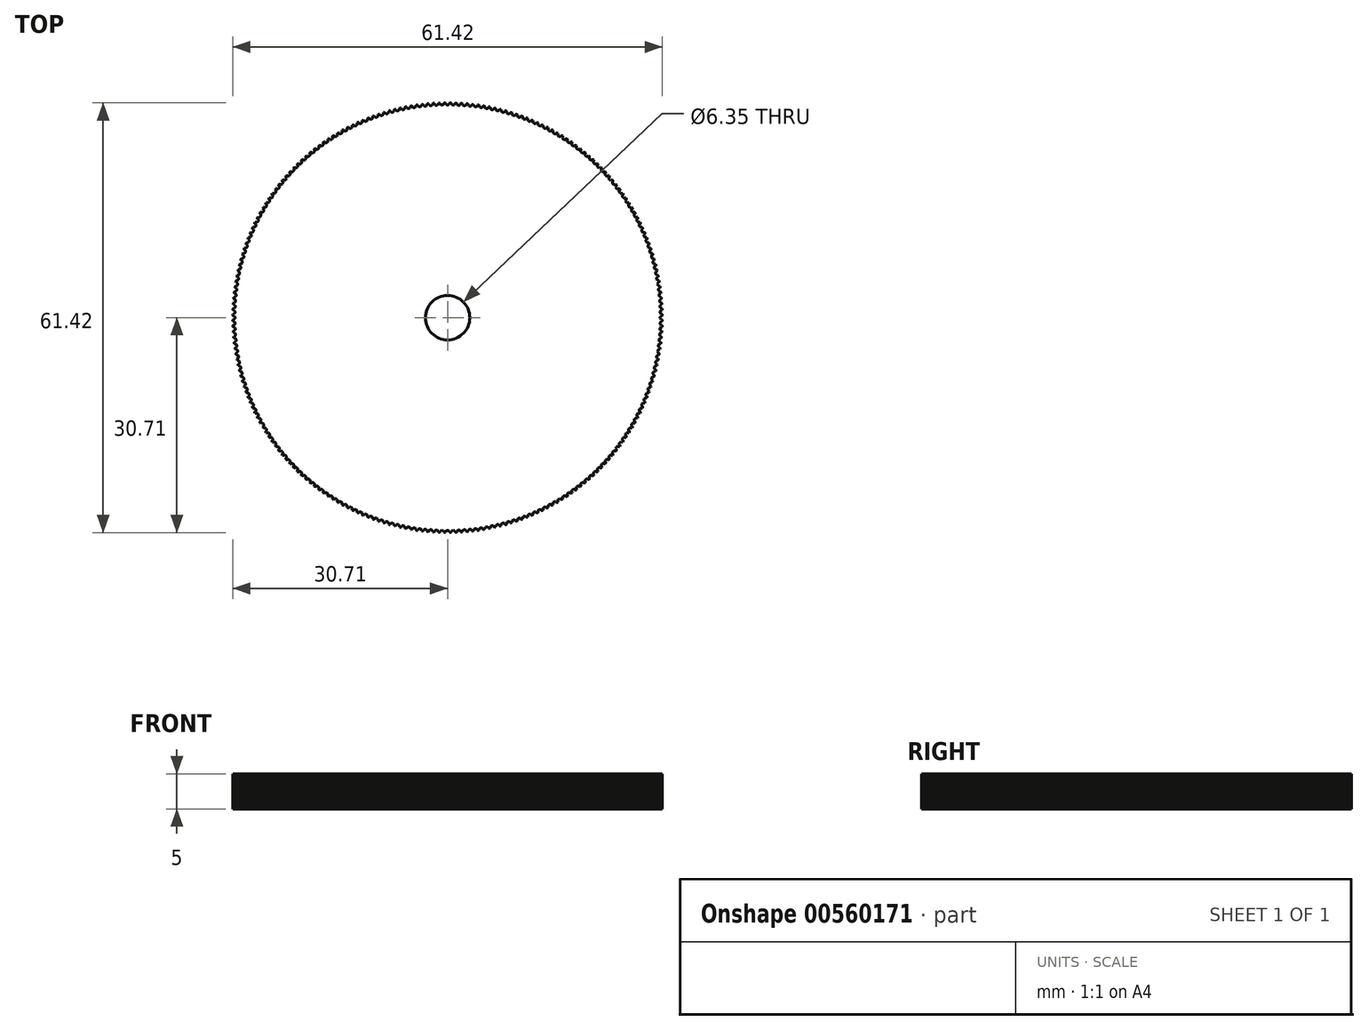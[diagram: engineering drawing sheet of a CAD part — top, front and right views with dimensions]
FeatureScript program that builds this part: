
annotation { "Feature Type Name" : "Feature", "Feature Type Description" : "" }
export const myFeature = defineFeature(function(context is Context, id is Id, definition is map)
    precondition{}
    {
        {
            var Q0;
            Q0=qCreatedBy(makeId("Top.planeOp"),FACE);
            var sketch = newSketch(context, id + "F0", { "sketchPlane" : qUnion([Q0])});
            skLineSegment(sketch, "E0", {"start": v(0.34, -30.7) * mm, "end": v(0.46, -30.7) * mm});
            skLineSegment(sketch, "E1", {"start": v(0.46, -30.7) * mm, "end": v(0.5, -30.7) * mm});
            skLineSegment(sketch, "E2", {"start": v(0.5, -30.7) * mm, "end": v(0.53, -30.65) * mm});
            skLineSegment(sketch, "E3", {"start": v(0.53, -30.65) * mm, "end": v(0.54, -30.6) * mm});
            skLineSegment(sketch, "E4", {"start": v(0.54, -30.6) * mm, "end": v(0.55, -30.57) * mm});
            skLineSegment(sketch, "E5", {"start": v(0.55, -30.57) * mm, "end": v(0.57, -30.53) * mm});
            skLineSegment(sketch, "E6", {"start": v(0.57, -30.53) * mm, "end": v(0.6, -30.49) * mm});
            skLineSegment(sketch, "E7", {"start": v(0.6, -30.49) * mm, "end": v(0.63, -30.45) * mm});
            skLineSegment(sketch, "E8", {"start": v(0.63, -30.45) * mm, "end": v(0.68, -30.42) * mm});
            skLineSegment(sketch, "E9", {"start": v(0.68, -30.42) * mm, "end": v(0.74, -30.4) * mm});
            skLineSegment(sketch, "E10", {"start": v(0.74, -30.4) * mm, "end": v(0.8, -30.39) * mm});
            skLineSegment(sketch, "E11", {"start": v(0.8, -30.39) * mm, "end": v(0.85, -30.4) * mm});
            skLineSegment(sketch, "E12", {"start": v(0.85, -30.4) * mm, "end": v(0.9, -30.4) * mm});
            skLineSegment(sketch, "E13", {"start": v(0.9, -30.4) * mm, "end": v(0.96, -30.44) * mm});
            skLineSegment(sketch, "E14", {"start": v(0.96, -30.44) * mm, "end": v(1, -30.48) * mm});
            skLineSegment(sketch, "E15", {"start": v(1, -30.48) * mm, "end": v(1.03, -30.51) * mm});
            skLineSegment(sketch, "E16", {"start": v(1.03, -30.51) * mm, "end": v(1.05, -30.55) * mm});
            skLineSegment(sketch, "E17", {"start": v(1.05, -30.55) * mm, "end": v(1.07, -30.6) * mm});
            skLineSegment(sketch, "E18", {"start": v(1.07, -30.6) * mm, "end": v(1.08, -30.64) * mm});
            skLineSegment(sketch, "E19", {"start": v(1.08, -30.64) * mm, "end": v(1.1, -30.68) * mm});
            skLineSegment(sketch, "E20", {"start": v(1.1, -30.68) * mm, "end": v(1.15, -30.69) * mm});
            skLineSegment(sketch, "E21", {"start": v(1.15, -30.69) * mm, "end": v(1.27, -30.68) * mm});
            skLineSegment(sketch, "E22", {"start": v(1.27, -30.68) * mm, "end": v(1.31, -30.67) * mm});
            skLineSegment(sketch, "E23", {"start": v(1.31, -30.67) * mm, "end": v(1.33, -30.63) * mm});
            skLineSegment(sketch, "E24", {"start": v(1.33, -30.63) * mm, "end": v(1.34, -30.58) * mm});
            skLineSegment(sketch, "E25", {"start": v(1.34, -30.58) * mm, "end": v(1.35, -30.54) * mm});
            skLineSegment(sketch, "E26", {"start": v(1.35, -30.54) * mm, "end": v(1.37, -30.5) * mm});
            skLineSegment(sketch, "E27", {"start": v(1.37, -30.5) * mm, "end": v(1.39, -30.46) * mm});
            skLineSegment(sketch, "E28", {"start": v(1.39, -30.46) * mm, "end": v(1.43, -30.42) * mm});
            skLineSegment(sketch, "E29", {"start": v(1.43, -30.42) * mm, "end": v(1.48, -30.39) * mm});
            skLineSegment(sketch, "E30", {"start": v(1.48, -30.39) * mm, "end": v(1.53, -30.37) * mm});
            skLineSegment(sketch, "E31", {"start": v(1.53, -30.37) * mm, "end": v(1.6, -30.36) * mm});
            skLineSegment(sketch, "E32", {"start": v(1.6, -30.36) * mm, "end": v(1.65, -30.36) * mm});
            skLineSegment(sketch, "E33", {"start": v(1.65, -30.36) * mm, "end": v(1.7, -30.38) * mm});
            skLineSegment(sketch, "E34", {"start": v(1.7, -30.38) * mm, "end": v(1.76, -30.4) * mm});
            skLineSegment(sketch, "E35", {"start": v(1.76, -30.4) * mm, "end": v(1.8, -30.44) * mm});
            skLineSegment(sketch, "E36", {"start": v(1.8, -30.44) * mm, "end": v(1.83, -30.48) * mm});
            skLineSegment(sketch, "E37", {"start": v(1.83, -30.48) * mm, "end": v(1.85, -30.52) * mm});
            skLineSegment(sketch, "E38", {"start": v(1.85, -30.52) * mm, "end": v(1.87, -30.56) * mm});
            skLineSegment(sketch, "E39", {"start": v(1.87, -30.56) * mm, "end": v(1.88, -30.6) * mm});
            skLineSegment(sketch, "E40", {"start": v(1.88, -30.6) * mm, "end": v(1.9, -30.64) * mm});
            skLineSegment(sketch, "E41", {"start": v(1.9, -30.64) * mm, "end": v(1.95, -30.65) * mm});
            skLineSegment(sketch, "E42", {"start": v(1.95, -30.65) * mm, "end": v(2.07, -30.64) * mm});
            skLineSegment(sketch, "E43", {"start": v(2.07, -30.64) * mm, "end": v(2.11, -30.62) * mm});
            skLineSegment(sketch, "E44", {"start": v(2.11, -30.62) * mm, "end": v(2.13, -30.58) * mm});
            skLineSegment(sketch, "E45", {"start": v(2.13, -30.58) * mm, "end": v(2.14, -30.54) * mm});
            skLineSegment(sketch, "E46", {"start": v(2.14, -30.54) * mm, "end": v(2.15, -30.5) * mm});
            skLineSegment(sketch, "E47", {"start": v(2.15, -30.5) * mm, "end": v(2.17, -30.45) * mm});
            skLineSegment(sketch, "E48", {"start": v(2.17, -30.45) * mm, "end": v(2.19, -30.41) * mm});
            skLineSegment(sketch, "E49", {"start": v(2.19, -30.41) * mm, "end": v(2.23, -30.37) * mm});
            skLineSegment(sketch, "E50", {"start": v(2.23, -30.37) * mm, "end": v(2.27, -30.34) * mm});
            skLineSegment(sketch, "E51", {"start": v(2.27, -30.34) * mm, "end": v(2.33, -30.32) * mm});
            skLineSegment(sketch, "E52", {"start": v(2.33, -30.32) * mm, "end": v(2.39, -30.3) * mm});
            skLineSegment(sketch, "E53", {"start": v(2.39, -30.3) * mm, "end": v(2.44, -30.3) * mm});
            skLineSegment(sketch, "E54", {"start": v(2.44, -30.3) * mm, "end": v(2.5, -30.32) * mm});
            skLineSegment(sketch, "E55", {"start": v(2.5, -30.32) * mm, "end": v(2.55, -30.34) * mm});
            skLineSegment(sketch, "E56", {"start": v(2.55, -30.34) * mm, "end": v(2.6, -30.38) * mm});
            skLineSegment(sketch, "E57", {"start": v(2.6, -30.38) * mm, "end": v(2.63, -30.42) * mm});
            skLineSegment(sketch, "E58", {"start": v(2.63, -30.42) * mm, "end": v(2.65, -30.46) * mm});
            skLineSegment(sketch, "E59", {"start": v(2.65, -30.46) * mm, "end": v(2.67, -30.5) * mm});
            skLineSegment(sketch, "E60", {"start": v(2.67, -30.5) * mm, "end": v(2.68, -30.54) * mm});
            skLineSegment(sketch, "E61", {"start": v(2.68, -30.54) * mm, "end": v(2.7, -30.58) * mm});
            skLineSegment(sketch, "E62", {"start": v(2.7, -30.58) * mm, "end": v(2.75, -30.59) * mm});
            skLineSegment(sketch, "E63", {"start": v(2.75, -30.59) * mm, "end": v(2.87, -30.58) * mm});
            skLineSegment(sketch, "E64", {"start": v(2.87, -30.58) * mm, "end": v(2.91, -30.56) * mm});
            skLineSegment(sketch, "E65", {"start": v(2.91, -30.56) * mm, "end": v(2.93, -30.52) * mm});
            skLineSegment(sketch, "E66", {"start": v(2.93, -30.52) * mm, "end": v(2.94, -30.47) * mm});
            skLineSegment(sketch, "E67", {"start": v(2.94, -30.47) * mm, "end": v(2.95, -30.43) * mm});
            skLineSegment(sketch, "E68", {"start": v(2.95, -30.43) * mm, "end": v(2.96, -30.39) * mm});
            skLineSegment(sketch, "E69", {"start": v(2.96, -30.39) * mm, "end": v(2.98, -30.35) * mm});
            skLineSegment(sketch, "E70", {"start": v(2.98, -30.35) * mm, "end": v(3.02, -30.3) * mm});
            skLineSegment(sketch, "E71", {"start": v(3.02, -30.3) * mm, "end": v(3.07, -30.27) * mm});
            skLineSegment(sketch, "E72", {"start": v(3.07, -30.27) * mm, "end": v(3.12, -30.25) * mm});
            skLineSegment(sketch, "E73", {"start": v(3.12, -30.25) * mm, "end": v(3.18, -30.23) * mm});
            skLineSegment(sketch, "E74", {"start": v(3.18, -30.23) * mm, "end": v(3.24, -30.23) * mm});
            skLineSegment(sketch, "E75", {"start": v(3.24, -30.23) * mm, "end": v(3.3, -30.24) * mm});
            skLineSegment(sketch, "E76", {"start": v(3.3, -30.24) * mm, "end": v(3.35, -30.27) * mm});
            skLineSegment(sketch, "E77", {"start": v(3.35, -30.27) * mm, "end": v(3.4, -30.3) * mm});
            skLineSegment(sketch, "E78", {"start": v(3.4, -30.3) * mm, "end": v(3.42, -30.34) * mm});
            skLineSegment(sketch, "E79", {"start": v(3.42, -30.34) * mm, "end": v(3.44, -30.38) * mm});
            skLineSegment(sketch, "E80", {"start": v(3.44, -30.38) * mm, "end": v(3.46, -30.42) * mm});
            skLineSegment(sketch, "E81", {"start": v(3.46, -30.42) * mm, "end": v(3.48, -30.46) * mm});
            skLineSegment(sketch, "E82", {"start": v(3.48, -30.46) * mm, "end": v(3.5, -30.5) * mm});
            skLineSegment(sketch, "E83", {"start": v(3.5, -30.5) * mm, "end": v(3.55, -30.5) * mm});
            skLineSegment(sketch, "E84", {"start": v(3.55, -30.5) * mm, "end": v(3.67, -30.5) * mm});
            skLineSegment(sketch, "E85", {"start": v(3.67, -30.5) * mm, "end": v(3.71, -30.47) * mm});
            skLineSegment(sketch, "E86", {"start": v(3.71, -30.47) * mm, "end": v(3.73, -30.43) * mm});
            skLineSegment(sketch, "E87", {"start": v(3.73, -30.43) * mm, "end": v(3.73, -30.39) * mm});
            skLineSegment(sketch, "E88", {"start": v(3.73, -30.39) * mm, "end": v(3.74, -30.34) * mm});
            skLineSegment(sketch, "E89", {"start": v(3.74, -30.34) * mm, "end": v(3.76, -30.3) * mm});
            skLineSegment(sketch, "E90", {"start": v(3.76, -30.3) * mm, "end": v(3.78, -30.26) * mm});
            skLineSegment(sketch, "E91", {"start": v(3.78, -30.26) * mm, "end": v(3.81, -30.21) * mm});
            skLineSegment(sketch, "E92", {"start": v(3.81, -30.21) * mm, "end": v(3.86, -30.18) * mm});
            skLineSegment(sketch, "E93", {"start": v(3.86, -30.18) * mm, "end": v(3.91, -30.15) * mm});
            skLineSegment(sketch, "E94", {"start": v(3.91, -30.15) * mm, "end": v(3.97, -30.14) * mm});
            skLineSegment(sketch, "E95", {"start": v(3.97, -30.14) * mm, "end": v(4.03, -30.14) * mm});
            skLineSegment(sketch, "E96", {"start": v(4.03, -30.14) * mm, "end": v(4.08, -30.15) * mm});
            skLineSegment(sketch, "E97", {"start": v(4.08, -30.15) * mm, "end": v(4.14, -30.17) * mm});
            skLineSegment(sketch, "E98", {"start": v(4.14, -30.17) * mm, "end": v(4.18, -30.2) * mm});
            skLineSegment(sketch, "E99", {"start": v(4.18, -30.2) * mm, "end": v(4.21, -30.24) * mm});
            skLineSegment(sketch, "E100", {"start": v(4.21, -30.24) * mm, "end": v(4.24, -30.28) * mm});
            skLineSegment(sketch, "E101", {"start": v(4.24, -30.28) * mm, "end": v(4.26, -30.32) * mm});
            skLineSegment(sketch, "E102", {"start": v(4.26, -30.32) * mm, "end": v(4.27, -30.36) * mm});
            skLineSegment(sketch, "E103", {"start": v(4.27, -30.36) * mm, "end": v(4.3, -30.4) * mm});
            skLineSegment(sketch, "E104", {"start": v(4.3, -30.4) * mm, "end": v(4.35, -30.4) * mm});
            skLineSegment(sketch, "E105", {"start": v(4.35, -30.4) * mm, "end": v(4.47, -30.38) * mm});
            skLineSegment(sketch, "E106", {"start": v(4.47, -30.38) * mm, "end": v(4.5, -30.36) * mm});
            skLineSegment(sketch, "E107", {"start": v(4.5, -30.36) * mm, "end": v(4.53, -30.32) * mm});
            skLineSegment(sketch, "E108", {"start": v(4.53, -30.32) * mm, "end": v(4.53, -30.28) * mm});
            skLineSegment(sketch, "E109", {"start": v(4.53, -30.28) * mm, "end": v(4.54, -30.23) * mm});
            skLineSegment(sketch, "E110", {"start": v(4.54, -30.23) * mm, "end": v(4.55, -30.19) * mm});
            skLineSegment(sketch, "E111", {"start": v(4.55, -30.19) * mm, "end": v(4.57, -30.15) * mm});
            skLineSegment(sketch, "E112", {"start": v(4.57, -30.15) * mm, "end": v(4.6, -30.1) * mm});
            skLineSegment(sketch, "E113", {"start": v(4.6, -30.1) * mm, "end": v(4.65, -30.07) * mm});
            skLineSegment(sketch, "E114", {"start": v(4.65, -30.07) * mm, "end": v(4.7, -30.04) * mm});
            skLineSegment(sketch, "E115", {"start": v(4.7, -30.04) * mm, "end": v(4.76, -30.03) * mm});
            skLineSegment(sketch, "E116", {"start": v(4.76, -30.03) * mm, "end": v(4.81, -30.02) * mm});
            skLineSegment(sketch, "E117", {"start": v(4.81, -30.02) * mm, "end": v(4.87, -30.03) * mm});
            skLineSegment(sketch, "E118", {"start": v(4.87, -30.03) * mm, "end": v(4.93, -30.05) * mm});
            skLineSegment(sketch, "E119", {"start": v(4.93, -30.05) * mm, "end": v(4.97, -30.08) * mm});
            skLineSegment(sketch, "E120", {"start": v(4.97, -30.08) * mm, "end": v(5, -30.12) * mm});
            skLineSegment(sketch, "E121", {"start": v(5, -30.12) * mm, "end": v(5.03, -30.15) * mm});
            skLineSegment(sketch, "E122", {"start": v(5.03, -30.15) * mm, "end": v(5.05, -30.2) * mm});
            skLineSegment(sketch, "E123", {"start": v(5.05, -30.2) * mm, "end": v(5.07, -30.24) * mm});
            skLineSegment(sketch, "E124", {"start": v(5.07, -30.24) * mm, "end": v(5.1, -30.27) * mm});
            skLineSegment(sketch, "E125", {"start": v(5.1, -30.27) * mm, "end": v(5.14, -30.28) * mm});
            skLineSegment(sketch, "E126", {"start": v(5.14, -30.28) * mm, "end": v(5.26, -30.26) * mm});
            skLineSegment(sketch, "E127", {"start": v(5.26, -30.26) * mm, "end": v(5.3, -30.23) * mm});
            skLineSegment(sketch, "E128", {"start": v(5.3, -30.23) * mm, "end": v(5.32, -30.2) * mm});
            skLineSegment(sketch, "E129", {"start": v(5.32, -30.2) * mm, "end": v(5.32, -30.15) * mm});
            skLineSegment(sketch, "E130", {"start": v(5.32, -30.15) * mm, "end": v(5.32, -30.1) * mm});
            skLineSegment(sketch, "E131", {"start": v(5.32, -30.1) * mm, "end": v(5.34, -30.06) * mm});
            skLineSegment(sketch, "E132", {"start": v(5.34, -30.06) * mm, "end": v(5.35, -30.02) * mm});
            skLineSegment(sketch, "E133", {"start": v(5.35, -30.02) * mm, "end": v(5.39, -29.97) * mm});
            skLineSegment(sketch, "E134", {"start": v(5.39, -29.97) * mm, "end": v(5.43, -29.93) * mm});
            skLineSegment(sketch, "E135", {"start": v(5.43, -29.93) * mm, "end": v(5.48, -29.9) * mm});
            skLineSegment(sketch, "E136", {"start": v(5.48, -29.9) * mm, "end": v(5.54, -29.9) * mm});
            skLineSegment(sketch, "E137", {"start": v(5.54, -29.9) * mm, "end": v(5.6, -29.89) * mm});
            skLineSegment(sketch, "E138", {"start": v(5.6, -29.89) * mm, "end": v(5.66, -29.9) * mm});
            skLineSegment(sketch, "E139", {"start": v(5.66, -29.9) * mm, "end": v(5.71, -29.91) * mm});
            skLineSegment(sketch, "E140", {"start": v(5.71, -29.91) * mm, "end": v(5.76, -29.94) * mm});
            skLineSegment(sketch, "E141", {"start": v(5.76, -29.94) * mm, "end": v(5.8, -29.98) * mm});
            skLineSegment(sketch, "E142", {"start": v(5.8, -29.98) * mm, "end": v(5.82, -30.01) * mm});
            skLineSegment(sketch, "E143", {"start": v(5.82, -30.01) * mm, "end": v(5.84, -30.05) * mm});
            skLineSegment(sketch, "E144", {"start": v(5.84, -30.05) * mm, "end": v(5.86, -30.1) * mm});
            skLineSegment(sketch, "E145", {"start": v(5.86, -30.1) * mm, "end": v(5.88, -30.13) * mm});
            skLineSegment(sketch, "E146", {"start": v(5.88, -30.13) * mm, "end": v(5.93, -30.13) * mm});
            skLineSegment(sketch, "E147", {"start": v(5.93, -30.13) * mm, "end": v(6.05, -30.1) * mm});
            skLineSegment(sketch, "E148", {"start": v(6.05, -30.1) * mm, "end": v(6.1, -30.08) * mm});
            skLineSegment(sketch, "E149", {"start": v(6.1, -30.08) * mm, "end": v(6.1, -30.04) * mm});
            skLineSegment(sketch, "E150", {"start": v(6.1, -30.04) * mm, "end": v(6.1, -30) * mm});
            skLineSegment(sketch, "E151", {"start": v(6.1, -30) * mm, "end": v(6.11, -29.95) * mm});
            skLineSegment(sketch, "E152", {"start": v(6.11, -29.95) * mm, "end": v(6.12, -29.91) * mm});
            skLineSegment(sketch, "E153", {"start": v(6.12, -29.91) * mm, "end": v(6.14, -29.87) * mm});
            skLineSegment(sketch, "E154", {"start": v(6.14, -29.87) * mm, "end": v(6.17, -29.82) * mm});
            skLineSegment(sketch, "E155", {"start": v(6.17, -29.82) * mm, "end": v(6.21, -29.78) * mm});
            skLineSegment(sketch, "E156", {"start": v(6.21, -29.78) * mm, "end": v(6.26, -29.75) * mm});
            skLineSegment(sketch, "E157", {"start": v(6.26, -29.75) * mm, "end": v(6.32, -29.74) * mm});
            skLineSegment(sketch, "E158", {"start": v(6.32, -29.74) * mm, "end": v(6.38, -29.73) * mm});
            skLineSegment(sketch, "E159", {"start": v(6.38, -29.73) * mm, "end": v(6.44, -29.73) * mm});
            skLineSegment(sketch, "E160", {"start": v(6.44, -29.73) * mm, "end": v(6.5, -29.75) * mm});
            skLineSegment(sketch, "E161", {"start": v(6.5, -29.75) * mm, "end": v(6.54, -29.78) * mm});
            skLineSegment(sketch, "E162", {"start": v(6.54, -29.78) * mm, "end": v(6.57, -29.81) * mm});
            skLineSegment(sketch, "E163", {"start": v(6.57, -29.81) * mm, "end": v(6.6, -29.85) * mm});
            skLineSegment(sketch, "E164", {"start": v(6.6, -29.85) * mm, "end": v(6.62, -29.89) * mm});
            skLineSegment(sketch, "E165", {"start": v(6.62, -29.89) * mm, "end": v(6.64, -29.93) * mm});
            skLineSegment(sketch, "E166", {"start": v(6.64, -29.93) * mm, "end": v(6.67, -29.96) * mm});
            skLineSegment(sketch, "E167", {"start": v(6.67, -29.96) * mm, "end": v(6.72, -29.97) * mm});
            skLineSegment(sketch, "E168", {"start": v(6.72, -29.97) * mm, "end": v(6.84, -29.94) * mm});
            skLineSegment(sketch, "E169", {"start": v(6.84, -29.94) * mm, "end": v(6.88, -29.91) * mm});
            skLineSegment(sketch, "E170", {"start": v(6.88, -29.91) * mm, "end": v(6.9, -29.87) * mm});
            skLineSegment(sketch, "E171", {"start": v(6.9, -29.87) * mm, "end": v(6.89, -29.83) * mm});
            skLineSegment(sketch, "E172", {"start": v(6.89, -29.83) * mm, "end": v(6.9, -29.78) * mm});
            skLineSegment(sketch, "E173", {"start": v(6.9, -29.78) * mm, "end": v(6.9, -29.74) * mm});
            skLineSegment(sketch, "E174", {"start": v(6.9, -29.74) * mm, "end": v(6.92, -29.7) * mm});
            skLineSegment(sketch, "E175", {"start": v(6.92, -29.7) * mm, "end": v(6.95, -29.65) * mm});
            skLineSegment(sketch, "E176", {"start": v(6.95, -29.65) * mm, "end": v(7, -29.6) * mm});
            skLineSegment(sketch, "E177", {"start": v(7, -29.6) * mm, "end": v(7.04, -29.58) * mm});
            skLineSegment(sketch, "E178", {"start": v(7.04, -29.58) * mm, "end": v(7.1, -29.56) * mm});
            skLineSegment(sketch, "E179", {"start": v(7.1, -29.56) * mm, "end": v(7.15, -29.55) * mm});
            skLineSegment(sketch, "E180", {"start": v(7.15, -29.55) * mm, "end": v(7.21, -29.56) * mm});
            skLineSegment(sketch, "E181", {"start": v(7.21, -29.56) * mm, "end": v(7.27, -29.57) * mm});
            skLineSegment(sketch, "E182", {"start": v(7.27, -29.57) * mm, "end": v(7.32, -29.6) * mm});
            skLineSegment(sketch, "E183", {"start": v(7.32, -29.6) * mm, "end": v(7.35, -29.63) * mm});
            skLineSegment(sketch, "E184", {"start": v(7.35, -29.63) * mm, "end": v(7.38, -29.67) * mm});
            skLineSegment(sketch, "E185", {"start": v(7.38, -29.67) * mm, "end": v(7.4, -29.7) * mm});
            skLineSegment(sketch, "E186", {"start": v(7.4, -29.7) * mm, "end": v(7.42, -29.75) * mm});
            skLineSegment(sketch, "E187", {"start": v(7.42, -29.75) * mm, "end": v(7.45, -29.78) * mm});
            skLineSegment(sketch, "E188", {"start": v(7.45, -29.78) * mm, "end": v(7.5, -29.78) * mm});
            skLineSegment(sketch, "E189", {"start": v(7.5, -29.78) * mm, "end": v(7.62, -29.75) * mm});
            skLineSegment(sketch, "E190", {"start": v(7.62, -29.75) * mm, "end": v(7.66, -29.72) * mm});
            skLineSegment(sketch, "E191", {"start": v(7.66, -29.72) * mm, "end": v(7.67, -29.68) * mm});
            skLineSegment(sketch, "E192", {"start": v(7.67, -29.68) * mm, "end": v(7.67, -29.64) * mm});
            skLineSegment(sketch, "E193", {"start": v(7.67, -29.64) * mm, "end": v(7.67, -29.6) * mm});
            skLineSegment(sketch, "E194", {"start": v(7.67, -29.6) * mm, "end": v(7.68, -29.55) * mm});
            skLineSegment(sketch, "E195", {"start": v(7.68, -29.55) * mm, "end": v(7.7, -29.5) * mm});
            skLineSegment(sketch, "E196", {"start": v(7.7, -29.5) * mm, "end": v(7.72, -29.46) * mm});
            skLineSegment(sketch, "E197", {"start": v(7.72, -29.46) * mm, "end": v(7.76, -29.42) * mm});
            skLineSegment(sketch, "E198", {"start": v(7.76, -29.42) * mm, "end": v(7.81, -29.39) * mm});
            skLineSegment(sketch, "E199", {"start": v(7.81, -29.39) * mm, "end": v(7.87, -29.36) * mm});
            skLineSegment(sketch, "E200", {"start": v(7.87, -29.36) * mm, "end": v(7.93, -29.35) * mm});
            skLineSegment(sketch, "E201", {"start": v(7.93, -29.35) * mm, "end": v(7.98, -29.36) * mm});
            skLineSegment(sketch, "E202", {"start": v(7.98, -29.36) * mm, "end": v(8.04, -29.37) * mm});
            skLineSegment(sketch, "E203", {"start": v(8.04, -29.37) * mm, "end": v(8.1, -29.4) * mm});
            skLineSegment(sketch, "E204", {"start": v(8.1, -29.4) * mm, "end": v(8.12, -29.43) * mm});
            skLineSegment(sketch, "E205", {"start": v(8.12, -29.43) * mm, "end": v(8.15, -29.46) * mm});
            skLineSegment(sketch, "E206", {"start": v(8.15, -29.46) * mm, "end": v(8.18, -29.5) * mm});
            skLineSegment(sketch, "E207", {"start": v(8.18, -29.5) * mm, "end": v(8.2, -29.54) * mm});
            skLineSegment(sketch, "E208", {"start": v(8.2, -29.54) * mm, "end": v(8.23, -29.57) * mm});
            skLineSegment(sketch, "E209", {"start": v(8.23, -29.57) * mm, "end": v(8.28, -29.57) * mm});
            skLineSegment(sketch, "E210", {"start": v(8.28, -29.57) * mm, "end": v(8.4, -29.54) * mm});
            skLineSegment(sketch, "E211", {"start": v(8.4, -29.54) * mm, "end": v(8.43, -29.51) * mm});
            skLineSegment(sketch, "E212", {"start": v(8.43, -29.51) * mm, "end": v(8.44, -29.47) * mm});
            skLineSegment(sketch, "E213", {"start": v(8.44, -29.47) * mm, "end": v(8.44, -29.43) * mm});
            skLineSegment(sketch, "E214", {"start": v(8.44, -29.43) * mm, "end": v(8.44, -29.38) * mm});
            skLineSegment(sketch, "E215", {"start": v(8.44, -29.38) * mm, "end": v(8.45, -29.34) * mm});
            skLineSegment(sketch, "E216", {"start": v(8.45, -29.34) * mm, "end": v(8.46, -29.3) * mm});
            skLineSegment(sketch, "E217", {"start": v(8.46, -29.3) * mm, "end": v(8.5, -29.24) * mm});
            skLineSegment(sketch, "E218", {"start": v(8.5, -29.24) * mm, "end": v(8.53, -29.2) * mm});
            skLineSegment(sketch, "E219", {"start": v(8.53, -29.2) * mm, "end": v(8.58, -29.17) * mm});
            skLineSegment(sketch, "E220", {"start": v(8.58, -29.17) * mm, "end": v(8.63, -29.15) * mm});
            skLineSegment(sketch, "E221", {"start": v(8.63, -29.15) * mm, "end": v(8.7, -29.14) * mm});
            skLineSegment(sketch, "E222", {"start": v(8.7, -29.14) * mm, "end": v(8.75, -29.14) * mm});
            skLineSegment(sketch, "E223", {"start": v(8.75, -29.14) * mm, "end": v(8.8, -29.15) * mm});
            skLineSegment(sketch, "E224", {"start": v(8.8, -29.15) * mm, "end": v(8.86, -29.18) * mm});
            skLineSegment(sketch, "E225", {"start": v(8.86, -29.18) * mm, "end": v(8.9, -29.2) * mm});
            skLineSegment(sketch, "E226", {"start": v(8.9, -29.2) * mm, "end": v(8.92, -29.24) * mm});
            skLineSegment(sketch, "E227", {"start": v(8.92, -29.24) * mm, "end": v(8.95, -29.28) * mm});
            skLineSegment(sketch, "E228", {"start": v(8.95, -29.28) * mm, "end": v(8.97, -29.32) * mm});
            skLineSegment(sketch, "E229", {"start": v(8.97, -29.32) * mm, "end": v(9, -29.35) * mm});
            skLineSegment(sketch, "E230", {"start": v(9, -29.35) * mm, "end": v(9.05, -29.35) * mm});
            skLineSegment(sketch, "E231", {"start": v(9.05, -29.35) * mm, "end": v(9.16, -29.31) * mm});
            skLineSegment(sketch, "E232", {"start": v(9.16, -29.31) * mm, "end": v(9.2, -29.28) * mm});
            skLineSegment(sketch, "E233", {"start": v(9.2, -29.28) * mm, "end": v(9.21, -29.24) * mm});
            skLineSegment(sketch, "E234", {"start": v(9.21, -29.24) * mm, "end": v(9.2, -29.2) * mm});
            skLineSegment(sketch, "E235", {"start": v(9.2, -29.2) * mm, "end": v(9.2, -29.15) * mm});
            skLineSegment(sketch, "E236", {"start": v(9.2, -29.15) * mm, "end": v(9.21, -29.1) * mm});
            skLineSegment(sketch, "E237", {"start": v(9.21, -29.1) * mm, "end": v(9.23, -29.06) * mm});
            skLineSegment(sketch, "E238", {"start": v(9.23, -29.06) * mm, "end": v(9.25, -29.01) * mm});
            skLineSegment(sketch, "E239", {"start": v(9.25, -29.01) * mm, "end": v(9.3, -28.97) * mm});
            skLineSegment(sketch, "E240", {"start": v(9.3, -28.97) * mm, "end": v(9.34, -28.94) * mm});
            skLineSegment(sketch, "E241", {"start": v(9.34, -28.94) * mm, "end": v(9.4, -28.91) * mm});
            skLineSegment(sketch, "E242", {"start": v(9.4, -28.91) * mm, "end": v(9.45, -28.9) * mm});
            skLineSegment(sketch, "E243", {"start": v(9.45, -28.9) * mm, "end": v(9.5, -28.9) * mm});
            skLineSegment(sketch, "E244", {"start": v(9.5, -28.9) * mm, "end": v(9.57, -28.91) * mm});
            skLineSegment(sketch, "E245", {"start": v(9.57, -28.91) * mm, "end": v(9.62, -28.93) * mm});
            skLineSegment(sketch, "E246", {"start": v(9.62, -28.93) * mm, "end": v(9.65, -28.96) * mm});
            skLineSegment(sketch, "E247", {"start": v(9.65, -28.96) * mm, "end": v(9.68, -29) * mm});
            skLineSegment(sketch, "E248", {"start": v(9.68, -29) * mm, "end": v(9.71, -29.03) * mm});
            skLineSegment(sketch, "E249", {"start": v(9.71, -29.03) * mm, "end": v(9.73, -29.07) * mm});
            skLineSegment(sketch, "E250", {"start": v(9.73, -29.07) * mm, "end": v(9.77, -29.1) * mm});
            skLineSegment(sketch, "E251", {"start": v(9.77, -29.1) * mm, "end": v(9.81, -29.1) * mm});
            skLineSegment(sketch, "E252", {"start": v(9.81, -29.1) * mm, "end": v(9.93, -29.06) * mm});
            skLineSegment(sketch, "E253", {"start": v(9.93, -29.06) * mm, "end": v(9.97, -29.03) * mm});
            skLineSegment(sketch, "E254", {"start": v(9.97, -29.03) * mm, "end": v(9.98, -28.99) * mm});
            skLineSegment(sketch, "E255", {"start": v(9.98, -28.99) * mm, "end": v(9.97, -28.94) * mm});
            skLineSegment(sketch, "E256", {"start": v(9.97, -28.94) * mm, "end": v(9.97, -28.9) * mm});
            skLineSegment(sketch, "E257", {"start": v(9.97, -28.9) * mm, "end": v(9.97, -28.86) * mm});
            skLineSegment(sketch, "E258", {"start": v(9.97, -28.86) * mm, "end": v(9.98, -28.81) * mm});
            skLineSegment(sketch, "E259", {"start": v(9.98, -28.81) * mm, "end": v(10.01, -28.76) * mm});
            skLineSegment(sketch, "E260", {"start": v(10.01, -28.76) * mm, "end": v(10.05, -28.72) * mm});
            skLineSegment(sketch, "E261", {"start": v(10.05, -28.72) * mm, "end": v(10.1, -28.68) * mm});
            skLineSegment(sketch, "E262", {"start": v(10.1, -28.68) * mm, "end": v(10.15, -28.66) * mm});
            skLineSegment(sketch, "E263", {"start": v(10.15, -28.66) * mm, "end": v(10.2, -28.64) * mm});
            skLineSegment(sketch, "E264", {"start": v(10.2, -28.64) * mm, "end": v(10.26, -28.64) * mm});
            skLineSegment(sketch, "E265", {"start": v(10.26, -28.64) * mm, "end": v(10.32, -28.65) * mm});
            skLineSegment(sketch, "E266", {"start": v(10.32, -28.65) * mm, "end": v(10.37, -28.67) * mm});
            skLineSegment(sketch, "E267", {"start": v(10.37, -28.67) * mm, "end": v(10.4, -28.7) * mm});
            skLineSegment(sketch, "E268", {"start": v(10.4, -28.7) * mm, "end": v(10.44, -28.73) * mm});
            skLineSegment(sketch, "E269", {"start": v(10.44, -28.73) * mm, "end": v(10.47, -28.77) * mm});
            skLineSegment(sketch, "E270", {"start": v(10.47, -28.77) * mm, "end": v(10.5, -28.8) * mm});
            skLineSegment(sketch, "E271", {"start": v(10.5, -28.8) * mm, "end": v(10.53, -28.83) * mm});
            skLineSegment(sketch, "E272", {"start": v(10.53, -28.83) * mm, "end": v(10.57, -28.83) * mm});
            skLineSegment(sketch, "E273", {"start": v(10.57, -28.83) * mm, "end": v(10.69, -28.8) * mm});
            skLineSegment(sketch, "E274", {"start": v(10.69, -28.8) * mm, "end": v(10.72, -28.76) * mm});
            skLineSegment(sketch, "E275", {"start": v(10.72, -28.76) * mm, "end": v(10.73, -28.72) * mm});
            skLineSegment(sketch, "E276", {"start": v(10.73, -28.72) * mm, "end": v(10.72, -28.67) * mm});
            skLineSegment(sketch, "E277", {"start": v(10.72, -28.67) * mm, "end": v(10.72, -28.63) * mm});
            skLineSegment(sketch, "E278", {"start": v(10.72, -28.63) * mm, "end": v(10.73, -28.58) * mm});
            skLineSegment(sketch, "E279", {"start": v(10.73, -28.58) * mm, "end": v(10.73, -28.54) * mm});
            skLineSegment(sketch, "E280", {"start": v(10.73, -28.54) * mm, "end": v(10.76, -28.49) * mm});
            skLineSegment(sketch, "E281", {"start": v(10.76, -28.49) * mm, "end": v(10.8, -28.44) * mm});
            skLineSegment(sketch, "E282", {"start": v(10.8, -28.44) * mm, "end": v(10.84, -28.4) * mm});
            skLineSegment(sketch, "E283", {"start": v(10.84, -28.4) * mm, "end": v(10.9, -28.38) * mm});
            skLineSegment(sketch, "E284", {"start": v(10.9, -28.38) * mm, "end": v(10.95, -28.37) * mm});
            skLineSegment(sketch, "E285", {"start": v(10.95, -28.37) * mm, "end": v(11, -28.36) * mm});
            skLineSegment(sketch, "E286", {"start": v(11, -28.36) * mm, "end": v(11.07, -28.37) * mm});
            skLineSegment(sketch, "E287", {"start": v(11.07, -28.37) * mm, "end": v(11.12, -28.4) * mm});
            skLineSegment(sketch, "E288", {"start": v(11.12, -28.4) * mm, "end": v(11.16, -28.42) * mm});
            skLineSegment(sketch, "E289", {"start": v(11.16, -28.42) * mm, "end": v(11.19, -28.45) * mm});
            skLineSegment(sketch, "E290", {"start": v(11.19, -28.45) * mm, "end": v(11.22, -28.48) * mm});
            skLineSegment(sketch, "E291", {"start": v(11.22, -28.48) * mm, "end": v(11.24, -28.52) * mm});
            skLineSegment(sketch, "E292", {"start": v(11.24, -28.52) * mm, "end": v(11.28, -28.55) * mm});
            skLineSegment(sketch, "E293", {"start": v(11.28, -28.55) * mm, "end": v(11.32, -28.55) * mm});
            skLineSegment(sketch, "E294", {"start": v(11.32, -28.55) * mm, "end": v(11.44, -28.5) * mm});
            skLineSegment(sketch, "E295", {"start": v(11.44, -28.5) * mm, "end": v(11.47, -28.47) * mm});
            skLineSegment(sketch, "E296", {"start": v(11.47, -28.47) * mm, "end": v(11.48, -28.43) * mm});
            skLineSegment(sketch, "E297", {"start": v(11.48, -28.43) * mm, "end": v(11.47, -28.38) * mm});
            skLineSegment(sketch, "E298", {"start": v(11.47, -28.38) * mm, "end": v(11.47, -28.34) * mm});
            skLineSegment(sketch, "E299", {"start": v(11.47, -28.34) * mm, "end": v(11.47, -28.3) * mm});
            skLineSegment(sketch, "E300", {"start": v(11.47, -28.3) * mm, "end": v(11.48, -28.25) * mm});
            skLineSegment(sketch, "E301", {"start": v(11.48, -28.25) * mm, "end": v(11.5, -28.2) * mm});
            skLineSegment(sketch, "E302", {"start": v(11.5, -28.2) * mm, "end": v(11.54, -28.15) * mm});
            skLineSegment(sketch, "E303", {"start": v(11.54, -28.15) * mm, "end": v(11.58, -28.11) * mm});
            skLineSegment(sketch, "E304", {"start": v(11.58, -28.11) * mm, "end": v(11.63, -28.09) * mm});
            skLineSegment(sketch, "E305", {"start": v(11.63, -28.09) * mm, "end": v(11.69, -28.07) * mm});
            skLineSegment(sketch, "E306", {"start": v(11.69, -28.07) * mm, "end": v(11.75, -28.06) * mm});
            skLineSegment(sketch, "E307", {"start": v(11.75, -28.06) * mm, "end": v(11.8, -28.07) * mm});
            skLineSegment(sketch, "E308", {"start": v(11.8, -28.07) * mm, "end": v(11.86, -28.1) * mm});
            skLineSegment(sketch, "E309", {"start": v(11.86, -28.1) * mm, "end": v(11.9, -28.12) * mm});
            skLineSegment(sketch, "E310", {"start": v(11.9, -28.12) * mm, "end": v(11.93, -28.15) * mm});
            skLineSegment(sketch, "E311", {"start": v(11.93, -28.15) * mm, "end": v(11.96, -28.18) * mm});
            skLineSegment(sketch, "E312", {"start": v(11.96, -28.18) * mm, "end": v(11.98, -28.22) * mm});
            skLineSegment(sketch, "E313", {"start": v(11.98, -28.22) * mm, "end": v(12.02, -28.24) * mm});
            skLineSegment(sketch, "E314", {"start": v(12.02, -28.24) * mm, "end": v(12.07, -28.24) * mm});
            skLineSegment(sketch, "E315", {"start": v(12.07, -28.24) * mm, "end": v(12.18, -28.2) * mm});
            skLineSegment(sketch, "E316", {"start": v(12.18, -28.2) * mm, "end": v(12.21, -28.16) * mm});
            skLineSegment(sketch, "E317", {"start": v(12.21, -28.16) * mm, "end": v(12.22, -28.12) * mm});
            skLineSegment(sketch, "E318", {"start": v(12.22, -28.12) * mm, "end": v(12.2, -28.07) * mm});
            skLineSegment(sketch, "E319", {"start": v(12.2, -28.07) * mm, "end": v(12.2, -28.03) * mm});
            skLineSegment(sketch, "E320", {"start": v(12.2, -28.03) * mm, "end": v(12.2, -27.98) * mm});
            skLineSegment(sketch, "E321", {"start": v(12.2, -27.98) * mm, "end": v(12.21, -27.94) * mm});
            skLineSegment(sketch, "E322", {"start": v(12.21, -27.94) * mm, "end": v(12.24, -27.89) * mm});
            skLineSegment(sketch, "E323", {"start": v(12.24, -27.89) * mm, "end": v(12.27, -27.84) * mm});
            skLineSegment(sketch, "E324", {"start": v(12.27, -27.84) * mm, "end": v(12.31, -27.8) * mm});
            skLineSegment(sketch, "E325", {"start": v(12.31, -27.8) * mm, "end": v(12.36, -27.77) * mm});
            skLineSegment(sketch, "E326", {"start": v(12.36, -27.77) * mm, "end": v(12.42, -27.75) * mm});
            skLineSegment(sketch, "E327", {"start": v(12.42, -27.75) * mm, "end": v(12.48, -27.75) * mm});
            skLineSegment(sketch, "E328", {"start": v(12.48, -27.75) * mm, "end": v(12.54, -27.75) * mm});
            skLineSegment(sketch, "E329", {"start": v(12.54, -27.75) * mm, "end": v(12.6, -27.77) * mm});
            skLineSegment(sketch, "E330", {"start": v(12.6, -27.77) * mm, "end": v(12.63, -27.8) * mm});
            skLineSegment(sketch, "E331", {"start": v(12.63, -27.8) * mm, "end": v(12.66, -27.83) * mm});
            skLineSegment(sketch, "E332", {"start": v(12.66, -27.83) * mm, "end": v(12.7, -27.86) * mm});
            skLineSegment(sketch, "E333", {"start": v(12.7, -27.86) * mm, "end": v(12.72, -27.9) * mm});
            skLineSegment(sketch, "E334", {"start": v(12.72, -27.9) * mm, "end": v(12.75, -27.92) * mm});
            skLineSegment(sketch, "E335", {"start": v(12.75, -27.92) * mm, "end": v(12.8, -27.91) * mm});
            skLineSegment(sketch, "E336", {"start": v(12.8, -27.91) * mm, "end": v(12.91, -27.86) * mm});
            skLineSegment(sketch, "E337", {"start": v(12.91, -27.86) * mm, "end": v(12.95, -27.83) * mm});
            skLineSegment(sketch, "E338", {"start": v(12.95, -27.83) * mm, "end": v(12.95, -27.79) * mm});
            skLineSegment(sketch, "E339", {"start": v(12.95, -27.79) * mm, "end": v(12.94, -27.74) * mm});
            skLineSegment(sketch, "E340", {"start": v(12.94, -27.74) * mm, "end": v(12.93, -27.7) * mm});
            skLineSegment(sketch, "E341", {"start": v(12.93, -27.7) * mm, "end": v(12.93, -27.65) * mm});
            skLineSegment(sketch, "E342", {"start": v(12.93, -27.65) * mm, "end": v(12.94, -27.6) * mm});
            skLineSegment(sketch, "E343", {"start": v(12.94, -27.6) * mm, "end": v(12.96, -27.56) * mm});
            skLineSegment(sketch, "E344", {"start": v(12.96, -27.56) * mm, "end": v(13, -27.5) * mm});
            skLineSegment(sketch, "E345", {"start": v(13, -27.5) * mm, "end": v(13.04, -27.47) * mm});
            skLineSegment(sketch, "E346", {"start": v(13.04, -27.47) * mm, "end": v(13.09, -27.44) * mm});
            skLineSegment(sketch, "E347", {"start": v(13.09, -27.44) * mm, "end": v(13.14, -27.42) * mm});
            skLineSegment(sketch, "E348", {"start": v(13.14, -27.42) * mm, "end": v(13.2, -27.41) * mm});
            skLineSegment(sketch, "E349", {"start": v(13.2, -27.41) * mm, "end": v(13.26, -27.41) * mm});
            skLineSegment(sketch, "E350", {"start": v(13.26, -27.41) * mm, "end": v(13.31, -27.43) * mm});
            skLineSegment(sketch, "E351", {"start": v(13.31, -27.43) * mm, "end": v(13.35, -27.46) * mm});
            skLineSegment(sketch, "E352", {"start": v(13.35, -27.46) * mm, "end": v(13.39, -27.48) * mm});
            skLineSegment(sketch, "E353", {"start": v(13.39, -27.48) * mm, "end": v(13.42, -27.52) * mm});
            skLineSegment(sketch, "E354", {"start": v(13.42, -27.52) * mm, "end": v(13.44, -27.55) * mm});
            skLineSegment(sketch, "E355", {"start": v(13.44, -27.55) * mm, "end": v(13.48, -27.58) * mm});
            skLineSegment(sketch, "E356", {"start": v(13.48, -27.58) * mm, "end": v(13.53, -27.57) * mm});
            skLineSegment(sketch, "E357", {"start": v(13.53, -27.57) * mm, "end": v(13.64, -27.52) * mm});
            skLineSegment(sketch, "E358", {"start": v(13.64, -27.52) * mm, "end": v(13.67, -27.48) * mm});
            skLineSegment(sketch, "E359", {"start": v(13.67, -27.48) * mm, "end": v(13.67, -27.44) * mm});
            skLineSegment(sketch, "E360", {"start": v(13.67, -27.44) * mm, "end": v(13.66, -27.4) * mm});
            skLineSegment(sketch, "E361", {"start": v(13.66, -27.4) * mm, "end": v(13.66, -27.35) * mm});
            skLineSegment(sketch, "E362", {"start": v(13.66, -27.35) * mm, "end": v(13.65, -27.3) * mm});
            skLineSegment(sketch, "E363", {"start": v(13.65, -27.3) * mm, "end": v(13.66, -27.26) * mm});
            skLineSegment(sketch, "E364", {"start": v(13.66, -27.26) * mm, "end": v(13.68, -27.2) * mm});
            skLineSegment(sketch, "E365", {"start": v(13.68, -27.2) * mm, "end": v(13.71, -27.16) * mm});
            skLineSegment(sketch, "E366", {"start": v(13.71, -27.16) * mm, "end": v(13.75, -27.12) * mm});
            skLineSegment(sketch, "E367", {"start": v(13.75, -27.12) * mm, "end": v(13.8, -27.09) * mm});
            skLineSegment(sketch, "E368", {"start": v(13.8, -27.09) * mm, "end": v(13.86, -27.07) * mm});
            skLineSegment(sketch, "E369", {"start": v(13.86, -27.07) * mm, "end": v(13.91, -27.06) * mm});
            skLineSegment(sketch, "E370", {"start": v(13.91, -27.06) * mm, "end": v(13.97, -27.06) * mm});
            skLineSegment(sketch, "E371", {"start": v(13.97, -27.06) * mm, "end": v(14.03, -27.07) * mm});
            skLineSegment(sketch, "E372", {"start": v(14.03, -27.07) * mm, "end": v(14.07, -27.1) * mm});
            skLineSegment(sketch, "E373", {"start": v(14.07, -27.1) * mm, "end": v(14.1, -27.12) * mm});
            skLineSegment(sketch, "E374", {"start": v(14.1, -27.12) * mm, "end": v(14.13, -27.16) * mm});
            skLineSegment(sketch, "E375", {"start": v(14.13, -27.16) * mm, "end": v(14.16, -27.2) * mm});
            skLineSegment(sketch, "E376", {"start": v(14.16, -27.2) * mm, "end": v(14.2, -27.21) * mm});
            skLineSegment(sketch, "E377", {"start": v(14.2, -27.21) * mm, "end": v(14.25, -27.2) * mm});
            skLineSegment(sketch, "E378", {"start": v(14.25, -27.2) * mm, "end": v(14.35, -27.15) * mm});
            skLineSegment(sketch, "E379", {"start": v(14.35, -27.15) * mm, "end": v(14.39, -27.12) * mm});
            skLineSegment(sketch, "E380", {"start": v(14.39, -27.12) * mm, "end": v(14.39, -27.07) * mm});
            skLineSegment(sketch, "E381", {"start": v(14.39, -27.07) * mm, "end": v(14.37, -27.03) * mm});
            skLineSegment(sketch, "E382", {"start": v(14.37, -27.03) * mm, "end": v(14.37, -26.99) * mm});
            skLineSegment(sketch, "E383", {"start": v(14.37, -26.99) * mm, "end": v(14.36, -26.94) * mm});
            skLineSegment(sketch, "E384", {"start": v(14.36, -26.94) * mm, "end": v(14.37, -26.9) * mm});
            skLineSegment(sketch, "E385", {"start": v(14.37, -26.9) * mm, "end": v(14.39, -26.84) * mm});
            skLineSegment(sketch, "E386", {"start": v(14.39, -26.84) * mm, "end": v(14.42, -26.8) * mm});
            skLineSegment(sketch, "E387", {"start": v(14.42, -26.8) * mm, "end": v(14.46, -26.75) * mm});
            skLineSegment(sketch, "E388", {"start": v(14.46, -26.75) * mm, "end": v(14.5, -26.72) * mm});
            skLineSegment(sketch, "E389", {"start": v(14.5, -26.72) * mm, "end": v(14.56, -26.7) * mm});
            skLineSegment(sketch, "E390", {"start": v(14.56, -26.7) * mm, "end": v(14.62, -26.68) * mm});
            skLineSegment(sketch, "E391", {"start": v(14.62, -26.68) * mm, "end": v(14.67, -26.68) * mm});
            skLineSegment(sketch, "E392", {"start": v(14.67, -26.68) * mm, "end": v(14.73, -26.7) * mm});
            skLineSegment(sketch, "E393", {"start": v(14.73, -26.7) * mm, "end": v(14.77, -26.72) * mm});
            skLineSegment(sketch, "E394", {"start": v(14.77, -26.72) * mm, "end": v(14.8, -26.75) * mm});
            skLineSegment(sketch, "E395", {"start": v(14.8, -26.75) * mm, "end": v(14.84, -26.78) * mm});
            skLineSegment(sketch, "E396", {"start": v(14.84, -26.78) * mm, "end": v(14.87, -26.81) * mm});
            skLineSegment(sketch, "E397", {"start": v(14.87, -26.81) * mm, "end": v(14.9, -26.83) * mm});
            skLineSegment(sketch, "E398", {"start": v(14.9, -26.83) * mm, "end": v(14.95, -26.82) * mm});
            skLineSegment(sketch, "E399", {"start": v(14.95, -26.82) * mm, "end": v(15.06, -26.76) * mm});
            skLineSegment(sketch, "E400", {"start": v(15.06, -26.76) * mm, "end": v(15.1, -26.73) * mm});
            skLineSegment(sketch, "E401", {"start": v(15.1, -26.73) * mm, "end": v(15.1, -26.69) * mm});
            skLineSegment(sketch, "E402", {"start": v(15.1, -26.69) * mm, "end": v(15.08, -26.64) * mm});
            skLineSegment(sketch, "E403", {"start": v(15.08, -26.64) * mm, "end": v(15.07, -26.6) * mm});
            skLineSegment(sketch, "E404", {"start": v(15.07, -26.6) * mm, "end": v(15.06, -26.55) * mm});
            skLineSegment(sketch, "E405", {"start": v(15.06, -26.55) * mm, "end": v(15.07, -26.5) * mm});
            skLineSegment(sketch, "E406", {"start": v(15.07, -26.5) * mm, "end": v(15.08, -26.45) * mm});
            skLineSegment(sketch, "E407", {"start": v(15.08, -26.45) * mm, "end": v(15.11, -26.4) * mm});
            skLineSegment(sketch, "E408", {"start": v(15.11, -26.4) * mm, "end": v(15.15, -26.36) * mm});
            skLineSegment(sketch, "E409", {"start": v(15.15, -26.36) * mm, "end": v(15.2, -26.33) * mm});
            skLineSegment(sketch, "E410", {"start": v(15.2, -26.33) * mm, "end": v(15.25, -26.3) * mm});
            skLineSegment(sketch, "E411", {"start": v(15.25, -26.3) * mm, "end": v(15.31, -26.3) * mm});
            skLineSegment(sketch, "E412", {"start": v(15.31, -26.3) * mm, "end": v(15.37, -26.3) * mm});
            skLineSegment(sketch, "E413", {"start": v(15.37, -26.3) * mm, "end": v(15.42, -26.3) * mm});
            skLineSegment(sketch, "E414", {"start": v(15.42, -26.3) * mm, "end": v(15.46, -26.32) * mm});
            skLineSegment(sketch, "E415", {"start": v(15.46, -26.32) * mm, "end": v(15.5, -26.35) * mm});
            skLineSegment(sketch, "E416", {"start": v(15.5, -26.35) * mm, "end": v(15.54, -26.38) * mm});
            skLineSegment(sketch, "E417", {"start": v(15.54, -26.38) * mm, "end": v(15.56, -26.41) * mm});
            skLineSegment(sketch, "E418", {"start": v(15.56, -26.41) * mm, "end": v(15.6, -26.43) * mm});
            skLineSegment(sketch, "E419", {"start": v(15.6, -26.43) * mm, "end": v(15.65, -26.42) * mm});
            skLineSegment(sketch, "E420", {"start": v(15.65, -26.42) * mm, "end": v(15.75, -26.36) * mm});
            skLineSegment(sketch, "E421", {"start": v(15.75, -26.36) * mm, "end": v(15.78, -26.33) * mm});
            skLineSegment(sketch, "E422", {"start": v(15.78, -26.33) * mm, "end": v(15.78, -26.28) * mm});
            skLineSegment(sketch, "E423", {"start": v(15.78, -26.28) * mm, "end": v(15.77, -26.24) * mm});
            skLineSegment(sketch, "E424", {"start": v(15.77, -26.24) * mm, "end": v(15.76, -26.2) * mm});
            skLineSegment(sketch, "E425", {"start": v(15.76, -26.2) * mm, "end": v(15.75, -26.15) * mm});
            skLineSegment(sketch, "E426", {"start": v(15.75, -26.15) * mm, "end": v(15.76, -26.1) * mm});
            skLineSegment(sketch, "E427", {"start": v(15.76, -26.1) * mm, "end": v(15.77, -26.05) * mm});
            skLineSegment(sketch, "E428", {"start": v(15.77, -26.05) * mm, "end": v(15.8, -26) * mm});
            skLineSegment(sketch, "E429", {"start": v(15.8, -26) * mm, "end": v(15.84, -25.96) * mm});
            skLineSegment(sketch, "E430", {"start": v(15.84, -25.96) * mm, "end": v(15.88, -25.92) * mm});
            skLineSegment(sketch, "E431", {"start": v(15.88, -25.92) * mm, "end": v(15.94, -25.9) * mm});
            skLineSegment(sketch, "E432", {"start": v(15.94, -25.9) * mm, "end": v(16, -25.88) * mm});
            skLineSegment(sketch, "E433", {"start": v(16, -25.88) * mm, "end": v(16.05, -25.88) * mm});
            skLineSegment(sketch, "E434", {"start": v(16.05, -25.88) * mm, "end": v(16.1, -25.89) * mm});
            skLineSegment(sketch, "E435", {"start": v(16.1, -25.89) * mm, "end": v(16.15, -25.91) * mm});
            skLineSegment(sketch, "E436", {"start": v(16.15, -25.91) * mm, "end": v(16.19, -25.93) * mm});
            skLineSegment(sketch, "E437", {"start": v(16.19, -25.93) * mm, "end": v(16.22, -25.96) * mm});
            skLineSegment(sketch, "E438", {"start": v(16.22, -25.96) * mm, "end": v(16.25, -26) * mm});
            skLineSegment(sketch, "E439", {"start": v(16.25, -26) * mm, "end": v(16.3, -26.02) * mm});
            skLineSegment(sketch, "E440", {"start": v(16.3, -26.02) * mm, "end": v(16.34, -26) * mm});
            skLineSegment(sketch, "E441", {"start": v(16.34, -26) * mm, "end": v(16.44, -25.94) * mm});
            skLineSegment(sketch, "E442", {"start": v(16.44, -25.94) * mm, "end": v(16.47, -25.9) * mm});
            skLineSegment(sketch, "E443", {"start": v(16.47, -25.9) * mm, "end": v(16.47, -25.86) * mm});
            skLineSegment(sketch, "E444", {"start": v(16.47, -25.86) * mm, "end": v(16.45, -25.82) * mm});
            skLineSegment(sketch, "E445", {"start": v(16.45, -25.82) * mm, "end": v(16.44, -25.77) * mm});
            skLineSegment(sketch, "E446", {"start": v(16.44, -25.77) * mm, "end": v(16.43, -25.73) * mm});
            skLineSegment(sketch, "E447", {"start": v(16.43, -25.73) * mm, "end": v(16.43, -25.68) * mm});
            skLineSegment(sketch, "E448", {"start": v(16.43, -25.68) * mm, "end": v(16.45, -25.63) * mm});
            skLineSegment(sketch, "E449", {"start": v(16.45, -25.63) * mm, "end": v(16.47, -25.58) * mm});
            skLineSegment(sketch, "E450", {"start": v(16.47, -25.58) * mm, "end": v(16.51, -25.53) * mm});
            skLineSegment(sketch, "E451", {"start": v(16.51, -25.53) * mm, "end": v(16.56, -25.5) * mm});
            skLineSegment(sketch, "E452", {"start": v(16.56, -25.5) * mm, "end": v(16.6, -25.47) * mm});
            skLineSegment(sketch, "E453", {"start": v(16.6, -25.47) * mm, "end": v(16.67, -25.45) * mm});
            skLineSegment(sketch, "E454", {"start": v(16.67, -25.45) * mm, "end": v(16.72, -25.45) * mm});
            skLineSegment(sketch, "E455", {"start": v(16.72, -25.45) * mm, "end": v(16.78, -25.46) * mm});
            skLineSegment(sketch, "E456", {"start": v(16.78, -25.46) * mm, "end": v(16.82, -25.48) * mm});
            skLineSegment(sketch, "E457", {"start": v(16.82, -25.48) * mm, "end": v(16.86, -25.5) * mm});
            skLineSegment(sketch, "E458", {"start": v(16.86, -25.5) * mm, "end": v(16.9, -25.53) * mm});
            skLineSegment(sketch, "E459", {"start": v(16.9, -25.53) * mm, "end": v(16.93, -25.56) * mm});
            skLineSegment(sketch, "E460", {"start": v(16.93, -25.56) * mm, "end": v(16.97, -25.58) * mm});
            skLineSegment(sketch, "E461", {"start": v(16.97, -25.58) * mm, "end": v(17.01, -25.57) * mm});
            skLineSegment(sketch, "E462", {"start": v(17.01, -25.57) * mm, "end": v(17.11, -25.5) * mm});
            skLineSegment(sketch, "E463", {"start": v(17.11, -25.5) * mm, "end": v(17.14, -25.46) * mm});
            skLineSegment(sketch, "E464", {"start": v(17.14, -25.46) * mm, "end": v(17.14, -25.42) * mm});
            skLineSegment(sketch, "E465", {"start": v(17.14, -25.42) * mm, "end": v(17.12, -25.38) * mm});
            skLineSegment(sketch, "E466", {"start": v(17.12, -25.38) * mm, "end": v(17.1, -25.34) * mm});
            skLineSegment(sketch, "E467", {"start": v(17.1, -25.34) * mm, "end": v(17.1, -25.3) * mm});
            skLineSegment(sketch, "E468", {"start": v(17.1, -25.3) * mm, "end": v(17.1, -25.25) * mm});
            skLineSegment(sketch, "E469", {"start": v(17.1, -25.25) * mm, "end": v(17.11, -25.19) * mm});
            skLineSegment(sketch, "E470", {"start": v(17.11, -25.19) * mm, "end": v(17.14, -25.14) * mm});
            skLineSegment(sketch, "E471", {"start": v(17.14, -25.14) * mm, "end": v(17.17, -25.1) * mm});
            skLineSegment(sketch, "E472", {"start": v(17.17, -25.1) * mm, "end": v(17.22, -25.05) * mm});
            skLineSegment(sketch, "E473", {"start": v(17.22, -25.05) * mm, "end": v(17.27, -25.03) * mm});
            skLineSegment(sketch, "E474", {"start": v(17.27, -25.03) * mm, "end": v(17.33, -25) * mm});
            skLineSegment(sketch, "E475", {"start": v(17.33, -25) * mm, "end": v(17.38, -25) * mm});
            skLineSegment(sketch, "E476", {"start": v(17.38, -25) * mm, "end": v(17.44, -25.01) * mm});
            skLineSegment(sketch, "E477", {"start": v(17.44, -25.01) * mm, "end": v(17.48, -25.03) * mm});
            skLineSegment(sketch, "E478", {"start": v(17.48, -25.03) * mm, "end": v(17.52, -25.05) * mm});
            skLineSegment(sketch, "E479", {"start": v(17.52, -25.05) * mm, "end": v(17.56, -25.08) * mm});
            skLineSegment(sketch, "E480", {"start": v(17.56, -25.08) * mm, "end": v(17.59, -25.1) * mm});
            skLineSegment(sketch, "E481", {"start": v(17.59, -25.1) * mm, "end": v(17.63, -25.13) * mm});
            skLineSegment(sketch, "E482", {"start": v(17.63, -25.13) * mm, "end": v(17.67, -25.11) * mm});
            skLineSegment(sketch, "E483", {"start": v(17.67, -25.11) * mm, "end": v(17.77, -25.04) * mm});
            skLineSegment(sketch, "E484", {"start": v(17.77, -25.04) * mm, "end": v(17.8, -25) * mm});
            skLineSegment(sketch, "E485", {"start": v(17.8, -25) * mm, "end": v(17.8, -24.96) * mm});
            skLineSegment(sketch, "E486", {"start": v(17.8, -24.96) * mm, "end": v(17.78, -24.92) * mm});
            skLineSegment(sketch, "E487", {"start": v(17.78, -24.92) * mm, "end": v(17.77, -24.88) * mm});
            skLineSegment(sketch, "E488", {"start": v(17.77, -24.88) * mm, "end": v(17.76, -24.83) * mm});
            skLineSegment(sketch, "E489", {"start": v(17.76, -24.83) * mm, "end": v(17.76, -24.79) * mm});
            skLineSegment(sketch, "E490", {"start": v(17.76, -24.79) * mm, "end": v(17.77, -24.73) * mm});
            skLineSegment(sketch, "E491", {"start": v(17.77, -24.73) * mm, "end": v(17.8, -24.68) * mm});
            skLineSegment(sketch, "E492", {"start": v(17.8, -24.68) * mm, "end": v(17.83, -24.63) * mm});
            skLineSegment(sketch, "E493", {"start": v(17.83, -24.63) * mm, "end": v(17.87, -24.6) * mm});
            skLineSegment(sketch, "E494", {"start": v(17.87, -24.6) * mm, "end": v(17.92, -24.56) * mm});
            skLineSegment(sketch, "E495", {"start": v(17.92, -24.56) * mm, "end": v(17.97, -24.55) * mm});
            skLineSegment(sketch, "E496", {"start": v(17.97, -24.55) * mm, "end": v(18.03, -24.54) * mm});
            skLineSegment(sketch, "E497", {"start": v(18.03, -24.54) * mm, "end": v(18.09, -24.55) * mm});
            skLineSegment(sketch, "E498", {"start": v(18.09, -24.55) * mm, "end": v(18.13, -24.56) * mm});
            skLineSegment(sketch, "E499", {"start": v(18.13, -24.56) * mm, "end": v(18.17, -24.58) * mm});
            skLineSegment(sketch, "E500", {"start": v(18.17, -24.58) * mm, "end": v(18.2, -24.61) * mm});
            skLineSegment(sketch, "E501", {"start": v(18.2, -24.61) * mm, "end": v(18.24, -24.64) * mm});
            skLineSegment(sketch, "E502", {"start": v(18.24, -24.64) * mm, "end": v(18.28, -24.66) * mm});
            skLineSegment(sketch, "E503", {"start": v(18.28, -24.66) * mm, "end": v(18.33, -24.64) * mm});
            skLineSegment(sketch, "E504", {"start": v(18.33, -24.64) * mm, "end": v(18.42, -24.57) * mm});
            skLineSegment(sketch, "E505", {"start": v(18.42, -24.57) * mm, "end": v(18.45, -24.53) * mm});
            skLineSegment(sketch, "E506", {"start": v(18.45, -24.53) * mm, "end": v(18.45, -24.49) * mm});
            skLineSegment(sketch, "E507", {"start": v(18.45, -24.49) * mm, "end": v(18.43, -24.45) * mm});
            skLineSegment(sketch, "E508", {"start": v(18.43, -24.45) * mm, "end": v(18.41, -24.4) * mm});
            skLineSegment(sketch, "E509", {"start": v(18.41, -24.4) * mm, "end": v(18.4, -24.36) * mm});
            skLineSegment(sketch, "E510", {"start": v(18.4, -24.36) * mm, "end": v(18.4, -24.32) * mm});
            skLineSegment(sketch, "E511", {"start": v(18.4, -24.32) * mm, "end": v(18.4, -24.26) * mm});
            skLineSegment(sketch, "E512", {"start": v(18.4, -24.26) * mm, "end": v(18.43, -24.2) * mm});
            skLineSegment(sketch, "E513", {"start": v(18.43, -24.2) * mm, "end": v(18.46, -24.16) * mm});
            skLineSegment(sketch, "E514", {"start": v(18.46, -24.16) * mm, "end": v(18.5, -24.12) * mm});
            skLineSegment(sketch, "E515", {"start": v(18.5, -24.12) * mm, "end": v(18.56, -24.09) * mm});
            skLineSegment(sketch, "E516", {"start": v(18.56, -24.09) * mm, "end": v(18.61, -24.07) * mm});
            skLineSegment(sketch, "E517", {"start": v(18.61, -24.07) * mm, "end": v(18.67, -24.06) * mm});
            skLineSegment(sketch, "E518", {"start": v(18.67, -24.06) * mm, "end": v(18.73, -24.06) * mm});
            skLineSegment(sketch, "E519", {"start": v(18.73, -24.06) * mm, "end": v(18.77, -24.08) * mm});
            skLineSegment(sketch, "E520", {"start": v(18.77, -24.08) * mm, "end": v(18.8, -24.1) * mm});
            skLineSegment(sketch, "E521", {"start": v(18.8, -24.1) * mm, "end": v(18.85, -24.13) * mm});
            skLineSegment(sketch, "E522", {"start": v(18.85, -24.13) * mm, "end": v(18.88, -24.15) * mm});
            skLineSegment(sketch, "E523", {"start": v(18.88, -24.15) * mm, "end": v(18.92, -24.17) * mm});
            skLineSegment(sketch, "E524", {"start": v(18.92, -24.17) * mm, "end": v(18.96, -24.15) * mm});
            skLineSegment(sketch, "E525", {"start": v(18.96, -24.15) * mm, "end": v(19.06, -24.08) * mm});
            skLineSegment(sketch, "E526", {"start": v(19.06, -24.08) * mm, "end": v(19.09, -24.04) * mm});
            skLineSegment(sketch, "E527", {"start": v(19.09, -24.04) * mm, "end": v(19.08, -24) * mm});
            skLineSegment(sketch, "E528", {"start": v(19.08, -24) * mm, "end": v(19.06, -23.96) * mm});
            skLineSegment(sketch, "E529", {"start": v(19.06, -23.96) * mm, "end": v(19.04, -23.92) * mm});
            skLineSegment(sketch, "E530", {"start": v(19.04, -23.92) * mm, "end": v(19.03, -23.87) * mm});
            skLineSegment(sketch, "E531", {"start": v(19.03, -23.87) * mm, "end": v(19.03, -23.83) * mm});
            skLineSegment(sketch, "E532", {"start": v(19.03, -23.83) * mm, "end": v(19.04, -23.77) * mm});
            skLineSegment(sketch, "E533", {"start": v(19.04, -23.77) * mm, "end": v(19.06, -23.71) * mm});
            skLineSegment(sketch, "E534", {"start": v(19.06, -23.71) * mm, "end": v(19.09, -23.67) * mm});
            skLineSegment(sketch, "E535", {"start": v(19.09, -23.67) * mm, "end": v(19.13, -23.63) * mm});
            skLineSegment(sketch, "E536", {"start": v(19.13, -23.63) * mm, "end": v(19.18, -23.6) * mm});
            skLineSegment(sketch, "E537", {"start": v(19.18, -23.6) * mm, "end": v(19.23, -23.57) * mm});
            skLineSegment(sketch, "E538", {"start": v(19.23, -23.57) * mm, "end": v(19.3, -23.56) * mm});
            skLineSegment(sketch, "E539", {"start": v(19.3, -23.56) * mm, "end": v(19.35, -23.57) * mm});
            skLineSegment(sketch, "E540", {"start": v(19.35, -23.57) * mm, "end": v(19.4, -23.58) * mm});
            skLineSegment(sketch, "E541", {"start": v(19.4, -23.58) * mm, "end": v(19.43, -23.6) * mm});
            skLineSegment(sketch, "E542", {"start": v(19.43, -23.6) * mm, "end": v(19.47, -23.62) * mm});
            skLineSegment(sketch, "E543", {"start": v(19.47, -23.62) * mm, "end": v(19.5, -23.65) * mm});
            skLineSegment(sketch, "E544", {"start": v(19.5, -23.65) * mm, "end": v(19.55, -23.67) * mm});
            skLineSegment(sketch, "E545", {"start": v(19.55, -23.67) * mm, "end": v(19.6, -23.65) * mm});
            skLineSegment(sketch, "E546", {"start": v(19.6, -23.65) * mm, "end": v(19.68, -23.57) * mm});
            skLineSegment(sketch, "E547", {"start": v(19.68, -23.57) * mm, "end": v(19.7, -23.53) * mm});
            skLineSegment(sketch, "E548", {"start": v(19.7, -23.53) * mm, "end": v(19.7, -23.49) * mm});
            skLineSegment(sketch, "E549", {"start": v(19.7, -23.49) * mm, "end": v(19.68, -23.45) * mm});
            skLineSegment(sketch, "E550", {"start": v(19.68, -23.45) * mm, "end": v(19.66, -23.4) * mm});
            skLineSegment(sketch, "E551", {"start": v(19.66, -23.4) * mm, "end": v(19.65, -23.36) * mm});
            skLineSegment(sketch, "E552", {"start": v(19.65, -23.36) * mm, "end": v(19.65, -23.32) * mm});
            skLineSegment(sketch, "E553", {"start": v(19.65, -23.32) * mm, "end": v(19.65, -23.26) * mm});
            skLineSegment(sketch, "E554", {"start": v(19.65, -23.26) * mm, "end": v(19.67, -23.2) * mm});
            skLineSegment(sketch, "E555", {"start": v(19.67, -23.2) * mm, "end": v(19.7, -23.16) * mm});
            skLineSegment(sketch, "E556", {"start": v(19.7, -23.16) * mm, "end": v(19.74, -23.12) * mm});
            skLineSegment(sketch, "E557", {"start": v(19.74, -23.12) * mm, "end": v(19.8, -23.08) * mm});
            skLineSegment(sketch, "E558", {"start": v(19.8, -23.08) * mm, "end": v(19.84, -23.06) * mm});
            skLineSegment(sketch, "E559", {"start": v(19.84, -23.06) * mm, "end": v(19.9, -23.05) * mm});
            skLineSegment(sketch, "E560", {"start": v(19.9, -23.05) * mm, "end": v(19.96, -23.05) * mm});
            skLineSegment(sketch, "E561", {"start": v(19.96, -23.05) * mm, "end": v(20, -23.07) * mm});
            skLineSegment(sketch, "E562", {"start": v(20, -23.07) * mm, "end": v(20.04, -23.08) * mm});
            skLineSegment(sketch, "E563", {"start": v(20.04, -23.08) * mm, "end": v(20.08, -23.1) * mm});
            skLineSegment(sketch, "E564", {"start": v(20.08, -23.1) * mm, "end": v(20.12, -23.13) * mm});
            skLineSegment(sketch, "E565", {"start": v(20.12, -23.13) * mm, "end": v(20.16, -23.15) * mm});
            skLineSegment(sketch, "E566", {"start": v(20.16, -23.15) * mm, "end": v(20.2, -23.13) * mm});
            skLineSegment(sketch, "E567", {"start": v(20.2, -23.13) * mm, "end": v(20.3, -23.05) * mm});
            skLineSegment(sketch, "E568", {"start": v(20.3, -23.05) * mm, "end": v(20.32, -23) * mm});
            skLineSegment(sketch, "E569", {"start": v(20.32, -23) * mm, "end": v(20.3, -22.96) * mm});
            skLineSegment(sketch, "E570", {"start": v(20.3, -22.96) * mm, "end": v(20.29, -22.93) * mm});
            skLineSegment(sketch, "E571", {"start": v(20.29, -22.93) * mm, "end": v(20.27, -22.89) * mm});
            skLineSegment(sketch, "E572", {"start": v(20.27, -22.89) * mm, "end": v(20.26, -22.84) * mm});
            skLineSegment(sketch, "E573", {"start": v(20.26, -22.84) * mm, "end": v(20.25, -22.8) * mm});
            skLineSegment(sketch, "E574", {"start": v(20.25, -22.8) * mm, "end": v(20.25, -22.74) * mm});
            skLineSegment(sketch, "E575", {"start": v(20.25, -22.74) * mm, "end": v(20.27, -22.68) * mm});
            skLineSegment(sketch, "E576", {"start": v(20.27, -22.68) * mm, "end": v(20.3, -22.64) * mm});
            skLineSegment(sketch, "E577", {"start": v(20.3, -22.64) * mm, "end": v(20.34, -22.6) * mm});
            skLineSegment(sketch, "E578", {"start": v(20.34, -22.6) * mm, "end": v(20.39, -22.56) * mm});
            skLineSegment(sketch, "E579", {"start": v(20.39, -22.56) * mm, "end": v(20.44, -22.53) * mm});
            skLineSegment(sketch, "E580", {"start": v(20.44, -22.53) * mm, "end": v(20.5, -22.52) * mm});
            skLineSegment(sketch, "E581", {"start": v(20.5, -22.52) * mm, "end": v(20.56, -22.52) * mm});
            skLineSegment(sketch, "E582", {"start": v(20.56, -22.52) * mm, "end": v(20.6, -22.53) * mm});
            skLineSegment(sketch, "E583", {"start": v(20.6, -22.53) * mm, "end": v(20.64, -22.55) * mm});
            skLineSegment(sketch, "E584", {"start": v(20.64, -22.55) * mm, "end": v(20.68, -22.57) * mm});
            skLineSegment(sketch, "E585", {"start": v(20.68, -22.57) * mm, "end": v(20.72, -22.6) * mm});
            skLineSegment(sketch, "E586", {"start": v(20.72, -22.6) * mm, "end": v(20.76, -22.61) * mm});
            skLineSegment(sketch, "E587", {"start": v(20.76, -22.61) * mm, "end": v(20.8, -22.6) * mm});
            skLineSegment(sketch, "E588", {"start": v(20.8, -22.6) * mm, "end": v(20.9, -22.51) * mm});
            skLineSegment(sketch, "E589", {"start": v(20.9, -22.51) * mm, "end": v(20.91, -22.47) * mm});
            skLineSegment(sketch, "E590", {"start": v(20.91, -22.47) * mm, "end": v(20.9, -22.43) * mm});
            skLineSegment(sketch, "E591", {"start": v(20.9, -22.43) * mm, "end": v(20.88, -22.39) * mm});
            skLineSegment(sketch, "E592", {"start": v(20.88, -22.39) * mm, "end": v(20.86, -22.35) * mm});
            skLineSegment(sketch, "E593", {"start": v(20.86, -22.35) * mm, "end": v(20.85, -22.3) * mm});
            skLineSegment(sketch, "E594", {"start": v(20.85, -22.3) * mm, "end": v(20.84, -22.26) * mm});
            skLineSegment(sketch, "E595", {"start": v(20.84, -22.26) * mm, "end": v(20.84, -22.2) * mm});
            skLineSegment(sketch, "E596", {"start": v(20.84, -22.2) * mm, "end": v(20.86, -22.15) * mm});
            skLineSegment(sketch, "E597", {"start": v(20.86, -22.15) * mm, "end": v(20.89, -22.1) * mm});
            skLineSegment(sketch, "E598", {"start": v(20.89, -22.1) * mm, "end": v(20.93, -22.05) * mm});
            skLineSegment(sketch, "E599", {"start": v(20.93, -22.05) * mm, "end": v(20.97, -22.02) * mm});
            skLineSegment(sketch, "E600", {"start": v(20.97, -22.02) * mm, "end": v(21.02, -22) * mm});
            skLineSegment(sketch, "E601", {"start": v(21.02, -22) * mm, "end": v(21.08, -21.98) * mm});
            skLineSegment(sketch, "E602", {"start": v(21.08, -21.98) * mm, "end": v(21.14, -21.98) * mm});
            skLineSegment(sketch, "E603", {"start": v(21.14, -21.98) * mm, "end": v(21.18, -21.99) * mm});
            skLineSegment(sketch, "E604", {"start": v(21.18, -21.99) * mm, "end": v(21.22, -22) * mm});
            skLineSegment(sketch, "E605", {"start": v(21.22, -22) * mm, "end": v(21.26, -22.02) * mm});
            skLineSegment(sketch, "E606", {"start": v(21.26, -22.02) * mm, "end": v(21.3, -22.05) * mm});
            skLineSegment(sketch, "E607", {"start": v(21.3, -22.05) * mm, "end": v(21.34, -22.06) * mm});
            skLineSegment(sketch, "E608", {"start": v(21.34, -22.06) * mm, "end": v(21.39, -22.04) * mm});
            skLineSegment(sketch, "E609", {"start": v(21.39, -22.04) * mm, "end": v(21.47, -21.96) * mm});
            skLineSegment(sketch, "E610", {"start": v(21.47, -21.96) * mm, "end": v(21.5, -21.91) * mm});
            skLineSegment(sketch, "E611", {"start": v(21.5, -21.91) * mm, "end": v(21.48, -21.87) * mm});
            skLineSegment(sketch, "E612", {"start": v(21.48, -21.87) * mm, "end": v(21.46, -21.83) * mm});
            skLineSegment(sketch, "E613", {"start": v(21.46, -21.83) * mm, "end": v(21.44, -21.8) * mm});
            skLineSegment(sketch, "E614", {"start": v(21.44, -21.8) * mm, "end": v(21.42, -21.75) * mm});
            skLineSegment(sketch, "E615", {"start": v(21.42, -21.75) * mm, "end": v(21.41, -21.7) * mm});
            skLineSegment(sketch, "E616", {"start": v(21.41, -21.7) * mm, "end": v(21.42, -21.65) * mm});
            skLineSegment(sketch, "E617", {"start": v(21.42, -21.65) * mm, "end": v(21.43, -21.6) * mm});
            skLineSegment(sketch, "E618", {"start": v(21.43, -21.6) * mm, "end": v(21.46, -21.54) * mm});
            skLineSegment(sketch, "E619", {"start": v(21.46, -21.54) * mm, "end": v(21.5, -21.5) * mm});
            skLineSegment(sketch, "E620", {"start": v(21.5, -21.5) * mm, "end": v(21.54, -21.46) * mm});
            skLineSegment(sketch, "E621", {"start": v(21.54, -21.46) * mm, "end": v(21.6, -21.43) * mm});
            skLineSegment(sketch, "E622", {"start": v(21.6, -21.43) * mm, "end": v(21.65, -21.42) * mm});
            skLineSegment(sketch, "E623", {"start": v(21.65, -21.42) * mm, "end": v(21.7, -21.41) * mm});
            skLineSegment(sketch, "E624", {"start": v(21.7, -21.41) * mm, "end": v(21.75, -21.42) * mm});
            skLineSegment(sketch, "E625", {"start": v(21.75, -21.42) * mm, "end": v(21.8, -21.44) * mm});
            skLineSegment(sketch, "E626", {"start": v(21.8, -21.44) * mm, "end": v(21.83, -21.46) * mm});
            skLineSegment(sketch, "E627", {"start": v(21.83, -21.46) * mm, "end": v(21.87, -21.48) * mm});
            skLineSegment(sketch, "E628", {"start": v(21.87, -21.48) * mm, "end": v(21.91, -21.5) * mm});
            skLineSegment(sketch, "E629", {"start": v(21.91, -21.5) * mm, "end": v(21.96, -21.47) * mm});
            skLineSegment(sketch, "E630", {"start": v(21.96, -21.47) * mm, "end": v(22.04, -21.39) * mm});
            skLineSegment(sketch, "E631", {"start": v(22.04, -21.39) * mm, "end": v(22.06, -21.34) * mm});
            skLineSegment(sketch, "E632", {"start": v(22.06, -21.34) * mm, "end": v(22.05, -21.3) * mm});
            skLineSegment(sketch, "E633", {"start": v(22.05, -21.3) * mm, "end": v(22.02, -21.26) * mm});
            skLineSegment(sketch, "E634", {"start": v(22.02, -21.26) * mm, "end": v(22, -21.22) * mm});
            skLineSegment(sketch, "E635", {"start": v(22, -21.22) * mm, "end": v(21.99, -21.18) * mm});
            skLineSegment(sketch, "E636", {"start": v(21.99, -21.18) * mm, "end": v(21.98, -21.14) * mm});
            skLineSegment(sketch, "E637", {"start": v(21.98, -21.14) * mm, "end": v(21.98, -21.08) * mm});
            skLineSegment(sketch, "E638", {"start": v(21.98, -21.08) * mm, "end": v(22, -21.02) * mm});
            skLineSegment(sketch, "E639", {"start": v(22, -21.02) * mm, "end": v(22.02, -20.97) * mm});
            skLineSegment(sketch, "E640", {"start": v(22.02, -20.97) * mm, "end": v(22.05, -20.93) * mm});
            skLineSegment(sketch, "E641", {"start": v(22.05, -20.93) * mm, "end": v(22.1, -20.89) * mm});
            skLineSegment(sketch, "E642", {"start": v(22.1, -20.89) * mm, "end": v(22.15, -20.86) * mm});
            skLineSegment(sketch, "E643", {"start": v(22.15, -20.86) * mm, "end": v(22.2, -20.84) * mm});
            skLineSegment(sketch, "E644", {"start": v(22.2, -20.84) * mm, "end": v(22.26, -20.84) * mm});
            skLineSegment(sketch, "E645", {"start": v(22.26, -20.84) * mm, "end": v(22.3, -20.85) * mm});
            skLineSegment(sketch, "E646", {"start": v(22.3, -20.85) * mm, "end": v(22.35, -20.86) * mm});
            skLineSegment(sketch, "E647", {"start": v(22.35, -20.86) * mm, "end": v(22.39, -20.88) * mm});
            skLineSegment(sketch, "E648", {"start": v(22.39, -20.88) * mm, "end": v(22.43, -20.9) * mm});
            skLineSegment(sketch, "E649", {"start": v(22.43, -20.9) * mm, "end": v(22.47, -20.91) * mm});
            skLineSegment(sketch, "E650", {"start": v(22.47, -20.91) * mm, "end": v(22.51, -20.9) * mm});
            skLineSegment(sketch, "E651", {"start": v(22.51, -20.9) * mm, "end": v(22.6, -20.8) * mm});
            skLineSegment(sketch, "E652", {"start": v(22.6, -20.8) * mm, "end": v(22.61, -20.76) * mm});
            skLineSegment(sketch, "E653", {"start": v(22.61, -20.76) * mm, "end": v(22.6, -20.72) * mm});
            skLineSegment(sketch, "E654", {"start": v(22.6, -20.72) * mm, "end": v(22.57, -20.68) * mm});
            skLineSegment(sketch, "E655", {"start": v(22.57, -20.68) * mm, "end": v(22.55, -20.64) * mm});
            skLineSegment(sketch, "E656", {"start": v(22.55, -20.64) * mm, "end": v(22.53, -20.6) * mm});
            skLineSegment(sketch, "E657", {"start": v(22.53, -20.6) * mm, "end": v(22.52, -20.56) * mm});
            skLineSegment(sketch, "E658", {"start": v(22.52, -20.56) * mm, "end": v(22.52, -20.5) * mm});
            skLineSegment(sketch, "E659", {"start": v(22.52, -20.5) * mm, "end": v(22.53, -20.44) * mm});
            skLineSegment(sketch, "E660", {"start": v(22.53, -20.44) * mm, "end": v(22.56, -20.39) * mm});
            skLineSegment(sketch, "E661", {"start": v(22.56, -20.39) * mm, "end": v(22.6, -20.34) * mm});
            skLineSegment(sketch, "E662", {"start": v(22.6, -20.34) * mm, "end": v(22.64, -20.3) * mm});
            skLineSegment(sketch, "E663", {"start": v(22.64, -20.3) * mm, "end": v(22.68, -20.27) * mm});
            skLineSegment(sketch, "E664", {"start": v(22.68, -20.27) * mm, "end": v(22.74, -20.25) * mm});
            skLineSegment(sketch, "E665", {"start": v(22.74, -20.25) * mm, "end": v(22.8, -20.25) * mm});
            skLineSegment(sketch, "E666", {"start": v(22.8, -20.25) * mm, "end": v(22.84, -20.26) * mm});
            skLineSegment(sketch, "E667", {"start": v(22.84, -20.26) * mm, "end": v(22.89, -20.27) * mm});
            skLineSegment(sketch, "E668", {"start": v(22.89, -20.27) * mm, "end": v(22.93, -20.29) * mm});
            skLineSegment(sketch, "E669", {"start": v(22.93, -20.29) * mm, "end": v(22.96, -20.3) * mm});
            skLineSegment(sketch, "E670", {"start": v(22.96, -20.3) * mm, "end": v(23, -20.32) * mm});
            skLineSegment(sketch, "E671", {"start": v(23, -20.32) * mm, "end": v(23.05, -20.3) * mm});
            skLineSegment(sketch, "E672", {"start": v(23.05, -20.3) * mm, "end": v(23.13, -20.2) * mm});
            skLineSegment(sketch, "E673", {"start": v(23.13, -20.2) * mm, "end": v(23.15, -20.16) * mm});
            skLineSegment(sketch, "E674", {"start": v(23.15, -20.16) * mm, "end": v(23.13, -20.12) * mm});
            skLineSegment(sketch, "E675", {"start": v(23.13, -20.12) * mm, "end": v(23.1, -20.08) * mm});
            skLineSegment(sketch, "E676", {"start": v(23.1, -20.08) * mm, "end": v(23.08, -20.04) * mm});
            skLineSegment(sketch, "E677", {"start": v(23.08, -20.04) * mm, "end": v(23.07, -20) * mm});
            skLineSegment(sketch, "E678", {"start": v(23.07, -20) * mm, "end": v(23.05, -19.96) * mm});
            skLineSegment(sketch, "E679", {"start": v(23.05, -19.96) * mm, "end": v(23.05, -19.9) * mm});
            skLineSegment(sketch, "E680", {"start": v(23.05, -19.9) * mm, "end": v(23.06, -19.84) * mm});
            skLineSegment(sketch, "E681", {"start": v(23.06, -19.84) * mm, "end": v(23.08, -19.8) * mm});
            skLineSegment(sketch, "E682", {"start": v(23.08, -19.8) * mm, "end": v(23.12, -19.74) * mm});
            skLineSegment(sketch, "E683", {"start": v(23.12, -19.74) * mm, "end": v(23.16, -19.7) * mm});
            skLineSegment(sketch, "E684", {"start": v(23.16, -19.7) * mm, "end": v(23.2, -19.67) * mm});
            skLineSegment(sketch, "E685", {"start": v(23.2, -19.67) * mm, "end": v(23.26, -19.65) * mm});
            skLineSegment(sketch, "E686", {"start": v(23.26, -19.65) * mm, "end": v(23.32, -19.65) * mm});
            skLineSegment(sketch, "E687", {"start": v(23.32, -19.65) * mm, "end": v(23.36, -19.65) * mm});
            skLineSegment(sketch, "E688", {"start": v(23.36, -19.65) * mm, "end": v(23.4, -19.66) * mm});
            skLineSegment(sketch, "E689", {"start": v(23.4, -19.66) * mm, "end": v(23.45, -19.68) * mm});
            skLineSegment(sketch, "E690", {"start": v(23.45, -19.68) * mm, "end": v(23.49, -19.7) * mm});
            skLineSegment(sketch, "E691", {"start": v(23.49, -19.7) * mm, "end": v(23.53, -19.7) * mm});
            skLineSegment(sketch, "E692", {"start": v(23.53, -19.7) * mm, "end": v(23.57, -19.68) * mm});
            skLineSegment(sketch, "E693", {"start": v(23.57, -19.68) * mm, "end": v(23.65, -19.6) * mm});
            skLineSegment(sketch, "E694", {"start": v(23.65, -19.6) * mm, "end": v(23.67, -19.55) * mm});
            skLineSegment(sketch, "E695", {"start": v(23.67, -19.55) * mm, "end": v(23.65, -19.5) * mm});
            skLineSegment(sketch, "E696", {"start": v(23.65, -19.5) * mm, "end": v(23.62, -19.47) * mm});
            skLineSegment(sketch, "E697", {"start": v(23.62, -19.47) * mm, "end": v(23.6, -19.43) * mm});
            skLineSegment(sketch, "E698", {"start": v(23.6, -19.43) * mm, "end": v(23.58, -19.4) * mm});
            skLineSegment(sketch, "E699", {"start": v(23.58, -19.4) * mm, "end": v(23.57, -19.35) * mm});
            skLineSegment(sketch, "E700", {"start": v(23.57, -19.35) * mm, "end": v(23.56, -19.3) * mm});
            skLineSegment(sketch, "E701", {"start": v(23.56, -19.3) * mm, "end": v(23.57, -19.23) * mm});
            skLineSegment(sketch, "E702", {"start": v(23.57, -19.23) * mm, "end": v(23.6, -19.18) * mm});
            skLineSegment(sketch, "E703", {"start": v(23.6, -19.18) * mm, "end": v(23.63, -19.13) * mm});
            skLineSegment(sketch, "E704", {"start": v(23.63, -19.13) * mm, "end": v(23.67, -19.09) * mm});
            skLineSegment(sketch, "E705", {"start": v(23.67, -19.09) * mm, "end": v(23.71, -19.06) * mm});
            skLineSegment(sketch, "E706", {"start": v(23.71, -19.06) * mm, "end": v(23.77, -19.04) * mm});
            skLineSegment(sketch, "E707", {"start": v(23.77, -19.04) * mm, "end": v(23.83, -19.03) * mm});
            skLineSegment(sketch, "E708", {"start": v(23.83, -19.03) * mm, "end": v(23.87, -19.03) * mm});
            skLineSegment(sketch, "E709", {"start": v(23.87, -19.03) * mm, "end": v(23.92, -19.04) * mm});
            skLineSegment(sketch, "E710", {"start": v(23.92, -19.04) * mm, "end": v(23.96, -19.06) * mm});
            skLineSegment(sketch, "E711", {"start": v(23.96, -19.06) * mm, "end": v(24, -19.08) * mm});
            skLineSegment(sketch, "E712", {"start": v(24, -19.08) * mm, "end": v(24.04, -19.09) * mm});
            skLineSegment(sketch, "E713", {"start": v(24.04, -19.09) * mm, "end": v(24.08, -19.06) * mm});
            skLineSegment(sketch, "E714", {"start": v(24.08, -19.06) * mm, "end": v(24.15, -18.96) * mm});
            skLineSegment(sketch, "E715", {"start": v(24.15, -18.96) * mm, "end": v(24.17, -18.92) * mm});
            skLineSegment(sketch, "E716", {"start": v(24.17, -18.92) * mm, "end": v(24.15, -18.88) * mm});
            skLineSegment(sketch, "E717", {"start": v(24.15, -18.88) * mm, "end": v(24.13, -18.85) * mm});
            skLineSegment(sketch, "E718", {"start": v(24.13, -18.85) * mm, "end": v(24.1, -18.8) * mm});
            skLineSegment(sketch, "E719", {"start": v(24.1, -18.8) * mm, "end": v(24.08, -18.77) * mm});
            skLineSegment(sketch, "E720", {"start": v(24.08, -18.77) * mm, "end": v(24.06, -18.73) * mm});
            skLineSegment(sketch, "E721", {"start": v(24.06, -18.73) * mm, "end": v(24.06, -18.67) * mm});
            skLineSegment(sketch, "E722", {"start": v(24.06, -18.67) * mm, "end": v(24.07, -18.61) * mm});
            skLineSegment(sketch, "E723", {"start": v(24.07, -18.61) * mm, "end": v(24.09, -18.56) * mm});
            skLineSegment(sketch, "E724", {"start": v(24.09, -18.56) * mm, "end": v(24.12, -18.5) * mm});
            skLineSegment(sketch, "E725", {"start": v(24.12, -18.5) * mm, "end": v(24.16, -18.46) * mm});
            skLineSegment(sketch, "E726", {"start": v(24.16, -18.46) * mm, "end": v(24.2, -18.43) * mm});
            skLineSegment(sketch, "E727", {"start": v(24.2, -18.43) * mm, "end": v(24.26, -18.4) * mm});
            skLineSegment(sketch, "E728", {"start": v(24.26, -18.4) * mm, "end": v(24.32, -18.4) * mm});
            skLineSegment(sketch, "E729", {"start": v(24.32, -18.4) * mm, "end": v(24.36, -18.4) * mm});
            skLineSegment(sketch, "E730", {"start": v(24.36, -18.4) * mm, "end": v(24.4, -18.41) * mm});
            skLineSegment(sketch, "E731", {"start": v(24.4, -18.41) * mm, "end": v(24.45, -18.43) * mm});
            skLineSegment(sketch, "E732", {"start": v(24.45, -18.43) * mm, "end": v(24.49, -18.45) * mm});
            skLineSegment(sketch, "E733", {"start": v(24.49, -18.45) * mm, "end": v(24.53, -18.45) * mm});
            skLineSegment(sketch, "E734", {"start": v(24.53, -18.45) * mm, "end": v(24.57, -18.42) * mm});
            skLineSegment(sketch, "E735", {"start": v(24.57, -18.42) * mm, "end": v(24.64, -18.33) * mm});
            skLineSegment(sketch, "E736", {"start": v(24.64, -18.33) * mm, "end": v(24.66, -18.28) * mm});
            skLineSegment(sketch, "E737", {"start": v(24.66, -18.28) * mm, "end": v(24.64, -18.24) * mm});
            skLineSegment(sketch, "E738", {"start": v(24.64, -18.24) * mm, "end": v(24.61, -18.2) * mm});
            skLineSegment(sketch, "E739", {"start": v(24.61, -18.2) * mm, "end": v(24.58, -18.17) * mm});
            skLineSegment(sketch, "E740", {"start": v(24.58, -18.17) * mm, "end": v(24.56, -18.13) * mm});
            skLineSegment(sketch, "E741", {"start": v(24.56, -18.13) * mm, "end": v(24.55, -18.09) * mm});
            skLineSegment(sketch, "E742", {"start": v(24.55, -18.09) * mm, "end": v(24.54, -18.03) * mm});
            skLineSegment(sketch, "E743", {"start": v(24.54, -18.03) * mm, "end": v(24.55, -17.97) * mm});
            skLineSegment(sketch, "E744", {"start": v(24.55, -17.97) * mm, "end": v(24.56, -17.92) * mm});
            skLineSegment(sketch, "E745", {"start": v(24.56, -17.92) * mm, "end": v(24.6, -17.87) * mm});
            skLineSegment(sketch, "E746", {"start": v(24.6, -17.87) * mm, "end": v(24.63, -17.83) * mm});
            skLineSegment(sketch, "E747", {"start": v(24.63, -17.83) * mm, "end": v(24.68, -17.8) * mm});
            skLineSegment(sketch, "E748", {"start": v(24.68, -17.8) * mm, "end": v(24.73, -17.77) * mm});
            skLineSegment(sketch, "E749", {"start": v(24.73, -17.77) * mm, "end": v(24.79, -17.76) * mm});
            skLineSegment(sketch, "E750", {"start": v(24.79, -17.76) * mm, "end": v(24.83, -17.76) * mm});
            skLineSegment(sketch, "E751", {"start": v(24.83, -17.76) * mm, "end": v(24.88, -17.77) * mm});
            skLineSegment(sketch, "E752", {"start": v(24.88, -17.77) * mm, "end": v(24.92, -17.78) * mm});
            skLineSegment(sketch, "E753", {"start": v(24.92, -17.78) * mm, "end": v(24.96, -17.8) * mm});
            skLineSegment(sketch, "E754", {"start": v(24.96, -17.8) * mm, "end": v(25, -17.8) * mm});
            skLineSegment(sketch, "E755", {"start": v(25, -17.8) * mm, "end": v(25.04, -17.77) * mm});
            skLineSegment(sketch, "E756", {"start": v(25.04, -17.77) * mm, "end": v(25.11, -17.67) * mm});
            skLineSegment(sketch, "E757", {"start": v(25.11, -17.67) * mm, "end": v(25.13, -17.63) * mm});
            skLineSegment(sketch, "E758", {"start": v(25.13, -17.63) * mm, "end": v(25.1, -17.59) * mm});
            skLineSegment(sketch, "E759", {"start": v(25.1, -17.59) * mm, "end": v(25.08, -17.56) * mm});
            skLineSegment(sketch, "E760", {"start": v(25.08, -17.56) * mm, "end": v(25.05, -17.52) * mm});
            skLineSegment(sketch, "E761", {"start": v(25.05, -17.52) * mm, "end": v(25.03, -17.48) * mm});
            skLineSegment(sketch, "E762", {"start": v(25.03, -17.48) * mm, "end": v(25.01, -17.44) * mm});
            skLineSegment(sketch, "E763", {"start": v(25.01, -17.44) * mm, "end": v(25, -17.38) * mm});
            skLineSegment(sketch, "E764", {"start": v(25, -17.38) * mm, "end": v(25, -17.33) * mm});
            skLineSegment(sketch, "E765", {"start": v(25, -17.33) * mm, "end": v(25.03, -17.27) * mm});
            skLineSegment(sketch, "E766", {"start": v(25.03, -17.27) * mm, "end": v(25.05, -17.22) * mm});
            skLineSegment(sketch, "E767", {"start": v(25.05, -17.22) * mm, "end": v(25.1, -17.17) * mm});
            skLineSegment(sketch, "E768", {"start": v(25.1, -17.17) * mm, "end": v(25.14, -17.14) * mm});
            skLineSegment(sketch, "E769", {"start": v(25.14, -17.14) * mm, "end": v(25.19, -17.11) * mm});
            skLineSegment(sketch, "E770", {"start": v(25.19, -17.11) * mm, "end": v(25.25, -17.1) * mm});
            skLineSegment(sketch, "E771", {"start": v(25.25, -17.1) * mm, "end": v(25.3, -17.1) * mm});
            skLineSegment(sketch, "E772", {"start": v(25.3, -17.1) * mm, "end": v(25.34, -17.1) * mm});
            skLineSegment(sketch, "E773", {"start": v(25.34, -17.1) * mm, "end": v(25.38, -17.12) * mm});
            skLineSegment(sketch, "E774", {"start": v(25.38, -17.12) * mm, "end": v(25.42, -17.14) * mm});
            skLineSegment(sketch, "E775", {"start": v(25.42, -17.14) * mm, "end": v(25.46, -17.14) * mm});
            skLineSegment(sketch, "E776", {"start": v(25.46, -17.14) * mm, "end": v(25.5, -17.11) * mm});
            skLineSegment(sketch, "E777", {"start": v(25.5, -17.11) * mm, "end": v(25.57, -17.01) * mm});
            skLineSegment(sketch, "E778", {"start": v(25.57, -17.01) * mm, "end": v(25.58, -16.97) * mm});
            skLineSegment(sketch, "E779", {"start": v(25.58, -16.97) * mm, "end": v(25.56, -16.93) * mm});
            skLineSegment(sketch, "E780", {"start": v(25.56, -16.93) * mm, "end": v(25.53, -16.9) * mm});
            skLineSegment(sketch, "E781", {"start": v(25.53, -16.9) * mm, "end": v(25.5, -16.86) * mm});
            skLineSegment(sketch, "E782", {"start": v(25.5, -16.86) * mm, "end": v(25.48, -16.82) * mm});
            skLineSegment(sketch, "E783", {"start": v(25.48, -16.82) * mm, "end": v(25.46, -16.78) * mm});
            skLineSegment(sketch, "E784", {"start": v(25.46, -16.78) * mm, "end": v(25.45, -16.72) * mm});
            skLineSegment(sketch, "E785", {"start": v(25.45, -16.72) * mm, "end": v(25.45, -16.67) * mm});
            skLineSegment(sketch, "E786", {"start": v(25.45, -16.67) * mm, "end": v(25.47, -16.6) * mm});
            skLineSegment(sketch, "E787", {"start": v(25.47, -16.6) * mm, "end": v(25.5, -16.56) * mm});
            skLineSegment(sketch, "E788", {"start": v(25.5, -16.56) * mm, "end": v(25.53, -16.51) * mm});
            skLineSegment(sketch, "E789", {"start": v(25.53, -16.51) * mm, "end": v(25.58, -16.47) * mm});
            skLineSegment(sketch, "E790", {"start": v(25.58, -16.47) * mm, "end": v(25.63, -16.45) * mm});
            skLineSegment(sketch, "E791", {"start": v(25.63, -16.45) * mm, "end": v(25.68, -16.43) * mm});
            skLineSegment(sketch, "E792", {"start": v(25.68, -16.43) * mm, "end": v(25.73, -16.43) * mm});
            skLineSegment(sketch, "E793", {"start": v(25.73, -16.43) * mm, "end": v(25.77, -16.44) * mm});
            skLineSegment(sketch, "E794", {"start": v(25.77, -16.44) * mm, "end": v(25.82, -16.45) * mm});
            skLineSegment(sketch, "E795", {"start": v(25.82, -16.45) * mm, "end": v(25.86, -16.47) * mm});
            skLineSegment(sketch, "E796", {"start": v(25.86, -16.47) * mm, "end": v(25.9, -16.47) * mm});
            skLineSegment(sketch, "E797", {"start": v(25.9, -16.47) * mm, "end": v(25.94, -16.44) * mm});
            skLineSegment(sketch, "E798", {"start": v(25.94, -16.44) * mm, "end": v(26, -16.34) * mm});
            skLineSegment(sketch, "E799", {"start": v(26, -16.34) * mm, "end": v(26.02, -16.3) * mm});
            skLineSegment(sketch, "E800", {"start": v(26.02, -16.3) * mm, "end": v(26, -16.25) * mm});
            skLineSegment(sketch, "E801", {"start": v(26, -16.25) * mm, "end": v(25.96, -16.22) * mm});
            skLineSegment(sketch, "E802", {"start": v(25.96, -16.22) * mm, "end": v(25.93, -16.19) * mm});
            skLineSegment(sketch, "E803", {"start": v(25.93, -16.19) * mm, "end": v(25.91, -16.15) * mm});
            skLineSegment(sketch, "E804", {"start": v(25.91, -16.15) * mm, "end": v(25.89, -16.1) * mm});
            skLineSegment(sketch, "E805", {"start": v(25.89, -16.1) * mm, "end": v(25.88, -16.05) * mm});
            skLineSegment(sketch, "E806", {"start": v(25.88, -16.05) * mm, "end": v(25.88, -16) * mm});
            skLineSegment(sketch, "E807", {"start": v(25.88, -16) * mm, "end": v(25.9, -15.94) * mm});
            skLineSegment(sketch, "E808", {"start": v(25.9, -15.94) * mm, "end": v(25.92, -15.88) * mm});
            skLineSegment(sketch, "E809", {"start": v(25.92, -15.88) * mm, "end": v(25.96, -15.84) * mm});
            skLineSegment(sketch, "E810", {"start": v(25.96, -15.84) * mm, "end": v(26, -15.8) * mm});
            skLineSegment(sketch, "E811", {"start": v(26, -15.8) * mm, "end": v(26.05, -15.77) * mm});
            skLineSegment(sketch, "E812", {"start": v(26.05, -15.77) * mm, "end": v(26.1, -15.76) * mm});
            skLineSegment(sketch, "E813", {"start": v(26.1, -15.76) * mm, "end": v(26.15, -15.75) * mm});
            skLineSegment(sketch, "E814", {"start": v(26.15, -15.75) * mm, "end": v(26.2, -15.76) * mm});
            skLineSegment(sketch, "E815", {"start": v(26.2, -15.76) * mm, "end": v(26.24, -15.77) * mm});
            skLineSegment(sketch, "E816", {"start": v(26.24, -15.77) * mm, "end": v(26.28, -15.78) * mm});
            skLineSegment(sketch, "E817", {"start": v(26.28, -15.78) * mm, "end": v(26.33, -15.78) * mm});
            skLineSegment(sketch, "E818", {"start": v(26.33, -15.78) * mm, "end": v(26.36, -15.75) * mm});
            skLineSegment(sketch, "E819", {"start": v(26.36, -15.75) * mm, "end": v(26.42, -15.65) * mm});
            skLineSegment(sketch, "E820", {"start": v(26.42, -15.65) * mm, "end": v(26.43, -15.6) * mm});
            skLineSegment(sketch, "E821", {"start": v(26.43, -15.6) * mm, "end": v(26.41, -15.56) * mm});
            skLineSegment(sketch, "E822", {"start": v(26.41, -15.56) * mm, "end": v(26.38, -15.54) * mm});
            skLineSegment(sketch, "E823", {"start": v(26.38, -15.54) * mm, "end": v(26.35, -15.5) * mm});
            skLineSegment(sketch, "E824", {"start": v(26.35, -15.5) * mm, "end": v(26.32, -15.46) * mm});
            skLineSegment(sketch, "E825", {"start": v(26.32, -15.46) * mm, "end": v(26.3, -15.42) * mm});
            skLineSegment(sketch, "E826", {"start": v(26.3, -15.42) * mm, "end": v(26.3, -15.37) * mm});
            skLineSegment(sketch, "E827", {"start": v(26.3, -15.37) * mm, "end": v(26.3, -15.31) * mm});
            skLineSegment(sketch, "E828", {"start": v(26.3, -15.31) * mm, "end": v(26.3, -15.25) * mm});
            skLineSegment(sketch, "E829", {"start": v(26.3, -15.25) * mm, "end": v(26.33, -15.2) * mm});
            skLineSegment(sketch, "E830", {"start": v(26.33, -15.2) * mm, "end": v(26.36, -15.15) * mm});
            skLineSegment(sketch, "E831", {"start": v(26.36, -15.15) * mm, "end": v(26.4, -15.11) * mm});
            skLineSegment(sketch, "E832", {"start": v(26.4, -15.11) * mm, "end": v(26.45, -15.08) * mm});
            skLineSegment(sketch, "E833", {"start": v(26.45, -15.08) * mm, "end": v(26.5, -15.07) * mm});
            skLineSegment(sketch, "E834", {"start": v(26.5, -15.07) * mm, "end": v(26.55, -15.06) * mm});
            skLineSegment(sketch, "E835", {"start": v(26.55, -15.06) * mm, "end": v(26.6, -15.07) * mm});
            skLineSegment(sketch, "E836", {"start": v(26.6, -15.07) * mm, "end": v(26.64, -15.08) * mm});
            skLineSegment(sketch, "E837", {"start": v(26.64, -15.08) * mm, "end": v(26.69, -15.1) * mm});
            skLineSegment(sketch, "E838", {"start": v(26.69, -15.1) * mm, "end": v(26.73, -15.1) * mm});
            skLineSegment(sketch, "E839", {"start": v(26.73, -15.1) * mm, "end": v(26.76, -15.06) * mm});
            skLineSegment(sketch, "E840", {"start": v(26.76, -15.06) * mm, "end": v(26.82, -14.95) * mm});
            skLineSegment(sketch, "E841", {"start": v(26.82, -14.95) * mm, "end": v(26.83, -14.9) * mm});
            skLineSegment(sketch, "E842", {"start": v(26.83, -14.9) * mm, "end": v(26.81, -14.87) * mm});
            skLineSegment(sketch, "E843", {"start": v(26.81, -14.87) * mm, "end": v(26.78, -14.84) * mm});
            skLineSegment(sketch, "E844", {"start": v(26.78, -14.84) * mm, "end": v(26.75, -14.8) * mm});
            skLineSegment(sketch, "E845", {"start": v(26.75, -14.8) * mm, "end": v(26.72, -14.77) * mm});
            skLineSegment(sketch, "E846", {"start": v(26.72, -14.77) * mm, "end": v(26.7, -14.73) * mm});
            skLineSegment(sketch, "E847", {"start": v(26.7, -14.73) * mm, "end": v(26.68, -14.67) * mm});
            skLineSegment(sketch, "E848", {"start": v(26.68, -14.67) * mm, "end": v(26.68, -14.62) * mm});
            skLineSegment(sketch, "E849", {"start": v(26.68, -14.62) * mm, "end": v(26.7, -14.56) * mm});
            skLineSegment(sketch, "E850", {"start": v(26.7, -14.56) * mm, "end": v(26.72, -14.5) * mm});
            skLineSegment(sketch, "E851", {"start": v(26.72, -14.5) * mm, "end": v(26.75, -14.46) * mm});
            skLineSegment(sketch, "E852", {"start": v(26.75, -14.46) * mm, "end": v(26.8, -14.42) * mm});
            skLineSegment(sketch, "E853", {"start": v(26.8, -14.42) * mm, "end": v(26.84, -14.39) * mm});
            skLineSegment(sketch, "E854", {"start": v(26.84, -14.39) * mm, "end": v(26.9, -14.37) * mm});
            skLineSegment(sketch, "E855", {"start": v(26.9, -14.37) * mm, "end": v(26.94, -14.36) * mm});
            skLineSegment(sketch, "E856", {"start": v(26.94, -14.36) * mm, "end": v(26.99, -14.37) * mm});
            skLineSegment(sketch, "E857", {"start": v(26.99, -14.37) * mm, "end": v(27.03, -14.37) * mm});
            skLineSegment(sketch, "E858", {"start": v(27.03, -14.37) * mm, "end": v(27.07, -14.39) * mm});
            skLineSegment(sketch, "E859", {"start": v(27.07, -14.39) * mm, "end": v(27.12, -14.39) * mm});
            skLineSegment(sketch, "E860", {"start": v(27.12, -14.39) * mm, "end": v(27.15, -14.35) * mm});
            skLineSegment(sketch, "E861", {"start": v(27.15, -14.35) * mm, "end": v(27.2, -14.25) * mm});
            skLineSegment(sketch, "E862", {"start": v(27.2, -14.25) * mm, "end": v(27.21, -14.2) * mm});
            skLineSegment(sketch, "E863", {"start": v(27.21, -14.2) * mm, "end": v(27.2, -14.16) * mm});
            skLineSegment(sketch, "E864", {"start": v(27.2, -14.16) * mm, "end": v(27.16, -14.13) * mm});
            skLineSegment(sketch, "E865", {"start": v(27.16, -14.13) * mm, "end": v(27.12, -14.1) * mm});
            skLineSegment(sketch, "E866", {"start": v(27.12, -14.1) * mm, "end": v(27.1, -14.07) * mm});
            skLineSegment(sketch, "E867", {"start": v(27.1, -14.07) * mm, "end": v(27.07, -14.03) * mm});
            skLineSegment(sketch, "E868", {"start": v(27.07, -14.03) * mm, "end": v(27.06, -13.97) * mm});
            skLineSegment(sketch, "E869", {"start": v(27.06, -13.97) * mm, "end": v(27.06, -13.91) * mm});
            skLineSegment(sketch, "E870", {"start": v(27.06, -13.91) * mm, "end": v(27.07, -13.86) * mm});
            skLineSegment(sketch, "E871", {"start": v(27.07, -13.86) * mm, "end": v(27.09, -13.8) * mm});
            skLineSegment(sketch, "E872", {"start": v(27.09, -13.8) * mm, "end": v(27.12, -13.75) * mm});
            skLineSegment(sketch, "E873", {"start": v(27.12, -13.75) * mm, "end": v(27.16, -13.71) * mm});
            skLineSegment(sketch, "E874", {"start": v(27.16, -13.71) * mm, "end": v(27.2, -13.68) * mm});
            skLineSegment(sketch, "E875", {"start": v(27.2, -13.68) * mm, "end": v(27.26, -13.66) * mm});
            skLineSegment(sketch, "E876", {"start": v(27.26, -13.66) * mm, "end": v(27.3, -13.65) * mm});
            skLineSegment(sketch, "E877", {"start": v(27.3, -13.65) * mm, "end": v(27.35, -13.66) * mm});
            skLineSegment(sketch, "E878", {"start": v(27.35, -13.66) * mm, "end": v(27.4, -13.66) * mm});
            skLineSegment(sketch, "E879", {"start": v(27.4, -13.66) * mm, "end": v(27.44, -13.67) * mm});
            skLineSegment(sketch, "E880", {"start": v(27.44, -13.67) * mm, "end": v(27.48, -13.67) * mm});
            skLineSegment(sketch, "E881", {"start": v(27.48, -13.67) * mm, "end": v(27.52, -13.64) * mm});
            skLineSegment(sketch, "E882", {"start": v(27.52, -13.64) * mm, "end": v(27.57, -13.53) * mm});
            skLineSegment(sketch, "E883", {"start": v(27.57, -13.53) * mm, "end": v(27.58, -13.48) * mm});
            skLineSegment(sketch, "E884", {"start": v(27.58, -13.48) * mm, "end": v(27.55, -13.44) * mm});
            skLineSegment(sketch, "E885", {"start": v(27.55, -13.44) * mm, "end": v(27.52, -13.42) * mm});
            skLineSegment(sketch, "E886", {"start": v(27.52, -13.42) * mm, "end": v(27.48, -13.39) * mm});
            skLineSegment(sketch, "E887", {"start": v(27.48, -13.39) * mm, "end": v(27.46, -13.35) * mm});
            skLineSegment(sketch, "E888", {"start": v(27.46, -13.35) * mm, "end": v(27.43, -13.31) * mm});
            skLineSegment(sketch, "E889", {"start": v(27.43, -13.31) * mm, "end": v(27.41, -13.26) * mm});
            skLineSegment(sketch, "E890", {"start": v(27.41, -13.26) * mm, "end": v(27.41, -13.2) * mm});
            skLineSegment(sketch, "E891", {"start": v(27.41, -13.2) * mm, "end": v(27.42, -13.14) * mm});
            skLineSegment(sketch, "E892", {"start": v(27.42, -13.14) * mm, "end": v(27.44, -13.09) * mm});
            skLineSegment(sketch, "E893", {"start": v(27.44, -13.09) * mm, "end": v(27.47, -13.04) * mm});
            skLineSegment(sketch, "E894", {"start": v(27.47, -13.04) * mm, "end": v(27.5, -13) * mm});
            skLineSegment(sketch, "E895", {"start": v(27.5, -13) * mm, "end": v(27.56, -12.96) * mm});
            skLineSegment(sketch, "E896", {"start": v(27.56, -12.96) * mm, "end": v(27.6, -12.94) * mm});
            skLineSegment(sketch, "E897", {"start": v(27.6, -12.94) * mm, "end": v(27.65, -12.94) * mm});
            skLineSegment(sketch, "E898", {"start": v(27.65, -12.94) * mm, "end": v(27.7, -12.93) * mm});
            skLineSegment(sketch, "E899", {"start": v(27.7, -12.93) * mm, "end": v(27.74, -12.94) * mm});
            skLineSegment(sketch, "E900", {"start": v(27.74, -12.94) * mm, "end": v(27.79, -12.95) * mm});
            skLineSegment(sketch, "E901", {"start": v(27.79, -12.95) * mm, "end": v(27.83, -12.95) * mm});
            skLineSegment(sketch, "E902", {"start": v(27.83, -12.95) * mm, "end": v(27.86, -12.91) * mm});
            skLineSegment(sketch, "E903", {"start": v(27.86, -12.91) * mm, "end": v(27.91, -12.8) * mm});
            skLineSegment(sketch, "E904", {"start": v(27.91, -12.8) * mm, "end": v(27.92, -12.75) * mm});
            skLineSegment(sketch, "E905", {"start": v(27.92, -12.75) * mm, "end": v(27.9, -12.72) * mm});
            skLineSegment(sketch, "E906", {"start": v(27.9, -12.72) * mm, "end": v(27.86, -12.7) * mm});
            skLineSegment(sketch, "E907", {"start": v(27.86, -12.7) * mm, "end": v(27.83, -12.66) * mm});
            skLineSegment(sketch, "E908", {"start": v(27.83, -12.66) * mm, "end": v(27.8, -12.63) * mm});
            skLineSegment(sketch, "E909", {"start": v(27.8, -12.63) * mm, "end": v(27.77, -12.6) * mm});
            skLineSegment(sketch, "E910", {"start": v(27.77, -12.6) * mm, "end": v(27.75, -12.54) * mm});
            skLineSegment(sketch, "E911", {"start": v(27.75, -12.54) * mm, "end": v(27.75, -12.48) * mm});
            skLineSegment(sketch, "E912", {"start": v(27.75, -12.48) * mm, "end": v(27.75, -12.42) * mm});
            skLineSegment(sketch, "E913", {"start": v(27.75, -12.42) * mm, "end": v(27.77, -12.36) * mm});
            skLineSegment(sketch, "E914", {"start": v(27.77, -12.36) * mm, "end": v(27.8, -12.31) * mm});
            skLineSegment(sketch, "E915", {"start": v(27.8, -12.31) * mm, "end": v(27.84, -12.27) * mm});
            skLineSegment(sketch, "E916", {"start": v(27.84, -12.27) * mm, "end": v(27.89, -12.24) * mm});
            skLineSegment(sketch, "E917", {"start": v(27.89, -12.24) * mm, "end": v(27.94, -12.21) * mm});
            skLineSegment(sketch, "E918", {"start": v(27.94, -12.21) * mm, "end": v(27.98, -12.2) * mm});
            skLineSegment(sketch, "E919", {"start": v(27.98, -12.2) * mm, "end": v(28.03, -12.2) * mm});
            skLineSegment(sketch, "E920", {"start": v(28.03, -12.2) * mm, "end": v(28.07, -12.2) * mm});
            skLineSegment(sketch, "E921", {"start": v(28.07, -12.2) * mm, "end": v(28.12, -12.22) * mm});
            skLineSegment(sketch, "E922", {"start": v(28.12, -12.22) * mm, "end": v(28.16, -12.21) * mm});
            skLineSegment(sketch, "E923", {"start": v(28.16, -12.21) * mm, "end": v(28.2, -12.18) * mm});
            skLineSegment(sketch, "E924", {"start": v(28.2, -12.18) * mm, "end": v(28.24, -12.07) * mm});
            skLineSegment(sketch, "E925", {"start": v(28.24, -12.07) * mm, "end": v(28.24, -12.02) * mm});
            skLineSegment(sketch, "E926", {"start": v(28.24, -12.02) * mm, "end": v(28.22, -11.98) * mm});
            skLineSegment(sketch, "E927", {"start": v(28.22, -11.98) * mm, "end": v(28.18, -11.96) * mm});
            skLineSegment(sketch, "E928", {"start": v(28.18, -11.96) * mm, "end": v(28.15, -11.93) * mm});
            skLineSegment(sketch, "E929", {"start": v(28.15, -11.93) * mm, "end": v(28.12, -11.9) * mm});
            skLineSegment(sketch, "E930", {"start": v(28.12, -11.9) * mm, "end": v(28.1, -11.86) * mm});
            skLineSegment(sketch, "E931", {"start": v(28.1, -11.86) * mm, "end": v(28.07, -11.8) * mm});
            skLineSegment(sketch, "E932", {"start": v(28.07, -11.8) * mm, "end": v(28.06, -11.75) * mm});
            skLineSegment(sketch, "E933", {"start": v(28.06, -11.75) * mm, "end": v(28.07, -11.69) * mm});
            skLineSegment(sketch, "E934", {"start": v(28.07, -11.69) * mm, "end": v(28.09, -11.63) * mm});
            skLineSegment(sketch, "E935", {"start": v(28.09, -11.63) * mm, "end": v(28.11, -11.58) * mm});
            skLineSegment(sketch, "E936", {"start": v(28.11, -11.58) * mm, "end": v(28.15, -11.54) * mm});
            skLineSegment(sketch, "E937", {"start": v(28.15, -11.54) * mm, "end": v(28.2, -11.5) * mm});
            skLineSegment(sketch, "E938", {"start": v(28.2, -11.5) * mm, "end": v(28.25, -11.48) * mm});
            skLineSegment(sketch, "E939", {"start": v(28.25, -11.48) * mm, "end": v(28.3, -11.47) * mm});
            skLineSegment(sketch, "E940", {"start": v(28.3, -11.47) * mm, "end": v(28.34, -11.47) * mm});
            skLineSegment(sketch, "E941", {"start": v(28.34, -11.47) * mm, "end": v(28.38, -11.47) * mm});
            skLineSegment(sketch, "E942", {"start": v(28.38, -11.47) * mm, "end": v(28.43, -11.48) * mm});
            skLineSegment(sketch, "E943", {"start": v(28.43, -11.48) * mm, "end": v(28.47, -11.47) * mm});
            skLineSegment(sketch, "E944", {"start": v(28.47, -11.47) * mm, "end": v(28.5, -11.44) * mm});
            skLineSegment(sketch, "E945", {"start": v(28.5, -11.44) * mm, "end": v(28.55, -11.32) * mm});
            skLineSegment(sketch, "E946", {"start": v(28.55, -11.32) * mm, "end": v(28.55, -11.28) * mm});
            skLineSegment(sketch, "E947", {"start": v(28.55, -11.28) * mm, "end": v(28.52, -11.24) * mm});
            skLineSegment(sketch, "E948", {"start": v(28.52, -11.24) * mm, "end": v(28.48, -11.22) * mm});
            skLineSegment(sketch, "E949", {"start": v(28.48, -11.22) * mm, "end": v(28.45, -11.19) * mm});
            skLineSegment(sketch, "E950", {"start": v(28.45, -11.19) * mm, "end": v(28.42, -11.16) * mm});
            skLineSegment(sketch, "E951", {"start": v(28.42, -11.16) * mm, "end": v(28.4, -11.12) * mm});
            skLineSegment(sketch, "E952", {"start": v(28.4, -11.12) * mm, "end": v(28.37, -11.07) * mm});
            skLineSegment(sketch, "E953", {"start": v(28.37, -11.07) * mm, "end": v(28.36, -11) * mm});
            skLineSegment(sketch, "E954", {"start": v(28.36, -11) * mm, "end": v(28.37, -10.95) * mm});
            skLineSegment(sketch, "E955", {"start": v(28.37, -10.95) * mm, "end": v(28.38, -10.9) * mm});
            skLineSegment(sketch, "E956", {"start": v(28.38, -10.9) * mm, "end": v(28.4, -10.84) * mm});
            skLineSegment(sketch, "E957", {"start": v(28.4, -10.84) * mm, "end": v(28.44, -10.8) * mm});
            skLineSegment(sketch, "E958", {"start": v(28.44, -10.8) * mm, "end": v(28.49, -10.76) * mm});
            skLineSegment(sketch, "E959", {"start": v(28.49, -10.76) * mm, "end": v(28.54, -10.73) * mm});
            skLineSegment(sketch, "E960", {"start": v(28.54, -10.73) * mm, "end": v(28.58, -10.73) * mm});
            skLineSegment(sketch, "E961", {"start": v(28.58, -10.73) * mm, "end": v(28.63, -10.72) * mm});
            skLineSegment(sketch, "E962", {"start": v(28.63, -10.72) * mm, "end": v(28.67, -10.72) * mm});
            skLineSegment(sketch, "E963", {"start": v(28.67, -10.72) * mm, "end": v(28.72, -10.73) * mm});
            skLineSegment(sketch, "E964", {"start": v(28.72, -10.73) * mm, "end": v(28.76, -10.72) * mm});
            skLineSegment(sketch, "E965", {"start": v(28.76, -10.72) * mm, "end": v(28.8, -10.69) * mm});
            skLineSegment(sketch, "E966", {"start": v(28.8, -10.69) * mm, "end": v(28.83, -10.57) * mm});
            skLineSegment(sketch, "E967", {"start": v(28.83, -10.57) * mm, "end": v(28.83, -10.53) * mm});
            skLineSegment(sketch, "E968", {"start": v(28.83, -10.53) * mm, "end": v(28.8, -10.5) * mm});
            skLineSegment(sketch, "E969", {"start": v(28.8, -10.5) * mm, "end": v(28.77, -10.47) * mm});
            skLineSegment(sketch, "E970", {"start": v(28.77, -10.47) * mm, "end": v(28.73, -10.44) * mm});
            skLineSegment(sketch, "E971", {"start": v(28.73, -10.44) * mm, "end": v(28.7, -10.4) * mm});
            skLineSegment(sketch, "E972", {"start": v(28.7, -10.4) * mm, "end": v(28.67, -10.37) * mm});
            skLineSegment(sketch, "E973", {"start": v(28.67, -10.37) * mm, "end": v(28.65, -10.32) * mm});
            skLineSegment(sketch, "E974", {"start": v(28.65, -10.32) * mm, "end": v(28.64, -10.26) * mm});
            skLineSegment(sketch, "E975", {"start": v(28.64, -10.26) * mm, "end": v(28.64, -10.2) * mm});
            skLineSegment(sketch, "E976", {"start": v(28.64, -10.2) * mm, "end": v(28.66, -10.15) * mm});
            skLineSegment(sketch, "E977", {"start": v(28.66, -10.15) * mm, "end": v(28.68, -10.1) * mm});
            skLineSegment(sketch, "E978", {"start": v(28.68, -10.1) * mm, "end": v(28.72, -10.05) * mm});
            skLineSegment(sketch, "E979", {"start": v(28.72, -10.05) * mm, "end": v(28.76, -10.01) * mm});
            skLineSegment(sketch, "E980", {"start": v(28.76, -10.01) * mm, "end": v(28.81, -9.98) * mm});
            skLineSegment(sketch, "E981", {"start": v(28.81, -9.98) * mm, "end": v(28.86, -9.97) * mm});
            skLineSegment(sketch, "E982", {"start": v(28.86, -9.97) * mm, "end": v(28.9, -9.97) * mm});
            skLineSegment(sketch, "E983", {"start": v(28.9, -9.97) * mm, "end": v(28.94, -9.97) * mm});
            skLineSegment(sketch, "E984", {"start": v(28.94, -9.97) * mm, "end": v(28.99, -9.98) * mm});
            skLineSegment(sketch, "E985", {"start": v(28.99, -9.98) * mm, "end": v(29.03, -9.97) * mm});
            skLineSegment(sketch, "E986", {"start": v(29.03, -9.97) * mm, "end": v(29.06, -9.93) * mm});
            skLineSegment(sketch, "E987", {"start": v(29.06, -9.93) * mm, "end": v(29.1, -9.81) * mm});
            skLineSegment(sketch, "E988", {"start": v(29.1, -9.81) * mm, "end": v(29.1, -9.77) * mm});
            skLineSegment(sketch, "E989", {"start": v(29.1, -9.77) * mm, "end": v(29.07, -9.73) * mm});
            skLineSegment(sketch, "E990", {"start": v(29.07, -9.73) * mm, "end": v(29.03, -9.71) * mm});
            skLineSegment(sketch, "E991", {"start": v(29.03, -9.71) * mm, "end": v(29, -9.68) * mm});
            skLineSegment(sketch, "E992", {"start": v(29, -9.68) * mm, "end": v(28.96, -9.65) * mm});
            skLineSegment(sketch, "E993", {"start": v(28.96, -9.65) * mm, "end": v(28.93, -9.62) * mm});
            skLineSegment(sketch, "E994", {"start": v(28.93, -9.62) * mm, "end": v(28.91, -9.57) * mm});
            skLineSegment(sketch, "E995", {"start": v(28.91, -9.57) * mm, "end": v(28.9, -9.5) * mm});
            skLineSegment(sketch, "E996", {"start": v(28.9, -9.5) * mm, "end": v(28.9, -9.45) * mm});
            skLineSegment(sketch, "E997", {"start": v(28.9, -9.45) * mm, "end": v(28.91, -9.4) * mm});
            skLineSegment(sketch, "E998", {"start": v(28.91, -9.4) * mm, "end": v(28.94, -9.34) * mm});
            skLineSegment(sketch, "E999", {"start": v(28.94, -9.34) * mm, "end": v(28.97, -9.3) * mm});
            skLineSegment(sketch, "E1000", {"start": v(28.97, -9.3) * mm, "end": v(29.01, -9.25) * mm});
            skLineSegment(sketch, "E1001", {"start": v(29.01, -9.25) * mm, "end": v(29.06, -9.23) * mm});
            skLineSegment(sketch, "E1002", {"start": v(29.06, -9.23) * mm, "end": v(29.1, -9.21) * mm});
            skLineSegment(sketch, "E1003", {"start": v(29.1, -9.21) * mm, "end": v(29.15, -9.2) * mm});
            skLineSegment(sketch, "E1004", {"start": v(29.15, -9.2) * mm, "end": v(29.2, -9.2) * mm});
            skLineSegment(sketch, "E1005", {"start": v(29.2, -9.2) * mm, "end": v(29.24, -9.21) * mm});
            skLineSegment(sketch, "E1006", {"start": v(29.24, -9.21) * mm, "end": v(29.28, -9.2) * mm});
            skLineSegment(sketch, "E1007", {"start": v(29.28, -9.2) * mm, "end": v(29.31, -9.16) * mm});
            skLineSegment(sketch, "E1008", {"start": v(29.31, -9.16) * mm, "end": v(29.35, -9.05) * mm});
            skLineSegment(sketch, "E1009", {"start": v(29.35, -9.05) * mm, "end": v(29.35, -9) * mm});
            skLineSegment(sketch, "E1010", {"start": v(29.35, -9) * mm, "end": v(29.32, -8.97) * mm});
            skLineSegment(sketch, "E1011", {"start": v(29.32, -8.97) * mm, "end": v(29.28, -8.95) * mm});
            skLineSegment(sketch, "E1012", {"start": v(29.28, -8.95) * mm, "end": v(29.24, -8.92) * mm});
            skLineSegment(sketch, "E1013", {"start": v(29.24, -8.92) * mm, "end": v(29.2, -8.9) * mm});
            skLineSegment(sketch, "E1014", {"start": v(29.2, -8.9) * mm, "end": v(29.18, -8.86) * mm});
            skLineSegment(sketch, "E1015", {"start": v(29.18, -8.86) * mm, "end": v(29.15, -8.8) * mm});
            skLineSegment(sketch, "E1016", {"start": v(29.15, -8.8) * mm, "end": v(29.14, -8.75) * mm});
            skLineSegment(sketch, "E1017", {"start": v(29.14, -8.75) * mm, "end": v(29.14, -8.7) * mm});
            skLineSegment(sketch, "E1018", {"start": v(29.14, -8.7) * mm, "end": v(29.15, -8.63) * mm});
            skLineSegment(sketch, "E1019", {"start": v(29.15, -8.63) * mm, "end": v(29.17, -8.58) * mm});
            skLineSegment(sketch, "E1020", {"start": v(29.17, -8.58) * mm, "end": v(29.2, -8.53) * mm});
            skLineSegment(sketch, "E1021", {"start": v(29.2, -8.53) * mm, "end": v(29.24, -8.5) * mm});
            skLineSegment(sketch, "E1022", {"start": v(29.24, -8.5) * mm, "end": v(29.3, -8.46) * mm});
            skLineSegment(sketch, "E1023", {"start": v(29.3, -8.46) * mm, "end": v(29.34, -8.45) * mm});
            skLineSegment(sketch, "E1024", {"start": v(29.34, -8.45) * mm, "end": v(29.38, -8.44) * mm});
            skLineSegment(sketch, "E1025", {"start": v(29.38, -8.44) * mm, "end": v(29.43, -8.44) * mm});
            skLineSegment(sketch, "E1026", {"start": v(29.43, -8.44) * mm, "end": v(29.47, -8.44) * mm});
            skLineSegment(sketch, "E1027", {"start": v(29.47, -8.44) * mm, "end": v(29.51, -8.43) * mm});
            skLineSegment(sketch, "E1028", {"start": v(29.51, -8.43) * mm, "end": v(29.54, -8.4) * mm});
            skLineSegment(sketch, "E1029", {"start": v(29.54, -8.4) * mm, "end": v(29.57, -8.28) * mm});
            skLineSegment(sketch, "E1030", {"start": v(29.57, -8.28) * mm, "end": v(29.57, -8.23) * mm});
            skLineSegment(sketch, "E1031", {"start": v(29.57, -8.23) * mm, "end": v(29.54, -8.2) * mm});
            skLineSegment(sketch, "E1032", {"start": v(29.54, -8.2) * mm, "end": v(29.5, -8.18) * mm});
            skLineSegment(sketch, "E1033", {"start": v(29.5, -8.18) * mm, "end": v(29.46, -8.15) * mm});
            skLineSegment(sketch, "E1034", {"start": v(29.46, -8.15) * mm, "end": v(29.43, -8.12) * mm});
            skLineSegment(sketch, "E1035", {"start": v(29.43, -8.12) * mm, "end": v(29.4, -8.1) * mm});
            skLineSegment(sketch, "E1036", {"start": v(29.4, -8.1) * mm, "end": v(29.37, -8.04) * mm});
            skLineSegment(sketch, "E1037", {"start": v(29.37, -8.04) * mm, "end": v(29.36, -7.98) * mm});
            skLineSegment(sketch, "E1038", {"start": v(29.36, -7.98) * mm, "end": v(29.35, -7.93) * mm});
            skLineSegment(sketch, "E1039", {"start": v(29.35, -7.93) * mm, "end": v(29.36, -7.87) * mm});
            skLineSegment(sketch, "E1040", {"start": v(29.36, -7.87) * mm, "end": v(29.39, -7.81) * mm});
            skLineSegment(sketch, "E1041", {"start": v(29.39, -7.81) * mm, "end": v(29.42, -7.76) * mm});
            skLineSegment(sketch, "E1042", {"start": v(29.42, -7.76) * mm, "end": v(29.46, -7.72) * mm});
            skLineSegment(sketch, "E1043", {"start": v(29.46, -7.72) * mm, "end": v(29.5, -7.7) * mm});
            skLineSegment(sketch, "E1044", {"start": v(29.5, -7.7) * mm, "end": v(29.55, -7.68) * mm});
            skLineSegment(sketch, "E1045", {"start": v(29.55, -7.68) * mm, "end": v(29.6, -7.67) * mm});
            skLineSegment(sketch, "E1046", {"start": v(29.6, -7.67) * mm, "end": v(29.64, -7.67) * mm});
            skLineSegment(sketch, "E1047", {"start": v(29.64, -7.67) * mm, "end": v(29.68, -7.67) * mm});
            skLineSegment(sketch, "E1048", {"start": v(29.68, -7.67) * mm, "end": v(29.72, -7.66) * mm});
            skLineSegment(sketch, "E1049", {"start": v(29.72, -7.66) * mm, "end": v(29.75, -7.62) * mm});
            skLineSegment(sketch, "E1050", {"start": v(29.75, -7.62) * mm, "end": v(29.78, -7.5) * mm});
            skLineSegment(sketch, "E1051", {"start": v(29.78, -7.5) * mm, "end": v(29.78, -7.45) * mm});
            skLineSegment(sketch, "E1052", {"start": v(29.78, -7.45) * mm, "end": v(29.75, -7.42) * mm});
            skLineSegment(sketch, "E1053", {"start": v(29.75, -7.42) * mm, "end": v(29.7, -7.4) * mm});
            skLineSegment(sketch, "E1054", {"start": v(29.7, -7.4) * mm, "end": v(29.67, -7.38) * mm});
            skLineSegment(sketch, "E1055", {"start": v(29.67, -7.38) * mm, "end": v(29.63, -7.35) * mm});
            skLineSegment(sketch, "E1056", {"start": v(29.63, -7.35) * mm, "end": v(29.6, -7.32) * mm});
            skLineSegment(sketch, "E1057", {"start": v(29.6, -7.32) * mm, "end": v(29.57, -7.27) * mm});
            skLineSegment(sketch, "E1058", {"start": v(29.57, -7.27) * mm, "end": v(29.56, -7.21) * mm});
            skLineSegment(sketch, "E1059", {"start": v(29.56, -7.21) * mm, "end": v(29.55, -7.15) * mm});
            skLineSegment(sketch, "E1060", {"start": v(29.55, -7.15) * mm, "end": v(29.56, -7.1) * mm});
            skLineSegment(sketch, "E1061", {"start": v(29.56, -7.1) * mm, "end": v(29.58, -7.04) * mm});
            skLineSegment(sketch, "E1062", {"start": v(29.58, -7.04) * mm, "end": v(29.6, -7) * mm});
            skLineSegment(sketch, "E1063", {"start": v(29.6, -7) * mm, "end": v(29.65, -6.95) * mm});
            skLineSegment(sketch, "E1064", {"start": v(29.65, -6.95) * mm, "end": v(29.7, -6.92) * mm});
            skLineSegment(sketch, "E1065", {"start": v(29.7, -6.92) * mm, "end": v(29.74, -6.9) * mm});
            skLineSegment(sketch, "E1066", {"start": v(29.74, -6.9) * mm, "end": v(29.78, -6.9) * mm});
            skLineSegment(sketch, "E1067", {"start": v(29.78, -6.9) * mm, "end": v(29.83, -6.89) * mm});
            skLineSegment(sketch, "E1068", {"start": v(29.83, -6.89) * mm, "end": v(29.87, -6.9) * mm});
            skLineSegment(sketch, "E1069", {"start": v(29.87, -6.9) * mm, "end": v(29.91, -6.88) * mm});
            skLineSegment(sketch, "E1070", {"start": v(29.91, -6.88) * mm, "end": v(29.94, -6.84) * mm});
            skLineSegment(sketch, "E1071", {"start": v(29.94, -6.84) * mm, "end": v(29.97, -6.72) * mm});
            skLineSegment(sketch, "E1072", {"start": v(29.97, -6.72) * mm, "end": v(29.96, -6.67) * mm});
            skLineSegment(sketch, "E1073", {"start": v(29.96, -6.67) * mm, "end": v(29.93, -6.64) * mm});
            skLineSegment(sketch, "E1074", {"start": v(29.93, -6.64) * mm, "end": v(29.89, -6.62) * mm});
            skLineSegment(sketch, "E1075", {"start": v(29.89, -6.62) * mm, "end": v(29.85, -6.6) * mm});
            skLineSegment(sketch, "E1076", {"start": v(29.85, -6.6) * mm, "end": v(29.81, -6.57) * mm});
            skLineSegment(sketch, "E1077", {"start": v(29.81, -6.57) * mm, "end": v(29.78, -6.54) * mm});
            skLineSegment(sketch, "E1078", {"start": v(29.78, -6.54) * mm, "end": v(29.75, -6.5) * mm});
            skLineSegment(sketch, "E1079", {"start": v(29.75, -6.5) * mm, "end": v(29.73, -6.44) * mm});
            skLineSegment(sketch, "E1080", {"start": v(29.73, -6.44) * mm, "end": v(29.73, -6.38) * mm});
            skLineSegment(sketch, "E1081", {"start": v(29.73, -6.38) * mm, "end": v(29.74, -6.32) * mm});
            skLineSegment(sketch, "E1082", {"start": v(29.74, -6.32) * mm, "end": v(29.75, -6.26) * mm});
            skLineSegment(sketch, "E1083", {"start": v(29.75, -6.26) * mm, "end": v(29.78, -6.21) * mm});
            skLineSegment(sketch, "E1084", {"start": v(29.78, -6.21) * mm, "end": v(29.82, -6.17) * mm});
            skLineSegment(sketch, "E1085", {"start": v(29.82, -6.17) * mm, "end": v(29.87, -6.14) * mm});
            skLineSegment(sketch, "E1086", {"start": v(29.87, -6.14) * mm, "end": v(29.91, -6.12) * mm});
            skLineSegment(sketch, "E1087", {"start": v(29.91, -6.12) * mm, "end": v(29.95, -6.11) * mm});
            skLineSegment(sketch, "E1088", {"start": v(29.95, -6.11) * mm, "end": v(30, -6.1) * mm});
            skLineSegment(sketch, "E1089", {"start": v(30, -6.1) * mm, "end": v(30.04, -6.1) * mm});
            skLineSegment(sketch, "E1090", {"start": v(30.04, -6.1) * mm, "end": v(30.08, -6.1) * mm});
            skLineSegment(sketch, "E1091", {"start": v(30.08, -6.1) * mm, "end": v(30.1, -6.05) * mm});
            skLineSegment(sketch, "E1092", {"start": v(30.1, -6.05) * mm, "end": v(30.13, -5.93) * mm});
            skLineSegment(sketch, "E1093", {"start": v(30.13, -5.93) * mm, "end": v(30.13, -5.88) * mm});
            skLineSegment(sketch, "E1094", {"start": v(30.13, -5.88) * mm, "end": v(30.1, -5.86) * mm});
            skLineSegment(sketch, "E1095", {"start": v(30.1, -5.86) * mm, "end": v(30.05, -5.84) * mm});
            skLineSegment(sketch, "E1096", {"start": v(30.05, -5.84) * mm, "end": v(30.01, -5.82) * mm});
            skLineSegment(sketch, "E1097", {"start": v(30.01, -5.82) * mm, "end": v(29.98, -5.8) * mm});
            skLineSegment(sketch, "E1098", {"start": v(29.98, -5.8) * mm, "end": v(29.94, -5.76) * mm});
            skLineSegment(sketch, "E1099", {"start": v(29.94, -5.76) * mm, "end": v(29.91, -5.71) * mm});
            skLineSegment(sketch, "E1100", {"start": v(29.91, -5.71) * mm, "end": v(29.9, -5.66) * mm});
            skLineSegment(sketch, "E1101", {"start": v(29.9, -5.66) * mm, "end": v(29.89, -5.6) * mm});
            skLineSegment(sketch, "E1102", {"start": v(29.89, -5.6) * mm, "end": v(29.9, -5.54) * mm});
            skLineSegment(sketch, "E1103", {"start": v(29.9, -5.54) * mm, "end": v(29.9, -5.48) * mm});
            skLineSegment(sketch, "E1104", {"start": v(29.9, -5.48) * mm, "end": v(29.93, -5.43) * mm});
            skLineSegment(sketch, "E1105", {"start": v(29.93, -5.43) * mm, "end": v(29.97, -5.39) * mm});
            skLineSegment(sketch, "E1106", {"start": v(29.97, -5.39) * mm, "end": v(30.02, -5.35) * mm});
            skLineSegment(sketch, "E1107", {"start": v(30.02, -5.35) * mm, "end": v(30.06, -5.34) * mm});
            skLineSegment(sketch, "E1108", {"start": v(30.06, -5.34) * mm, "end": v(30.1, -5.32) * mm});
            skLineSegment(sketch, "E1109", {"start": v(30.1, -5.32) * mm, "end": v(30.15, -5.32) * mm});
            skLineSegment(sketch, "E1110", {"start": v(30.15, -5.32) * mm, "end": v(30.2, -5.32) * mm});
            skLineSegment(sketch, "E1111", {"start": v(30.2, -5.32) * mm, "end": v(30.23, -5.3) * mm});
            skLineSegment(sketch, "E1112", {"start": v(30.23, -5.3) * mm, "end": v(30.26, -5.26) * mm});
            skLineSegment(sketch, "E1113", {"start": v(30.26, -5.26) * mm, "end": v(30.28, -5.14) * mm});
            skLineSegment(sketch, "E1114", {"start": v(30.28, -5.14) * mm, "end": v(30.27, -5.1) * mm});
            skLineSegment(sketch, "E1115", {"start": v(30.27, -5.1) * mm, "end": v(30.24, -5.07) * mm});
            skLineSegment(sketch, "E1116", {"start": v(30.24, -5.07) * mm, "end": v(30.2, -5.05) * mm});
            skLineSegment(sketch, "E1117", {"start": v(30.2, -5.05) * mm, "end": v(30.15, -5.03) * mm});
            skLineSegment(sketch, "E1118", {"start": v(30.15, -5.03) * mm, "end": v(30.12, -5) * mm});
            skLineSegment(sketch, "E1119", {"start": v(30.12, -5) * mm, "end": v(30.08, -4.97) * mm});
            skLineSegment(sketch, "E1120", {"start": v(30.08, -4.97) * mm, "end": v(30.05, -4.93) * mm});
            skLineSegment(sketch, "E1121", {"start": v(30.05, -4.93) * mm, "end": v(30.03, -4.87) * mm});
            skLineSegment(sketch, "E1122", {"start": v(30.03, -4.87) * mm, "end": v(30.02, -4.81) * mm});
            skLineSegment(sketch, "E1123", {"start": v(30.02, -4.81) * mm, "end": v(30.03, -4.76) * mm});
            skLineSegment(sketch, "E1124", {"start": v(30.03, -4.76) * mm, "end": v(30.04, -4.7) * mm});
            skLineSegment(sketch, "E1125", {"start": v(30.04, -4.7) * mm, "end": v(30.07, -4.65) * mm});
            skLineSegment(sketch, "E1126", {"start": v(30.07, -4.65) * mm, "end": v(30.1, -4.6) * mm});
            skLineSegment(sketch, "E1127", {"start": v(30.1, -4.6) * mm, "end": v(30.15, -4.57) * mm});
            skLineSegment(sketch, "E1128", {"start": v(30.15, -4.57) * mm, "end": v(30.19, -4.55) * mm});
            skLineSegment(sketch, "E1129", {"start": v(30.19, -4.55) * mm, "end": v(30.23, -4.54) * mm});
            skLineSegment(sketch, "E1130", {"start": v(30.23, -4.54) * mm, "end": v(30.28, -4.53) * mm});
            skLineSegment(sketch, "E1131", {"start": v(30.28, -4.53) * mm, "end": v(30.32, -4.53) * mm});
            skLineSegment(sketch, "E1132", {"start": v(30.32, -4.53) * mm, "end": v(30.36, -4.5) * mm});
            skLineSegment(sketch, "E1133", {"start": v(30.36, -4.5) * mm, "end": v(30.38, -4.47) * mm});
            skLineSegment(sketch, "E1134", {"start": v(30.38, -4.47) * mm, "end": v(30.4, -4.35) * mm});
            skLineSegment(sketch, "E1135", {"start": v(30.4, -4.35) * mm, "end": v(30.4, -4.3) * mm});
            skLineSegment(sketch, "E1136", {"start": v(30.4, -4.3) * mm, "end": v(30.36, -4.27) * mm});
            skLineSegment(sketch, "E1137", {"start": v(30.36, -4.27) * mm, "end": v(30.32, -4.26) * mm});
            skLineSegment(sketch, "E1138", {"start": v(30.32, -4.26) * mm, "end": v(30.28, -4.24) * mm});
            skLineSegment(sketch, "E1139", {"start": v(30.28, -4.24) * mm, "end": v(30.24, -4.21) * mm});
            skLineSegment(sketch, "E1140", {"start": v(30.24, -4.21) * mm, "end": v(30.2, -4.18) * mm});
            skLineSegment(sketch, "E1141", {"start": v(30.2, -4.18) * mm, "end": v(30.17, -4.14) * mm});
            skLineSegment(sketch, "E1142", {"start": v(30.17, -4.14) * mm, "end": v(30.15, -4.08) * mm});
            skLineSegment(sketch, "E1143", {"start": v(30.15, -4.08) * mm, "end": v(30.14, -4.03) * mm});
            skLineSegment(sketch, "E1144", {"start": v(30.14, -4.03) * mm, "end": v(30.14, -3.97) * mm});
            skLineSegment(sketch, "E1145", {"start": v(30.14, -3.97) * mm, "end": v(30.15, -3.91) * mm});
            skLineSegment(sketch, "E1146", {"start": v(30.15, -3.91) * mm, "end": v(30.18, -3.86) * mm});
            skLineSegment(sketch, "E1147", {"start": v(30.18, -3.86) * mm, "end": v(30.21, -3.81) * mm});
            skLineSegment(sketch, "E1148", {"start": v(30.21, -3.81) * mm, "end": v(30.26, -3.78) * mm});
            skLineSegment(sketch, "E1149", {"start": v(30.26, -3.78) * mm, "end": v(30.3, -3.76) * mm});
            skLineSegment(sketch, "E1150", {"start": v(30.3, -3.76) * mm, "end": v(30.34, -3.74) * mm});
            skLineSegment(sketch, "E1151", {"start": v(30.34, -3.74) * mm, "end": v(30.39, -3.73) * mm});
            skLineSegment(sketch, "E1152", {"start": v(30.39, -3.73) * mm, "end": v(30.43, -3.73) * mm});
            skLineSegment(sketch, "E1153", {"start": v(30.43, -3.73) * mm, "end": v(30.47, -3.71) * mm});
            skLineSegment(sketch, "E1154", {"start": v(30.47, -3.71) * mm, "end": v(30.5, -3.67) * mm});
            skLineSegment(sketch, "E1155", {"start": v(30.5, -3.67) * mm, "end": v(30.5, -3.55) * mm});
            skLineSegment(sketch, "E1156", {"start": v(30.5, -3.55) * mm, "end": v(30.5, -3.5) * mm});
            skLineSegment(sketch, "E1157", {"start": v(30.5, -3.5) * mm, "end": v(30.46, -3.48) * mm});
            skLineSegment(sketch, "E1158", {"start": v(30.46, -3.48) * mm, "end": v(30.42, -3.46) * mm});
            skLineSegment(sketch, "E1159", {"start": v(30.42, -3.46) * mm, "end": v(30.38, -3.44) * mm});
            skLineSegment(sketch, "E1160", {"start": v(30.38, -3.44) * mm, "end": v(30.34, -3.42) * mm});
            skLineSegment(sketch, "E1161", {"start": v(30.34, -3.42) * mm, "end": v(30.3, -3.4) * mm});
            skLineSegment(sketch, "E1162", {"start": v(30.3, -3.4) * mm, "end": v(30.27, -3.35) * mm});
            skLineSegment(sketch, "E1163", {"start": v(30.27, -3.35) * mm, "end": v(30.24, -3.3) * mm});
            skLineSegment(sketch, "E1164", {"start": v(30.24, -3.3) * mm, "end": v(30.23, -3.24) * mm});
            skLineSegment(sketch, "E1165", {"start": v(30.23, -3.24) * mm, "end": v(30.23, -3.18) * mm});
            skLineSegment(sketch, "E1166", {"start": v(30.23, -3.18) * mm, "end": v(30.25, -3.12) * mm});
            skLineSegment(sketch, "E1167", {"start": v(30.25, -3.12) * mm, "end": v(30.27, -3.07) * mm});
            skLineSegment(sketch, "E1168", {"start": v(30.27, -3.07) * mm, "end": v(30.3, -3.02) * mm});
            skLineSegment(sketch, "E1169", {"start": v(30.3, -3.02) * mm, "end": v(30.35, -2.98) * mm});
            skLineSegment(sketch, "E1170", {"start": v(30.35, -2.98) * mm, "end": v(30.39, -2.96) * mm});
            skLineSegment(sketch, "E1171", {"start": v(30.39, -2.96) * mm, "end": v(30.43, -2.95) * mm});
            skLineSegment(sketch, "E1172", {"start": v(30.43, -2.95) * mm, "end": v(30.47, -2.94) * mm});
            skLineSegment(sketch, "E1173", {"start": v(30.47, -2.94) * mm, "end": v(30.52, -2.93) * mm});
            skLineSegment(sketch, "E1174", {"start": v(30.52, -2.93) * mm, "end": v(30.56, -2.91) * mm});
            skLineSegment(sketch, "E1175", {"start": v(30.56, -2.91) * mm, "end": v(30.58, -2.87) * mm});
            skLineSegment(sketch, "E1176", {"start": v(30.58, -2.87) * mm, "end": v(30.59, -2.75) * mm});
            skLineSegment(sketch, "E1177", {"start": v(30.59, -2.75) * mm, "end": v(30.58, -2.7) * mm});
            skLineSegment(sketch, "E1178", {"start": v(30.58, -2.7) * mm, "end": v(30.54, -2.68) * mm});
            skLineSegment(sketch, "E1179", {"start": v(30.54, -2.68) * mm, "end": v(30.5, -2.67) * mm});
            skLineSegment(sketch, "E1180", {"start": v(30.5, -2.67) * mm, "end": v(30.46, -2.65) * mm});
            skLineSegment(sketch, "E1181", {"start": v(30.46, -2.65) * mm, "end": v(30.42, -2.63) * mm});
            skLineSegment(sketch, "E1182", {"start": v(30.42, -2.63) * mm, "end": v(30.38, -2.6) * mm});
            skLineSegment(sketch, "E1183", {"start": v(30.38, -2.6) * mm, "end": v(30.34, -2.55) * mm});
            skLineSegment(sketch, "E1184", {"start": v(30.34, -2.55) * mm, "end": v(30.32, -2.5) * mm});
            skLineSegment(sketch, "E1185", {"start": v(30.32, -2.5) * mm, "end": v(30.3, -2.44) * mm});
            skLineSegment(sketch, "E1186", {"start": v(30.3, -2.44) * mm, "end": v(30.3, -2.39) * mm});
            skLineSegment(sketch, "E1187", {"start": v(30.3, -2.39) * mm, "end": v(30.32, -2.33) * mm});
            skLineSegment(sketch, "E1188", {"start": v(30.32, -2.33) * mm, "end": v(30.34, -2.27) * mm});
            skLineSegment(sketch, "E1189", {"start": v(30.34, -2.27) * mm, "end": v(30.37, -2.23) * mm});
            skLineSegment(sketch, "E1190", {"start": v(30.37, -2.23) * mm, "end": v(30.41, -2.19) * mm});
            skLineSegment(sketch, "E1191", {"start": v(30.41, -2.19) * mm, "end": v(30.45, -2.17) * mm});
            skLineSegment(sketch, "E1192", {"start": v(30.45, -2.17) * mm, "end": v(30.5, -2.15) * mm});
            skLineSegment(sketch, "E1193", {"start": v(30.5, -2.15) * mm, "end": v(30.54, -2.14) * mm});
            skLineSegment(sketch, "E1194", {"start": v(30.54, -2.14) * mm, "end": v(30.58, -2.13) * mm});
            skLineSegment(sketch, "E1195", {"start": v(30.58, -2.13) * mm, "end": v(30.62, -2.11) * mm});
            skLineSegment(sketch, "E1196", {"start": v(30.62, -2.11) * mm, "end": v(30.64, -2.07) * mm});
            skLineSegment(sketch, "E1197", {"start": v(30.64, -2.07) * mm, "end": v(30.65, -1.95) * mm});
            skLineSegment(sketch, "E1198", {"start": v(30.65, -1.95) * mm, "end": v(30.64, -1.9) * mm});
            skLineSegment(sketch, "E1199", {"start": v(30.64, -1.9) * mm, "end": v(30.6, -1.88) * mm});
            skLineSegment(sketch, "E1200", {"start": v(30.6, -1.88) * mm, "end": v(30.56, -1.87) * mm});
            skLineSegment(sketch, "E1201", {"start": v(30.56, -1.87) * mm, "end": v(30.52, -1.85) * mm});
            skLineSegment(sketch, "E1202", {"start": v(30.52, -1.85) * mm, "end": v(30.48, -1.83) * mm});
            skLineSegment(sketch, "E1203", {"start": v(30.48, -1.83) * mm, "end": v(30.44, -1.8) * mm});
            skLineSegment(sketch, "E1204", {"start": v(30.44, -1.8) * mm, "end": v(30.4, -1.76) * mm});
            skLineSegment(sketch, "E1205", {"start": v(30.4, -1.76) * mm, "end": v(30.38, -1.7) * mm});
            skLineSegment(sketch, "E1206", {"start": v(30.38, -1.7) * mm, "end": v(30.36, -1.65) * mm});
            skLineSegment(sketch, "E1207", {"start": v(30.36, -1.65) * mm, "end": v(30.36, -1.6) * mm});
            skLineSegment(sketch, "E1208", {"start": v(30.36, -1.6) * mm, "end": v(30.37, -1.53) * mm});
            skLineSegment(sketch, "E1209", {"start": v(30.37, -1.53) * mm, "end": v(30.39, -1.48) * mm});
            skLineSegment(sketch, "E1210", {"start": v(30.39, -1.48) * mm, "end": v(30.42, -1.43) * mm});
            skLineSegment(sketch, "E1211", {"start": v(30.42, -1.43) * mm, "end": v(30.46, -1.39) * mm});
            skLineSegment(sketch, "E1212", {"start": v(30.46, -1.39) * mm, "end": v(30.5, -1.37) * mm});
            skLineSegment(sketch, "E1213", {"start": v(30.5, -1.37) * mm, "end": v(30.54, -1.35) * mm});
            skLineSegment(sketch, "E1214", {"start": v(30.54, -1.35) * mm, "end": v(30.58, -1.34) * mm});
            skLineSegment(sketch, "E1215", {"start": v(30.58, -1.34) * mm, "end": v(30.63, -1.33) * mm});
            skLineSegment(sketch, "E1216", {"start": v(30.63, -1.33) * mm, "end": v(30.67, -1.31) * mm});
            skLineSegment(sketch, "E1217", {"start": v(30.67, -1.31) * mm, "end": v(30.68, -1.27) * mm});
            skLineSegment(sketch, "E1218", {"start": v(30.68, -1.27) * mm, "end": v(30.69, -1.15) * mm});
            skLineSegment(sketch, "E1219", {"start": v(30.69, -1.15) * mm, "end": v(30.68, -1.1) * mm});
            skLineSegment(sketch, "E1220", {"start": v(30.68, -1.1) * mm, "end": v(30.64, -1.08) * mm});
            skLineSegment(sketch, "E1221", {"start": v(30.64, -1.08) * mm, "end": v(30.6, -1.07) * mm});
            skLineSegment(sketch, "E1222", {"start": v(30.6, -1.07) * mm, "end": v(30.55, -1.05) * mm});
            skLineSegment(sketch, "E1223", {"start": v(30.55, -1.05) * mm, "end": v(30.51, -1.03) * mm});
            skLineSegment(sketch, "E1224", {"start": v(30.51, -1.03) * mm, "end": v(30.48, -1) * mm});
            skLineSegment(sketch, "E1225", {"start": v(30.48, -1) * mm, "end": v(30.44, -0.96) * mm});
            skLineSegment(sketch, "E1226", {"start": v(30.44, -0.96) * mm, "end": v(30.4, -0.9) * mm});
            skLineSegment(sketch, "E1227", {"start": v(30.4, -0.9) * mm, "end": v(30.4, -0.85) * mm});
            skLineSegment(sketch, "E1228", {"start": v(30.4, -0.85) * mm, "end": v(30.39, -0.8) * mm});
            skLineSegment(sketch, "E1229", {"start": v(30.39, -0.8) * mm, "end": v(30.4, -0.74) * mm});
            skLineSegment(sketch, "E1230", {"start": v(30.4, -0.74) * mm, "end": v(30.42, -0.68) * mm});
            skLineSegment(sketch, "E1231", {"start": v(30.42, -0.68) * mm, "end": v(30.45, -0.63) * mm});
            skLineSegment(sketch, "E1232", {"start": v(30.45, -0.63) * mm, "end": v(30.49, -0.6) * mm});
            skLineSegment(sketch, "E1233", {"start": v(30.49, -0.6) * mm, "end": v(30.53, -0.57) * mm});
            skLineSegment(sketch, "E1234", {"start": v(30.53, -0.57) * mm, "end": v(30.57, -0.55) * mm});
            skLineSegment(sketch, "E1235", {"start": v(30.57, -0.55) * mm, "end": v(30.6, -0.54) * mm});
            skLineSegment(sketch, "E1236", {"start": v(30.6, -0.54) * mm, "end": v(30.65, -0.53) * mm});
            skLineSegment(sketch, "E1237", {"start": v(30.65, -0.53) * mm, "end": v(30.7, -0.5) * mm});
            skLineSegment(sketch, "E1238", {"start": v(30.7, -0.5) * mm, "end": v(30.7, -0.46) * mm});
            skLineSegment(sketch, "E1239", {"start": v(30.7, -0.46) * mm, "end": v(30.7, -0.34) * mm});
            skLineSegment(sketch, "E1240", {"start": v(30.7, -0.34) * mm, "end": v(30.7, -0.3) * mm});
            skLineSegment(sketch, "E1241", {"start": v(30.7, -0.3) * mm, "end": v(30.66, -0.27) * mm});
            skLineSegment(sketch, "E1242", {"start": v(30.66, -0.27) * mm, "end": v(30.61, -0.26) * mm});
            skLineSegment(sketch, "E1243", {"start": v(30.61, -0.26) * mm, "end": v(30.57, -0.25) * mm});
            skLineSegment(sketch, "E1244", {"start": v(30.57, -0.25) * mm, "end": v(30.53, -0.23) * mm});
            skLineSegment(sketch, "E1245", {"start": v(30.53, -0.23) * mm, "end": v(30.5, -0.2) * mm});
            skLineSegment(sketch, "E1246", {"start": v(30.5, -0.2) * mm, "end": v(30.45, -0.16) * mm});
            skLineSegment(sketch, "E1247", {"start": v(30.45, -0.16) * mm, "end": v(30.42, -0.11) * mm});
            skLineSegment(sketch, "E1248", {"start": v(30.42, -0.11) * mm, "end": v(30.4, -0.06) * mm});
            skLineSegment(sketch, "E1249", {"start": v(30.4, -0.06) * mm, "end": v(30.4, 0) * mm});
            skLineSegment(sketch, "E1250", {"start": v(30.4, 0) * mm, "end": v(30.4, 0.06) * mm});
            skLineSegment(sketch, "E1251", {"start": v(30.4, 0.06) * mm, "end": v(30.42, 0.11) * mm});
            skLineSegment(sketch, "E1252", {"start": v(30.42, 0.11) * mm, "end": v(30.45, 0.16) * mm});
            skLineSegment(sketch, "E1253", {"start": v(30.45, 0.16) * mm, "end": v(30.5, 0.2) * mm});
            skLineSegment(sketch, "E1254", {"start": v(30.5, 0.2) * mm, "end": v(30.53, 0.23) * mm});
            skLineSegment(sketch, "E1255", {"start": v(30.53, 0.23) * mm, "end": v(30.57, 0.25) * mm});
            skLineSegment(sketch, "E1256", {"start": v(30.57, 0.25) * mm, "end": v(30.61, 0.26) * mm});
            skLineSegment(sketch, "E1257", {"start": v(30.61, 0.26) * mm, "end": v(30.66, 0.27) * mm});
            skLineSegment(sketch, "E1258", {"start": v(30.66, 0.27) * mm, "end": v(30.7, 0.3) * mm});
            skLineSegment(sketch, "E1259", {"start": v(30.7, 0.3) * mm, "end": v(30.7, 0.34) * mm});
            skLineSegment(sketch, "E1260", {"start": v(30.7, 0.34) * mm, "end": v(30.7, 0.46) * mm});
            skLineSegment(sketch, "E1261", {"start": v(30.7, 0.46) * mm, "end": v(30.7, 0.5) * mm});
            skLineSegment(sketch, "E1262", {"start": v(30.7, 0.5) * mm, "end": v(30.65, 0.53) * mm});
            skLineSegment(sketch, "E1263", {"start": v(30.65, 0.53) * mm, "end": v(30.6, 0.54) * mm});
            skLineSegment(sketch, "E1264", {"start": v(30.6, 0.54) * mm, "end": v(30.57, 0.55) * mm});
            skLineSegment(sketch, "E1265", {"start": v(30.57, 0.55) * mm, "end": v(30.53, 0.57) * mm});
            skLineSegment(sketch, "E1266", {"start": v(30.53, 0.57) * mm, "end": v(30.49, 0.6) * mm});
            skLineSegment(sketch, "E1267", {"start": v(30.49, 0.6) * mm, "end": v(30.45, 0.63) * mm});
            skLineSegment(sketch, "E1268", {"start": v(30.45, 0.63) * mm, "end": v(30.42, 0.68) * mm});
            skLineSegment(sketch, "E1269", {"start": v(30.42, 0.68) * mm, "end": v(30.4, 0.74) * mm});
            skLineSegment(sketch, "E1270", {"start": v(30.4, 0.74) * mm, "end": v(30.39, 0.8) * mm});
            skLineSegment(sketch, "E1271", {"start": v(30.39, 0.8) * mm, "end": v(30.4, 0.85) * mm});
            skLineSegment(sketch, "E1272", {"start": v(30.4, 0.85) * mm, "end": v(30.4, 0.9) * mm});
            skLineSegment(sketch, "E1273", {"start": v(30.4, 0.9) * mm, "end": v(30.44, 0.96) * mm});
            skLineSegment(sketch, "E1274", {"start": v(30.44, 0.96) * mm, "end": v(30.48, 1) * mm});
            skLineSegment(sketch, "E1275", {"start": v(30.48, 1) * mm, "end": v(30.51, 1.03) * mm});
            skLineSegment(sketch, "E1276", {"start": v(30.51, 1.03) * mm, "end": v(30.55, 1.05) * mm});
            skLineSegment(sketch, "E1277", {"start": v(30.55, 1.05) * mm, "end": v(30.6, 1.07) * mm});
            skLineSegment(sketch, "E1278", {"start": v(30.6, 1.07) * mm, "end": v(30.64, 1.08) * mm});
            skLineSegment(sketch, "E1279", {"start": v(30.64, 1.08) * mm, "end": v(30.68, 1.1) * mm});
            skLineSegment(sketch, "E1280", {"start": v(30.68, 1.1) * mm, "end": v(30.69, 1.15) * mm});
            skLineSegment(sketch, "E1281", {"start": v(30.69, 1.15) * mm, "end": v(30.68, 1.27) * mm});
            skLineSegment(sketch, "E1282", {"start": v(30.68, 1.27) * mm, "end": v(30.67, 1.31) * mm});
            skLineSegment(sketch, "E1283", {"start": v(30.67, 1.31) * mm, "end": v(30.63, 1.33) * mm});
            skLineSegment(sketch, "E1284", {"start": v(30.63, 1.33) * mm, "end": v(30.58, 1.34) * mm});
            skLineSegment(sketch, "E1285", {"start": v(30.58, 1.34) * mm, "end": v(30.54, 1.35) * mm});
            skLineSegment(sketch, "E1286", {"start": v(30.54, 1.35) * mm, "end": v(30.5, 1.37) * mm});
            skLineSegment(sketch, "E1287", {"start": v(30.5, 1.37) * mm, "end": v(30.46, 1.39) * mm});
            skLineSegment(sketch, "E1288", {"start": v(30.46, 1.39) * mm, "end": v(30.42, 1.43) * mm});
            skLineSegment(sketch, "E1289", {"start": v(30.42, 1.43) * mm, "end": v(30.39, 1.48) * mm});
            skLineSegment(sketch, "E1290", {"start": v(30.39, 1.48) * mm, "end": v(30.37, 1.53) * mm});
            skLineSegment(sketch, "E1291", {"start": v(30.37, 1.53) * mm, "end": v(30.36, 1.6) * mm});
            skLineSegment(sketch, "E1292", {"start": v(30.36, 1.6) * mm, "end": v(30.36, 1.65) * mm});
            skLineSegment(sketch, "E1293", {"start": v(30.36, 1.65) * mm, "end": v(30.38, 1.7) * mm});
            skLineSegment(sketch, "E1294", {"start": v(30.38, 1.7) * mm, "end": v(30.4, 1.76) * mm});
            skLineSegment(sketch, "E1295", {"start": v(30.4, 1.76) * mm, "end": v(30.44, 1.8) * mm});
            skLineSegment(sketch, "E1296", {"start": v(30.44, 1.8) * mm, "end": v(30.48, 1.83) * mm});
            skLineSegment(sketch, "E1297", {"start": v(30.48, 1.83) * mm, "end": v(30.52, 1.85) * mm});
            skLineSegment(sketch, "E1298", {"start": v(30.52, 1.85) * mm, "end": v(30.56, 1.87) * mm});
            skLineSegment(sketch, "E1299", {"start": v(30.56, 1.87) * mm, "end": v(30.6, 1.88) * mm});
            skLineSegment(sketch, "E1300", {"start": v(30.6, 1.88) * mm, "end": v(30.64, 1.9) * mm});
            skLineSegment(sketch, "E1301", {"start": v(30.64, 1.9) * mm, "end": v(30.65, 1.95) * mm});
            skLineSegment(sketch, "E1302", {"start": v(30.65, 1.95) * mm, "end": v(30.64, 2.07) * mm});
            skLineSegment(sketch, "E1303", {"start": v(30.64, 2.07) * mm, "end": v(30.62, 2.11) * mm});
            skLineSegment(sketch, "E1304", {"start": v(30.62, 2.11) * mm, "end": v(30.58, 2.13) * mm});
            skLineSegment(sketch, "E1305", {"start": v(30.58, 2.13) * mm, "end": v(30.54, 2.14) * mm});
            skLineSegment(sketch, "E1306", {"start": v(30.54, 2.14) * mm, "end": v(30.5, 2.15) * mm});
            skLineSegment(sketch, "E1307", {"start": v(30.5, 2.15) * mm, "end": v(30.45, 2.17) * mm});
            skLineSegment(sketch, "E1308", {"start": v(30.45, 2.17) * mm, "end": v(30.41, 2.19) * mm});
            skLineSegment(sketch, "E1309", {"start": v(30.41, 2.19) * mm, "end": v(30.37, 2.23) * mm});
            skLineSegment(sketch, "E1310", {"start": v(30.37, 2.23) * mm, "end": v(30.34, 2.27) * mm});
            skLineSegment(sketch, "E1311", {"start": v(30.34, 2.27) * mm, "end": v(30.32, 2.33) * mm});
            skLineSegment(sketch, "E1312", {"start": v(30.32, 2.33) * mm, "end": v(30.3, 2.39) * mm});
            skLineSegment(sketch, "E1313", {"start": v(30.3, 2.39) * mm, "end": v(30.3, 2.44) * mm});
            skLineSegment(sketch, "E1314", {"start": v(30.3, 2.44) * mm, "end": v(30.32, 2.5) * mm});
            skLineSegment(sketch, "E1315", {"start": v(30.32, 2.5) * mm, "end": v(30.34, 2.55) * mm});
            skLineSegment(sketch, "E1316", {"start": v(30.34, 2.55) * mm, "end": v(30.38, 2.6) * mm});
            skLineSegment(sketch, "E1317", {"start": v(30.38, 2.6) * mm, "end": v(30.42, 2.63) * mm});
            skLineSegment(sketch, "E1318", {"start": v(30.42, 2.63) * mm, "end": v(30.46, 2.65) * mm});
            skLineSegment(sketch, "E1319", {"start": v(30.46, 2.65) * mm, "end": v(30.5, 2.67) * mm});
            skLineSegment(sketch, "E1320", {"start": v(30.5, 2.67) * mm, "end": v(30.54, 2.68) * mm});
            skLineSegment(sketch, "E1321", {"start": v(30.54, 2.68) * mm, "end": v(30.58, 2.7) * mm});
            skLineSegment(sketch, "E1322", {"start": v(30.58, 2.7) * mm, "end": v(30.59, 2.75) * mm});
            skLineSegment(sketch, "E1323", {"start": v(30.59, 2.75) * mm, "end": v(30.58, 2.87) * mm});
            skLineSegment(sketch, "E1324", {"start": v(30.58, 2.87) * mm, "end": v(30.56, 2.91) * mm});
            skLineSegment(sketch, "E1325", {"start": v(30.56, 2.91) * mm, "end": v(30.52, 2.93) * mm});
            skLineSegment(sketch, "E1326", {"start": v(30.52, 2.93) * mm, "end": v(30.47, 2.94) * mm});
            skLineSegment(sketch, "E1327", {"start": v(30.47, 2.94) * mm, "end": v(30.43, 2.95) * mm});
            skLineSegment(sketch, "E1328", {"start": v(30.43, 2.95) * mm, "end": v(30.39, 2.96) * mm});
            skLineSegment(sketch, "E1329", {"start": v(30.39, 2.96) * mm, "end": v(30.35, 2.98) * mm});
            skLineSegment(sketch, "E1330", {"start": v(30.35, 2.98) * mm, "end": v(30.3, 3.02) * mm});
            skLineSegment(sketch, "E1331", {"start": v(30.3, 3.02) * mm, "end": v(30.27, 3.07) * mm});
            skLineSegment(sketch, "E1332", {"start": v(30.27, 3.07) * mm, "end": v(30.25, 3.12) * mm});
            skLineSegment(sketch, "E1333", {"start": v(30.25, 3.12) * mm, "end": v(30.23, 3.18) * mm});
            skLineSegment(sketch, "E1334", {"start": v(30.23, 3.18) * mm, "end": v(30.23, 3.24) * mm});
            skLineSegment(sketch, "E1335", {"start": v(30.23, 3.24) * mm, "end": v(30.24, 3.3) * mm});
            skLineSegment(sketch, "E1336", {"start": v(30.24, 3.3) * mm, "end": v(30.27, 3.35) * mm});
            skLineSegment(sketch, "E1337", {"start": v(30.27, 3.35) * mm, "end": v(30.3, 3.4) * mm});
            skLineSegment(sketch, "E1338", {"start": v(30.3, 3.4) * mm, "end": v(30.34, 3.42) * mm});
            skLineSegment(sketch, "E1339", {"start": v(30.34, 3.42) * mm, "end": v(30.38, 3.44) * mm});
            skLineSegment(sketch, "E1340", {"start": v(30.38, 3.44) * mm, "end": v(30.42, 3.46) * mm});
            skLineSegment(sketch, "E1341", {"start": v(30.42, 3.46) * mm, "end": v(30.46, 3.48) * mm});
            skLineSegment(sketch, "E1342", {"start": v(30.46, 3.48) * mm, "end": v(30.5, 3.5) * mm});
            skLineSegment(sketch, "E1343", {"start": v(30.5, 3.5) * mm, "end": v(30.5, 3.55) * mm});
            skLineSegment(sketch, "E1344", {"start": v(30.5, 3.55) * mm, "end": v(30.5, 3.67) * mm});
            skLineSegment(sketch, "E1345", {"start": v(30.5, 3.67) * mm, "end": v(30.47, 3.71) * mm});
            skLineSegment(sketch, "E1346", {"start": v(30.47, 3.71) * mm, "end": v(30.43, 3.73) * mm});
            skLineSegment(sketch, "E1347", {"start": v(30.43, 3.73) * mm, "end": v(30.39, 3.73) * mm});
            skLineSegment(sketch, "E1348", {"start": v(30.39, 3.73) * mm, "end": v(30.34, 3.74) * mm});
            skLineSegment(sketch, "E1349", {"start": v(30.34, 3.74) * mm, "end": v(30.3, 3.76) * mm});
            skLineSegment(sketch, "E1350", {"start": v(30.3, 3.76) * mm, "end": v(30.26, 3.78) * mm});
            skLineSegment(sketch, "E1351", {"start": v(30.26, 3.78) * mm, "end": v(30.21, 3.81) * mm});
            skLineSegment(sketch, "E1352", {"start": v(30.21, 3.81) * mm, "end": v(30.18, 3.86) * mm});
            skLineSegment(sketch, "E1353", {"start": v(30.18, 3.86) * mm, "end": v(30.15, 3.91) * mm});
            skLineSegment(sketch, "E1354", {"start": v(30.15, 3.91) * mm, "end": v(30.14, 3.97) * mm});
            skLineSegment(sketch, "E1355", {"start": v(30.14, 3.97) * mm, "end": v(30.14, 4.03) * mm});
            skLineSegment(sketch, "E1356", {"start": v(30.14, 4.03) * mm, "end": v(30.15, 4.08) * mm});
            skLineSegment(sketch, "E1357", {"start": v(30.15, 4.08) * mm, "end": v(30.17, 4.14) * mm});
            skLineSegment(sketch, "E1358", {"start": v(30.17, 4.14) * mm, "end": v(30.2, 4.18) * mm});
            skLineSegment(sketch, "E1359", {"start": v(30.2, 4.18) * mm, "end": v(30.24, 4.21) * mm});
            skLineSegment(sketch, "E1360", {"start": v(30.24, 4.21) * mm, "end": v(30.28, 4.24) * mm});
            skLineSegment(sketch, "E1361", {"start": v(30.28, 4.24) * mm, "end": v(30.32, 4.26) * mm});
            skLineSegment(sketch, "E1362", {"start": v(30.32, 4.26) * mm, "end": v(30.36, 4.27) * mm});
            skLineSegment(sketch, "E1363", {"start": v(30.36, 4.27) * mm, "end": v(30.4, 4.3) * mm});
            skLineSegment(sketch, "E1364", {"start": v(30.4, 4.3) * mm, "end": v(30.4, 4.35) * mm});
            skLineSegment(sketch, "E1365", {"start": v(30.4, 4.35) * mm, "end": v(30.38, 4.47) * mm});
            skLineSegment(sketch, "E1366", {"start": v(30.38, 4.47) * mm, "end": v(30.36, 4.5) * mm});
            skLineSegment(sketch, "E1367", {"start": v(30.36, 4.5) * mm, "end": v(30.32, 4.53) * mm});
            skLineSegment(sketch, "E1368", {"start": v(30.32, 4.53) * mm, "end": v(30.28, 4.53) * mm});
            skLineSegment(sketch, "E1369", {"start": v(30.28, 4.53) * mm, "end": v(30.23, 4.54) * mm});
            skLineSegment(sketch, "E1370", {"start": v(30.23, 4.54) * mm, "end": v(30.19, 4.55) * mm});
            skLineSegment(sketch, "E1371", {"start": v(30.19, 4.55) * mm, "end": v(30.15, 4.57) * mm});
            skLineSegment(sketch, "E1372", {"start": v(30.15, 4.57) * mm, "end": v(30.1, 4.6) * mm});
            skLineSegment(sketch, "E1373", {"start": v(30.1, 4.6) * mm, "end": v(30.07, 4.65) * mm});
            skLineSegment(sketch, "E1374", {"start": v(30.07, 4.65) * mm, "end": v(30.04, 4.7) * mm});
            skLineSegment(sketch, "E1375", {"start": v(30.04, 4.7) * mm, "end": v(30.03, 4.76) * mm});
            skLineSegment(sketch, "E1376", {"start": v(30.03, 4.76) * mm, "end": v(30.02, 4.81) * mm});
            skLineSegment(sketch, "E1377", {"start": v(30.02, 4.81) * mm, "end": v(30.03, 4.87) * mm});
            skLineSegment(sketch, "E1378", {"start": v(30.03, 4.87) * mm, "end": v(30.05, 4.93) * mm});
            skLineSegment(sketch, "E1379", {"start": v(30.05, 4.93) * mm, "end": v(30.08, 4.97) * mm});
            skLineSegment(sketch, "E1380", {"start": v(30.08, 4.97) * mm, "end": v(30.12, 5) * mm});
            skLineSegment(sketch, "E1381", {"start": v(30.12, 5) * mm, "end": v(30.15, 5.03) * mm});
            skLineSegment(sketch, "E1382", {"start": v(30.15, 5.03) * mm, "end": v(30.2, 5.05) * mm});
            skLineSegment(sketch, "E1383", {"start": v(30.2, 5.05) * mm, "end": v(30.24, 5.07) * mm});
            skLineSegment(sketch, "E1384", {"start": v(30.24, 5.07) * mm, "end": v(30.27, 5.1) * mm});
            skLineSegment(sketch, "E1385", {"start": v(30.27, 5.1) * mm, "end": v(30.28, 5.14) * mm});
            skLineSegment(sketch, "E1386", {"start": v(30.28, 5.14) * mm, "end": v(30.26, 5.26) * mm});
            skLineSegment(sketch, "E1387", {"start": v(30.26, 5.26) * mm, "end": v(30.23, 5.3) * mm});
            skLineSegment(sketch, "E1388", {"start": v(30.23, 5.3) * mm, "end": v(30.2, 5.32) * mm});
            skLineSegment(sketch, "E1389", {"start": v(30.2, 5.32) * mm, "end": v(30.15, 5.32) * mm});
            skLineSegment(sketch, "E1390", {"start": v(30.15, 5.32) * mm, "end": v(30.1, 5.32) * mm});
            skLineSegment(sketch, "E1391", {"start": v(30.1, 5.32) * mm, "end": v(30.06, 5.34) * mm});
            skLineSegment(sketch, "E1392", {"start": v(30.06, 5.34) * mm, "end": v(30.02, 5.35) * mm});
            skLineSegment(sketch, "E1393", {"start": v(30.02, 5.35) * mm, "end": v(29.97, 5.39) * mm});
            skLineSegment(sketch, "E1394", {"start": v(29.97, 5.39) * mm, "end": v(29.93, 5.43) * mm});
            skLineSegment(sketch, "E1395", {"start": v(29.93, 5.43) * mm, "end": v(29.9, 5.48) * mm});
            skLineSegment(sketch, "E1396", {"start": v(29.9, 5.48) * mm, "end": v(29.9, 5.54) * mm});
            skLineSegment(sketch, "E1397", {"start": v(29.9, 5.54) * mm, "end": v(29.89, 5.6) * mm});
            skLineSegment(sketch, "E1398", {"start": v(29.89, 5.6) * mm, "end": v(29.9, 5.66) * mm});
            skLineSegment(sketch, "E1399", {"start": v(29.9, 5.66) * mm, "end": v(29.91, 5.71) * mm});
            skLineSegment(sketch, "E1400", {"start": v(29.91, 5.71) * mm, "end": v(29.94, 5.76) * mm});
            skLineSegment(sketch, "E1401", {"start": v(29.94, 5.76) * mm, "end": v(29.98, 5.8) * mm});
            skLineSegment(sketch, "E1402", {"start": v(29.98, 5.8) * mm, "end": v(30.01, 5.82) * mm});
            skLineSegment(sketch, "E1403", {"start": v(30.01, 5.82) * mm, "end": v(30.05, 5.84) * mm});
            skLineSegment(sketch, "E1404", {"start": v(30.05, 5.84) * mm, "end": v(30.1, 5.86) * mm});
            skLineSegment(sketch, "E1405", {"start": v(30.1, 5.86) * mm, "end": v(30.13, 5.88) * mm});
            skLineSegment(sketch, "E1406", {"start": v(30.13, 5.88) * mm, "end": v(30.13, 5.93) * mm});
            skLineSegment(sketch, "E1407", {"start": v(30.13, 5.93) * mm, "end": v(30.1, 6.05) * mm});
            skLineSegment(sketch, "E1408", {"start": v(30.1, 6.05) * mm, "end": v(30.08, 6.1) * mm});
            skLineSegment(sketch, "E1409", {"start": v(30.08, 6.1) * mm, "end": v(30.04, 6.1) * mm});
            skLineSegment(sketch, "E1410", {"start": v(30.04, 6.1) * mm, "end": v(30, 6.1) * mm});
            skLineSegment(sketch, "E1411", {"start": v(30, 6.1) * mm, "end": v(29.95, 6.11) * mm});
            skLineSegment(sketch, "E1412", {"start": v(29.95, 6.11) * mm, "end": v(29.91, 6.12) * mm});
            skLineSegment(sketch, "E1413", {"start": v(29.91, 6.12) * mm, "end": v(29.87, 6.14) * mm});
            skLineSegment(sketch, "E1414", {"start": v(29.87, 6.14) * mm, "end": v(29.82, 6.17) * mm});
            skLineSegment(sketch, "E1415", {"start": v(29.82, 6.17) * mm, "end": v(29.78, 6.21) * mm});
            skLineSegment(sketch, "E1416", {"start": v(29.78, 6.21) * mm, "end": v(29.75, 6.26) * mm});
            skLineSegment(sketch, "E1417", {"start": v(29.75, 6.26) * mm, "end": v(29.74, 6.32) * mm});
            skLineSegment(sketch, "E1418", {"start": v(29.74, 6.32) * mm, "end": v(29.73, 6.38) * mm});
            skLineSegment(sketch, "E1419", {"start": v(29.73, 6.38) * mm, "end": v(29.73, 6.44) * mm});
            skLineSegment(sketch, "E1420", {"start": v(29.73, 6.44) * mm, "end": v(29.75, 6.5) * mm});
            skLineSegment(sketch, "E1421", {"start": v(29.75, 6.5) * mm, "end": v(29.78, 6.54) * mm});
            skLineSegment(sketch, "E1422", {"start": v(29.78, 6.54) * mm, "end": v(29.81, 6.57) * mm});
            skLineSegment(sketch, "E1423", {"start": v(29.81, 6.57) * mm, "end": v(29.85, 6.6) * mm});
            skLineSegment(sketch, "E1424", {"start": v(29.85, 6.6) * mm, "end": v(29.89, 6.62) * mm});
            skLineSegment(sketch, "E1425", {"start": v(29.89, 6.62) * mm, "end": v(29.93, 6.64) * mm});
            skLineSegment(sketch, "E1426", {"start": v(29.93, 6.64) * mm, "end": v(29.96, 6.67) * mm});
            skLineSegment(sketch, "E1427", {"start": v(29.96, 6.67) * mm, "end": v(29.97, 6.72) * mm});
            skLineSegment(sketch, "E1428", {"start": v(29.97, 6.72) * mm, "end": v(29.94, 6.84) * mm});
            skLineSegment(sketch, "E1429", {"start": v(29.94, 6.84) * mm, "end": v(29.91, 6.88) * mm});
            skLineSegment(sketch, "E1430", {"start": v(29.91, 6.88) * mm, "end": v(29.87, 6.9) * mm});
            skLineSegment(sketch, "E1431", {"start": v(29.87, 6.9) * mm, "end": v(29.83, 6.89) * mm});
            skLineSegment(sketch, "E1432", {"start": v(29.83, 6.89) * mm, "end": v(29.78, 6.9) * mm});
            skLineSegment(sketch, "E1433", {"start": v(29.78, 6.9) * mm, "end": v(29.74, 6.9) * mm});
            skLineSegment(sketch, "E1434", {"start": v(29.74, 6.9) * mm, "end": v(29.7, 6.92) * mm});
            skLineSegment(sketch, "E1435", {"start": v(29.7, 6.92) * mm, "end": v(29.65, 6.95) * mm});
            skLineSegment(sketch, "E1436", {"start": v(29.65, 6.95) * mm, "end": v(29.6, 7) * mm});
            skLineSegment(sketch, "E1437", {"start": v(29.6, 7) * mm, "end": v(29.58, 7.04) * mm});
            skLineSegment(sketch, "E1438", {"start": v(29.58, 7.04) * mm, "end": v(29.56, 7.1) * mm});
            skLineSegment(sketch, "E1439", {"start": v(29.56, 7.1) * mm, "end": v(29.55, 7.15) * mm});
            skLineSegment(sketch, "E1440", {"start": v(29.55, 7.15) * mm, "end": v(29.56, 7.21) * mm});
            skLineSegment(sketch, "E1441", {"start": v(29.56, 7.21) * mm, "end": v(29.57, 7.27) * mm});
            skLineSegment(sketch, "E1442", {"start": v(29.57, 7.27) * mm, "end": v(29.6, 7.32) * mm});
            skLineSegment(sketch, "E1443", {"start": v(29.6, 7.32) * mm, "end": v(29.63, 7.35) * mm});
            skLineSegment(sketch, "E1444", {"start": v(29.63, 7.35) * mm, "end": v(29.67, 7.38) * mm});
            skLineSegment(sketch, "E1445", {"start": v(29.67, 7.38) * mm, "end": v(29.7, 7.4) * mm});
            skLineSegment(sketch, "E1446", {"start": v(29.7, 7.4) * mm, "end": v(29.75, 7.42) * mm});
            skLineSegment(sketch, "E1447", {"start": v(29.75, 7.42) * mm, "end": v(29.78, 7.45) * mm});
            skLineSegment(sketch, "E1448", {"start": v(29.78, 7.45) * mm, "end": v(29.78, 7.5) * mm});
            skLineSegment(sketch, "E1449", {"start": v(29.78, 7.5) * mm, "end": v(29.75, 7.62) * mm});
            skLineSegment(sketch, "E1450", {"start": v(29.75, 7.62) * mm, "end": v(29.72, 7.66) * mm});
            skLineSegment(sketch, "E1451", {"start": v(29.72, 7.66) * mm, "end": v(29.68, 7.67) * mm});
            skLineSegment(sketch, "E1452", {"start": v(29.68, 7.67) * mm, "end": v(29.64, 7.67) * mm});
            skLineSegment(sketch, "E1453", {"start": v(29.64, 7.67) * mm, "end": v(29.6, 7.67) * mm});
            skLineSegment(sketch, "E1454", {"start": v(29.6, 7.67) * mm, "end": v(29.55, 7.68) * mm});
            skLineSegment(sketch, "E1455", {"start": v(29.55, 7.68) * mm, "end": v(29.5, 7.7) * mm});
            skLineSegment(sketch, "E1456", {"start": v(29.5, 7.7) * mm, "end": v(29.46, 7.72) * mm});
            skLineSegment(sketch, "E1457", {"start": v(29.46, 7.72) * mm, "end": v(29.42, 7.76) * mm});
            skLineSegment(sketch, "E1458", {"start": v(29.42, 7.76) * mm, "end": v(29.39, 7.81) * mm});
            skLineSegment(sketch, "E1459", {"start": v(29.39, 7.81) * mm, "end": v(29.36, 7.87) * mm});
            skLineSegment(sketch, "E1460", {"start": v(29.36, 7.87) * mm, "end": v(29.35, 7.93) * mm});
            skLineSegment(sketch, "E1461", {"start": v(29.35, 7.93) * mm, "end": v(29.36, 7.98) * mm});
            skLineSegment(sketch, "E1462", {"start": v(29.36, 7.98) * mm, "end": v(29.37, 8.04) * mm});
            skLineSegment(sketch, "E1463", {"start": v(29.37, 8.04) * mm, "end": v(29.4, 8.1) * mm});
            skLineSegment(sketch, "E1464", {"start": v(29.4, 8.1) * mm, "end": v(29.43, 8.12) * mm});
            skLineSegment(sketch, "E1465", {"start": v(29.43, 8.12) * mm, "end": v(29.46, 8.15) * mm});
            skLineSegment(sketch, "E1466", {"start": v(29.46, 8.15) * mm, "end": v(29.5, 8.18) * mm});
            skLineSegment(sketch, "E1467", {"start": v(29.5, 8.18) * mm, "end": v(29.54, 8.2) * mm});
            skLineSegment(sketch, "E1468", {"start": v(29.54, 8.2) * mm, "end": v(29.57, 8.23) * mm});
            skLineSegment(sketch, "E1469", {"start": v(29.57, 8.23) * mm, "end": v(29.57, 8.28) * mm});
            skLineSegment(sketch, "E1470", {"start": v(29.57, 8.28) * mm, "end": v(29.54, 8.4) * mm});
            skLineSegment(sketch, "E1471", {"start": v(29.54, 8.4) * mm, "end": v(29.51, 8.43) * mm});
            skLineSegment(sketch, "E1472", {"start": v(29.51, 8.43) * mm, "end": v(29.47, 8.44) * mm});
            skLineSegment(sketch, "E1473", {"start": v(29.47, 8.44) * mm, "end": v(29.43, 8.44) * mm});
            skLineSegment(sketch, "E1474", {"start": v(29.43, 8.44) * mm, "end": v(29.38, 8.44) * mm});
            skLineSegment(sketch, "E1475", {"start": v(29.38, 8.44) * mm, "end": v(29.34, 8.45) * mm});
            skLineSegment(sketch, "E1476", {"start": v(29.34, 8.45) * mm, "end": v(29.3, 8.46) * mm});
            skLineSegment(sketch, "E1477", {"start": v(29.3, 8.46) * mm, "end": v(29.24, 8.5) * mm});
            skLineSegment(sketch, "E1478", {"start": v(29.24, 8.5) * mm, "end": v(29.2, 8.53) * mm});
            skLineSegment(sketch, "E1479", {"start": v(29.2, 8.53) * mm, "end": v(29.17, 8.58) * mm});
            skLineSegment(sketch, "E1480", {"start": v(29.17, 8.58) * mm, "end": v(29.15, 8.63) * mm});
            skLineSegment(sketch, "E1481", {"start": v(29.15, 8.63) * mm, "end": v(29.14, 8.7) * mm});
            skLineSegment(sketch, "E1482", {"start": v(29.14, 8.7) * mm, "end": v(29.14, 8.75) * mm});
            skLineSegment(sketch, "E1483", {"start": v(29.14, 8.75) * mm, "end": v(29.15, 8.8) * mm});
            skLineSegment(sketch, "E1484", {"start": v(29.15, 8.8) * mm, "end": v(29.18, 8.86) * mm});
            skLineSegment(sketch, "E1485", {"start": v(29.18, 8.86) * mm, "end": v(29.2, 8.9) * mm});
            skLineSegment(sketch, "E1486", {"start": v(29.2, 8.9) * mm, "end": v(29.24, 8.92) * mm});
            skLineSegment(sketch, "E1487", {"start": v(29.24, 8.92) * mm, "end": v(29.28, 8.95) * mm});
            skLineSegment(sketch, "E1488", {"start": v(29.28, 8.95) * mm, "end": v(29.32, 8.97) * mm});
            skLineSegment(sketch, "E1489", {"start": v(29.32, 8.97) * mm, "end": v(29.35, 9) * mm});
            skLineSegment(sketch, "E1490", {"start": v(29.35, 9) * mm, "end": v(29.35, 9.05) * mm});
            skLineSegment(sketch, "E1491", {"start": v(29.35, 9.05) * mm, "end": v(29.31, 9.16) * mm});
            skLineSegment(sketch, "E1492", {"start": v(29.31, 9.16) * mm, "end": v(29.28, 9.2) * mm});
            skLineSegment(sketch, "E1493", {"start": v(29.28, 9.2) * mm, "end": v(29.24, 9.21) * mm});
            skLineSegment(sketch, "E1494", {"start": v(29.24, 9.21) * mm, "end": v(29.2, 9.2) * mm});
            skLineSegment(sketch, "E1495", {"start": v(29.2, 9.2) * mm, "end": v(29.15, 9.2) * mm});
            skLineSegment(sketch, "E1496", {"start": v(29.15, 9.2) * mm, "end": v(29.1, 9.21) * mm});
            skLineSegment(sketch, "E1497", {"start": v(29.1, 9.21) * mm, "end": v(29.06, 9.23) * mm});
            skLineSegment(sketch, "E1498", {"start": v(29.06, 9.23) * mm, "end": v(29.01, 9.25) * mm});
            skLineSegment(sketch, "E1499", {"start": v(29.01, 9.25) * mm, "end": v(28.97, 9.3) * mm});
            skLineSegment(sketch, "E1500", {"start": v(28.97, 9.3) * mm, "end": v(28.94, 9.34) * mm});
            skLineSegment(sketch, "E1501", {"start": v(28.94, 9.34) * mm, "end": v(28.91, 9.4) * mm});
            skLineSegment(sketch, "E1502", {"start": v(28.91, 9.4) * mm, "end": v(28.9, 9.45) * mm});
            skLineSegment(sketch, "E1503", {"start": v(28.9, 9.45) * mm, "end": v(28.9, 9.5) * mm});
            skLineSegment(sketch, "E1504", {"start": v(28.9, 9.5) * mm, "end": v(28.91, 9.57) * mm});
            skLineSegment(sketch, "E1505", {"start": v(28.91, 9.57) * mm, "end": v(28.93, 9.62) * mm});
            skLineSegment(sketch, "E1506", {"start": v(28.93, 9.62) * mm, "end": v(28.96, 9.65) * mm});
            skLineSegment(sketch, "E1507", {"start": v(28.96, 9.65) * mm, "end": v(29, 9.68) * mm});
            skLineSegment(sketch, "E1508", {"start": v(29, 9.68) * mm, "end": v(29.03, 9.71) * mm});
            skLineSegment(sketch, "E1509", {"start": v(29.03, 9.71) * mm, "end": v(29.07, 9.73) * mm});
            skLineSegment(sketch, "E1510", {"start": v(29.07, 9.73) * mm, "end": v(29.1, 9.77) * mm});
            skLineSegment(sketch, "E1511", {"start": v(29.1, 9.77) * mm, "end": v(29.1, 9.81) * mm});
            skLineSegment(sketch, "E1512", {"start": v(29.1, 9.81) * mm, "end": v(29.06, 9.93) * mm});
            skLineSegment(sketch, "E1513", {"start": v(29.06, 9.93) * mm, "end": v(29.03, 9.97) * mm});
            skLineSegment(sketch, "E1514", {"start": v(29.03, 9.97) * mm, "end": v(28.99, 9.98) * mm});
            skLineSegment(sketch, "E1515", {"start": v(28.99, 9.98) * mm, "end": v(28.94, 9.97) * mm});
            skLineSegment(sketch, "E1516", {"start": v(28.94, 9.97) * mm, "end": v(28.9, 9.97) * mm});
            skLineSegment(sketch, "E1517", {"start": v(28.9, 9.97) * mm, "end": v(28.86, 9.97) * mm});
            skLineSegment(sketch, "E1518", {"start": v(28.86, 9.97) * mm, "end": v(28.81, 9.98) * mm});
            skLineSegment(sketch, "E1519", {"start": v(28.81, 9.98) * mm, "end": v(28.76, 10.01) * mm});
            skLineSegment(sketch, "E1520", {"start": v(28.76, 10.01) * mm, "end": v(28.72, 10.05) * mm});
            skLineSegment(sketch, "E1521", {"start": v(28.72, 10.05) * mm, "end": v(28.68, 10.1) * mm});
            skLineSegment(sketch, "E1522", {"start": v(28.68, 10.1) * mm, "end": v(28.66, 10.15) * mm});
            skLineSegment(sketch, "E1523", {"start": v(28.66, 10.15) * mm, "end": v(28.64, 10.2) * mm});
            skLineSegment(sketch, "E1524", {"start": v(28.64, 10.2) * mm, "end": v(28.64, 10.26) * mm});
            skLineSegment(sketch, "E1525", {"start": v(28.64, 10.26) * mm, "end": v(28.65, 10.32) * mm});
            skLineSegment(sketch, "E1526", {"start": v(28.65, 10.32) * mm, "end": v(28.67, 10.37) * mm});
            skLineSegment(sketch, "E1527", {"start": v(28.67, 10.37) * mm, "end": v(28.7, 10.4) * mm});
            skLineSegment(sketch, "E1528", {"start": v(28.7, 10.4) * mm, "end": v(28.73, 10.44) * mm});
            skLineSegment(sketch, "E1529", {"start": v(28.73, 10.44) * mm, "end": v(28.77, 10.47) * mm});
            skLineSegment(sketch, "E1530", {"start": v(28.77, 10.47) * mm, "end": v(28.8, 10.5) * mm});
            skLineSegment(sketch, "E1531", {"start": v(28.8, 10.5) * mm, "end": v(28.83, 10.53) * mm});
            skLineSegment(sketch, "E1532", {"start": v(28.83, 10.53) * mm, "end": v(28.83, 10.57) * mm});
            skLineSegment(sketch, "E1533", {"start": v(28.83, 10.57) * mm, "end": v(28.8, 10.69) * mm});
            skLineSegment(sketch, "E1534", {"start": v(28.8, 10.69) * mm, "end": v(28.76, 10.72) * mm});
            skLineSegment(sketch, "E1535", {"start": v(28.76, 10.72) * mm, "end": v(28.72, 10.73) * mm});
            skLineSegment(sketch, "E1536", {"start": v(28.72, 10.73) * mm, "end": v(28.67, 10.72) * mm});
            skLineSegment(sketch, "E1537", {"start": v(28.67, 10.72) * mm, "end": v(28.63, 10.72) * mm});
            skLineSegment(sketch, "E1538", {"start": v(28.63, 10.72) * mm, "end": v(28.58, 10.73) * mm});
            skLineSegment(sketch, "E1539", {"start": v(28.58, 10.73) * mm, "end": v(28.54, 10.73) * mm});
            skLineSegment(sketch, "E1540", {"start": v(28.54, 10.73) * mm, "end": v(28.49, 10.76) * mm});
            skLineSegment(sketch, "E1541", {"start": v(28.49, 10.76) * mm, "end": v(28.44, 10.8) * mm});
            skLineSegment(sketch, "E1542", {"start": v(28.44, 10.8) * mm, "end": v(28.4, 10.84) * mm});
            skLineSegment(sketch, "E1543", {"start": v(28.4, 10.84) * mm, "end": v(28.38, 10.9) * mm});
            skLineSegment(sketch, "E1544", {"start": v(28.38, 10.9) * mm, "end": v(28.37, 10.95) * mm});
            skLineSegment(sketch, "E1545", {"start": v(28.37, 10.95) * mm, "end": v(28.36, 11) * mm});
            skLineSegment(sketch, "E1546", {"start": v(28.36, 11) * mm, "end": v(28.37, 11.07) * mm});
            skLineSegment(sketch, "E1547", {"start": v(28.37, 11.07) * mm, "end": v(28.4, 11.12) * mm});
            skLineSegment(sketch, "E1548", {"start": v(28.4, 11.12) * mm, "end": v(28.42, 11.16) * mm});
            skLineSegment(sketch, "E1549", {"start": v(28.42, 11.16) * mm, "end": v(28.45, 11.19) * mm});
            skLineSegment(sketch, "E1550", {"start": v(28.45, 11.19) * mm, "end": v(28.48, 11.22) * mm});
            skLineSegment(sketch, "E1551", {"start": v(28.48, 11.22) * mm, "end": v(28.52, 11.24) * mm});
            skLineSegment(sketch, "E1552", {"start": v(28.52, 11.24) * mm, "end": v(28.55, 11.28) * mm});
            skLineSegment(sketch, "E1553", {"start": v(28.55, 11.28) * mm, "end": v(28.55, 11.32) * mm});
            skLineSegment(sketch, "E1554", {"start": v(28.55, 11.32) * mm, "end": v(28.5, 11.44) * mm});
            skLineSegment(sketch, "E1555", {"start": v(28.5, 11.44) * mm, "end": v(28.47, 11.47) * mm});
            skLineSegment(sketch, "E1556", {"start": v(28.47, 11.47) * mm, "end": v(28.43, 11.48) * mm});
            skLineSegment(sketch, "E1557", {"start": v(28.43, 11.48) * mm, "end": v(28.38, 11.47) * mm});
            skLineSegment(sketch, "E1558", {"start": v(28.38, 11.47) * mm, "end": v(28.34, 11.47) * mm});
            skLineSegment(sketch, "E1559", {"start": v(28.34, 11.47) * mm, "end": v(28.3, 11.47) * mm});
            skLineSegment(sketch, "E1560", {"start": v(28.3, 11.47) * mm, "end": v(28.25, 11.48) * mm});
            skLineSegment(sketch, "E1561", {"start": v(28.25, 11.48) * mm, "end": v(28.2, 11.5) * mm});
            skLineSegment(sketch, "E1562", {"start": v(28.2, 11.5) * mm, "end": v(28.15, 11.54) * mm});
            skLineSegment(sketch, "E1563", {"start": v(28.15, 11.54) * mm, "end": v(28.11, 11.58) * mm});
            skLineSegment(sketch, "E1564", {"start": v(28.11, 11.58) * mm, "end": v(28.09, 11.63) * mm});
            skLineSegment(sketch, "E1565", {"start": v(28.09, 11.63) * mm, "end": v(28.07, 11.69) * mm});
            skLineSegment(sketch, "E1566", {"start": v(28.07, 11.69) * mm, "end": v(28.06, 11.75) * mm});
            skLineSegment(sketch, "E1567", {"start": v(28.06, 11.75) * mm, "end": v(28.07, 11.8) * mm});
            skLineSegment(sketch, "E1568", {"start": v(28.07, 11.8) * mm, "end": v(28.1, 11.86) * mm});
            skLineSegment(sketch, "E1569", {"start": v(28.1, 11.86) * mm, "end": v(28.12, 11.9) * mm});
            skLineSegment(sketch, "E1570", {"start": v(28.12, 11.9) * mm, "end": v(28.15, 11.93) * mm});
            skLineSegment(sketch, "E1571", {"start": v(28.15, 11.93) * mm, "end": v(28.18, 11.96) * mm});
            skLineSegment(sketch, "E1572", {"start": v(28.18, 11.96) * mm, "end": v(28.22, 11.98) * mm});
            skLineSegment(sketch, "E1573", {"start": v(28.22, 11.98) * mm, "end": v(28.24, 12.02) * mm});
            skLineSegment(sketch, "E1574", {"start": v(28.24, 12.02) * mm, "end": v(28.24, 12.07) * mm});
            skLineSegment(sketch, "E1575", {"start": v(28.24, 12.07) * mm, "end": v(28.2, 12.18) * mm});
            skLineSegment(sketch, "E1576", {"start": v(28.2, 12.18) * mm, "end": v(28.16, 12.21) * mm});
            skLineSegment(sketch, "E1577", {"start": v(28.16, 12.21) * mm, "end": v(28.12, 12.22) * mm});
            skLineSegment(sketch, "E1578", {"start": v(28.12, 12.22) * mm, "end": v(28.07, 12.2) * mm});
            skLineSegment(sketch, "E1579", {"start": v(28.07, 12.2) * mm, "end": v(28.03, 12.2) * mm});
            skLineSegment(sketch, "E1580", {"start": v(28.03, 12.2) * mm, "end": v(27.98, 12.2) * mm});
            skLineSegment(sketch, "E1581", {"start": v(27.98, 12.2) * mm, "end": v(27.94, 12.21) * mm});
            skLineSegment(sketch, "E1582", {"start": v(27.94, 12.21) * mm, "end": v(27.89, 12.24) * mm});
            skLineSegment(sketch, "E1583", {"start": v(27.89, 12.24) * mm, "end": v(27.84, 12.27) * mm});
            skLineSegment(sketch, "E1584", {"start": v(27.84, 12.27) * mm, "end": v(27.8, 12.31) * mm});
            skLineSegment(sketch, "E1585", {"start": v(27.8, 12.31) * mm, "end": v(27.77, 12.36) * mm});
            skLineSegment(sketch, "E1586", {"start": v(27.77, 12.36) * mm, "end": v(27.75, 12.42) * mm});
            skLineSegment(sketch, "E1587", {"start": v(27.75, 12.42) * mm, "end": v(27.75, 12.48) * mm});
            skLineSegment(sketch, "E1588", {"start": v(27.75, 12.48) * mm, "end": v(27.75, 12.54) * mm});
            skLineSegment(sketch, "E1589", {"start": v(27.75, 12.54) * mm, "end": v(27.77, 12.6) * mm});
            skLineSegment(sketch, "E1590", {"start": v(27.77, 12.6) * mm, "end": v(27.8, 12.63) * mm});
            skLineSegment(sketch, "E1591", {"start": v(27.8, 12.63) * mm, "end": v(27.83, 12.66) * mm});
            skLineSegment(sketch, "E1592", {"start": v(27.83, 12.66) * mm, "end": v(27.86, 12.7) * mm});
            skLineSegment(sketch, "E1593", {"start": v(27.86, 12.7) * mm, "end": v(27.9, 12.72) * mm});
            skLineSegment(sketch, "E1594", {"start": v(27.9, 12.72) * mm, "end": v(27.92, 12.75) * mm});
            skLineSegment(sketch, "E1595", {"start": v(27.92, 12.75) * mm, "end": v(27.91, 12.8) * mm});
            skLineSegment(sketch, "E1596", {"start": v(27.91, 12.8) * mm, "end": v(27.86, 12.91) * mm});
            skLineSegment(sketch, "E1597", {"start": v(27.86, 12.91) * mm, "end": v(27.83, 12.95) * mm});
            skLineSegment(sketch, "E1598", {"start": v(27.83, 12.95) * mm, "end": v(27.79, 12.95) * mm});
            skLineSegment(sketch, "E1599", {"start": v(27.79, 12.95) * mm, "end": v(27.74, 12.94) * mm});
            skLineSegment(sketch, "E1600", {"start": v(27.74, 12.94) * mm, "end": v(27.7, 12.93) * mm});
            skLineSegment(sketch, "E1601", {"start": v(27.7, 12.93) * mm, "end": v(27.65, 12.93) * mm});
            skLineSegment(sketch, "E1602", {"start": v(27.65, 12.93) * mm, "end": v(27.6, 12.94) * mm});
            skLineSegment(sketch, "E1603", {"start": v(27.6, 12.94) * mm, "end": v(27.56, 12.96) * mm});
            skLineSegment(sketch, "E1604", {"start": v(27.56, 12.96) * mm, "end": v(27.5, 13) * mm});
            skLineSegment(sketch, "E1605", {"start": v(27.5, 13) * mm, "end": v(27.47, 13.04) * mm});
            skLineSegment(sketch, "E1606", {"start": v(27.47, 13.04) * mm, "end": v(27.44, 13.09) * mm});
            skLineSegment(sketch, "E1607", {"start": v(27.44, 13.09) * mm, "end": v(27.42, 13.14) * mm});
            skLineSegment(sketch, "E1608", {"start": v(27.42, 13.14) * mm, "end": v(27.41, 13.2) * mm});
            skLineSegment(sketch, "E1609", {"start": v(27.41, 13.2) * mm, "end": v(27.41, 13.26) * mm});
            skLineSegment(sketch, "E1610", {"start": v(27.41, 13.26) * mm, "end": v(27.43, 13.31) * mm});
            skLineSegment(sketch, "E1611", {"start": v(27.43, 13.31) * mm, "end": v(27.46, 13.35) * mm});
            skLineSegment(sketch, "E1612", {"start": v(27.46, 13.35) * mm, "end": v(27.48, 13.39) * mm});
            skLineSegment(sketch, "E1613", {"start": v(27.48, 13.39) * mm, "end": v(27.52, 13.42) * mm});
            skLineSegment(sketch, "E1614", {"start": v(27.52, 13.42) * mm, "end": v(27.55, 13.44) * mm});
            skLineSegment(sketch, "E1615", {"start": v(27.55, 13.44) * mm, "end": v(27.58, 13.48) * mm});
            skLineSegment(sketch, "E1616", {"start": v(27.58, 13.48) * mm, "end": v(27.57, 13.53) * mm});
            skLineSegment(sketch, "E1617", {"start": v(27.57, 13.53) * mm, "end": v(27.52, 13.64) * mm});
            skLineSegment(sketch, "E1618", {"start": v(27.52, 13.64) * mm, "end": v(27.48, 13.67) * mm});
            skLineSegment(sketch, "E1619", {"start": v(27.48, 13.67) * mm, "end": v(27.44, 13.67) * mm});
            skLineSegment(sketch, "E1620", {"start": v(27.44, 13.67) * mm, "end": v(27.4, 13.66) * mm});
            skLineSegment(sketch, "E1621", {"start": v(27.4, 13.66) * mm, "end": v(27.35, 13.66) * mm});
            skLineSegment(sketch, "E1622", {"start": v(27.35, 13.66) * mm, "end": v(27.3, 13.65) * mm});
            skLineSegment(sketch, "E1623", {"start": v(27.3, 13.65) * mm, "end": v(27.26, 13.66) * mm});
            skLineSegment(sketch, "E1624", {"start": v(27.26, 13.66) * mm, "end": v(27.2, 13.68) * mm});
            skLineSegment(sketch, "E1625", {"start": v(27.2, 13.68) * mm, "end": v(27.16, 13.71) * mm});
            skLineSegment(sketch, "E1626", {"start": v(27.16, 13.71) * mm, "end": v(27.12, 13.75) * mm});
            skLineSegment(sketch, "E1627", {"start": v(27.12, 13.75) * mm, "end": v(27.09, 13.8) * mm});
            skLineSegment(sketch, "E1628", {"start": v(27.09, 13.8) * mm, "end": v(27.07, 13.86) * mm});
            skLineSegment(sketch, "E1629", {"start": v(27.07, 13.86) * mm, "end": v(27.06, 13.91) * mm});
            skLineSegment(sketch, "E1630", {"start": v(27.06, 13.91) * mm, "end": v(27.06, 13.97) * mm});
            skLineSegment(sketch, "E1631", {"start": v(27.06, 13.97) * mm, "end": v(27.07, 14.03) * mm});
            skLineSegment(sketch, "E1632", {"start": v(27.07, 14.03) * mm, "end": v(27.1, 14.07) * mm});
            skLineSegment(sketch, "E1633", {"start": v(27.1, 14.07) * mm, "end": v(27.12, 14.1) * mm});
            skLineSegment(sketch, "E1634", {"start": v(27.12, 14.1) * mm, "end": v(27.16, 14.13) * mm});
            skLineSegment(sketch, "E1635", {"start": v(27.16, 14.13) * mm, "end": v(27.2, 14.16) * mm});
            skLineSegment(sketch, "E1636", {"start": v(27.2, 14.16) * mm, "end": v(27.21, 14.2) * mm});
            skLineSegment(sketch, "E1637", {"start": v(27.21, 14.2) * mm, "end": v(27.2, 14.25) * mm});
            skLineSegment(sketch, "E1638", {"start": v(27.2, 14.25) * mm, "end": v(27.15, 14.35) * mm});
            skLineSegment(sketch, "E1639", {"start": v(27.15, 14.35) * mm, "end": v(27.12, 14.39) * mm});
            skLineSegment(sketch, "E1640", {"start": v(27.12, 14.39) * mm, "end": v(27.07, 14.39) * mm});
            skLineSegment(sketch, "E1641", {"start": v(27.07, 14.39) * mm, "end": v(27.03, 14.37) * mm});
            skLineSegment(sketch, "E1642", {"start": v(27.03, 14.37) * mm, "end": v(26.99, 14.37) * mm});
            skLineSegment(sketch, "E1643", {"start": v(26.99, 14.37) * mm, "end": v(26.94, 14.36) * mm});
            skLineSegment(sketch, "E1644", {"start": v(26.94, 14.36) * mm, "end": v(26.9, 14.37) * mm});
            skLineSegment(sketch, "E1645", {"start": v(26.9, 14.37) * mm, "end": v(26.84, 14.39) * mm});
            skLineSegment(sketch, "E1646", {"start": v(26.84, 14.39) * mm, "end": v(26.8, 14.42) * mm});
            skLineSegment(sketch, "E1647", {"start": v(26.8, 14.42) * mm, "end": v(26.75, 14.46) * mm});
            skLineSegment(sketch, "E1648", {"start": v(26.75, 14.46) * mm, "end": v(26.72, 14.5) * mm});
            skLineSegment(sketch, "E1649", {"start": v(26.72, 14.5) * mm, "end": v(26.7, 14.56) * mm});
            skLineSegment(sketch, "E1650", {"start": v(26.7, 14.56) * mm, "end": v(26.68, 14.62) * mm});
            skLineSegment(sketch, "E1651", {"start": v(26.68, 14.62) * mm, "end": v(26.68, 14.67) * mm});
            skLineSegment(sketch, "E1652", {"start": v(26.68, 14.67) * mm, "end": v(26.7, 14.73) * mm});
            skLineSegment(sketch, "E1653", {"start": v(26.7, 14.73) * mm, "end": v(26.72, 14.77) * mm});
            skLineSegment(sketch, "E1654", {"start": v(26.72, 14.77) * mm, "end": v(26.75, 14.8) * mm});
            skLineSegment(sketch, "E1655", {"start": v(26.75, 14.8) * mm, "end": v(26.78, 14.84) * mm});
            skLineSegment(sketch, "E1656", {"start": v(26.78, 14.84) * mm, "end": v(26.81, 14.87) * mm});
            skLineSegment(sketch, "E1657", {"start": v(26.81, 14.87) * mm, "end": v(26.83, 14.9) * mm});
            skLineSegment(sketch, "E1658", {"start": v(26.83, 14.9) * mm, "end": v(26.82, 14.95) * mm});
            skLineSegment(sketch, "E1659", {"start": v(26.82, 14.95) * mm, "end": v(26.76, 15.06) * mm});
            skLineSegment(sketch, "E1660", {"start": v(26.76, 15.06) * mm, "end": v(26.73, 15.1) * mm});
            skLineSegment(sketch, "E1661", {"start": v(26.73, 15.1) * mm, "end": v(26.69, 15.1) * mm});
            skLineSegment(sketch, "E1662", {"start": v(26.69, 15.1) * mm, "end": v(26.64, 15.08) * mm});
            skLineSegment(sketch, "E1663", {"start": v(26.64, 15.08) * mm, "end": v(26.6, 15.07) * mm});
            skLineSegment(sketch, "E1664", {"start": v(26.6, 15.07) * mm, "end": v(26.55, 15.06) * mm});
            skLineSegment(sketch, "E1665", {"start": v(26.55, 15.06) * mm, "end": v(26.5, 15.07) * mm});
            skLineSegment(sketch, "E1666", {"start": v(26.5, 15.07) * mm, "end": v(26.45, 15.08) * mm});
            skLineSegment(sketch, "E1667", {"start": v(26.45, 15.08) * mm, "end": v(26.4, 15.11) * mm});
            skLineSegment(sketch, "E1668", {"start": v(26.4, 15.11) * mm, "end": v(26.36, 15.15) * mm});
            skLineSegment(sketch, "E1669", {"start": v(26.36, 15.15) * mm, "end": v(26.33, 15.2) * mm});
            skLineSegment(sketch, "E1670", {"start": v(26.33, 15.2) * mm, "end": v(26.3, 15.25) * mm});
            skLineSegment(sketch, "E1671", {"start": v(26.3, 15.25) * mm, "end": v(26.3, 15.31) * mm});
            skLineSegment(sketch, "E1672", {"start": v(26.3, 15.31) * mm, "end": v(26.3, 15.37) * mm});
            skLineSegment(sketch, "E1673", {"start": v(26.3, 15.37) * mm, "end": v(26.3, 15.42) * mm});
            skLineSegment(sketch, "E1674", {"start": v(26.3, 15.42) * mm, "end": v(26.32, 15.46) * mm});
            skLineSegment(sketch, "E1675", {"start": v(26.32, 15.46) * mm, "end": v(26.35, 15.5) * mm});
            skLineSegment(sketch, "E1676", {"start": v(26.35, 15.5) * mm, "end": v(26.38, 15.54) * mm});
            skLineSegment(sketch, "E1677", {"start": v(26.38, 15.54) * mm, "end": v(26.41, 15.56) * mm});
            skLineSegment(sketch, "E1678", {"start": v(26.41, 15.56) * mm, "end": v(26.43, 15.6) * mm});
            skLineSegment(sketch, "E1679", {"start": v(26.43, 15.6) * mm, "end": v(26.42, 15.65) * mm});
            skLineSegment(sketch, "E1680", {"start": v(26.42, 15.65) * mm, "end": v(26.36, 15.75) * mm});
            skLineSegment(sketch, "E1681", {"start": v(26.36, 15.75) * mm, "end": v(26.33, 15.78) * mm});
            skLineSegment(sketch, "E1682", {"start": v(26.33, 15.78) * mm, "end": v(26.28, 15.78) * mm});
            skLineSegment(sketch, "E1683", {"start": v(26.28, 15.78) * mm, "end": v(26.24, 15.77) * mm});
            skLineSegment(sketch, "E1684", {"start": v(26.24, 15.77) * mm, "end": v(26.2, 15.76) * mm});
            skLineSegment(sketch, "E1685", {"start": v(26.2, 15.76) * mm, "end": v(26.15, 15.75) * mm});
            skLineSegment(sketch, "E1686", {"start": v(26.15, 15.75) * mm, "end": v(26.1, 15.76) * mm});
            skLineSegment(sketch, "E1687", {"start": v(26.1, 15.76) * mm, "end": v(26.05, 15.77) * mm});
            skLineSegment(sketch, "E1688", {"start": v(26.05, 15.77) * mm, "end": v(26, 15.8) * mm});
            skLineSegment(sketch, "E1689", {"start": v(26, 15.8) * mm, "end": v(25.96, 15.84) * mm});
            skLineSegment(sketch, "E1690", {"start": v(25.96, 15.84) * mm, "end": v(25.92, 15.88) * mm});
            skLineSegment(sketch, "E1691", {"start": v(25.92, 15.88) * mm, "end": v(25.9, 15.94) * mm});
            skLineSegment(sketch, "E1692", {"start": v(25.9, 15.94) * mm, "end": v(25.88, 16) * mm});
            skLineSegment(sketch, "E1693", {"start": v(25.88, 16) * mm, "end": v(25.88, 16.05) * mm});
            skLineSegment(sketch, "E1694", {"start": v(25.88, 16.05) * mm, "end": v(25.89, 16.1) * mm});
            skLineSegment(sketch, "E1695", {"start": v(25.89, 16.1) * mm, "end": v(25.91, 16.15) * mm});
            skLineSegment(sketch, "E1696", {"start": v(25.91, 16.15) * mm, "end": v(25.93, 16.19) * mm});
            skLineSegment(sketch, "E1697", {"start": v(25.93, 16.19) * mm, "end": v(25.96, 16.22) * mm});
            skLineSegment(sketch, "E1698", {"start": v(25.96, 16.22) * mm, "end": v(26, 16.25) * mm});
            skLineSegment(sketch, "E1699", {"start": v(26, 16.25) * mm, "end": v(26.02, 16.3) * mm});
            skLineSegment(sketch, "E1700", {"start": v(26.02, 16.3) * mm, "end": v(26, 16.34) * mm});
            skLineSegment(sketch, "E1701", {"start": v(26, 16.34) * mm, "end": v(25.94, 16.44) * mm});
            skLineSegment(sketch, "E1702", {"start": v(25.94, 16.44) * mm, "end": v(25.9, 16.47) * mm});
            skLineSegment(sketch, "E1703", {"start": v(25.9, 16.47) * mm, "end": v(25.86, 16.47) * mm});
            skLineSegment(sketch, "E1704", {"start": v(25.86, 16.47) * mm, "end": v(25.82, 16.45) * mm});
            skLineSegment(sketch, "E1705", {"start": v(25.82, 16.45) * mm, "end": v(25.77, 16.44) * mm});
            skLineSegment(sketch, "E1706", {"start": v(25.77, 16.44) * mm, "end": v(25.73, 16.43) * mm});
            skLineSegment(sketch, "E1707", {"start": v(25.73, 16.43) * mm, "end": v(25.68, 16.43) * mm});
            skLineSegment(sketch, "E1708", {"start": v(25.68, 16.43) * mm, "end": v(25.63, 16.45) * mm});
            skLineSegment(sketch, "E1709", {"start": v(25.63, 16.45) * mm, "end": v(25.58, 16.47) * mm});
            skLineSegment(sketch, "E1710", {"start": v(25.58, 16.47) * mm, "end": v(25.53, 16.51) * mm});
            skLineSegment(sketch, "E1711", {"start": v(25.53, 16.51) * mm, "end": v(25.5, 16.56) * mm});
            skLineSegment(sketch, "E1712", {"start": v(25.5, 16.56) * mm, "end": v(25.47, 16.6) * mm});
            skLineSegment(sketch, "E1713", {"start": v(25.47, 16.6) * mm, "end": v(25.45, 16.67) * mm});
            skLineSegment(sketch, "E1714", {"start": v(25.45, 16.67) * mm, "end": v(25.45, 16.72) * mm});
            skLineSegment(sketch, "E1715", {"start": v(25.45, 16.72) * mm, "end": v(25.46, 16.78) * mm});
            skLineSegment(sketch, "E1716", {"start": v(25.46, 16.78) * mm, "end": v(25.48, 16.82) * mm});
            skLineSegment(sketch, "E1717", {"start": v(25.48, 16.82) * mm, "end": v(25.5, 16.86) * mm});
            skLineSegment(sketch, "E1718", {"start": v(25.5, 16.86) * mm, "end": v(25.53, 16.9) * mm});
            skLineSegment(sketch, "E1719", {"start": v(25.53, 16.9) * mm, "end": v(25.56, 16.93) * mm});
            skLineSegment(sketch, "E1720", {"start": v(25.56, 16.93) * mm, "end": v(25.58, 16.97) * mm});
            skLineSegment(sketch, "E1721", {"start": v(25.58, 16.97) * mm, "end": v(25.57, 17.01) * mm});
            skLineSegment(sketch, "E1722", {"start": v(25.57, 17.01) * mm, "end": v(25.5, 17.11) * mm});
            skLineSegment(sketch, "E1723", {"start": v(25.5, 17.11) * mm, "end": v(25.46, 17.14) * mm});
            skLineSegment(sketch, "E1724", {"start": v(25.46, 17.14) * mm, "end": v(25.42, 17.14) * mm});
            skLineSegment(sketch, "E1725", {"start": v(25.42, 17.14) * mm, "end": v(25.38, 17.12) * mm});
            skLineSegment(sketch, "E1726", {"start": v(25.38, 17.12) * mm, "end": v(25.34, 17.1) * mm});
            skLineSegment(sketch, "E1727", {"start": v(25.34, 17.1) * mm, "end": v(25.3, 17.1) * mm});
            skLineSegment(sketch, "E1728", {"start": v(25.3, 17.1) * mm, "end": v(25.25, 17.1) * mm});
            skLineSegment(sketch, "E1729", {"start": v(25.25, 17.1) * mm, "end": v(25.19, 17.11) * mm});
            skLineSegment(sketch, "E1730", {"start": v(25.19, 17.11) * mm, "end": v(25.14, 17.14) * mm});
            skLineSegment(sketch, "E1731", {"start": v(25.14, 17.14) * mm, "end": v(25.1, 17.17) * mm});
            skLineSegment(sketch, "E1732", {"start": v(25.1, 17.17) * mm, "end": v(25.05, 17.22) * mm});
            skLineSegment(sketch, "E1733", {"start": v(25.05, 17.22) * mm, "end": v(25.03, 17.27) * mm});
            skLineSegment(sketch, "E1734", {"start": v(25.03, 17.27) * mm, "end": v(25, 17.33) * mm});
            skLineSegment(sketch, "E1735", {"start": v(25, 17.33) * mm, "end": v(25, 17.38) * mm});
            skLineSegment(sketch, "E1736", {"start": v(25, 17.38) * mm, "end": v(25.01, 17.44) * mm});
            skLineSegment(sketch, "E1737", {"start": v(25.01, 17.44) * mm, "end": v(25.03, 17.48) * mm});
            skLineSegment(sketch, "E1738", {"start": v(25.03, 17.48) * mm, "end": v(25.05, 17.52) * mm});
            skLineSegment(sketch, "E1739", {"start": v(25.05, 17.52) * mm, "end": v(25.08, 17.56) * mm});
            skLineSegment(sketch, "E1740", {"start": v(25.08, 17.56) * mm, "end": v(25.1, 17.59) * mm});
            skLineSegment(sketch, "E1741", {"start": v(25.1, 17.59) * mm, "end": v(25.13, 17.63) * mm});
            skLineSegment(sketch, "E1742", {"start": v(25.13, 17.63) * mm, "end": v(25.11, 17.67) * mm});
            skLineSegment(sketch, "E1743", {"start": v(25.11, 17.67) * mm, "end": v(25.04, 17.77) * mm});
            skLineSegment(sketch, "E1744", {"start": v(25.04, 17.77) * mm, "end": v(25, 17.8) * mm});
            skLineSegment(sketch, "E1745", {"start": v(25, 17.8) * mm, "end": v(24.96, 17.8) * mm});
            skLineSegment(sketch, "E1746", {"start": v(24.96, 17.8) * mm, "end": v(24.92, 17.78) * mm});
            skLineSegment(sketch, "E1747", {"start": v(24.92, 17.78) * mm, "end": v(24.88, 17.77) * mm});
            skLineSegment(sketch, "E1748", {"start": v(24.88, 17.77) * mm, "end": v(24.83, 17.76) * mm});
            skLineSegment(sketch, "E1749", {"start": v(24.83, 17.76) * mm, "end": v(24.79, 17.76) * mm});
            skLineSegment(sketch, "E1750", {"start": v(24.79, 17.76) * mm, "end": v(24.73, 17.77) * mm});
            skLineSegment(sketch, "E1751", {"start": v(24.73, 17.77) * mm, "end": v(24.68, 17.8) * mm});
            skLineSegment(sketch, "E1752", {"start": v(24.68, 17.8) * mm, "end": v(24.63, 17.83) * mm});
            skLineSegment(sketch, "E1753", {"start": v(24.63, 17.83) * mm, "end": v(24.6, 17.87) * mm});
            skLineSegment(sketch, "E1754", {"start": v(24.6, 17.87) * mm, "end": v(24.56, 17.92) * mm});
            skLineSegment(sketch, "E1755", {"start": v(24.56, 17.92) * mm, "end": v(24.55, 17.97) * mm});
            skLineSegment(sketch, "E1756", {"start": v(24.55, 17.97) * mm, "end": v(24.54, 18.03) * mm});
            skLineSegment(sketch, "E1757", {"start": v(24.54, 18.03) * mm, "end": v(24.55, 18.09) * mm});
            skLineSegment(sketch, "E1758", {"start": v(24.55, 18.09) * mm, "end": v(24.56, 18.13) * mm});
            skLineSegment(sketch, "E1759", {"start": v(24.56, 18.13) * mm, "end": v(24.58, 18.17) * mm});
            skLineSegment(sketch, "E1760", {"start": v(24.58, 18.17) * mm, "end": v(24.61, 18.2) * mm});
            skLineSegment(sketch, "E1761", {"start": v(24.61, 18.2) * mm, "end": v(24.64, 18.24) * mm});
            skLineSegment(sketch, "E1762", {"start": v(24.64, 18.24) * mm, "end": v(24.66, 18.28) * mm});
            skLineSegment(sketch, "E1763", {"start": v(24.66, 18.28) * mm, "end": v(24.64, 18.33) * mm});
            skLineSegment(sketch, "E1764", {"start": v(24.64, 18.33) * mm, "end": v(24.57, 18.42) * mm});
            skLineSegment(sketch, "E1765", {"start": v(24.57, 18.42) * mm, "end": v(24.53, 18.45) * mm});
            skLineSegment(sketch, "E1766", {"start": v(24.53, 18.45) * mm, "end": v(24.49, 18.45) * mm});
            skLineSegment(sketch, "E1767", {"start": v(24.49, 18.45) * mm, "end": v(24.45, 18.43) * mm});
            skLineSegment(sketch, "E1768", {"start": v(24.45, 18.43) * mm, "end": v(24.4, 18.41) * mm});
            skLineSegment(sketch, "E1769", {"start": v(24.4, 18.41) * mm, "end": v(24.36, 18.4) * mm});
            skLineSegment(sketch, "E1770", {"start": v(24.36, 18.4) * mm, "end": v(24.32, 18.4) * mm});
            skLineSegment(sketch, "E1771", {"start": v(24.32, 18.4) * mm, "end": v(24.26, 18.4) * mm});
            skLineSegment(sketch, "E1772", {"start": v(24.26, 18.4) * mm, "end": v(24.2, 18.43) * mm});
            skLineSegment(sketch, "E1773", {"start": v(24.2, 18.43) * mm, "end": v(24.16, 18.46) * mm});
            skLineSegment(sketch, "E1774", {"start": v(24.16, 18.46) * mm, "end": v(24.12, 18.5) * mm});
            skLineSegment(sketch, "E1775", {"start": v(24.12, 18.5) * mm, "end": v(24.09, 18.56) * mm});
            skLineSegment(sketch, "E1776", {"start": v(24.09, 18.56) * mm, "end": v(24.07, 18.61) * mm});
            skLineSegment(sketch, "E1777", {"start": v(24.07, 18.61) * mm, "end": v(24.06, 18.67) * mm});
            skLineSegment(sketch, "E1778", {"start": v(24.06, 18.67) * mm, "end": v(24.06, 18.73) * mm});
            skLineSegment(sketch, "E1779", {"start": v(24.06, 18.73) * mm, "end": v(24.08, 18.77) * mm});
            skLineSegment(sketch, "E1780", {"start": v(24.08, 18.77) * mm, "end": v(24.1, 18.8) * mm});
            skLineSegment(sketch, "E1781", {"start": v(24.1, 18.8) * mm, "end": v(24.13, 18.85) * mm});
            skLineSegment(sketch, "E1782", {"start": v(24.13, 18.85) * mm, "end": v(24.15, 18.88) * mm});
            skLineSegment(sketch, "E1783", {"start": v(24.15, 18.88) * mm, "end": v(24.17, 18.92) * mm});
            skLineSegment(sketch, "E1784", {"start": v(24.17, 18.92) * mm, "end": v(24.15, 18.96) * mm});
            skLineSegment(sketch, "E1785", {"start": v(24.15, 18.96) * mm, "end": v(24.08, 19.06) * mm});
            skLineSegment(sketch, "E1786", {"start": v(24.08, 19.06) * mm, "end": v(24.04, 19.09) * mm});
            skLineSegment(sketch, "E1787", {"start": v(24.04, 19.09) * mm, "end": v(24, 19.08) * mm});
            skLineSegment(sketch, "E1788", {"start": v(24, 19.08) * mm, "end": v(23.96, 19.06) * mm});
            skLineSegment(sketch, "E1789", {"start": v(23.96, 19.06) * mm, "end": v(23.92, 19.04) * mm});
            skLineSegment(sketch, "E1790", {"start": v(23.92, 19.04) * mm, "end": v(23.87, 19.03) * mm});
            skLineSegment(sketch, "E1791", {"start": v(23.87, 19.03) * mm, "end": v(23.83, 19.03) * mm});
            skLineSegment(sketch, "E1792", {"start": v(23.83, 19.03) * mm, "end": v(23.77, 19.04) * mm});
            skLineSegment(sketch, "E1793", {"start": v(23.77, 19.04) * mm, "end": v(23.71, 19.06) * mm});
            skLineSegment(sketch, "E1794", {"start": v(23.71, 19.06) * mm, "end": v(23.67, 19.09) * mm});
            skLineSegment(sketch, "E1795", {"start": v(23.67, 19.09) * mm, "end": v(23.63, 19.13) * mm});
            skLineSegment(sketch, "E1796", {"start": v(23.63, 19.13) * mm, "end": v(23.6, 19.18) * mm});
            skLineSegment(sketch, "E1797", {"start": v(23.6, 19.18) * mm, "end": v(23.57, 19.23) * mm});
            skLineSegment(sketch, "E1798", {"start": v(23.57, 19.23) * mm, "end": v(23.56, 19.3) * mm});
            skLineSegment(sketch, "E1799", {"start": v(23.56, 19.3) * mm, "end": v(23.57, 19.35) * mm});
            skLineSegment(sketch, "E1800", {"start": v(23.57, 19.35) * mm, "end": v(23.58, 19.4) * mm});
            skLineSegment(sketch, "E1801", {"start": v(23.58, 19.4) * mm, "end": v(23.6, 19.43) * mm});
            skLineSegment(sketch, "E1802", {"start": v(23.6, 19.43) * mm, "end": v(23.62, 19.47) * mm});
            skLineSegment(sketch, "E1803", {"start": v(23.62, 19.47) * mm, "end": v(23.65, 19.5) * mm});
            skLineSegment(sketch, "E1804", {"start": v(23.65, 19.5) * mm, "end": v(23.67, 19.55) * mm});
            skLineSegment(sketch, "E1805", {"start": v(23.67, 19.55) * mm, "end": v(23.65, 19.6) * mm});
            skLineSegment(sketch, "E1806", {"start": v(23.65, 19.6) * mm, "end": v(23.57, 19.68) * mm});
            skLineSegment(sketch, "E1807", {"start": v(23.57, 19.68) * mm, "end": v(23.53, 19.7) * mm});
            skLineSegment(sketch, "E1808", {"start": v(23.53, 19.7) * mm, "end": v(23.49, 19.7) * mm});
            skLineSegment(sketch, "E1809", {"start": v(23.49, 19.7) * mm, "end": v(23.45, 19.68) * mm});
            skLineSegment(sketch, "E1810", {"start": v(23.45, 19.68) * mm, "end": v(23.4, 19.66) * mm});
            skLineSegment(sketch, "E1811", {"start": v(23.4, 19.66) * mm, "end": v(23.36, 19.65) * mm});
            skLineSegment(sketch, "E1812", {"start": v(23.36, 19.65) * mm, "end": v(23.32, 19.65) * mm});
            skLineSegment(sketch, "E1813", {"start": v(23.32, 19.65) * mm, "end": v(23.26, 19.65) * mm});
            skLineSegment(sketch, "E1814", {"start": v(23.26, 19.65) * mm, "end": v(23.2, 19.67) * mm});
            skLineSegment(sketch, "E1815", {"start": v(23.2, 19.67) * mm, "end": v(23.16, 19.7) * mm});
            skLineSegment(sketch, "E1816", {"start": v(23.16, 19.7) * mm, "end": v(23.12, 19.74) * mm});
            skLineSegment(sketch, "E1817", {"start": v(23.12, 19.74) * mm, "end": v(23.08, 19.8) * mm});
            skLineSegment(sketch, "E1818", {"start": v(23.08, 19.8) * mm, "end": v(23.06, 19.84) * mm});
            skLineSegment(sketch, "E1819", {"start": v(23.06, 19.84) * mm, "end": v(23.05, 19.9) * mm});
            skLineSegment(sketch, "E1820", {"start": v(23.05, 19.9) * mm, "end": v(23.05, 19.96) * mm});
            skLineSegment(sketch, "E1821", {"start": v(23.05, 19.96) * mm, "end": v(23.07, 20) * mm});
            skLineSegment(sketch, "E1822", {"start": v(23.07, 20) * mm, "end": v(23.08, 20.04) * mm});
            skLineSegment(sketch, "E1823", {"start": v(23.08, 20.04) * mm, "end": v(23.1, 20.08) * mm});
            skLineSegment(sketch, "E1824", {"start": v(23.1, 20.08) * mm, "end": v(23.13, 20.12) * mm});
            skLineSegment(sketch, "E1825", {"start": v(23.13, 20.12) * mm, "end": v(23.15, 20.16) * mm});
            skLineSegment(sketch, "E1826", {"start": v(23.15, 20.16) * mm, "end": v(23.13, 20.2) * mm});
            skLineSegment(sketch, "E1827", {"start": v(23.13, 20.2) * mm, "end": v(23.05, 20.3) * mm});
            skLineSegment(sketch, "E1828", {"start": v(23.05, 20.3) * mm, "end": v(23, 20.32) * mm});
            skLineSegment(sketch, "E1829", {"start": v(23, 20.32) * mm, "end": v(22.96, 20.3) * mm});
            skLineSegment(sketch, "E1830", {"start": v(22.96, 20.3) * mm, "end": v(22.93, 20.29) * mm});
            skLineSegment(sketch, "E1831", {"start": v(22.93, 20.29) * mm, "end": v(22.89, 20.27) * mm});
            skLineSegment(sketch, "E1832", {"start": v(22.89, 20.27) * mm, "end": v(22.84, 20.26) * mm});
            skLineSegment(sketch, "E1833", {"start": v(22.84, 20.26) * mm, "end": v(22.8, 20.25) * mm});
            skLineSegment(sketch, "E1834", {"start": v(22.8, 20.25) * mm, "end": v(22.74, 20.25) * mm});
            skLineSegment(sketch, "E1835", {"start": v(22.74, 20.25) * mm, "end": v(22.68, 20.27) * mm});
            skLineSegment(sketch, "E1836", {"start": v(22.68, 20.27) * mm, "end": v(22.64, 20.3) * mm});
            skLineSegment(sketch, "E1837", {"start": v(22.64, 20.3) * mm, "end": v(22.6, 20.34) * mm});
            skLineSegment(sketch, "E1838", {"start": v(22.6, 20.34) * mm, "end": v(22.56, 20.39) * mm});
            skLineSegment(sketch, "E1839", {"start": v(22.56, 20.39) * mm, "end": v(22.53, 20.44) * mm});
            skLineSegment(sketch, "E1840", {"start": v(22.53, 20.44) * mm, "end": v(22.52, 20.5) * mm});
            skLineSegment(sketch, "E1841", {"start": v(22.52, 20.5) * mm, "end": v(22.52, 20.56) * mm});
            skLineSegment(sketch, "E1842", {"start": v(22.52, 20.56) * mm, "end": v(22.53, 20.6) * mm});
            skLineSegment(sketch, "E1843", {"start": v(22.53, 20.6) * mm, "end": v(22.55, 20.64) * mm});
            skLineSegment(sketch, "E1844", {"start": v(22.55, 20.64) * mm, "end": v(22.57, 20.68) * mm});
            skLineSegment(sketch, "E1845", {"start": v(22.57, 20.68) * mm, "end": v(22.6, 20.72) * mm});
            skLineSegment(sketch, "E1846", {"start": v(22.6, 20.72) * mm, "end": v(22.61, 20.76) * mm});
            skLineSegment(sketch, "E1847", {"start": v(22.61, 20.76) * mm, "end": v(22.6, 20.8) * mm});
            skLineSegment(sketch, "E1848", {"start": v(22.6, 20.8) * mm, "end": v(22.51, 20.9) * mm});
            skLineSegment(sketch, "E1849", {"start": v(22.51, 20.9) * mm, "end": v(22.47, 20.91) * mm});
            skLineSegment(sketch, "E1850", {"start": v(22.47, 20.91) * mm, "end": v(22.43, 20.9) * mm});
            skLineSegment(sketch, "E1851", {"start": v(22.43, 20.9) * mm, "end": v(22.39, 20.88) * mm});
            skLineSegment(sketch, "E1852", {"start": v(22.39, 20.88) * mm, "end": v(22.35, 20.86) * mm});
            skLineSegment(sketch, "E1853", {"start": v(22.35, 20.86) * mm, "end": v(22.3, 20.85) * mm});
            skLineSegment(sketch, "E1854", {"start": v(22.3, 20.85) * mm, "end": v(22.26, 20.84) * mm});
            skLineSegment(sketch, "E1855", {"start": v(22.26, 20.84) * mm, "end": v(22.2, 20.84) * mm});
            skLineSegment(sketch, "E1856", {"start": v(22.2, 20.84) * mm, "end": v(22.15, 20.86) * mm});
            skLineSegment(sketch, "E1857", {"start": v(22.15, 20.86) * mm, "end": v(22.1, 20.89) * mm});
            skLineSegment(sketch, "E1858", {"start": v(22.1, 20.89) * mm, "end": v(22.05, 20.93) * mm});
            skLineSegment(sketch, "E1859", {"start": v(22.05, 20.93) * mm, "end": v(22.02, 20.97) * mm});
            skLineSegment(sketch, "E1860", {"start": v(22.02, 20.97) * mm, "end": v(22, 21.02) * mm});
            skLineSegment(sketch, "E1861", {"start": v(22, 21.02) * mm, "end": v(21.98, 21.08) * mm});
            skLineSegment(sketch, "E1862", {"start": v(21.98, 21.08) * mm, "end": v(21.98, 21.14) * mm});
            skLineSegment(sketch, "E1863", {"start": v(21.98, 21.14) * mm, "end": v(21.99, 21.18) * mm});
            skLineSegment(sketch, "E1864", {"start": v(21.99, 21.18) * mm, "end": v(22, 21.22) * mm});
            skLineSegment(sketch, "E1865", {"start": v(22, 21.22) * mm, "end": v(22.02, 21.26) * mm});
            skLineSegment(sketch, "E1866", {"start": v(22.02, 21.26) * mm, "end": v(22.05, 21.3) * mm});
            skLineSegment(sketch, "E1867", {"start": v(22.05, 21.3) * mm, "end": v(22.06, 21.34) * mm});
            skLineSegment(sketch, "E1868", {"start": v(22.06, 21.34) * mm, "end": v(22.04, 21.39) * mm});
            skLineSegment(sketch, "E1869", {"start": v(22.04, 21.39) * mm, "end": v(21.96, 21.47) * mm});
            skLineSegment(sketch, "E1870", {"start": v(21.96, 21.47) * mm, "end": v(21.91, 21.5) * mm});
            skLineSegment(sketch, "E1871", {"start": v(21.91, 21.5) * mm, "end": v(21.87, 21.48) * mm});
            skLineSegment(sketch, "E1872", {"start": v(21.87, 21.48) * mm, "end": v(21.83, 21.46) * mm});
            skLineSegment(sketch, "E1873", {"start": v(21.83, 21.46) * mm, "end": v(21.8, 21.44) * mm});
            skLineSegment(sketch, "E1874", {"start": v(21.8, 21.44) * mm, "end": v(21.75, 21.42) * mm});
            skLineSegment(sketch, "E1875", {"start": v(21.75, 21.42) * mm, "end": v(21.7, 21.41) * mm});
            skLineSegment(sketch, "E1876", {"start": v(21.7, 21.41) * mm, "end": v(21.65, 21.42) * mm});
            skLineSegment(sketch, "E1877", {"start": v(21.65, 21.42) * mm, "end": v(21.6, 21.43) * mm});
            skLineSegment(sketch, "E1878", {"start": v(21.6, 21.43) * mm, "end": v(21.54, 21.46) * mm});
            skLineSegment(sketch, "E1879", {"start": v(21.54, 21.46) * mm, "end": v(21.5, 21.5) * mm});
            skLineSegment(sketch, "E1880", {"start": v(21.5, 21.5) * mm, "end": v(21.46, 21.54) * mm});
            skLineSegment(sketch, "E1881", {"start": v(21.46, 21.54) * mm, "end": v(21.43, 21.6) * mm});
            skLineSegment(sketch, "E1882", {"start": v(21.43, 21.6) * mm, "end": v(21.42, 21.65) * mm});
            skLineSegment(sketch, "E1883", {"start": v(21.42, 21.65) * mm, "end": v(21.41, 21.7) * mm});
            skLineSegment(sketch, "E1884", {"start": v(21.41, 21.7) * mm, "end": v(21.42, 21.75) * mm});
            skLineSegment(sketch, "E1885", {"start": v(21.42, 21.75) * mm, "end": v(21.44, 21.8) * mm});
            skLineSegment(sketch, "E1886", {"start": v(21.44, 21.8) * mm, "end": v(21.46, 21.83) * mm});
            skLineSegment(sketch, "E1887", {"start": v(21.46, 21.83) * mm, "end": v(21.48, 21.87) * mm});
            skLineSegment(sketch, "E1888", {"start": v(21.48, 21.87) * mm, "end": v(21.5, 21.91) * mm});
            skLineSegment(sketch, "E1889", {"start": v(21.5, 21.91) * mm, "end": v(21.47, 21.96) * mm});
            skLineSegment(sketch, "E1890", {"start": v(21.47, 21.96) * mm, "end": v(21.39, 22.04) * mm});
            skLineSegment(sketch, "E1891", {"start": v(21.39, 22.04) * mm, "end": v(21.34, 22.06) * mm});
            skLineSegment(sketch, "E1892", {"start": v(21.34, 22.06) * mm, "end": v(21.3, 22.05) * mm});
            skLineSegment(sketch, "E1893", {"start": v(21.3, 22.05) * mm, "end": v(21.26, 22.02) * mm});
            skLineSegment(sketch, "E1894", {"start": v(21.26, 22.02) * mm, "end": v(21.22, 22) * mm});
            skLineSegment(sketch, "E1895", {"start": v(21.22, 22) * mm, "end": v(21.18, 21.99) * mm});
            skLineSegment(sketch, "E1896", {"start": v(21.18, 21.99) * mm, "end": v(21.14, 21.98) * mm});
            skLineSegment(sketch, "E1897", {"start": v(21.14, 21.98) * mm, "end": v(21.08, 21.98) * mm});
            skLineSegment(sketch, "E1898", {"start": v(21.08, 21.98) * mm, "end": v(21.02, 22) * mm});
            skLineSegment(sketch, "E1899", {"start": v(21.02, 22) * mm, "end": v(20.97, 22.02) * mm});
            skLineSegment(sketch, "E1900", {"start": v(20.97, 22.02) * mm, "end": v(20.93, 22.05) * mm});
            skLineSegment(sketch, "E1901", {"start": v(20.93, 22.05) * mm, "end": v(20.89, 22.1) * mm});
            skLineSegment(sketch, "E1902", {"start": v(20.89, 22.1) * mm, "end": v(20.86, 22.15) * mm});
            skLineSegment(sketch, "E1903", {"start": v(20.86, 22.15) * mm, "end": v(20.84, 22.2) * mm});
            skLineSegment(sketch, "E1904", {"start": v(20.84, 22.2) * mm, "end": v(20.84, 22.26) * mm});
            skLineSegment(sketch, "E1905", {"start": v(20.84, 22.26) * mm, "end": v(20.85, 22.3) * mm});
            skLineSegment(sketch, "E1906", {"start": v(20.85, 22.3) * mm, "end": v(20.86, 22.35) * mm});
            skLineSegment(sketch, "E1907", {"start": v(20.86, 22.35) * mm, "end": v(20.88, 22.39) * mm});
            skLineSegment(sketch, "E1908", {"start": v(20.88, 22.39) * mm, "end": v(20.9, 22.43) * mm});
            skLineSegment(sketch, "E1909", {"start": v(20.9, 22.43) * mm, "end": v(20.91, 22.47) * mm});
            skLineSegment(sketch, "E1910", {"start": v(20.91, 22.47) * mm, "end": v(20.9, 22.51) * mm});
            skLineSegment(sketch, "E1911", {"start": v(20.9, 22.51) * mm, "end": v(20.8, 22.6) * mm});
            skLineSegment(sketch, "E1912", {"start": v(20.8, 22.6) * mm, "end": v(20.76, 22.61) * mm});
            skLineSegment(sketch, "E1913", {"start": v(20.76, 22.61) * mm, "end": v(20.72, 22.6) * mm});
            skLineSegment(sketch, "E1914", {"start": v(20.72, 22.6) * mm, "end": v(20.68, 22.57) * mm});
            skLineSegment(sketch, "E1915", {"start": v(20.68, 22.57) * mm, "end": v(20.64, 22.55) * mm});
            skLineSegment(sketch, "E1916", {"start": v(20.64, 22.55) * mm, "end": v(20.6, 22.53) * mm});
            skLineSegment(sketch, "E1917", {"start": v(20.6, 22.53) * mm, "end": v(20.56, 22.52) * mm});
            skLineSegment(sketch, "E1918", {"start": v(20.56, 22.52) * mm, "end": v(20.5, 22.52) * mm});
            skLineSegment(sketch, "E1919", {"start": v(20.5, 22.52) * mm, "end": v(20.44, 22.53) * mm});
            skLineSegment(sketch, "E1920", {"start": v(20.44, 22.53) * mm, "end": v(20.39, 22.56) * mm});
            skLineSegment(sketch, "E1921", {"start": v(20.39, 22.56) * mm, "end": v(20.34, 22.6) * mm});
            skLineSegment(sketch, "E1922", {"start": v(20.34, 22.6) * mm, "end": v(20.3, 22.64) * mm});
            skLineSegment(sketch, "E1923", {"start": v(20.3, 22.64) * mm, "end": v(20.27, 22.68) * mm});
            skLineSegment(sketch, "E1924", {"start": v(20.27, 22.68) * mm, "end": v(20.25, 22.74) * mm});
            skLineSegment(sketch, "E1925", {"start": v(20.25, 22.74) * mm, "end": v(20.25, 22.8) * mm});
            skLineSegment(sketch, "E1926", {"start": v(20.25, 22.8) * mm, "end": v(20.26, 22.84) * mm});
            skLineSegment(sketch, "E1927", {"start": v(20.26, 22.84) * mm, "end": v(20.27, 22.89) * mm});
            skLineSegment(sketch, "E1928", {"start": v(20.27, 22.89) * mm, "end": v(20.29, 22.93) * mm});
            skLineSegment(sketch, "E1929", {"start": v(20.29, 22.93) * mm, "end": v(20.3, 22.96) * mm});
            skLineSegment(sketch, "E1930", {"start": v(20.3, 22.96) * mm, "end": v(20.32, 23) * mm});
            skLineSegment(sketch, "E1931", {"start": v(20.32, 23) * mm, "end": v(20.3, 23.05) * mm});
            skLineSegment(sketch, "E1932", {"start": v(20.3, 23.05) * mm, "end": v(20.2, 23.13) * mm});
            skLineSegment(sketch, "E1933", {"start": v(20.2, 23.13) * mm, "end": v(20.16, 23.15) * mm});
            skLineSegment(sketch, "E1934", {"start": v(20.16, 23.15) * mm, "end": v(20.12, 23.13) * mm});
            skLineSegment(sketch, "E1935", {"start": v(20.12, 23.13) * mm, "end": v(20.08, 23.1) * mm});
            skLineSegment(sketch, "E1936", {"start": v(20.08, 23.1) * mm, "end": v(20.04, 23.08) * mm});
            skLineSegment(sketch, "E1937", {"start": v(20.04, 23.08) * mm, "end": v(20, 23.07) * mm});
            skLineSegment(sketch, "E1938", {"start": v(20, 23.07) * mm, "end": v(19.96, 23.05) * mm});
            skLineSegment(sketch, "E1939", {"start": v(19.96, 23.05) * mm, "end": v(19.9, 23.05) * mm});
            skLineSegment(sketch, "E1940", {"start": v(19.9, 23.05) * mm, "end": v(19.84, 23.06) * mm});
            skLineSegment(sketch, "E1941", {"start": v(19.84, 23.06) * mm, "end": v(19.8, 23.08) * mm});
            skLineSegment(sketch, "E1942", {"start": v(19.8, 23.08) * mm, "end": v(19.74, 23.12) * mm});
            skLineSegment(sketch, "E1943", {"start": v(19.74, 23.12) * mm, "end": v(19.7, 23.16) * mm});
            skLineSegment(sketch, "E1944", {"start": v(19.7, 23.16) * mm, "end": v(19.67, 23.2) * mm});
            skLineSegment(sketch, "E1945", {"start": v(19.67, 23.2) * mm, "end": v(19.65, 23.26) * mm});
            skLineSegment(sketch, "E1946", {"start": v(19.65, 23.26) * mm, "end": v(19.65, 23.32) * mm});
            skLineSegment(sketch, "E1947", {"start": v(19.65, 23.32) * mm, "end": v(19.65, 23.36) * mm});
            skLineSegment(sketch, "E1948", {"start": v(19.65, 23.36) * mm, "end": v(19.66, 23.4) * mm});
            skLineSegment(sketch, "E1949", {"start": v(19.66, 23.4) * mm, "end": v(19.68, 23.45) * mm});
            skLineSegment(sketch, "E1950", {"start": v(19.68, 23.45) * mm, "end": v(19.7, 23.49) * mm});
            skLineSegment(sketch, "E1951", {"start": v(19.7, 23.49) * mm, "end": v(19.7, 23.53) * mm});
            skLineSegment(sketch, "E1952", {"start": v(19.7, 23.53) * mm, "end": v(19.68, 23.57) * mm});
            skLineSegment(sketch, "E1953", {"start": v(19.68, 23.57) * mm, "end": v(19.6, 23.65) * mm});
            skLineSegment(sketch, "E1954", {"start": v(19.6, 23.65) * mm, "end": v(19.55, 23.67) * mm});
            skLineSegment(sketch, "E1955", {"start": v(19.55, 23.67) * mm, "end": v(19.5, 23.65) * mm});
            skLineSegment(sketch, "E1956", {"start": v(19.5, 23.65) * mm, "end": v(19.47, 23.62) * mm});
            skLineSegment(sketch, "E1957", {"start": v(19.47, 23.62) * mm, "end": v(19.43, 23.6) * mm});
            skLineSegment(sketch, "E1958", {"start": v(19.43, 23.6) * mm, "end": v(19.4, 23.58) * mm});
            skLineSegment(sketch, "E1959", {"start": v(19.4, 23.58) * mm, "end": v(19.35, 23.57) * mm});
            skLineSegment(sketch, "E1960", {"start": v(19.35, 23.57) * mm, "end": v(19.3, 23.56) * mm});
            skLineSegment(sketch, "E1961", {"start": v(19.3, 23.56) * mm, "end": v(19.23, 23.57) * mm});
            skLineSegment(sketch, "E1962", {"start": v(19.23, 23.57) * mm, "end": v(19.18, 23.6) * mm});
            skLineSegment(sketch, "E1963", {"start": v(19.18, 23.6) * mm, "end": v(19.13, 23.63) * mm});
            skLineSegment(sketch, "E1964", {"start": v(19.13, 23.63) * mm, "end": v(19.09, 23.67) * mm});
            skLineSegment(sketch, "E1965", {"start": v(19.09, 23.67) * mm, "end": v(19.06, 23.71) * mm});
            skLineSegment(sketch, "E1966", {"start": v(19.06, 23.71) * mm, "end": v(19.04, 23.77) * mm});
            skLineSegment(sketch, "E1967", {"start": v(19.04, 23.77) * mm, "end": v(19.03, 23.83) * mm});
            skLineSegment(sketch, "E1968", {"start": v(19.03, 23.83) * mm, "end": v(19.03, 23.87) * mm});
            skLineSegment(sketch, "E1969", {"start": v(19.03, 23.87) * mm, "end": v(19.04, 23.92) * mm});
            skLineSegment(sketch, "E1970", {"start": v(19.04, 23.92) * mm, "end": v(19.06, 23.96) * mm});
            skLineSegment(sketch, "E1971", {"start": v(19.06, 23.96) * mm, "end": v(19.08, 24) * mm});
            skLineSegment(sketch, "E1972", {"start": v(19.08, 24) * mm, "end": v(19.09, 24.04) * mm});
            skLineSegment(sketch, "E1973", {"start": v(19.09, 24.04) * mm, "end": v(19.06, 24.08) * mm});
            skLineSegment(sketch, "E1974", {"start": v(19.06, 24.08) * mm, "end": v(18.96, 24.15) * mm});
            skLineSegment(sketch, "E1975", {"start": v(18.96, 24.15) * mm, "end": v(18.92, 24.17) * mm});
            skLineSegment(sketch, "E1976", {"start": v(18.92, 24.17) * mm, "end": v(18.88, 24.15) * mm});
            skLineSegment(sketch, "E1977", {"start": v(18.88, 24.15) * mm, "end": v(18.85, 24.13) * mm});
            skLineSegment(sketch, "E1978", {"start": v(18.85, 24.13) * mm, "end": v(18.8, 24.1) * mm});
            skLineSegment(sketch, "E1979", {"start": v(18.8, 24.1) * mm, "end": v(18.77, 24.08) * mm});
            skLineSegment(sketch, "E1980", {"start": v(18.77, 24.08) * mm, "end": v(18.73, 24.06) * mm});
            skLineSegment(sketch, "E1981", {"start": v(18.73, 24.06) * mm, "end": v(18.67, 24.06) * mm});
            skLineSegment(sketch, "E1982", {"start": v(18.67, 24.06) * mm, "end": v(18.61, 24.07) * mm});
            skLineSegment(sketch, "E1983", {"start": v(18.61, 24.07) * mm, "end": v(18.56, 24.09) * mm});
            skLineSegment(sketch, "E1984", {"start": v(18.56, 24.09) * mm, "end": v(18.5, 24.12) * mm});
            skLineSegment(sketch, "E1985", {"start": v(18.5, 24.12) * mm, "end": v(18.46, 24.16) * mm});
            skLineSegment(sketch, "E1986", {"start": v(18.46, 24.16) * mm, "end": v(18.43, 24.2) * mm});
            skLineSegment(sketch, "E1987", {"start": v(18.43, 24.2) * mm, "end": v(18.4, 24.26) * mm});
            skLineSegment(sketch, "E1988", {"start": v(18.4, 24.26) * mm, "end": v(18.4, 24.32) * mm});
            skLineSegment(sketch, "E1989", {"start": v(18.4, 24.32) * mm, "end": v(18.4, 24.36) * mm});
            skLineSegment(sketch, "E1990", {"start": v(18.4, 24.36) * mm, "end": v(18.41, 24.4) * mm});
            skLineSegment(sketch, "E1991", {"start": v(18.41, 24.4) * mm, "end": v(18.43, 24.45) * mm});
            skLineSegment(sketch, "E1992", {"start": v(18.43, 24.45) * mm, "end": v(18.45, 24.49) * mm});
            skLineSegment(sketch, "E1993", {"start": v(18.45, 24.49) * mm, "end": v(18.45, 24.53) * mm});
            skLineSegment(sketch, "E1994", {"start": v(18.45, 24.53) * mm, "end": v(18.42, 24.57) * mm});
            skLineSegment(sketch, "E1995", {"start": v(18.42, 24.57) * mm, "end": v(18.33, 24.64) * mm});
            skLineSegment(sketch, "E1996", {"start": v(18.33, 24.64) * mm, "end": v(18.28, 24.66) * mm});
            skLineSegment(sketch, "E1997", {"start": v(18.28, 24.66) * mm, "end": v(18.24, 24.64) * mm});
            skLineSegment(sketch, "E1998", {"start": v(18.24, 24.64) * mm, "end": v(18.2, 24.61) * mm});
            skLineSegment(sketch, "E1999", {"start": v(18.2, 24.61) * mm, "end": v(18.17, 24.58) * mm});
            skLineSegment(sketch, "E2000", {"start": v(18.17, 24.58) * mm, "end": v(18.13, 24.56) * mm});
            skLineSegment(sketch, "E2001", {"start": v(18.13, 24.56) * mm, "end": v(18.09, 24.55) * mm});
            skLineSegment(sketch, "E2002", {"start": v(18.09, 24.55) * mm, "end": v(18.03, 24.54) * mm});
            skLineSegment(sketch, "E2003", {"start": v(18.03, 24.54) * mm, "end": v(17.97, 24.55) * mm});
            skLineSegment(sketch, "E2004", {"start": v(17.97, 24.55) * mm, "end": v(17.92, 24.56) * mm});
            skLineSegment(sketch, "E2005", {"start": v(17.92, 24.56) * mm, "end": v(17.87, 24.6) * mm});
            skLineSegment(sketch, "E2006", {"start": v(17.87, 24.6) * mm, "end": v(17.83, 24.63) * mm});
            skLineSegment(sketch, "E2007", {"start": v(17.83, 24.63) * mm, "end": v(17.8, 24.68) * mm});
            skLineSegment(sketch, "E2008", {"start": v(17.8, 24.68) * mm, "end": v(17.77, 24.73) * mm});
            skLineSegment(sketch, "E2009", {"start": v(17.77, 24.73) * mm, "end": v(17.76, 24.79) * mm});
            skLineSegment(sketch, "E2010", {"start": v(17.76, 24.79) * mm, "end": v(17.76, 24.83) * mm});
            skLineSegment(sketch, "E2011", {"start": v(17.76, 24.83) * mm, "end": v(17.77, 24.88) * mm});
            skLineSegment(sketch, "E2012", {"start": v(17.77, 24.88) * mm, "end": v(17.78, 24.92) * mm});
            skLineSegment(sketch, "E2013", {"start": v(17.78, 24.92) * mm, "end": v(17.8, 24.96) * mm});
            skLineSegment(sketch, "E2014", {"start": v(17.8, 24.96) * mm, "end": v(17.8, 25) * mm});
            skLineSegment(sketch, "E2015", {"start": v(17.8, 25) * mm, "end": v(17.77, 25.04) * mm});
            skLineSegment(sketch, "E2016", {"start": v(17.77, 25.04) * mm, "end": v(17.67, 25.11) * mm});
            skLineSegment(sketch, "E2017", {"start": v(17.67, 25.11) * mm, "end": v(17.63, 25.13) * mm});
            skLineSegment(sketch, "E2018", {"start": v(17.63, 25.13) * mm, "end": v(17.59, 25.1) * mm});
            skLineSegment(sketch, "E2019", {"start": v(17.59, 25.1) * mm, "end": v(17.56, 25.08) * mm});
            skLineSegment(sketch, "E2020", {"start": v(17.56, 25.08) * mm, "end": v(17.52, 25.05) * mm});
            skLineSegment(sketch, "E2021", {"start": v(17.52, 25.05) * mm, "end": v(17.48, 25.03) * mm});
            skLineSegment(sketch, "E2022", {"start": v(17.48, 25.03) * mm, "end": v(17.44, 25.01) * mm});
            skLineSegment(sketch, "E2023", {"start": v(17.44, 25.01) * mm, "end": v(17.38, 25) * mm});
            skLineSegment(sketch, "E2024", {"start": v(17.38, 25) * mm, "end": v(17.33, 25) * mm});
            skLineSegment(sketch, "E2025", {"start": v(17.33, 25) * mm, "end": v(17.27, 25.03) * mm});
            skLineSegment(sketch, "E2026", {"start": v(17.27, 25.03) * mm, "end": v(17.22, 25.05) * mm});
            skLineSegment(sketch, "E2027", {"start": v(17.22, 25.05) * mm, "end": v(17.17, 25.1) * mm});
            skLineSegment(sketch, "E2028", {"start": v(17.17, 25.1) * mm, "end": v(17.14, 25.14) * mm});
            skLineSegment(sketch, "E2029", {"start": v(17.14, 25.14) * mm, "end": v(17.11, 25.19) * mm});
            skLineSegment(sketch, "E2030", {"start": v(17.11, 25.19) * mm, "end": v(17.1, 25.25) * mm});
            skLineSegment(sketch, "E2031", {"start": v(17.1, 25.25) * mm, "end": v(17.1, 25.3) * mm});
            skLineSegment(sketch, "E2032", {"start": v(17.1, 25.3) * mm, "end": v(17.1, 25.34) * mm});
            skLineSegment(sketch, "E2033", {"start": v(17.1, 25.34) * mm, "end": v(17.12, 25.38) * mm});
            skLineSegment(sketch, "E2034", {"start": v(17.12, 25.38) * mm, "end": v(17.14, 25.42) * mm});
            skLineSegment(sketch, "E2035", {"start": v(17.14, 25.42) * mm, "end": v(17.14, 25.46) * mm});
            skLineSegment(sketch, "E2036", {"start": v(17.14, 25.46) * mm, "end": v(17.11, 25.5) * mm});
            skLineSegment(sketch, "E2037", {"start": v(17.11, 25.5) * mm, "end": v(17.01, 25.57) * mm});
            skLineSegment(sketch, "E2038", {"start": v(17.01, 25.57) * mm, "end": v(16.97, 25.58) * mm});
            skLineSegment(sketch, "E2039", {"start": v(16.97, 25.58) * mm, "end": v(16.93, 25.56) * mm});
            skLineSegment(sketch, "E2040", {"start": v(16.93, 25.56) * mm, "end": v(16.9, 25.53) * mm});
            skLineSegment(sketch, "E2041", {"start": v(16.9, 25.53) * mm, "end": v(16.86, 25.5) * mm});
            skLineSegment(sketch, "E2042", {"start": v(16.86, 25.5) * mm, "end": v(16.82, 25.48) * mm});
            skLineSegment(sketch, "E2043", {"start": v(16.82, 25.48) * mm, "end": v(16.78, 25.46) * mm});
            skLineSegment(sketch, "E2044", {"start": v(16.78, 25.46) * mm, "end": v(16.72, 25.45) * mm});
            skLineSegment(sketch, "E2045", {"start": v(16.72, 25.45) * mm, "end": v(16.67, 25.45) * mm});
            skLineSegment(sketch, "E2046", {"start": v(16.67, 25.45) * mm, "end": v(16.6, 25.47) * mm});
            skLineSegment(sketch, "E2047", {"start": v(16.6, 25.47) * mm, "end": v(16.56, 25.5) * mm});
            skLineSegment(sketch, "E2048", {"start": v(16.56, 25.5) * mm, "end": v(16.51, 25.53) * mm});
            skLineSegment(sketch, "E2049", {"start": v(16.51, 25.53) * mm, "end": v(16.47, 25.58) * mm});
            skLineSegment(sketch, "E2050", {"start": v(16.47, 25.58) * mm, "end": v(16.45, 25.63) * mm});
            skLineSegment(sketch, "E2051", {"start": v(16.45, 25.63) * mm, "end": v(16.43, 25.68) * mm});
            skLineSegment(sketch, "E2052", {"start": v(16.43, 25.68) * mm, "end": v(16.43, 25.73) * mm});
            skLineSegment(sketch, "E2053", {"start": v(16.43, 25.73) * mm, "end": v(16.44, 25.77) * mm});
            skLineSegment(sketch, "E2054", {"start": v(16.44, 25.77) * mm, "end": v(16.45, 25.82) * mm});
            skLineSegment(sketch, "E2055", {"start": v(16.45, 25.82) * mm, "end": v(16.47, 25.86) * mm});
            skLineSegment(sketch, "E2056", {"start": v(16.47, 25.86) * mm, "end": v(16.47, 25.9) * mm});
            skLineSegment(sketch, "E2057", {"start": v(16.47, 25.9) * mm, "end": v(16.44, 25.94) * mm});
            skLineSegment(sketch, "E2058", {"start": v(16.44, 25.94) * mm, "end": v(16.34, 26) * mm});
            skLineSegment(sketch, "E2059", {"start": v(16.34, 26) * mm, "end": v(16.3, 26.02) * mm});
            skLineSegment(sketch, "E2060", {"start": v(16.3, 26.02) * mm, "end": v(16.25, 26) * mm});
            skLineSegment(sketch, "E2061", {"start": v(16.25, 26) * mm, "end": v(16.22, 25.96) * mm});
            skLineSegment(sketch, "E2062", {"start": v(16.22, 25.96) * mm, "end": v(16.19, 25.93) * mm});
            skLineSegment(sketch, "E2063", {"start": v(16.19, 25.93) * mm, "end": v(16.15, 25.91) * mm});
            skLineSegment(sketch, "E2064", {"start": v(16.15, 25.91) * mm, "end": v(16.1, 25.89) * mm});
            skLineSegment(sketch, "E2065", {"start": v(16.1, 25.89) * mm, "end": v(16.05, 25.88) * mm});
            skLineSegment(sketch, "E2066", {"start": v(16.05, 25.88) * mm, "end": v(16, 25.88) * mm});
            skLineSegment(sketch, "E2067", {"start": v(16, 25.88) * mm, "end": v(15.94, 25.9) * mm});
            skLineSegment(sketch, "E2068", {"start": v(15.94, 25.9) * mm, "end": v(15.88, 25.92) * mm});
            skLineSegment(sketch, "E2069", {"start": v(15.88, 25.92) * mm, "end": v(15.84, 25.96) * mm});
            skLineSegment(sketch, "E2070", {"start": v(15.84, 25.96) * mm, "end": v(15.8, 26) * mm});
            skLineSegment(sketch, "E2071", {"start": v(15.8, 26) * mm, "end": v(15.77, 26.05) * mm});
            skLineSegment(sketch, "E2072", {"start": v(15.77, 26.05) * mm, "end": v(15.76, 26.1) * mm});
            skLineSegment(sketch, "E2073", {"start": v(15.76, 26.1) * mm, "end": v(15.75, 26.15) * mm});
            skLineSegment(sketch, "E2074", {"start": v(15.75, 26.15) * mm, "end": v(15.76, 26.2) * mm});
            skLineSegment(sketch, "E2075", {"start": v(15.76, 26.2) * mm, "end": v(15.77, 26.24) * mm});
            skLineSegment(sketch, "E2076", {"start": v(15.77, 26.24) * mm, "end": v(15.78, 26.28) * mm});
            skLineSegment(sketch, "E2077", {"start": v(15.78, 26.28) * mm, "end": v(15.78, 26.33) * mm});
            skLineSegment(sketch, "E2078", {"start": v(15.78, 26.33) * mm, "end": v(15.75, 26.36) * mm});
            skLineSegment(sketch, "E2079", {"start": v(15.75, 26.36) * mm, "end": v(15.65, 26.42) * mm});
            skLineSegment(sketch, "E2080", {"start": v(15.65, 26.42) * mm, "end": v(15.6, 26.43) * mm});
            skLineSegment(sketch, "E2081", {"start": v(15.6, 26.43) * mm, "end": v(15.56, 26.41) * mm});
            skLineSegment(sketch, "E2082", {"start": v(15.56, 26.41) * mm, "end": v(15.54, 26.38) * mm});
            skLineSegment(sketch, "E2083", {"start": v(15.54, 26.38) * mm, "end": v(15.5, 26.35) * mm});
            skLineSegment(sketch, "E2084", {"start": v(15.5, 26.35) * mm, "end": v(15.46, 26.32) * mm});
            skLineSegment(sketch, "E2085", {"start": v(15.46, 26.32) * mm, "end": v(15.42, 26.3) * mm});
            skLineSegment(sketch, "E2086", {"start": v(15.42, 26.3) * mm, "end": v(15.37, 26.3) * mm});
            skLineSegment(sketch, "E2087", {"start": v(15.37, 26.3) * mm, "end": v(15.31, 26.3) * mm});
            skLineSegment(sketch, "E2088", {"start": v(15.31, 26.3) * mm, "end": v(15.25, 26.3) * mm});
            skLineSegment(sketch, "E2089", {"start": v(15.25, 26.3) * mm, "end": v(15.2, 26.33) * mm});
            skLineSegment(sketch, "E2090", {"start": v(15.2, 26.33) * mm, "end": v(15.15, 26.36) * mm});
            skLineSegment(sketch, "E2091", {"start": v(15.15, 26.36) * mm, "end": v(15.11, 26.4) * mm});
            skLineSegment(sketch, "E2092", {"start": v(15.11, 26.4) * mm, "end": v(15.08, 26.45) * mm});
            skLineSegment(sketch, "E2093", {"start": v(15.08, 26.45) * mm, "end": v(15.07, 26.5) * mm});
            skLineSegment(sketch, "E2094", {"start": v(15.07, 26.5) * mm, "end": v(15.06, 26.55) * mm});
            skLineSegment(sketch, "E2095", {"start": v(15.06, 26.55) * mm, "end": v(15.07, 26.6) * mm});
            skLineSegment(sketch, "E2096", {"start": v(15.07, 26.6) * mm, "end": v(15.08, 26.64) * mm});
            skLineSegment(sketch, "E2097", {"start": v(15.08, 26.64) * mm, "end": v(15.1, 26.69) * mm});
            skLineSegment(sketch, "E2098", {"start": v(15.1, 26.69) * mm, "end": v(15.1, 26.73) * mm});
            skLineSegment(sketch, "E2099", {"start": v(15.1, 26.73) * mm, "end": v(15.06, 26.76) * mm});
            skLineSegment(sketch, "E2100", {"start": v(15.06, 26.76) * mm, "end": v(14.95, 26.82) * mm});
            skLineSegment(sketch, "E2101", {"start": v(14.95, 26.82) * mm, "end": v(14.9, 26.83) * mm});
            skLineSegment(sketch, "E2102", {"start": v(14.9, 26.83) * mm, "end": v(14.87, 26.81) * mm});
            skLineSegment(sketch, "E2103", {"start": v(14.87, 26.81) * mm, "end": v(14.84, 26.78) * mm});
            skLineSegment(sketch, "E2104", {"start": v(14.84, 26.78) * mm, "end": v(14.8, 26.75) * mm});
            skLineSegment(sketch, "E2105", {"start": v(14.8, 26.75) * mm, "end": v(14.77, 26.72) * mm});
            skLineSegment(sketch, "E2106", {"start": v(14.77, 26.72) * mm, "end": v(14.73, 26.7) * mm});
            skLineSegment(sketch, "E2107", {"start": v(14.73, 26.7) * mm, "end": v(14.67, 26.68) * mm});
            skLineSegment(sketch, "E2108", {"start": v(14.67, 26.68) * mm, "end": v(14.62, 26.68) * mm});
            skLineSegment(sketch, "E2109", {"start": v(14.62, 26.68) * mm, "end": v(14.56, 26.7) * mm});
            skLineSegment(sketch, "E2110", {"start": v(14.56, 26.7) * mm, "end": v(14.5, 26.72) * mm});
            skLineSegment(sketch, "E2111", {"start": v(14.5, 26.72) * mm, "end": v(14.46, 26.75) * mm});
            skLineSegment(sketch, "E2112", {"start": v(14.46, 26.75) * mm, "end": v(14.42, 26.8) * mm});
            skLineSegment(sketch, "E2113", {"start": v(14.42, 26.8) * mm, "end": v(14.39, 26.84) * mm});
            skLineSegment(sketch, "E2114", {"start": v(14.39, 26.84) * mm, "end": v(14.37, 26.9) * mm});
            skLineSegment(sketch, "E2115", {"start": v(14.37, 26.9) * mm, "end": v(14.36, 26.94) * mm});
            skLineSegment(sketch, "E2116", {"start": v(14.36, 26.94) * mm, "end": v(14.37, 26.99) * mm});
            skLineSegment(sketch, "E2117", {"start": v(14.37, 26.99) * mm, "end": v(14.37, 27.03) * mm});
            skLineSegment(sketch, "E2118", {"start": v(14.37, 27.03) * mm, "end": v(14.39, 27.07) * mm});
            skLineSegment(sketch, "E2119", {"start": v(14.39, 27.07) * mm, "end": v(14.39, 27.12) * mm});
            skLineSegment(sketch, "E2120", {"start": v(14.39, 27.12) * mm, "end": v(14.35, 27.15) * mm});
            skLineSegment(sketch, "E2121", {"start": v(14.35, 27.15) * mm, "end": v(14.25, 27.2) * mm});
            skLineSegment(sketch, "E2122", {"start": v(14.25, 27.2) * mm, "end": v(14.2, 27.21) * mm});
            skLineSegment(sketch, "E2123", {"start": v(14.2, 27.21) * mm, "end": v(14.16, 27.2) * mm});
            skLineSegment(sketch, "E2124", {"start": v(14.16, 27.2) * mm, "end": v(14.13, 27.16) * mm});
            skLineSegment(sketch, "E2125", {"start": v(14.13, 27.16) * mm, "end": v(14.1, 27.12) * mm});
            skLineSegment(sketch, "E2126", {"start": v(14.1, 27.12) * mm, "end": v(14.07, 27.1) * mm});
            skLineSegment(sketch, "E2127", {"start": v(14.07, 27.1) * mm, "end": v(14.03, 27.07) * mm});
            skLineSegment(sketch, "E2128", {"start": v(14.03, 27.07) * mm, "end": v(13.97, 27.06) * mm});
            skLineSegment(sketch, "E2129", {"start": v(13.97, 27.06) * mm, "end": v(13.91, 27.06) * mm});
            skLineSegment(sketch, "E2130", {"start": v(13.91, 27.06) * mm, "end": v(13.86, 27.07) * mm});
            skLineSegment(sketch, "E2131", {"start": v(13.86, 27.07) * mm, "end": v(13.8, 27.09) * mm});
            skLineSegment(sketch, "E2132", {"start": v(13.8, 27.09) * mm, "end": v(13.75, 27.12) * mm});
            skLineSegment(sketch, "E2133", {"start": v(13.75, 27.12) * mm, "end": v(13.71, 27.16) * mm});
            skLineSegment(sketch, "E2134", {"start": v(13.71, 27.16) * mm, "end": v(13.68, 27.2) * mm});
            skLineSegment(sketch, "E2135", {"start": v(13.68, 27.2) * mm, "end": v(13.66, 27.26) * mm});
            skLineSegment(sketch, "E2136", {"start": v(13.66, 27.26) * mm, "end": v(13.65, 27.3) * mm});
            skLineSegment(sketch, "E2137", {"start": v(13.65, 27.3) * mm, "end": v(13.66, 27.35) * mm});
            skLineSegment(sketch, "E2138", {"start": v(13.66, 27.35) * mm, "end": v(13.66, 27.4) * mm});
            skLineSegment(sketch, "E2139", {"start": v(13.66, 27.4) * mm, "end": v(13.67, 27.44) * mm});
            skLineSegment(sketch, "E2140", {"start": v(13.67, 27.44) * mm, "end": v(13.67, 27.48) * mm});
            skLineSegment(sketch, "E2141", {"start": v(13.67, 27.48) * mm, "end": v(13.64, 27.52) * mm});
            skLineSegment(sketch, "E2142", {"start": v(13.64, 27.52) * mm, "end": v(13.53, 27.57) * mm});
            skLineSegment(sketch, "E2143", {"start": v(13.53, 27.57) * mm, "end": v(13.48, 27.58) * mm});
            skLineSegment(sketch, "E2144", {"start": v(13.48, 27.58) * mm, "end": v(13.44, 27.55) * mm});
            skLineSegment(sketch, "E2145", {"start": v(13.44, 27.55) * mm, "end": v(13.42, 27.52) * mm});
            skLineSegment(sketch, "E2146", {"start": v(13.42, 27.52) * mm, "end": v(13.39, 27.48) * mm});
            skLineSegment(sketch, "E2147", {"start": v(13.39, 27.48) * mm, "end": v(13.35, 27.46) * mm});
            skLineSegment(sketch, "E2148", {"start": v(13.35, 27.46) * mm, "end": v(13.31, 27.43) * mm});
            skLineSegment(sketch, "E2149", {"start": v(13.31, 27.43) * mm, "end": v(13.26, 27.41) * mm});
            skLineSegment(sketch, "E2150", {"start": v(13.26, 27.41) * mm, "end": v(13.2, 27.41) * mm});
            skLineSegment(sketch, "E2151", {"start": v(13.2, 27.41) * mm, "end": v(13.14, 27.42) * mm});
            skLineSegment(sketch, "E2152", {"start": v(13.14, 27.42) * mm, "end": v(13.09, 27.44) * mm});
            skLineSegment(sketch, "E2153", {"start": v(13.09, 27.44) * mm, "end": v(13.04, 27.47) * mm});
            skLineSegment(sketch, "E2154", {"start": v(13.04, 27.47) * mm, "end": v(13, 27.5) * mm});
            skLineSegment(sketch, "E2155", {"start": v(13, 27.5) * mm, "end": v(12.96, 27.56) * mm});
            skLineSegment(sketch, "E2156", {"start": v(12.96, 27.56) * mm, "end": v(12.94, 27.6) * mm});
            skLineSegment(sketch, "E2157", {"start": v(12.94, 27.6) * mm, "end": v(12.94, 27.65) * mm});
            skLineSegment(sketch, "E2158", {"start": v(12.94, 27.65) * mm, "end": v(12.93, 27.7) * mm});
            skLineSegment(sketch, "E2159", {"start": v(12.93, 27.7) * mm, "end": v(12.94, 27.74) * mm});
            skLineSegment(sketch, "E2160", {"start": v(12.94, 27.74) * mm, "end": v(12.95, 27.79) * mm});
            skLineSegment(sketch, "E2161", {"start": v(12.95, 27.79) * mm, "end": v(12.95, 27.83) * mm});
            skLineSegment(sketch, "E2162", {"start": v(12.95, 27.83) * mm, "end": v(12.91, 27.86) * mm});
            skLineSegment(sketch, "E2163", {"start": v(12.91, 27.86) * mm, "end": v(12.8, 27.91) * mm});
            skLineSegment(sketch, "E2164", {"start": v(12.8, 27.91) * mm, "end": v(12.75, 27.92) * mm});
            skLineSegment(sketch, "E2165", {"start": v(12.75, 27.92) * mm, "end": v(12.72, 27.9) * mm});
            skLineSegment(sketch, "E2166", {"start": v(12.72, 27.9) * mm, "end": v(12.7, 27.86) * mm});
            skLineSegment(sketch, "E2167", {"start": v(12.7, 27.86) * mm, "end": v(12.66, 27.83) * mm});
            skLineSegment(sketch, "E2168", {"start": v(12.66, 27.83) * mm, "end": v(12.63, 27.8) * mm});
            skLineSegment(sketch, "E2169", {"start": v(12.63, 27.8) * mm, "end": v(12.6, 27.77) * mm});
            skLineSegment(sketch, "E2170", {"start": v(12.6, 27.77) * mm, "end": v(12.54, 27.75) * mm});
            skLineSegment(sketch, "E2171", {"start": v(12.54, 27.75) * mm, "end": v(12.48, 27.75) * mm});
            skLineSegment(sketch, "E2172", {"start": v(12.48, 27.75) * mm, "end": v(12.42, 27.75) * mm});
            skLineSegment(sketch, "E2173", {"start": v(12.42, 27.75) * mm, "end": v(12.36, 27.77) * mm});
            skLineSegment(sketch, "E2174", {"start": v(12.36, 27.77) * mm, "end": v(12.31, 27.8) * mm});
            skLineSegment(sketch, "E2175", {"start": v(12.31, 27.8) * mm, "end": v(12.27, 27.84) * mm});
            skLineSegment(sketch, "E2176", {"start": v(12.27, 27.84) * mm, "end": v(12.24, 27.89) * mm});
            skLineSegment(sketch, "E2177", {"start": v(12.24, 27.89) * mm, "end": v(12.21, 27.94) * mm});
            skLineSegment(sketch, "E2178", {"start": v(12.21, 27.94) * mm, "end": v(12.2, 27.98) * mm});
            skLineSegment(sketch, "E2179", {"start": v(12.2, 27.98) * mm, "end": v(12.2, 28.03) * mm});
            skLineSegment(sketch, "E2180", {"start": v(12.2, 28.03) * mm, "end": v(12.2, 28.07) * mm});
            skLineSegment(sketch, "E2181", {"start": v(12.2, 28.07) * mm, "end": v(12.22, 28.12) * mm});
            skLineSegment(sketch, "E2182", {"start": v(12.22, 28.12) * mm, "end": v(12.21, 28.16) * mm});
            skLineSegment(sketch, "E2183", {"start": v(12.21, 28.16) * mm, "end": v(12.18, 28.2) * mm});
            skLineSegment(sketch, "E2184", {"start": v(12.18, 28.2) * mm, "end": v(12.07, 28.24) * mm});
            skLineSegment(sketch, "E2185", {"start": v(12.07, 28.24) * mm, "end": v(12.02, 28.24) * mm});
            skLineSegment(sketch, "E2186", {"start": v(12.02, 28.24) * mm, "end": v(11.98, 28.22) * mm});
            skLineSegment(sketch, "E2187", {"start": v(11.98, 28.22) * mm, "end": v(11.96, 28.18) * mm});
            skLineSegment(sketch, "E2188", {"start": v(11.96, 28.18) * mm, "end": v(11.93, 28.15) * mm});
            skLineSegment(sketch, "E2189", {"start": v(11.93, 28.15) * mm, "end": v(11.9, 28.12) * mm});
            skLineSegment(sketch, "E2190", {"start": v(11.9, 28.12) * mm, "end": v(11.86, 28.1) * mm});
            skLineSegment(sketch, "E2191", {"start": v(11.86, 28.1) * mm, "end": v(11.8, 28.07) * mm});
            skLineSegment(sketch, "E2192", {"start": v(11.8, 28.07) * mm, "end": v(11.75, 28.06) * mm});
            skLineSegment(sketch, "E2193", {"start": v(11.75, 28.06) * mm, "end": v(11.69, 28.07) * mm});
            skLineSegment(sketch, "E2194", {"start": v(11.69, 28.07) * mm, "end": v(11.63, 28.09) * mm});
            skLineSegment(sketch, "E2195", {"start": v(11.63, 28.09) * mm, "end": v(11.58, 28.11) * mm});
            skLineSegment(sketch, "E2196", {"start": v(11.58, 28.11) * mm, "end": v(11.54, 28.15) * mm});
            skLineSegment(sketch, "E2197", {"start": v(11.54, 28.15) * mm, "end": v(11.5, 28.2) * mm});
            skLineSegment(sketch, "E2198", {"start": v(11.5, 28.2) * mm, "end": v(11.48, 28.25) * mm});
            skLineSegment(sketch, "E2199", {"start": v(11.48, 28.25) * mm, "end": v(11.47, 28.3) * mm});
            skLineSegment(sketch, "E2200", {"start": v(11.47, 28.3) * mm, "end": v(11.47, 28.34) * mm});
            skLineSegment(sketch, "E2201", {"start": v(11.47, 28.34) * mm, "end": v(11.47, 28.38) * mm});
            skLineSegment(sketch, "E2202", {"start": v(11.47, 28.38) * mm, "end": v(11.48, 28.43) * mm});
            skLineSegment(sketch, "E2203", {"start": v(11.48, 28.43) * mm, "end": v(11.47, 28.47) * mm});
            skLineSegment(sketch, "E2204", {"start": v(11.47, 28.47) * mm, "end": v(11.44, 28.5) * mm});
            skLineSegment(sketch, "E2205", {"start": v(11.44, 28.5) * mm, "end": v(11.32, 28.55) * mm});
            skLineSegment(sketch, "E2206", {"start": v(11.32, 28.55) * mm, "end": v(11.28, 28.55) * mm});
            skLineSegment(sketch, "E2207", {"start": v(11.28, 28.55) * mm, "end": v(11.24, 28.52) * mm});
            skLineSegment(sketch, "E2208", {"start": v(11.24, 28.52) * mm, "end": v(11.22, 28.48) * mm});
            skLineSegment(sketch, "E2209", {"start": v(11.22, 28.48) * mm, "end": v(11.19, 28.45) * mm});
            skLineSegment(sketch, "E2210", {"start": v(11.19, 28.45) * mm, "end": v(11.16, 28.42) * mm});
            skLineSegment(sketch, "E2211", {"start": v(11.16, 28.42) * mm, "end": v(11.12, 28.4) * mm});
            skLineSegment(sketch, "E2212", {"start": v(11.12, 28.4) * mm, "end": v(11.07, 28.37) * mm});
            skLineSegment(sketch, "E2213", {"start": v(11.07, 28.37) * mm, "end": v(11, 28.36) * mm});
            skLineSegment(sketch, "E2214", {"start": v(11, 28.36) * mm, "end": v(10.95, 28.37) * mm});
            skLineSegment(sketch, "E2215", {"start": v(10.95, 28.37) * mm, "end": v(10.9, 28.38) * mm});
            skLineSegment(sketch, "E2216", {"start": v(10.9, 28.38) * mm, "end": v(10.84, 28.4) * mm});
            skLineSegment(sketch, "E2217", {"start": v(10.84, 28.4) * mm, "end": v(10.8, 28.44) * mm});
            skLineSegment(sketch, "E2218", {"start": v(10.8, 28.44) * mm, "end": v(10.76, 28.49) * mm});
            skLineSegment(sketch, "E2219", {"start": v(10.76, 28.49) * mm, "end": v(10.73, 28.54) * mm});
            skLineSegment(sketch, "E2220", {"start": v(10.73, 28.54) * mm, "end": v(10.73, 28.58) * mm});
            skLineSegment(sketch, "E2221", {"start": v(10.73, 28.58) * mm, "end": v(10.72, 28.63) * mm});
            skLineSegment(sketch, "E2222", {"start": v(10.72, 28.63) * mm, "end": v(10.72, 28.67) * mm});
            skLineSegment(sketch, "E2223", {"start": v(10.72, 28.67) * mm, "end": v(10.73, 28.72) * mm});
            skLineSegment(sketch, "E2224", {"start": v(10.73, 28.72) * mm, "end": v(10.72, 28.76) * mm});
            skLineSegment(sketch, "E2225", {"start": v(10.72, 28.76) * mm, "end": v(10.69, 28.8) * mm});
            skLineSegment(sketch, "E2226", {"start": v(10.69, 28.8) * mm, "end": v(10.57, 28.83) * mm});
            skLineSegment(sketch, "E2227", {"start": v(10.57, 28.83) * mm, "end": v(10.53, 28.83) * mm});
            skLineSegment(sketch, "E2228", {"start": v(10.53, 28.83) * mm, "end": v(10.5, 28.8) * mm});
            skLineSegment(sketch, "E2229", {"start": v(10.5, 28.8) * mm, "end": v(10.47, 28.77) * mm});
            skLineSegment(sketch, "E2230", {"start": v(10.47, 28.77) * mm, "end": v(10.44, 28.73) * mm});
            skLineSegment(sketch, "E2231", {"start": v(10.44, 28.73) * mm, "end": v(10.4, 28.7) * mm});
            skLineSegment(sketch, "E2232", {"start": v(10.4, 28.7) * mm, "end": v(10.37, 28.67) * mm});
            skLineSegment(sketch, "E2233", {"start": v(10.37, 28.67) * mm, "end": v(10.32, 28.65) * mm});
            skLineSegment(sketch, "E2234", {"start": v(10.32, 28.65) * mm, "end": v(10.26, 28.64) * mm});
            skLineSegment(sketch, "E2235", {"start": v(10.26, 28.64) * mm, "end": v(10.2, 28.64) * mm});
            skLineSegment(sketch, "E2236", {"start": v(10.2, 28.64) * mm, "end": v(10.15, 28.66) * mm});
            skLineSegment(sketch, "E2237", {"start": v(10.15, 28.66) * mm, "end": v(10.1, 28.68) * mm});
            skLineSegment(sketch, "E2238", {"start": v(10.1, 28.68) * mm, "end": v(10.05, 28.72) * mm});
            skLineSegment(sketch, "E2239", {"start": v(10.05, 28.72) * mm, "end": v(10.01, 28.76) * mm});
            skLineSegment(sketch, "E2240", {"start": v(10.01, 28.76) * mm, "end": v(9.98, 28.81) * mm});
            skLineSegment(sketch, "E2241", {"start": v(9.98, 28.81) * mm, "end": v(9.97, 28.86) * mm});
            skLineSegment(sketch, "E2242", {"start": v(9.97, 28.86) * mm, "end": v(9.97, 28.9) * mm});
            skLineSegment(sketch, "E2243", {"start": v(9.97, 28.9) * mm, "end": v(9.97, 28.94) * mm});
            skLineSegment(sketch, "E2244", {"start": v(9.97, 28.94) * mm, "end": v(9.98, 28.99) * mm});
            skLineSegment(sketch, "E2245", {"start": v(9.98, 28.99) * mm, "end": v(9.97, 29.03) * mm});
            skLineSegment(sketch, "E2246", {"start": v(9.97, 29.03) * mm, "end": v(9.93, 29.06) * mm});
            skLineSegment(sketch, "E2247", {"start": v(9.93, 29.06) * mm, "end": v(9.81, 29.1) * mm});
            skLineSegment(sketch, "E2248", {"start": v(9.81, 29.1) * mm, "end": v(9.77, 29.1) * mm});
            skLineSegment(sketch, "E2249", {"start": v(9.77, 29.1) * mm, "end": v(9.73, 29.07) * mm});
            skLineSegment(sketch, "E2250", {"start": v(9.73, 29.07) * mm, "end": v(9.71, 29.03) * mm});
            skLineSegment(sketch, "E2251", {"start": v(9.71, 29.03) * mm, "end": v(9.68, 29) * mm});
            skLineSegment(sketch, "E2252", {"start": v(9.68, 29) * mm, "end": v(9.65, 28.96) * mm});
            skLineSegment(sketch, "E2253", {"start": v(9.65, 28.96) * mm, "end": v(9.62, 28.93) * mm});
            skLineSegment(sketch, "E2254", {"start": v(9.62, 28.93) * mm, "end": v(9.57, 28.91) * mm});
            skLineSegment(sketch, "E2255", {"start": v(9.57, 28.91) * mm, "end": v(9.5, 28.9) * mm});
            skLineSegment(sketch, "E2256", {"start": v(9.5, 28.9) * mm, "end": v(9.45, 28.9) * mm});
            skLineSegment(sketch, "E2257", {"start": v(9.45, 28.9) * mm, "end": v(9.4, 28.91) * mm});
            skLineSegment(sketch, "E2258", {"start": v(9.4, 28.91) * mm, "end": v(9.34, 28.94) * mm});
            skLineSegment(sketch, "E2259", {"start": v(9.34, 28.94) * mm, "end": v(9.3, 28.97) * mm});
            skLineSegment(sketch, "E2260", {"start": v(9.3, 28.97) * mm, "end": v(9.25, 29.01) * mm});
            skLineSegment(sketch, "E2261", {"start": v(9.25, 29.01) * mm, "end": v(9.23, 29.06) * mm});
            skLineSegment(sketch, "E2262", {"start": v(9.23, 29.06) * mm, "end": v(9.21, 29.1) * mm});
            skLineSegment(sketch, "E2263", {"start": v(9.21, 29.1) * mm, "end": v(9.2, 29.15) * mm});
            skLineSegment(sketch, "E2264", {"start": v(9.2, 29.15) * mm, "end": v(9.2, 29.2) * mm});
            skLineSegment(sketch, "E2265", {"start": v(9.2, 29.2) * mm, "end": v(9.21, 29.24) * mm});
            skLineSegment(sketch, "E2266", {"start": v(9.21, 29.24) * mm, "end": v(9.2, 29.28) * mm});
            skLineSegment(sketch, "E2267", {"start": v(9.2, 29.28) * mm, "end": v(9.16, 29.31) * mm});
            skLineSegment(sketch, "E2268", {"start": v(9.16, 29.31) * mm, "end": v(9.05, 29.35) * mm});
            skLineSegment(sketch, "E2269", {"start": v(9.05, 29.35) * mm, "end": v(9, 29.35) * mm});
            skLineSegment(sketch, "E2270", {"start": v(9, 29.35) * mm, "end": v(8.97, 29.32) * mm});
            skLineSegment(sketch, "E2271", {"start": v(8.97, 29.32) * mm, "end": v(8.95, 29.28) * mm});
            skLineSegment(sketch, "E2272", {"start": v(8.95, 29.28) * mm, "end": v(8.92, 29.24) * mm});
            skLineSegment(sketch, "E2273", {"start": v(8.92, 29.24) * mm, "end": v(8.9, 29.2) * mm});
            skLineSegment(sketch, "E2274", {"start": v(8.9, 29.2) * mm, "end": v(8.86, 29.18) * mm});
            skLineSegment(sketch, "E2275", {"start": v(8.86, 29.18) * mm, "end": v(8.8, 29.15) * mm});
            skLineSegment(sketch, "E2276", {"start": v(8.8, 29.15) * mm, "end": v(8.75, 29.14) * mm});
            skLineSegment(sketch, "E2277", {"start": v(8.75, 29.14) * mm, "end": v(8.7, 29.14) * mm});
            skLineSegment(sketch, "E2278", {"start": v(8.7, 29.14) * mm, "end": v(8.63, 29.15) * mm});
            skLineSegment(sketch, "E2279", {"start": v(8.63, 29.15) * mm, "end": v(8.58, 29.17) * mm});
            skLineSegment(sketch, "E2280", {"start": v(8.58, 29.17) * mm, "end": v(8.53, 29.2) * mm});
            skLineSegment(sketch, "E2281", {"start": v(8.53, 29.2) * mm, "end": v(8.5, 29.24) * mm});
            skLineSegment(sketch, "E2282", {"start": v(8.5, 29.24) * mm, "end": v(8.46, 29.3) * mm});
            skLineSegment(sketch, "E2283", {"start": v(8.46, 29.3) * mm, "end": v(8.45, 29.34) * mm});
            skLineSegment(sketch, "E2284", {"start": v(8.45, 29.34) * mm, "end": v(8.44, 29.38) * mm});
            skLineSegment(sketch, "E2285", {"start": v(8.44, 29.38) * mm, "end": v(8.44, 29.43) * mm});
            skLineSegment(sketch, "E2286", {"start": v(8.44, 29.43) * mm, "end": v(8.44, 29.47) * mm});
            skLineSegment(sketch, "E2287", {"start": v(8.44, 29.47) * mm, "end": v(8.43, 29.51) * mm});
            skLineSegment(sketch, "E2288", {"start": v(8.43, 29.51) * mm, "end": v(8.4, 29.54) * mm});
            skLineSegment(sketch, "E2289", {"start": v(8.4, 29.54) * mm, "end": v(8.28, 29.57) * mm});
            skLineSegment(sketch, "E2290", {"start": v(8.28, 29.57) * mm, "end": v(8.23, 29.57) * mm});
            skLineSegment(sketch, "E2291", {"start": v(8.23, 29.57) * mm, "end": v(8.2, 29.54) * mm});
            skLineSegment(sketch, "E2292", {"start": v(8.2, 29.54) * mm, "end": v(8.18, 29.5) * mm});
            skLineSegment(sketch, "E2293", {"start": v(8.18, 29.5) * mm, "end": v(8.15, 29.46) * mm});
            skLineSegment(sketch, "E2294", {"start": v(8.15, 29.46) * mm, "end": v(8.12, 29.43) * mm});
            skLineSegment(sketch, "E2295", {"start": v(8.12, 29.43) * mm, "end": v(8.1, 29.4) * mm});
            skLineSegment(sketch, "E2296", {"start": v(8.1, 29.4) * mm, "end": v(8.04, 29.37) * mm});
            skLineSegment(sketch, "E2297", {"start": v(8.04, 29.37) * mm, "end": v(7.98, 29.36) * mm});
            skLineSegment(sketch, "E2298", {"start": v(7.98, 29.36) * mm, "end": v(7.93, 29.35) * mm});
            skLineSegment(sketch, "E2299", {"start": v(7.93, 29.35) * mm, "end": v(7.87, 29.36) * mm});
            skLineSegment(sketch, "E2300", {"start": v(7.87, 29.36) * mm, "end": v(7.81, 29.39) * mm});
            skLineSegment(sketch, "E2301", {"start": v(7.81, 29.39) * mm, "end": v(7.76, 29.42) * mm});
            skLineSegment(sketch, "E2302", {"start": v(7.76, 29.42) * mm, "end": v(7.72, 29.46) * mm});
            skLineSegment(sketch, "E2303", {"start": v(7.72, 29.46) * mm, "end": v(7.7, 29.5) * mm});
            skLineSegment(sketch, "E2304", {"start": v(7.7, 29.5) * mm, "end": v(7.68, 29.55) * mm});
            skLineSegment(sketch, "E2305", {"start": v(7.68, 29.55) * mm, "end": v(7.67, 29.6) * mm});
            skLineSegment(sketch, "E2306", {"start": v(7.67, 29.6) * mm, "end": v(7.67, 29.64) * mm});
            skLineSegment(sketch, "E2307", {"start": v(7.67, 29.64) * mm, "end": v(7.67, 29.68) * mm});
            skLineSegment(sketch, "E2308", {"start": v(7.67, 29.68) * mm, "end": v(7.66, 29.72) * mm});
            skLineSegment(sketch, "E2309", {"start": v(7.66, 29.72) * mm, "end": v(7.62, 29.75) * mm});
            skLineSegment(sketch, "E2310", {"start": v(7.62, 29.75) * mm, "end": v(7.5, 29.78) * mm});
            skLineSegment(sketch, "E2311", {"start": v(7.5, 29.78) * mm, "end": v(7.45, 29.78) * mm});
            skLineSegment(sketch, "E2312", {"start": v(7.45, 29.78) * mm, "end": v(7.42, 29.75) * mm});
            skLineSegment(sketch, "E2313", {"start": v(7.42, 29.75) * mm, "end": v(7.4, 29.7) * mm});
            skLineSegment(sketch, "E2314", {"start": v(7.4, 29.7) * mm, "end": v(7.38, 29.67) * mm});
            skLineSegment(sketch, "E2315", {"start": v(7.38, 29.67) * mm, "end": v(7.35, 29.63) * mm});
            skLineSegment(sketch, "E2316", {"start": v(7.35, 29.63) * mm, "end": v(7.32, 29.6) * mm});
            skLineSegment(sketch, "E2317", {"start": v(7.32, 29.6) * mm, "end": v(7.27, 29.57) * mm});
            skLineSegment(sketch, "E2318", {"start": v(7.27, 29.57) * mm, "end": v(7.21, 29.56) * mm});
            skLineSegment(sketch, "E2319", {"start": v(7.21, 29.56) * mm, "end": v(7.15, 29.55) * mm});
            skLineSegment(sketch, "E2320", {"start": v(7.15, 29.55) * mm, "end": v(7.1, 29.56) * mm});
            skLineSegment(sketch, "E2321", {"start": v(7.1, 29.56) * mm, "end": v(7.04, 29.58) * mm});
            skLineSegment(sketch, "E2322", {"start": v(7.04, 29.58) * mm, "end": v(7, 29.6) * mm});
            skLineSegment(sketch, "E2323", {"start": v(7, 29.6) * mm, "end": v(6.95, 29.65) * mm});
            skLineSegment(sketch, "E2324", {"start": v(6.95, 29.65) * mm, "end": v(6.92, 29.7) * mm});
            skLineSegment(sketch, "E2325", {"start": v(6.92, 29.7) * mm, "end": v(6.9, 29.74) * mm});
            skLineSegment(sketch, "E2326", {"start": v(6.9, 29.74) * mm, "end": v(6.9, 29.78) * mm});
            skLineSegment(sketch, "E2327", {"start": v(6.9, 29.78) * mm, "end": v(6.89, 29.83) * mm});
            skLineSegment(sketch, "E2328", {"start": v(6.89, 29.83) * mm, "end": v(6.9, 29.87) * mm});
            skLineSegment(sketch, "E2329", {"start": v(6.9, 29.87) * mm, "end": v(6.88, 29.91) * mm});
            skLineSegment(sketch, "E2330", {"start": v(6.88, 29.91) * mm, "end": v(6.84, 29.94) * mm});
            skLineSegment(sketch, "E2331", {"start": v(6.84, 29.94) * mm, "end": v(6.72, 29.97) * mm});
            skLineSegment(sketch, "E2332", {"start": v(6.72, 29.97) * mm, "end": v(6.67, 29.96) * mm});
            skLineSegment(sketch, "E2333", {"start": v(6.67, 29.96) * mm, "end": v(6.64, 29.93) * mm});
            skLineSegment(sketch, "E2334", {"start": v(6.64, 29.93) * mm, "end": v(6.62, 29.89) * mm});
            skLineSegment(sketch, "E2335", {"start": v(6.62, 29.89) * mm, "end": v(6.6, 29.85) * mm});
            skLineSegment(sketch, "E2336", {"start": v(6.6, 29.85) * mm, "end": v(6.57, 29.81) * mm});
            skLineSegment(sketch, "E2337", {"start": v(6.57, 29.81) * mm, "end": v(6.54, 29.78) * mm});
            skLineSegment(sketch, "E2338", {"start": v(6.54, 29.78) * mm, "end": v(6.5, 29.75) * mm});
            skLineSegment(sketch, "E2339", {"start": v(6.5, 29.75) * mm, "end": v(6.44, 29.73) * mm});
            skLineSegment(sketch, "E2340", {"start": v(6.44, 29.73) * mm, "end": v(6.38, 29.73) * mm});
            skLineSegment(sketch, "E2341", {"start": v(6.38, 29.73) * mm, "end": v(6.32, 29.74) * mm});
            skLineSegment(sketch, "E2342", {"start": v(6.32, 29.74) * mm, "end": v(6.26, 29.75) * mm});
            skLineSegment(sketch, "E2343", {"start": v(6.26, 29.75) * mm, "end": v(6.21, 29.78) * mm});
            skLineSegment(sketch, "E2344", {"start": v(6.21, 29.78) * mm, "end": v(6.17, 29.82) * mm});
            skLineSegment(sketch, "E2345", {"start": v(6.17, 29.82) * mm, "end": v(6.14, 29.87) * mm});
            skLineSegment(sketch, "E2346", {"start": v(6.14, 29.87) * mm, "end": v(6.12, 29.91) * mm});
            skLineSegment(sketch, "E2347", {"start": v(6.12, 29.91) * mm, "end": v(6.11, 29.95) * mm});
            skLineSegment(sketch, "E2348", {"start": v(6.11, 29.95) * mm, "end": v(6.1, 30) * mm});
            skLineSegment(sketch, "E2349", {"start": v(6.1, 30) * mm, "end": v(6.1, 30.04) * mm});
            skLineSegment(sketch, "E2350", {"start": v(6.1, 30.04) * mm, "end": v(6.1, 30.08) * mm});
            skLineSegment(sketch, "E2351", {"start": v(6.1, 30.08) * mm, "end": v(6.05, 30.1) * mm});
            skLineSegment(sketch, "E2352", {"start": v(6.05, 30.1) * mm, "end": v(5.93, 30.13) * mm});
            skLineSegment(sketch, "E2353", {"start": v(5.93, 30.13) * mm, "end": v(5.88, 30.13) * mm});
            skLineSegment(sketch, "E2354", {"start": v(5.88, 30.13) * mm, "end": v(5.86, 30.1) * mm});
            skLineSegment(sketch, "E2355", {"start": v(5.86, 30.1) * mm, "end": v(5.84, 30.05) * mm});
            skLineSegment(sketch, "E2356", {"start": v(5.84, 30.05) * mm, "end": v(5.82, 30.01) * mm});
            skLineSegment(sketch, "E2357", {"start": v(5.82, 30.01) * mm, "end": v(5.8, 29.98) * mm});
            skLineSegment(sketch, "E2358", {"start": v(5.8, 29.98) * mm, "end": v(5.76, 29.94) * mm});
            skLineSegment(sketch, "E2359", {"start": v(5.76, 29.94) * mm, "end": v(5.71, 29.91) * mm});
            skLineSegment(sketch, "E2360", {"start": v(5.71, 29.91) * mm, "end": v(5.66, 29.9) * mm});
            skLineSegment(sketch, "E2361", {"start": v(5.66, 29.9) * mm, "end": v(5.6, 29.89) * mm});
            skLineSegment(sketch, "E2362", {"start": v(5.6, 29.89) * mm, "end": v(5.54, 29.9) * mm});
            skLineSegment(sketch, "E2363", {"start": v(5.54, 29.9) * mm, "end": v(5.48, 29.9) * mm});
            skLineSegment(sketch, "E2364", {"start": v(5.48, 29.9) * mm, "end": v(5.43, 29.93) * mm});
            skLineSegment(sketch, "E2365", {"start": v(5.43, 29.93) * mm, "end": v(5.39, 29.97) * mm});
            skLineSegment(sketch, "E2366", {"start": v(5.39, 29.97) * mm, "end": v(5.35, 30.02) * mm});
            skLineSegment(sketch, "E2367", {"start": v(5.35, 30.02) * mm, "end": v(5.34, 30.06) * mm});
            skLineSegment(sketch, "E2368", {"start": v(5.34, 30.06) * mm, "end": v(5.32, 30.1) * mm});
            skLineSegment(sketch, "E2369", {"start": v(5.32, 30.1) * mm, "end": v(5.32, 30.15) * mm});
            skLineSegment(sketch, "E2370", {"start": v(5.32, 30.15) * mm, "end": v(5.32, 30.2) * mm});
            skLineSegment(sketch, "E2371", {"start": v(5.32, 30.2) * mm, "end": v(5.3, 30.23) * mm});
            skLineSegment(sketch, "E2372", {"start": v(5.3, 30.23) * mm, "end": v(5.26, 30.26) * mm});
            skLineSegment(sketch, "E2373", {"start": v(5.26, 30.26) * mm, "end": v(5.14, 30.28) * mm});
            skLineSegment(sketch, "E2374", {"start": v(5.14, 30.28) * mm, "end": v(5.1, 30.27) * mm});
            skLineSegment(sketch, "E2375", {"start": v(5.1, 30.27) * mm, "end": v(5.07, 30.24) * mm});
            skLineSegment(sketch, "E2376", {"start": v(5.07, 30.24) * mm, "end": v(5.05, 30.2) * mm});
            skLineSegment(sketch, "E2377", {"start": v(5.05, 30.2) * mm, "end": v(5.03, 30.15) * mm});
            skLineSegment(sketch, "E2378", {"start": v(5.03, 30.15) * mm, "end": v(5, 30.12) * mm});
            skLineSegment(sketch, "E2379", {"start": v(5, 30.12) * mm, "end": v(4.97, 30.08) * mm});
            skLineSegment(sketch, "E2380", {"start": v(4.97, 30.08) * mm, "end": v(4.93, 30.05) * mm});
            skLineSegment(sketch, "E2381", {"start": v(4.93, 30.05) * mm, "end": v(4.87, 30.03) * mm});
            skLineSegment(sketch, "E2382", {"start": v(4.87, 30.03) * mm, "end": v(4.81, 30.02) * mm});
            skLineSegment(sketch, "E2383", {"start": v(4.81, 30.02) * mm, "end": v(4.76, 30.03) * mm});
            skLineSegment(sketch, "E2384", {"start": v(4.76, 30.03) * mm, "end": v(4.7, 30.04) * mm});
            skLineSegment(sketch, "E2385", {"start": v(4.7, 30.04) * mm, "end": v(4.65, 30.07) * mm});
            skLineSegment(sketch, "E2386", {"start": v(4.65, 30.07) * mm, "end": v(4.6, 30.1) * mm});
            skLineSegment(sketch, "E2387", {"start": v(4.6, 30.1) * mm, "end": v(4.57, 30.15) * mm});
            skLineSegment(sketch, "E2388", {"start": v(4.57, 30.15) * mm, "end": v(4.55, 30.19) * mm});
            skLineSegment(sketch, "E2389", {"start": v(4.55, 30.19) * mm, "end": v(4.54, 30.23) * mm});
            skLineSegment(sketch, "E2390", {"start": v(4.54, 30.23) * mm, "end": v(4.53, 30.28) * mm});
            skLineSegment(sketch, "E2391", {"start": v(4.53, 30.28) * mm, "end": v(4.53, 30.32) * mm});
            skLineSegment(sketch, "E2392", {"start": v(4.53, 30.32) * mm, "end": v(4.5, 30.36) * mm});
            skLineSegment(sketch, "E2393", {"start": v(4.5, 30.36) * mm, "end": v(4.47, 30.38) * mm});
            skLineSegment(sketch, "E2394", {"start": v(4.47, 30.38) * mm, "end": v(4.35, 30.4) * mm});
            skLineSegment(sketch, "E2395", {"start": v(4.35, 30.4) * mm, "end": v(4.3, 30.4) * mm});
            skLineSegment(sketch, "E2396", {"start": v(4.3, 30.4) * mm, "end": v(4.27, 30.36) * mm});
            skLineSegment(sketch, "E2397", {"start": v(4.27, 30.36) * mm, "end": v(4.26, 30.32) * mm});
            skLineSegment(sketch, "E2398", {"start": v(4.26, 30.32) * mm, "end": v(4.24, 30.28) * mm});
            skLineSegment(sketch, "E2399", {"start": v(4.24, 30.28) * mm, "end": v(4.21, 30.24) * mm});
            skLineSegment(sketch, "E2400", {"start": v(4.21, 30.24) * mm, "end": v(4.18, 30.2) * mm});
            skLineSegment(sketch, "E2401", {"start": v(4.18, 30.2) * mm, "end": v(4.14, 30.17) * mm});
            skLineSegment(sketch, "E2402", {"start": v(4.14, 30.17) * mm, "end": v(4.08, 30.15) * mm});
            skLineSegment(sketch, "E2403", {"start": v(4.08, 30.15) * mm, "end": v(4.03, 30.14) * mm});
            skLineSegment(sketch, "E2404", {"start": v(4.03, 30.14) * mm, "end": v(3.97, 30.14) * mm});
            skLineSegment(sketch, "E2405", {"start": v(3.97, 30.14) * mm, "end": v(3.91, 30.15) * mm});
            skLineSegment(sketch, "E2406", {"start": v(3.91, 30.15) * mm, "end": v(3.86, 30.18) * mm});
            skLineSegment(sketch, "E2407", {"start": v(3.86, 30.18) * mm, "end": v(3.81, 30.21) * mm});
            skLineSegment(sketch, "E2408", {"start": v(3.81, 30.21) * mm, "end": v(3.78, 30.26) * mm});
            skLineSegment(sketch, "E2409", {"start": v(3.78, 30.26) * mm, "end": v(3.76, 30.3) * mm});
            skLineSegment(sketch, "E2410", {"start": v(3.76, 30.3) * mm, "end": v(3.74, 30.34) * mm});
            skLineSegment(sketch, "E2411", {"start": v(3.74, 30.34) * mm, "end": v(3.73, 30.39) * mm});
            skLineSegment(sketch, "E2412", {"start": v(3.73, 30.39) * mm, "end": v(3.73, 30.43) * mm});
            skLineSegment(sketch, "E2413", {"start": v(3.73, 30.43) * mm, "end": v(3.71, 30.47) * mm});
            skLineSegment(sketch, "E2414", {"start": v(3.71, 30.47) * mm, "end": v(3.67, 30.5) * mm});
            skLineSegment(sketch, "E2415", {"start": v(3.67, 30.5) * mm, "end": v(3.55, 30.5) * mm});
            skLineSegment(sketch, "E2416", {"start": v(3.55, 30.5) * mm, "end": v(3.5, 30.5) * mm});
            skLineSegment(sketch, "E2417", {"start": v(3.5, 30.5) * mm, "end": v(3.48, 30.46) * mm});
            skLineSegment(sketch, "E2418", {"start": v(3.48, 30.46) * mm, "end": v(3.46, 30.42) * mm});
            skLineSegment(sketch, "E2419", {"start": v(3.46, 30.42) * mm, "end": v(3.44, 30.38) * mm});
            skLineSegment(sketch, "E2420", {"start": v(3.44, 30.38) * mm, "end": v(3.42, 30.34) * mm});
            skLineSegment(sketch, "E2421", {"start": v(3.42, 30.34) * mm, "end": v(3.4, 30.3) * mm});
            skLineSegment(sketch, "E2422", {"start": v(3.4, 30.3) * mm, "end": v(3.35, 30.27) * mm});
            skLineSegment(sketch, "E2423", {"start": v(3.35, 30.27) * mm, "end": v(3.3, 30.24) * mm});
            skLineSegment(sketch, "E2424", {"start": v(3.3, 30.24) * mm, "end": v(3.24, 30.23) * mm});
            skLineSegment(sketch, "E2425", {"start": v(3.24, 30.23) * mm, "end": v(3.18, 30.23) * mm});
            skLineSegment(sketch, "E2426", {"start": v(3.18, 30.23) * mm, "end": v(3.12, 30.25) * mm});
            skLineSegment(sketch, "E2427", {"start": v(3.12, 30.25) * mm, "end": v(3.07, 30.27) * mm});
            skLineSegment(sketch, "E2428", {"start": v(3.07, 30.27) * mm, "end": v(3.02, 30.3) * mm});
            skLineSegment(sketch, "E2429", {"start": v(3.02, 30.3) * mm, "end": v(2.98, 30.35) * mm});
            skLineSegment(sketch, "E2430", {"start": v(2.98, 30.35) * mm, "end": v(2.96, 30.39) * mm});
            skLineSegment(sketch, "E2431", {"start": v(2.96, 30.39) * mm, "end": v(2.95, 30.43) * mm});
            skLineSegment(sketch, "E2432", {"start": v(2.95, 30.43) * mm, "end": v(2.94, 30.47) * mm});
            skLineSegment(sketch, "E2433", {"start": v(2.94, 30.47) * mm, "end": v(2.93, 30.52) * mm});
            skLineSegment(sketch, "E2434", {"start": v(2.93, 30.52) * mm, "end": v(2.91, 30.56) * mm});
            skLineSegment(sketch, "E2435", {"start": v(2.91, 30.56) * mm, "end": v(2.87, 30.58) * mm});
            skLineSegment(sketch, "E2436", {"start": v(2.87, 30.58) * mm, "end": v(2.75, 30.59) * mm});
            skLineSegment(sketch, "E2437", {"start": v(2.75, 30.59) * mm, "end": v(2.7, 30.58) * mm});
            skLineSegment(sketch, "E2438", {"start": v(2.7, 30.58) * mm, "end": v(2.68, 30.54) * mm});
            skLineSegment(sketch, "E2439", {"start": v(2.68, 30.54) * mm, "end": v(2.67, 30.5) * mm});
            skLineSegment(sketch, "E2440", {"start": v(2.67, 30.5) * mm, "end": v(2.65, 30.46) * mm});
            skLineSegment(sketch, "E2441", {"start": v(2.65, 30.46) * mm, "end": v(2.63, 30.42) * mm});
            skLineSegment(sketch, "E2442", {"start": v(2.63, 30.42) * mm, "end": v(2.6, 30.38) * mm});
            skLineSegment(sketch, "E2443", {"start": v(2.6, 30.38) * mm, "end": v(2.55, 30.34) * mm});
            skLineSegment(sketch, "E2444", {"start": v(2.55, 30.34) * mm, "end": v(2.5, 30.32) * mm});
            skLineSegment(sketch, "E2445", {"start": v(2.5, 30.32) * mm, "end": v(2.44, 30.3) * mm});
            skLineSegment(sketch, "E2446", {"start": v(2.44, 30.3) * mm, "end": v(2.39, 30.3) * mm});
            skLineSegment(sketch, "E2447", {"start": v(2.39, 30.3) * mm, "end": v(2.33, 30.32) * mm});
            skLineSegment(sketch, "E2448", {"start": v(2.33, 30.32) * mm, "end": v(2.27, 30.34) * mm});
            skLineSegment(sketch, "E2449", {"start": v(2.27, 30.34) * mm, "end": v(2.23, 30.37) * mm});
            skLineSegment(sketch, "E2450", {"start": v(2.23, 30.37) * mm, "end": v(2.19, 30.41) * mm});
            skLineSegment(sketch, "E2451", {"start": v(2.19, 30.41) * mm, "end": v(2.17, 30.45) * mm});
            skLineSegment(sketch, "E2452", {"start": v(2.17, 30.45) * mm, "end": v(2.15, 30.5) * mm});
            skLineSegment(sketch, "E2453", {"start": v(2.15, 30.5) * mm, "end": v(2.14, 30.54) * mm});
            skLineSegment(sketch, "E2454", {"start": v(2.14, 30.54) * mm, "end": v(2.13, 30.58) * mm});
            skLineSegment(sketch, "E2455", {"start": v(2.13, 30.58) * mm, "end": v(2.11, 30.62) * mm});
            skLineSegment(sketch, "E2456", {"start": v(2.11, 30.62) * mm, "end": v(2.07, 30.64) * mm});
            skLineSegment(sketch, "E2457", {"start": v(2.07, 30.64) * mm, "end": v(1.95, 30.65) * mm});
            skLineSegment(sketch, "E2458", {"start": v(1.95, 30.65) * mm, "end": v(1.9, 30.64) * mm});
            skLineSegment(sketch, "E2459", {"start": v(1.9, 30.64) * mm, "end": v(1.88, 30.6) * mm});
            skLineSegment(sketch, "E2460", {"start": v(1.88, 30.6) * mm, "end": v(1.87, 30.56) * mm});
            skLineSegment(sketch, "E2461", {"start": v(1.87, 30.56) * mm, "end": v(1.85, 30.52) * mm});
            skLineSegment(sketch, "E2462", {"start": v(1.85, 30.52) * mm, "end": v(1.83, 30.48) * mm});
            skLineSegment(sketch, "E2463", {"start": v(1.83, 30.48) * mm, "end": v(1.8, 30.44) * mm});
            skLineSegment(sketch, "E2464", {"start": v(1.8, 30.44) * mm, "end": v(1.76, 30.4) * mm});
            skLineSegment(sketch, "E2465", {"start": v(1.76, 30.4) * mm, "end": v(1.7, 30.38) * mm});
            skLineSegment(sketch, "E2466", {"start": v(1.7, 30.38) * mm, "end": v(1.65, 30.36) * mm});
            skLineSegment(sketch, "E2467", {"start": v(1.65, 30.36) * mm, "end": v(1.6, 30.36) * mm});
            skLineSegment(sketch, "E2468", {"start": v(1.6, 30.36) * mm, "end": v(1.53, 30.37) * mm});
            skLineSegment(sketch, "E2469", {"start": v(1.53, 30.37) * mm, "end": v(1.48, 30.39) * mm});
            skLineSegment(sketch, "E2470", {"start": v(1.48, 30.39) * mm, "end": v(1.43, 30.42) * mm});
            skLineSegment(sketch, "E2471", {"start": v(1.43, 30.42) * mm, "end": v(1.39, 30.46) * mm});
            skLineSegment(sketch, "E2472", {"start": v(1.39, 30.46) * mm, "end": v(1.37, 30.5) * mm});
            skLineSegment(sketch, "E2473", {"start": v(1.37, 30.5) * mm, "end": v(1.35, 30.54) * mm});
            skLineSegment(sketch, "E2474", {"start": v(1.35, 30.54) * mm, "end": v(1.34, 30.58) * mm});
            skLineSegment(sketch, "E2475", {"start": v(1.34, 30.58) * mm, "end": v(1.33, 30.63) * mm});
            skLineSegment(sketch, "E2476", {"start": v(1.33, 30.63) * mm, "end": v(1.31, 30.67) * mm});
            skLineSegment(sketch, "E2477", {"start": v(1.31, 30.67) * mm, "end": v(1.27, 30.68) * mm});
            skLineSegment(sketch, "E2478", {"start": v(1.27, 30.68) * mm, "end": v(1.15, 30.69) * mm});
            skLineSegment(sketch, "E2479", {"start": v(1.15, 30.69) * mm, "end": v(1.1, 30.68) * mm});
            skLineSegment(sketch, "E2480", {"start": v(1.1, 30.68) * mm, "end": v(1.08, 30.64) * mm});
            skLineSegment(sketch, "E2481", {"start": v(1.08, 30.64) * mm, "end": v(1.07, 30.6) * mm});
            skLineSegment(sketch, "E2482", {"start": v(1.07, 30.6) * mm, "end": v(1.05, 30.55) * mm});
            skLineSegment(sketch, "E2483", {"start": v(1.05, 30.55) * mm, "end": v(1.03, 30.51) * mm});
            skLineSegment(sketch, "E2484", {"start": v(1.03, 30.51) * mm, "end": v(1, 30.48) * mm});
            skLineSegment(sketch, "E2485", {"start": v(1, 30.48) * mm, "end": v(0.96, 30.44) * mm});
            skLineSegment(sketch, "E2486", {"start": v(0.96, 30.44) * mm, "end": v(0.9, 30.4) * mm});
            skLineSegment(sketch, "E2487", {"start": v(0.9, 30.4) * mm, "end": v(0.85, 30.4) * mm});
            skLineSegment(sketch, "E2488", {"start": v(0.85, 30.4) * mm, "end": v(0.8, 30.39) * mm});
            skLineSegment(sketch, "E2489", {"start": v(0.8, 30.39) * mm, "end": v(0.74, 30.4) * mm});
            skLineSegment(sketch, "E2490", {"start": v(0.74, 30.4) * mm, "end": v(0.68, 30.42) * mm});
            skLineSegment(sketch, "E2491", {"start": v(0.68, 30.42) * mm, "end": v(0.63, 30.45) * mm});
            skLineSegment(sketch, "E2492", {"start": v(0.63, 30.45) * mm, "end": v(0.6, 30.49) * mm});
            skLineSegment(sketch, "E2493", {"start": v(0.6, 30.49) * mm, "end": v(0.57, 30.53) * mm});
            skLineSegment(sketch, "E2494", {"start": v(0.57, 30.53) * mm, "end": v(0.55, 30.57) * mm});
            skLineSegment(sketch, "E2495", {"start": v(0.55, 30.57) * mm, "end": v(0.54, 30.6) * mm});
            skLineSegment(sketch, "E2496", {"start": v(0.54, 30.6) * mm, "end": v(0.53, 30.65) * mm});
            skLineSegment(sketch, "E2497", {"start": v(0.53, 30.65) * mm, "end": v(0.5, 30.7) * mm});
            skLineSegment(sketch, "E2498", {"start": v(0.5, 30.7) * mm, "end": v(0.46, 30.7) * mm});
            skLineSegment(sketch, "E2499", {"start": v(0.46, 30.7) * mm, "end": v(0.34, 30.7) * mm});
            skLineSegment(sketch, "E2500", {"start": v(0.34, 30.7) * mm, "end": v(0.3, 30.7) * mm});
            skLineSegment(sketch, "E2501", {"start": v(0.3, 30.7) * mm, "end": v(0.27, 30.66) * mm});
            skLineSegment(sketch, "E2502", {"start": v(0.27, 30.66) * mm, "end": v(0.26, 30.61) * mm});
            skLineSegment(sketch, "E2503", {"start": v(0.26, 30.61) * mm, "end": v(0.25, 30.57) * mm});
            skLineSegment(sketch, "E2504", {"start": v(0.25, 30.57) * mm, "end": v(0.23, 30.53) * mm});
            skLineSegment(sketch, "E2505", {"start": v(0.23, 30.53) * mm, "end": v(0.2, 30.5) * mm});
            skLineSegment(sketch, "E2506", {"start": v(0.2, 30.5) * mm, "end": v(0.16, 30.45) * mm});
            skLineSegment(sketch, "E2507", {"start": v(0.16, 30.45) * mm, "end": v(0.11, 30.42) * mm});
            skLineSegment(sketch, "E2508", {"start": v(0.11, 30.42) * mm, "end": v(0.06, 30.4) * mm});
            skLineSegment(sketch, "E2509", {"start": v(0.06, 30.4) * mm, "end": v(0, 30.4) * mm});
            skLineSegment(sketch, "E2510", {"start": v(0, 30.4) * mm, "end": v(-0.06, 30.4) * mm});
            skLineSegment(sketch, "E2511", {"start": v(-0.06, 30.4) * mm, "end": v(-0.11, 30.42) * mm});
            skLineSegment(sketch, "E2512", {"start": v(-0.11, 30.42) * mm, "end": v(-0.16, 30.45) * mm});
            skLineSegment(sketch, "E2513", {"start": v(-0.16, 30.45) * mm, "end": v(-0.2, 30.5) * mm});
            skLineSegment(sketch, "E2514", {"start": v(-0.2, 30.5) * mm, "end": v(-0.23, 30.53) * mm});
            skLineSegment(sketch, "E2515", {"start": v(-0.23, 30.53) * mm, "end": v(-0.25, 30.57) * mm});
            skLineSegment(sketch, "E2516", {"start": v(-0.25, 30.57) * mm, "end": v(-0.26, 30.61) * mm});
            skLineSegment(sketch, "E2517", {"start": v(-0.26, 30.61) * mm, "end": v(-0.27, 30.66) * mm});
            skLineSegment(sketch, "E2518", {"start": v(-0.27, 30.66) * mm, "end": v(-0.3, 30.7) * mm});
            skLineSegment(sketch, "E2519", {"start": v(-0.3, 30.7) * mm, "end": v(-0.34, 30.7) * mm});
            skLineSegment(sketch, "E2520", {"start": v(-0.34, 30.7) * mm, "end": v(-0.46, 30.7) * mm});
            skLineSegment(sketch, "E2521", {"start": v(-0.46, 30.7) * mm, "end": v(-0.5, 30.7) * mm});
            skLineSegment(sketch, "E2522", {"start": v(-0.5, 30.7) * mm, "end": v(-0.53, 30.65) * mm});
            skLineSegment(sketch, "E2523", {"start": v(-0.53, 30.65) * mm, "end": v(-0.54, 30.6) * mm});
            skLineSegment(sketch, "E2524", {"start": v(-0.54, 30.6) * mm, "end": v(-0.55, 30.57) * mm});
            skLineSegment(sketch, "E2525", {"start": v(-0.55, 30.57) * mm, "end": v(-0.57, 30.53) * mm});
            skLineSegment(sketch, "E2526", {"start": v(-0.57, 30.53) * mm, "end": v(-0.6, 30.49) * mm});
            skLineSegment(sketch, "E2527", {"start": v(-0.6, 30.49) * mm, "end": v(-0.63, 30.45) * mm});
            skLineSegment(sketch, "E2528", {"start": v(-0.63, 30.45) * mm, "end": v(-0.68, 30.42) * mm});
            skLineSegment(sketch, "E2529", {"start": v(-0.68, 30.42) * mm, "end": v(-0.74, 30.4) * mm});
            skLineSegment(sketch, "E2530", {"start": v(-0.74, 30.4) * mm, "end": v(-0.8, 30.39) * mm});
            skLineSegment(sketch, "E2531", {"start": v(-0.8, 30.39) * mm, "end": v(-0.85, 30.4) * mm});
            skLineSegment(sketch, "E2532", {"start": v(-0.85, 30.4) * mm, "end": v(-0.9, 30.4) * mm});
            skLineSegment(sketch, "E2533", {"start": v(-0.9, 30.4) * mm, "end": v(-0.96, 30.44) * mm});
            skLineSegment(sketch, "E2534", {"start": v(-0.96, 30.44) * mm, "end": v(-1, 30.48) * mm});
            skLineSegment(sketch, "E2535", {"start": v(-1, 30.48) * mm, "end": v(-1.03, 30.51) * mm});
            skLineSegment(sketch, "E2536", {"start": v(-1.03, 30.51) * mm, "end": v(-1.05, 30.55) * mm});
            skLineSegment(sketch, "E2537", {"start": v(-1.05, 30.55) * mm, "end": v(-1.07, 30.6) * mm});
            skLineSegment(sketch, "E2538", {"start": v(-1.07, 30.6) * mm, "end": v(-1.08, 30.64) * mm});
            skLineSegment(sketch, "E2539", {"start": v(-1.08, 30.64) * mm, "end": v(-1.1, 30.68) * mm});
            skLineSegment(sketch, "E2540", {"start": v(-1.1, 30.68) * mm, "end": v(-1.15, 30.69) * mm});
            skLineSegment(sketch, "E2541", {"start": v(-1.15, 30.69) * mm, "end": v(-1.27, 30.68) * mm});
            skLineSegment(sketch, "E2542", {"start": v(-1.27, 30.68) * mm, "end": v(-1.31, 30.67) * mm});
            skLineSegment(sketch, "E2543", {"start": v(-1.31, 30.67) * mm, "end": v(-1.33, 30.63) * mm});
            skLineSegment(sketch, "E2544", {"start": v(-1.33, 30.63) * mm, "end": v(-1.34, 30.58) * mm});
            skLineSegment(sketch, "E2545", {"start": v(-1.34, 30.58) * mm, "end": v(-1.35, 30.54) * mm});
            skLineSegment(sketch, "E2546", {"start": v(-1.35, 30.54) * mm, "end": v(-1.37, 30.5) * mm});
            skLineSegment(sketch, "E2547", {"start": v(-1.37, 30.5) * mm, "end": v(-1.39, 30.46) * mm});
            skLineSegment(sketch, "E2548", {"start": v(-1.39, 30.46) * mm, "end": v(-1.43, 30.42) * mm});
            skLineSegment(sketch, "E2549", {"start": v(-1.43, 30.42) * mm, "end": v(-1.48, 30.39) * mm});
            skLineSegment(sketch, "E2550", {"start": v(-1.48, 30.39) * mm, "end": v(-1.53, 30.37) * mm});
            skLineSegment(sketch, "E2551", {"start": v(-1.53, 30.37) * mm, "end": v(-1.6, 30.36) * mm});
            skLineSegment(sketch, "E2552", {"start": v(-1.6, 30.36) * mm, "end": v(-1.65, 30.36) * mm});
            skLineSegment(sketch, "E2553", {"start": v(-1.65, 30.36) * mm, "end": v(-1.7, 30.38) * mm});
            skLineSegment(sketch, "E2554", {"start": v(-1.7, 30.38) * mm, "end": v(-1.76, 30.4) * mm});
            skLineSegment(sketch, "E2555", {"start": v(-1.76, 30.4) * mm, "end": v(-1.8, 30.44) * mm});
            skLineSegment(sketch, "E2556", {"start": v(-1.8, 30.44) * mm, "end": v(-1.83, 30.48) * mm});
            skLineSegment(sketch, "E2557", {"start": v(-1.83, 30.48) * mm, "end": v(-1.85, 30.52) * mm});
            skLineSegment(sketch, "E2558", {"start": v(-1.85, 30.52) * mm, "end": v(-1.87, 30.56) * mm});
            skLineSegment(sketch, "E2559", {"start": v(-1.87, 30.56) * mm, "end": v(-1.88, 30.6) * mm});
            skLineSegment(sketch, "E2560", {"start": v(-1.88, 30.6) * mm, "end": v(-1.9, 30.64) * mm});
            skLineSegment(sketch, "E2561", {"start": v(-1.9, 30.64) * mm, "end": v(-1.95, 30.65) * mm});
            skLineSegment(sketch, "E2562", {"start": v(-1.95, 30.65) * mm, "end": v(-2.07, 30.64) * mm});
            skLineSegment(sketch, "E2563", {"start": v(-2.07, 30.64) * mm, "end": v(-2.11, 30.62) * mm});
            skLineSegment(sketch, "E2564", {"start": v(-2.11, 30.62) * mm, "end": v(-2.13, 30.58) * mm});
            skLineSegment(sketch, "E2565", {"start": v(-2.13, 30.58) * mm, "end": v(-2.14, 30.54) * mm});
            skLineSegment(sketch, "E2566", {"start": v(-2.14, 30.54) * mm, "end": v(-2.15, 30.5) * mm});
            skLineSegment(sketch, "E2567", {"start": v(-2.15, 30.5) * mm, "end": v(-2.17, 30.45) * mm});
            skLineSegment(sketch, "E2568", {"start": v(-2.17, 30.45) * mm, "end": v(-2.19, 30.41) * mm});
            skLineSegment(sketch, "E2569", {"start": v(-2.19, 30.41) * mm, "end": v(-2.23, 30.37) * mm});
            skLineSegment(sketch, "E2570", {"start": v(-2.23, 30.37) * mm, "end": v(-2.27, 30.34) * mm});
            skLineSegment(sketch, "E2571", {"start": v(-2.27, 30.34) * mm, "end": v(-2.33, 30.32) * mm});
            skLineSegment(sketch, "E2572", {"start": v(-2.33, 30.32) * mm, "end": v(-2.39, 30.3) * mm});
            skLineSegment(sketch, "E2573", {"start": v(-2.39, 30.3) * mm, "end": v(-2.44, 30.3) * mm});
            skLineSegment(sketch, "E2574", {"start": v(-2.44, 30.3) * mm, "end": v(-2.5, 30.32) * mm});
            skLineSegment(sketch, "E2575", {"start": v(-2.5, 30.32) * mm, "end": v(-2.55, 30.34) * mm});
            skLineSegment(sketch, "E2576", {"start": v(-2.55, 30.34) * mm, "end": v(-2.6, 30.38) * mm});
            skLineSegment(sketch, "E2577", {"start": v(-2.6, 30.38) * mm, "end": v(-2.63, 30.42) * mm});
            skLineSegment(sketch, "E2578", {"start": v(-2.63, 30.42) * mm, "end": v(-2.65, 30.46) * mm});
            skLineSegment(sketch, "E2579", {"start": v(-2.65, 30.46) * mm, "end": v(-2.67, 30.5) * mm});
            skLineSegment(sketch, "E2580", {"start": v(-2.67, 30.5) * mm, "end": v(-2.68, 30.54) * mm});
            skLineSegment(sketch, "E2581", {"start": v(-2.68, 30.54) * mm, "end": v(-2.7, 30.58) * mm});
            skLineSegment(sketch, "E2582", {"start": v(-2.7, 30.58) * mm, "end": v(-2.75, 30.59) * mm});
            skLineSegment(sketch, "E2583", {"start": v(-2.75, 30.59) * mm, "end": v(-2.87, 30.58) * mm});
            skLineSegment(sketch, "E2584", {"start": v(-2.87, 30.58) * mm, "end": v(-2.91, 30.56) * mm});
            skLineSegment(sketch, "E2585", {"start": v(-2.91, 30.56) * mm, "end": v(-2.93, 30.52) * mm});
            skLineSegment(sketch, "E2586", {"start": v(-2.93, 30.52) * mm, "end": v(-2.94, 30.47) * mm});
            skLineSegment(sketch, "E2587", {"start": v(-2.94, 30.47) * mm, "end": v(-2.95, 30.43) * mm});
            skLineSegment(sketch, "E2588", {"start": v(-2.95, 30.43) * mm, "end": v(-2.96, 30.39) * mm});
            skLineSegment(sketch, "E2589", {"start": v(-2.96, 30.39) * mm, "end": v(-2.98, 30.35) * mm});
            skLineSegment(sketch, "E2590", {"start": v(-2.98, 30.35) * mm, "end": v(-3.02, 30.3) * mm});
            skLineSegment(sketch, "E2591", {"start": v(-3.02, 30.3) * mm, "end": v(-3.07, 30.27) * mm});
            skLineSegment(sketch, "E2592", {"start": v(-3.07, 30.27) * mm, "end": v(-3.12, 30.25) * mm});
            skLineSegment(sketch, "E2593", {"start": v(-3.12, 30.25) * mm, "end": v(-3.18, 30.23) * mm});
            skLineSegment(sketch, "E2594", {"start": v(-3.18, 30.23) * mm, "end": v(-3.24, 30.23) * mm});
            skLineSegment(sketch, "E2595", {"start": v(-3.24, 30.23) * mm, "end": v(-3.3, 30.24) * mm});
            skLineSegment(sketch, "E2596", {"start": v(-3.3, 30.24) * mm, "end": v(-3.35, 30.27) * mm});
            skLineSegment(sketch, "E2597", {"start": v(-3.35, 30.27) * mm, "end": v(-3.4, 30.3) * mm});
            skLineSegment(sketch, "E2598", {"start": v(-3.4, 30.3) * mm, "end": v(-3.42, 30.34) * mm});
            skLineSegment(sketch, "E2599", {"start": v(-3.42, 30.34) * mm, "end": v(-3.44, 30.38) * mm});
            skLineSegment(sketch, "E2600", {"start": v(-3.44, 30.38) * mm, "end": v(-3.46, 30.42) * mm});
            skLineSegment(sketch, "E2601", {"start": v(-3.46, 30.42) * mm, "end": v(-3.48, 30.46) * mm});
            skLineSegment(sketch, "E2602", {"start": v(-3.48, 30.46) * mm, "end": v(-3.5, 30.5) * mm});
            skLineSegment(sketch, "E2603", {"start": v(-3.5, 30.5) * mm, "end": v(-3.55, 30.5) * mm});
            skLineSegment(sketch, "E2604", {"start": v(-3.55, 30.5) * mm, "end": v(-3.67, 30.5) * mm});
            skLineSegment(sketch, "E2605", {"start": v(-3.67, 30.5) * mm, "end": v(-3.71, 30.47) * mm});
            skLineSegment(sketch, "E2606", {"start": v(-3.71, 30.47) * mm, "end": v(-3.73, 30.43) * mm});
            skLineSegment(sketch, "E2607", {"start": v(-3.73, 30.43) * mm, "end": v(-3.73, 30.39) * mm});
            skLineSegment(sketch, "E2608", {"start": v(-3.73, 30.39) * mm, "end": v(-3.74, 30.34) * mm});
            skLineSegment(sketch, "E2609", {"start": v(-3.74, 30.34) * mm, "end": v(-3.76, 30.3) * mm});
            skLineSegment(sketch, "E2610", {"start": v(-3.76, 30.3) * mm, "end": v(-3.78, 30.26) * mm});
            skLineSegment(sketch, "E2611", {"start": v(-3.78, 30.26) * mm, "end": v(-3.81, 30.21) * mm});
            skLineSegment(sketch, "E2612", {"start": v(-3.81, 30.21) * mm, "end": v(-3.86, 30.18) * mm});
            skLineSegment(sketch, "E2613", {"start": v(-3.86, 30.18) * mm, "end": v(-3.91, 30.15) * mm});
            skLineSegment(sketch, "E2614", {"start": v(-3.91, 30.15) * mm, "end": v(-3.97, 30.14) * mm});
            skLineSegment(sketch, "E2615", {"start": v(-3.97, 30.14) * mm, "end": v(-4.03, 30.14) * mm});
            skLineSegment(sketch, "E2616", {"start": v(-4.03, 30.14) * mm, "end": v(-4.08, 30.15) * mm});
            skLineSegment(sketch, "E2617", {"start": v(-4.08, 30.15) * mm, "end": v(-4.14, 30.17) * mm});
            skLineSegment(sketch, "E2618", {"start": v(-4.14, 30.17) * mm, "end": v(-4.18, 30.2) * mm});
            skLineSegment(sketch, "E2619", {"start": v(-4.18, 30.2) * mm, "end": v(-4.21, 30.24) * mm});
            skLineSegment(sketch, "E2620", {"start": v(-4.21, 30.24) * mm, "end": v(-4.24, 30.28) * mm});
            skLineSegment(sketch, "E2621", {"start": v(-4.24, 30.28) * mm, "end": v(-4.26, 30.32) * mm});
            skLineSegment(sketch, "E2622", {"start": v(-4.26, 30.32) * mm, "end": v(-4.27, 30.36) * mm});
            skLineSegment(sketch, "E2623", {"start": v(-4.27, 30.36) * mm, "end": v(-4.3, 30.4) * mm});
            skLineSegment(sketch, "E2624", {"start": v(-4.3, 30.4) * mm, "end": v(-4.35, 30.4) * mm});
            skLineSegment(sketch, "E2625", {"start": v(-4.35, 30.4) * mm, "end": v(-4.47, 30.38) * mm});
            skLineSegment(sketch, "E2626", {"start": v(-4.47, 30.38) * mm, "end": v(-4.5, 30.36) * mm});
            skLineSegment(sketch, "E2627", {"start": v(-4.5, 30.36) * mm, "end": v(-4.53, 30.32) * mm});
            skLineSegment(sketch, "E2628", {"start": v(-4.53, 30.32) * mm, "end": v(-4.53, 30.28) * mm});
            skLineSegment(sketch, "E2629", {"start": v(-4.53, 30.28) * mm, "end": v(-4.54, 30.23) * mm});
            skLineSegment(sketch, "E2630", {"start": v(-4.54, 30.23) * mm, "end": v(-4.55, 30.19) * mm});
            skLineSegment(sketch, "E2631", {"start": v(-4.55, 30.19) * mm, "end": v(-4.57, 30.15) * mm});
            skLineSegment(sketch, "E2632", {"start": v(-4.57, 30.15) * mm, "end": v(-4.6, 30.1) * mm});
            skLineSegment(sketch, "E2633", {"start": v(-4.6, 30.1) * mm, "end": v(-4.65, 30.07) * mm});
            skLineSegment(sketch, "E2634", {"start": v(-4.65, 30.07) * mm, "end": v(-4.7, 30.04) * mm});
            skLineSegment(sketch, "E2635", {"start": v(-4.7, 30.04) * mm, "end": v(-4.76, 30.03) * mm});
            skLineSegment(sketch, "E2636", {"start": v(-4.76, 30.03) * mm, "end": v(-4.81, 30.02) * mm});
            skLineSegment(sketch, "E2637", {"start": v(-4.81, 30.02) * mm, "end": v(-4.87, 30.03) * mm});
            skLineSegment(sketch, "E2638", {"start": v(-4.87, 30.03) * mm, "end": v(-4.93, 30.05) * mm});
            skLineSegment(sketch, "E2639", {"start": v(-4.93, 30.05) * mm, "end": v(-4.97, 30.08) * mm});
            skLineSegment(sketch, "E2640", {"start": v(-4.97, 30.08) * mm, "end": v(-5, 30.12) * mm});
            skLineSegment(sketch, "E2641", {"start": v(-5, 30.12) * mm, "end": v(-5.03, 30.15) * mm});
            skLineSegment(sketch, "E2642", {"start": v(-5.03, 30.15) * mm, "end": v(-5.05, 30.2) * mm});
            skLineSegment(sketch, "E2643", {"start": v(-5.05, 30.2) * mm, "end": v(-5.07, 30.24) * mm});
            skLineSegment(sketch, "E2644", {"start": v(-5.07, 30.24) * mm, "end": v(-5.1, 30.27) * mm});
            skLineSegment(sketch, "E2645", {"start": v(-5.1, 30.27) * mm, "end": v(-5.14, 30.28) * mm});
            skLineSegment(sketch, "E2646", {"start": v(-5.14, 30.28) * mm, "end": v(-5.26, 30.26) * mm});
            skLineSegment(sketch, "E2647", {"start": v(-5.26, 30.26) * mm, "end": v(-5.3, 30.23) * mm});
            skLineSegment(sketch, "E2648", {"start": v(-5.3, 30.23) * mm, "end": v(-5.32, 30.2) * mm});
            skLineSegment(sketch, "E2649", {"start": v(-5.32, 30.2) * mm, "end": v(-5.32, 30.15) * mm});
            skLineSegment(sketch, "E2650", {"start": v(-5.32, 30.15) * mm, "end": v(-5.32, 30.1) * mm});
            skLineSegment(sketch, "E2651", {"start": v(-5.32, 30.1) * mm, "end": v(-5.34, 30.06) * mm});
            skLineSegment(sketch, "E2652", {"start": v(-5.34, 30.06) * mm, "end": v(-5.35, 30.02) * mm});
            skLineSegment(sketch, "E2653", {"start": v(-5.35, 30.02) * mm, "end": v(-5.39, 29.97) * mm});
            skLineSegment(sketch, "E2654", {"start": v(-5.39, 29.97) * mm, "end": v(-5.43, 29.93) * mm});
            skLineSegment(sketch, "E2655", {"start": v(-5.43, 29.93) * mm, "end": v(-5.48, 29.9) * mm});
            skLineSegment(sketch, "E2656", {"start": v(-5.48, 29.9) * mm, "end": v(-5.54, 29.9) * mm});
            skLineSegment(sketch, "E2657", {"start": v(-5.54, 29.9) * mm, "end": v(-5.6, 29.89) * mm});
            skLineSegment(sketch, "E2658", {"start": v(-5.6, 29.89) * mm, "end": v(-5.66, 29.9) * mm});
            skLineSegment(sketch, "E2659", {"start": v(-5.66, 29.9) * mm, "end": v(-5.71, 29.91) * mm});
            skLineSegment(sketch, "E2660", {"start": v(-5.71, 29.91) * mm, "end": v(-5.76, 29.94) * mm});
            skLineSegment(sketch, "E2661", {"start": v(-5.76, 29.94) * mm, "end": v(-5.8, 29.98) * mm});
            skLineSegment(sketch, "E2662", {"start": v(-5.8, 29.98) * mm, "end": v(-5.82, 30.01) * mm});
            skLineSegment(sketch, "E2663", {"start": v(-5.82, 30.01) * mm, "end": v(-5.84, 30.05) * mm});
            skLineSegment(sketch, "E2664", {"start": v(-5.84, 30.05) * mm, "end": v(-5.86, 30.1) * mm});
            skLineSegment(sketch, "E2665", {"start": v(-5.86, 30.1) * mm, "end": v(-5.88, 30.13) * mm});
            skLineSegment(sketch, "E2666", {"start": v(-5.88, 30.13) * mm, "end": v(-5.93, 30.13) * mm});
            skLineSegment(sketch, "E2667", {"start": v(-5.93, 30.13) * mm, "end": v(-6.05, 30.1) * mm});
            skLineSegment(sketch, "E2668", {"start": v(-6.05, 30.1) * mm, "end": v(-6.1, 30.08) * mm});
            skLineSegment(sketch, "E2669", {"start": v(-6.1, 30.08) * mm, "end": v(-6.1, 30.04) * mm});
            skLineSegment(sketch, "E2670", {"start": v(-6.1, 30.04) * mm, "end": v(-6.1, 30) * mm});
            skLineSegment(sketch, "E2671", {"start": v(-6.1, 30) * mm, "end": v(-6.11, 29.95) * mm});
            skLineSegment(sketch, "E2672", {"start": v(-6.11, 29.95) * mm, "end": v(-6.12, 29.91) * mm});
            skLineSegment(sketch, "E2673", {"start": v(-6.12, 29.91) * mm, "end": v(-6.14, 29.87) * mm});
            skLineSegment(sketch, "E2674", {"start": v(-6.14, 29.87) * mm, "end": v(-6.17, 29.82) * mm});
            skLineSegment(sketch, "E2675", {"start": v(-6.17, 29.82) * mm, "end": v(-6.21, 29.78) * mm});
            skLineSegment(sketch, "E2676", {"start": v(-6.21, 29.78) * mm, "end": v(-6.26, 29.75) * mm});
            skLineSegment(sketch, "E2677", {"start": v(-6.26, 29.75) * mm, "end": v(-6.32, 29.74) * mm});
            skLineSegment(sketch, "E2678", {"start": v(-6.32, 29.74) * mm, "end": v(-6.38, 29.73) * mm});
            skLineSegment(sketch, "E2679", {"start": v(-6.38, 29.73) * mm, "end": v(-6.44, 29.73) * mm});
            skLineSegment(sketch, "E2680", {"start": v(-6.44, 29.73) * mm, "end": v(-6.5, 29.75) * mm});
            skLineSegment(sketch, "E2681", {"start": v(-6.5, 29.75) * mm, "end": v(-6.54, 29.78) * mm});
            skLineSegment(sketch, "E2682", {"start": v(-6.54, 29.78) * mm, "end": v(-6.57, 29.81) * mm});
            skLineSegment(sketch, "E2683", {"start": v(-6.57, 29.81) * mm, "end": v(-6.6, 29.85) * mm});
            skLineSegment(sketch, "E2684", {"start": v(-6.6, 29.85) * mm, "end": v(-6.62, 29.89) * mm});
            skLineSegment(sketch, "E2685", {"start": v(-6.62, 29.89) * mm, "end": v(-6.64, 29.93) * mm});
            skLineSegment(sketch, "E2686", {"start": v(-6.64, 29.93) * mm, "end": v(-6.67, 29.96) * mm});
            skLineSegment(sketch, "E2687", {"start": v(-6.67, 29.96) * mm, "end": v(-6.72, 29.97) * mm});
            skLineSegment(sketch, "E2688", {"start": v(-6.72, 29.97) * mm, "end": v(-6.84, 29.94) * mm});
            skLineSegment(sketch, "E2689", {"start": v(-6.84, 29.94) * mm, "end": v(-6.88, 29.91) * mm});
            skLineSegment(sketch, "E2690", {"start": v(-6.88, 29.91) * mm, "end": v(-6.9, 29.87) * mm});
            skLineSegment(sketch, "E2691", {"start": v(-6.9, 29.87) * mm, "end": v(-6.89, 29.83) * mm});
            skLineSegment(sketch, "E2692", {"start": v(-6.89, 29.83) * mm, "end": v(-6.9, 29.78) * mm});
            skLineSegment(sketch, "E2693", {"start": v(-6.9, 29.78) * mm, "end": v(-6.9, 29.74) * mm});
            skLineSegment(sketch, "E2694", {"start": v(-6.9, 29.74) * mm, "end": v(-6.92, 29.7) * mm});
            skLineSegment(sketch, "E2695", {"start": v(-6.92, 29.7) * mm, "end": v(-6.95, 29.65) * mm});
            skLineSegment(sketch, "E2696", {"start": v(-6.95, 29.65) * mm, "end": v(-7, 29.6) * mm});
            skLineSegment(sketch, "E2697", {"start": v(-7, 29.6) * mm, "end": v(-7.04, 29.58) * mm});
            skLineSegment(sketch, "E2698", {"start": v(-7.04, 29.58) * mm, "end": v(-7.1, 29.56) * mm});
            skLineSegment(sketch, "E2699", {"start": v(-7.1, 29.56) * mm, "end": v(-7.15, 29.55) * mm});
            skLineSegment(sketch, "E2700", {"start": v(-7.15, 29.55) * mm, "end": v(-7.21, 29.56) * mm});
            skLineSegment(sketch, "E2701", {"start": v(-7.21, 29.56) * mm, "end": v(-7.27, 29.57) * mm});
            skLineSegment(sketch, "E2702", {"start": v(-7.27, 29.57) * mm, "end": v(-7.32, 29.6) * mm});
            skLineSegment(sketch, "E2703", {"start": v(-7.32, 29.6) * mm, "end": v(-7.35, 29.63) * mm});
            skLineSegment(sketch, "E2704", {"start": v(-7.35, 29.63) * mm, "end": v(-7.38, 29.67) * mm});
            skLineSegment(sketch, "E2705", {"start": v(-7.38, 29.67) * mm, "end": v(-7.4, 29.7) * mm});
            skLineSegment(sketch, "E2706", {"start": v(-7.4, 29.7) * mm, "end": v(-7.42, 29.75) * mm});
            skLineSegment(sketch, "E2707", {"start": v(-7.42, 29.75) * mm, "end": v(-7.45, 29.78) * mm});
            skLineSegment(sketch, "E2708", {"start": v(-7.45, 29.78) * mm, "end": v(-7.5, 29.78) * mm});
            skLineSegment(sketch, "E2709", {"start": v(-7.5, 29.78) * mm, "end": v(-7.62, 29.75) * mm});
            skLineSegment(sketch, "E2710", {"start": v(-7.62, 29.75) * mm, "end": v(-7.66, 29.72) * mm});
            skLineSegment(sketch, "E2711", {"start": v(-7.66, 29.72) * mm, "end": v(-7.67, 29.68) * mm});
            skLineSegment(sketch, "E2712", {"start": v(-7.67, 29.68) * mm, "end": v(-7.67, 29.64) * mm});
            skLineSegment(sketch, "E2713", {"start": v(-7.67, 29.64) * mm, "end": v(-7.67, 29.6) * mm});
            skLineSegment(sketch, "E2714", {"start": v(-7.67, 29.6) * mm, "end": v(-7.68, 29.55) * mm});
            skLineSegment(sketch, "E2715", {"start": v(-7.68, 29.55) * mm, "end": v(-7.7, 29.5) * mm});
            skLineSegment(sketch, "E2716", {"start": v(-7.7, 29.5) * mm, "end": v(-7.72, 29.46) * mm});
            skLineSegment(sketch, "E2717", {"start": v(-7.72, 29.46) * mm, "end": v(-7.76, 29.42) * mm});
            skLineSegment(sketch, "E2718", {"start": v(-7.76, 29.42) * mm, "end": v(-7.81, 29.39) * mm});
            skLineSegment(sketch, "E2719", {"start": v(-7.81, 29.39) * mm, "end": v(-7.87, 29.36) * mm});
            skLineSegment(sketch, "E2720", {"start": v(-7.87, 29.36) * mm, "end": v(-7.93, 29.35) * mm});
            skLineSegment(sketch, "E2721", {"start": v(-7.93, 29.35) * mm, "end": v(-7.98, 29.36) * mm});
            skLineSegment(sketch, "E2722", {"start": v(-7.98, 29.36) * mm, "end": v(-8.04, 29.37) * mm});
            skLineSegment(sketch, "E2723", {"start": v(-8.04, 29.37) * mm, "end": v(-8.1, 29.4) * mm});
            skLineSegment(sketch, "E2724", {"start": v(-8.1, 29.4) * mm, "end": v(-8.12, 29.43) * mm});
            skLineSegment(sketch, "E2725", {"start": v(-8.12, 29.43) * mm, "end": v(-8.15, 29.46) * mm});
            skLineSegment(sketch, "E2726", {"start": v(-8.15, 29.46) * mm, "end": v(-8.18, 29.5) * mm});
            skLineSegment(sketch, "E2727", {"start": v(-8.18, 29.5) * mm, "end": v(-8.2, 29.54) * mm});
            skLineSegment(sketch, "E2728", {"start": v(-8.2, 29.54) * mm, "end": v(-8.23, 29.57) * mm});
            skLineSegment(sketch, "E2729", {"start": v(-8.23, 29.57) * mm, "end": v(-8.28, 29.57) * mm});
            skLineSegment(sketch, "E2730", {"start": v(-8.28, 29.57) * mm, "end": v(-8.4, 29.54) * mm});
            skLineSegment(sketch, "E2731", {"start": v(-8.4, 29.54) * mm, "end": v(-8.43, 29.51) * mm});
            skLineSegment(sketch, "E2732", {"start": v(-8.43, 29.51) * mm, "end": v(-8.44, 29.47) * mm});
            skLineSegment(sketch, "E2733", {"start": v(-8.44, 29.47) * mm, "end": v(-8.44, 29.43) * mm});
            skLineSegment(sketch, "E2734", {"start": v(-8.44, 29.43) * mm, "end": v(-8.44, 29.38) * mm});
            skLineSegment(sketch, "E2735", {"start": v(-8.44, 29.38) * mm, "end": v(-8.45, 29.34) * mm});
            skLineSegment(sketch, "E2736", {"start": v(-8.45, 29.34) * mm, "end": v(-8.46, 29.3) * mm});
            skLineSegment(sketch, "E2737", {"start": v(-8.46, 29.3) * mm, "end": v(-8.5, 29.24) * mm});
            skLineSegment(sketch, "E2738", {"start": v(-8.5, 29.24) * mm, "end": v(-8.53, 29.2) * mm});
            skLineSegment(sketch, "E2739", {"start": v(-8.53, 29.2) * mm, "end": v(-8.58, 29.17) * mm});
            skLineSegment(sketch, "E2740", {"start": v(-8.58, 29.17) * mm, "end": v(-8.63, 29.15) * mm});
            skLineSegment(sketch, "E2741", {"start": v(-8.63, 29.15) * mm, "end": v(-8.7, 29.14) * mm});
            skLineSegment(sketch, "E2742", {"start": v(-8.7, 29.14) * mm, "end": v(-8.75, 29.14) * mm});
            skLineSegment(sketch, "E2743", {"start": v(-8.75, 29.14) * mm, "end": v(-8.8, 29.15) * mm});
            skLineSegment(sketch, "E2744", {"start": v(-8.8, 29.15) * mm, "end": v(-8.86, 29.18) * mm});
            skLineSegment(sketch, "E2745", {"start": v(-8.86, 29.18) * mm, "end": v(-8.9, 29.2) * mm});
            skLineSegment(sketch, "E2746", {"start": v(-8.9, 29.2) * mm, "end": v(-8.92, 29.24) * mm});
            skLineSegment(sketch, "E2747", {"start": v(-8.92, 29.24) * mm, "end": v(-8.95, 29.28) * mm});
            skLineSegment(sketch, "E2748", {"start": v(-8.95, 29.28) * mm, "end": v(-8.97, 29.32) * mm});
            skLineSegment(sketch, "E2749", {"start": v(-8.97, 29.32) * mm, "end": v(-9, 29.35) * mm});
            skLineSegment(sketch, "E2750", {"start": v(-9, 29.35) * mm, "end": v(-9.05, 29.35) * mm});
            skLineSegment(sketch, "E2751", {"start": v(-9.05, 29.35) * mm, "end": v(-9.16, 29.31) * mm});
            skLineSegment(sketch, "E2752", {"start": v(-9.16, 29.31) * mm, "end": v(-9.2, 29.28) * mm});
            skLineSegment(sketch, "E2753", {"start": v(-9.2, 29.28) * mm, "end": v(-9.21, 29.24) * mm});
            skLineSegment(sketch, "E2754", {"start": v(-9.21, 29.24) * mm, "end": v(-9.2, 29.2) * mm});
            skLineSegment(sketch, "E2755", {"start": v(-9.2, 29.2) * mm, "end": v(-9.2, 29.15) * mm});
            skLineSegment(sketch, "E2756", {"start": v(-9.2, 29.15) * mm, "end": v(-9.21, 29.1) * mm});
            skLineSegment(sketch, "E2757", {"start": v(-9.21, 29.1) * mm, "end": v(-9.23, 29.06) * mm});
            skLineSegment(sketch, "E2758", {"start": v(-9.23, 29.06) * mm, "end": v(-9.25, 29.01) * mm});
            skLineSegment(sketch, "E2759", {"start": v(-9.25, 29.01) * mm, "end": v(-9.3, 28.97) * mm});
            skLineSegment(sketch, "E2760", {"start": v(-9.3, 28.97) * mm, "end": v(-9.34, 28.94) * mm});
            skLineSegment(sketch, "E2761", {"start": v(-9.34, 28.94) * mm, "end": v(-9.4, 28.91) * mm});
            skLineSegment(sketch, "E2762", {"start": v(-9.4, 28.91) * mm, "end": v(-9.45, 28.9) * mm});
            skLineSegment(sketch, "E2763", {"start": v(-9.45, 28.9) * mm, "end": v(-9.5, 28.9) * mm});
            skLineSegment(sketch, "E2764", {"start": v(-9.5, 28.9) * mm, "end": v(-9.57, 28.91) * mm});
            skLineSegment(sketch, "E2765", {"start": v(-9.57, 28.91) * mm, "end": v(-9.62, 28.93) * mm});
            skLineSegment(sketch, "E2766", {"start": v(-9.62, 28.93) * mm, "end": v(-9.65, 28.96) * mm});
            skLineSegment(sketch, "E2767", {"start": v(-9.65, 28.96) * mm, "end": v(-9.68, 29) * mm});
            skLineSegment(sketch, "E2768", {"start": v(-9.68, 29) * mm, "end": v(-9.71, 29.03) * mm});
            skLineSegment(sketch, "E2769", {"start": v(-9.71, 29.03) * mm, "end": v(-9.73, 29.07) * mm});
            skLineSegment(sketch, "E2770", {"start": v(-9.73, 29.07) * mm, "end": v(-9.77, 29.1) * mm});
            skLineSegment(sketch, "E2771", {"start": v(-9.77, 29.1) * mm, "end": v(-9.81, 29.1) * mm});
            skLineSegment(sketch, "E2772", {"start": v(-9.81, 29.1) * mm, "end": v(-9.93, 29.06) * mm});
            skLineSegment(sketch, "E2773", {"start": v(-9.93, 29.06) * mm, "end": v(-9.97, 29.03) * mm});
            skLineSegment(sketch, "E2774", {"start": v(-9.97, 29.03) * mm, "end": v(-9.98, 28.99) * mm});
            skLineSegment(sketch, "E2775", {"start": v(-9.98, 28.99) * mm, "end": v(-9.97, 28.94) * mm});
            skLineSegment(sketch, "E2776", {"start": v(-9.97, 28.94) * mm, "end": v(-9.97, 28.9) * mm});
            skLineSegment(sketch, "E2777", {"start": v(-9.97, 28.9) * mm, "end": v(-9.97, 28.86) * mm});
            skLineSegment(sketch, "E2778", {"start": v(-9.97, 28.86) * mm, "end": v(-9.98, 28.81) * mm});
            skLineSegment(sketch, "E2779", {"start": v(-9.98, 28.81) * mm, "end": v(-10.01, 28.76) * mm});
            skLineSegment(sketch, "E2780", {"start": v(-10.01, 28.76) * mm, "end": v(-10.05, 28.72) * mm});
            skLineSegment(sketch, "E2781", {"start": v(-10.05, 28.72) * mm, "end": v(-10.1, 28.68) * mm});
            skLineSegment(sketch, "E2782", {"start": v(-10.1, 28.68) * mm, "end": v(-10.15, 28.66) * mm});
            skLineSegment(sketch, "E2783", {"start": v(-10.15, 28.66) * mm, "end": v(-10.2, 28.64) * mm});
            skLineSegment(sketch, "E2784", {"start": v(-10.2, 28.64) * mm, "end": v(-10.26, 28.64) * mm});
            skLineSegment(sketch, "E2785", {"start": v(-10.26, 28.64) * mm, "end": v(-10.32, 28.65) * mm});
            skLineSegment(sketch, "E2786", {"start": v(-10.32, 28.65) * mm, "end": v(-10.37, 28.67) * mm});
            skLineSegment(sketch, "E2787", {"start": v(-10.37, 28.67) * mm, "end": v(-10.4, 28.7) * mm});
            skLineSegment(sketch, "E2788", {"start": v(-10.4, 28.7) * mm, "end": v(-10.44, 28.73) * mm});
            skLineSegment(sketch, "E2789", {"start": v(-10.44, 28.73) * mm, "end": v(-10.47, 28.77) * mm});
            skLineSegment(sketch, "E2790", {"start": v(-10.47, 28.77) * mm, "end": v(-10.5, 28.8) * mm});
            skLineSegment(sketch, "E2791", {"start": v(-10.5, 28.8) * mm, "end": v(-10.53, 28.83) * mm});
            skLineSegment(sketch, "E2792", {"start": v(-10.53, 28.83) * mm, "end": v(-10.57, 28.83) * mm});
            skLineSegment(sketch, "E2793", {"start": v(-10.57, 28.83) * mm, "end": v(-10.69, 28.8) * mm});
            skLineSegment(sketch, "E2794", {"start": v(-10.69, 28.8) * mm, "end": v(-10.72, 28.76) * mm});
            skLineSegment(sketch, "E2795", {"start": v(-10.72, 28.76) * mm, "end": v(-10.73, 28.72) * mm});
            skLineSegment(sketch, "E2796", {"start": v(-10.73, 28.72) * mm, "end": v(-10.72, 28.67) * mm});
            skLineSegment(sketch, "E2797", {"start": v(-10.72, 28.67) * mm, "end": v(-10.72, 28.63) * mm});
            skLineSegment(sketch, "E2798", {"start": v(-10.72, 28.63) * mm, "end": v(-10.73, 28.58) * mm});
            skLineSegment(sketch, "E2799", {"start": v(-10.73, 28.58) * mm, "end": v(-10.73, 28.54) * mm});
            skLineSegment(sketch, "E2800", {"start": v(-10.73, 28.54) * mm, "end": v(-10.76, 28.49) * mm});
            skLineSegment(sketch, "E2801", {"start": v(-10.76, 28.49) * mm, "end": v(-10.8, 28.44) * mm});
            skLineSegment(sketch, "E2802", {"start": v(-10.8, 28.44) * mm, "end": v(-10.84, 28.4) * mm});
            skLineSegment(sketch, "E2803", {"start": v(-10.84, 28.4) * mm, "end": v(-10.9, 28.38) * mm});
            skLineSegment(sketch, "E2804", {"start": v(-10.9, 28.38) * mm, "end": v(-10.95, 28.37) * mm});
            skLineSegment(sketch, "E2805", {"start": v(-10.95, 28.37) * mm, "end": v(-11, 28.36) * mm});
            skLineSegment(sketch, "E2806", {"start": v(-11, 28.36) * mm, "end": v(-11.07, 28.37) * mm});
            skLineSegment(sketch, "E2807", {"start": v(-11.07, 28.37) * mm, "end": v(-11.12, 28.4) * mm});
            skLineSegment(sketch, "E2808", {"start": v(-11.12, 28.4) * mm, "end": v(-11.16, 28.42) * mm});
            skLineSegment(sketch, "E2809", {"start": v(-11.16, 28.42) * mm, "end": v(-11.19, 28.45) * mm});
            skLineSegment(sketch, "E2810", {"start": v(-11.19, 28.45) * mm, "end": v(-11.22, 28.48) * mm});
            skLineSegment(sketch, "E2811", {"start": v(-11.22, 28.48) * mm, "end": v(-11.24, 28.52) * mm});
            skLineSegment(sketch, "E2812", {"start": v(-11.24, 28.52) * mm, "end": v(-11.28, 28.55) * mm});
            skLineSegment(sketch, "E2813", {"start": v(-11.28, 28.55) * mm, "end": v(-11.32, 28.55) * mm});
            skLineSegment(sketch, "E2814", {"start": v(-11.32, 28.55) * mm, "end": v(-11.44, 28.5) * mm});
            skLineSegment(sketch, "E2815", {"start": v(-11.44, 28.5) * mm, "end": v(-11.47, 28.47) * mm});
            skLineSegment(sketch, "E2816", {"start": v(-11.47, 28.47) * mm, "end": v(-11.48, 28.43) * mm});
            skLineSegment(sketch, "E2817", {"start": v(-11.48, 28.43) * mm, "end": v(-11.47, 28.38) * mm});
            skLineSegment(sketch, "E2818", {"start": v(-11.47, 28.38) * mm, "end": v(-11.47, 28.34) * mm});
            skLineSegment(sketch, "E2819", {"start": v(-11.47, 28.34) * mm, "end": v(-11.47, 28.3) * mm});
            skLineSegment(sketch, "E2820", {"start": v(-11.47, 28.3) * mm, "end": v(-11.48, 28.25) * mm});
            skLineSegment(sketch, "E2821", {"start": v(-11.48, 28.25) * mm, "end": v(-11.5, 28.2) * mm});
            skLineSegment(sketch, "E2822", {"start": v(-11.5, 28.2) * mm, "end": v(-11.54, 28.15) * mm});
            skLineSegment(sketch, "E2823", {"start": v(-11.54, 28.15) * mm, "end": v(-11.58, 28.11) * mm});
            skLineSegment(sketch, "E2824", {"start": v(-11.58, 28.11) * mm, "end": v(-11.63, 28.09) * mm});
            skLineSegment(sketch, "E2825", {"start": v(-11.63, 28.09) * mm, "end": v(-11.69, 28.07) * mm});
            skLineSegment(sketch, "E2826", {"start": v(-11.69, 28.07) * mm, "end": v(-11.75, 28.06) * mm});
            skLineSegment(sketch, "E2827", {"start": v(-11.75, 28.06) * mm, "end": v(-11.8, 28.07) * mm});
            skLineSegment(sketch, "E2828", {"start": v(-11.8, 28.07) * mm, "end": v(-11.86, 28.1) * mm});
            skLineSegment(sketch, "E2829", {"start": v(-11.86, 28.1) * mm, "end": v(-11.9, 28.12) * mm});
            skLineSegment(sketch, "E2830", {"start": v(-11.9, 28.12) * mm, "end": v(-11.93, 28.15) * mm});
            skLineSegment(sketch, "E2831", {"start": v(-11.93, 28.15) * mm, "end": v(-11.96, 28.18) * mm});
            skLineSegment(sketch, "E2832", {"start": v(-11.96, 28.18) * mm, "end": v(-11.98, 28.22) * mm});
            skLineSegment(sketch, "E2833", {"start": v(-11.98, 28.22) * mm, "end": v(-12.02, 28.24) * mm});
            skLineSegment(sketch, "E2834", {"start": v(-12.02, 28.24) * mm, "end": v(-12.07, 28.24) * mm});
            skLineSegment(sketch, "E2835", {"start": v(-12.07, 28.24) * mm, "end": v(-12.18, 28.2) * mm});
            skLineSegment(sketch, "E2836", {"start": v(-12.18, 28.2) * mm, "end": v(-12.21, 28.16) * mm});
            skLineSegment(sketch, "E2837", {"start": v(-12.21, 28.16) * mm, "end": v(-12.22, 28.12) * mm});
            skLineSegment(sketch, "E2838", {"start": v(-12.22, 28.12) * mm, "end": v(-12.2, 28.07) * mm});
            skLineSegment(sketch, "E2839", {"start": v(-12.2, 28.07) * mm, "end": v(-12.2, 28.03) * mm});
            skLineSegment(sketch, "E2840", {"start": v(-12.2, 28.03) * mm, "end": v(-12.2, 27.98) * mm});
            skLineSegment(sketch, "E2841", {"start": v(-12.2, 27.98) * mm, "end": v(-12.21, 27.94) * mm});
            skLineSegment(sketch, "E2842", {"start": v(-12.21, 27.94) * mm, "end": v(-12.24, 27.89) * mm});
            skLineSegment(sketch, "E2843", {"start": v(-12.24, 27.89) * mm, "end": v(-12.27, 27.84) * mm});
            skLineSegment(sketch, "E2844", {"start": v(-12.27, 27.84) * mm, "end": v(-12.31, 27.8) * mm});
            skLineSegment(sketch, "E2845", {"start": v(-12.31, 27.8) * mm, "end": v(-12.36, 27.77) * mm});
            skLineSegment(sketch, "E2846", {"start": v(-12.36, 27.77) * mm, "end": v(-12.42, 27.75) * mm});
            skLineSegment(sketch, "E2847", {"start": v(-12.42, 27.75) * mm, "end": v(-12.48, 27.75) * mm});
            skLineSegment(sketch, "E2848", {"start": v(-12.48, 27.75) * mm, "end": v(-12.54, 27.75) * mm});
            skLineSegment(sketch, "E2849", {"start": v(-12.54, 27.75) * mm, "end": v(-12.6, 27.77) * mm});
            skLineSegment(sketch, "E2850", {"start": v(-12.6, 27.77) * mm, "end": v(-12.63, 27.8) * mm});
            skLineSegment(sketch, "E2851", {"start": v(-12.63, 27.8) * mm, "end": v(-12.66, 27.83) * mm});
            skLineSegment(sketch, "E2852", {"start": v(-12.66, 27.83) * mm, "end": v(-12.7, 27.86) * mm});
            skLineSegment(sketch, "E2853", {"start": v(-12.7, 27.86) * mm, "end": v(-12.72, 27.9) * mm});
            skLineSegment(sketch, "E2854", {"start": v(-12.72, 27.9) * mm, "end": v(-12.75, 27.92) * mm});
            skLineSegment(sketch, "E2855", {"start": v(-12.75, 27.92) * mm, "end": v(-12.8, 27.91) * mm});
            skLineSegment(sketch, "E2856", {"start": v(-12.8, 27.91) * mm, "end": v(-12.91, 27.86) * mm});
            skLineSegment(sketch, "E2857", {"start": v(-12.91, 27.86) * mm, "end": v(-12.95, 27.83) * mm});
            skLineSegment(sketch, "E2858", {"start": v(-12.95, 27.83) * mm, "end": v(-12.95, 27.79) * mm});
            skLineSegment(sketch, "E2859", {"start": v(-12.95, 27.79) * mm, "end": v(-12.94, 27.74) * mm});
            skLineSegment(sketch, "E2860", {"start": v(-12.94, 27.74) * mm, "end": v(-12.93, 27.7) * mm});
            skLineSegment(sketch, "E2861", {"start": v(-12.93, 27.7) * mm, "end": v(-12.93, 27.65) * mm});
            skLineSegment(sketch, "E2862", {"start": v(-12.93, 27.65) * mm, "end": v(-12.94, 27.6) * mm});
            skLineSegment(sketch, "E2863", {"start": v(-12.94, 27.6) * mm, "end": v(-12.96, 27.56) * mm});
            skLineSegment(sketch, "E2864", {"start": v(-12.96, 27.56) * mm, "end": v(-13, 27.5) * mm});
            skLineSegment(sketch, "E2865", {"start": v(-13, 27.5) * mm, "end": v(-13.04, 27.47) * mm});
            skLineSegment(sketch, "E2866", {"start": v(-13.04, 27.47) * mm, "end": v(-13.09, 27.44) * mm});
            skLineSegment(sketch, "E2867", {"start": v(-13.09, 27.44) * mm, "end": v(-13.14, 27.42) * mm});
            skLineSegment(sketch, "E2868", {"start": v(-13.14, 27.42) * mm, "end": v(-13.2, 27.41) * mm});
            skLineSegment(sketch, "E2869", {"start": v(-13.2, 27.41) * mm, "end": v(-13.26, 27.41) * mm});
            skLineSegment(sketch, "E2870", {"start": v(-13.26, 27.41) * mm, "end": v(-13.31, 27.43) * mm});
            skLineSegment(sketch, "E2871", {"start": v(-13.31, 27.43) * mm, "end": v(-13.35, 27.46) * mm});
            skLineSegment(sketch, "E2872", {"start": v(-13.35, 27.46) * mm, "end": v(-13.39, 27.48) * mm});
            skLineSegment(sketch, "E2873", {"start": v(-13.39, 27.48) * mm, "end": v(-13.42, 27.52) * mm});
            skLineSegment(sketch, "E2874", {"start": v(-13.42, 27.52) * mm, "end": v(-13.44, 27.55) * mm});
            skLineSegment(sketch, "E2875", {"start": v(-13.44, 27.55) * mm, "end": v(-13.48, 27.58) * mm});
            skLineSegment(sketch, "E2876", {"start": v(-13.48, 27.58) * mm, "end": v(-13.53, 27.57) * mm});
            skLineSegment(sketch, "E2877", {"start": v(-13.53, 27.57) * mm, "end": v(-13.64, 27.52) * mm});
            skLineSegment(sketch, "E2878", {"start": v(-13.64, 27.52) * mm, "end": v(-13.67, 27.48) * mm});
            skLineSegment(sketch, "E2879", {"start": v(-13.67, 27.48) * mm, "end": v(-13.67, 27.44) * mm});
            skLineSegment(sketch, "E2880", {"start": v(-13.67, 27.44) * mm, "end": v(-13.66, 27.4) * mm});
            skLineSegment(sketch, "E2881", {"start": v(-13.66, 27.4) * mm, "end": v(-13.66, 27.35) * mm});
            skLineSegment(sketch, "E2882", {"start": v(-13.66, 27.35) * mm, "end": v(-13.65, 27.3) * mm});
            skLineSegment(sketch, "E2883", {"start": v(-13.65, 27.3) * mm, "end": v(-13.66, 27.26) * mm});
            skLineSegment(sketch, "E2884", {"start": v(-13.66, 27.26) * mm, "end": v(-13.68, 27.2) * mm});
            skLineSegment(sketch, "E2885", {"start": v(-13.68, 27.2) * mm, "end": v(-13.71, 27.16) * mm});
            skLineSegment(sketch, "E2886", {"start": v(-13.71, 27.16) * mm, "end": v(-13.75, 27.12) * mm});
            skLineSegment(sketch, "E2887", {"start": v(-13.75, 27.12) * mm, "end": v(-13.8, 27.09) * mm});
            skLineSegment(sketch, "E2888", {"start": v(-13.8, 27.09) * mm, "end": v(-13.86, 27.07) * mm});
            skLineSegment(sketch, "E2889", {"start": v(-13.86, 27.07) * mm, "end": v(-13.91, 27.06) * mm});
            skLineSegment(sketch, "E2890", {"start": v(-13.91, 27.06) * mm, "end": v(-13.97, 27.06) * mm});
            skLineSegment(sketch, "E2891", {"start": v(-13.97, 27.06) * mm, "end": v(-14.03, 27.07) * mm});
            skLineSegment(sketch, "E2892", {"start": v(-14.03, 27.07) * mm, "end": v(-14.07, 27.1) * mm});
            skLineSegment(sketch, "E2893", {"start": v(-14.07, 27.1) * mm, "end": v(-14.1, 27.12) * mm});
            skLineSegment(sketch, "E2894", {"start": v(-14.1, 27.12) * mm, "end": v(-14.13, 27.16) * mm});
            skLineSegment(sketch, "E2895", {"start": v(-14.13, 27.16) * mm, "end": v(-14.16, 27.2) * mm});
            skLineSegment(sketch, "E2896", {"start": v(-14.16, 27.2) * mm, "end": v(-14.2, 27.21) * mm});
            skLineSegment(sketch, "E2897", {"start": v(-14.2, 27.21) * mm, "end": v(-14.25, 27.2) * mm});
            skLineSegment(sketch, "E2898", {"start": v(-14.25, 27.2) * mm, "end": v(-14.35, 27.15) * mm});
            skLineSegment(sketch, "E2899", {"start": v(-14.35, 27.15) * mm, "end": v(-14.39, 27.12) * mm});
            skLineSegment(sketch, "E2900", {"start": v(-14.39, 27.12) * mm, "end": v(-14.39, 27.07) * mm});
            skLineSegment(sketch, "E2901", {"start": v(-14.39, 27.07) * mm, "end": v(-14.37, 27.03) * mm});
            skLineSegment(sketch, "E2902", {"start": v(-14.37, 27.03) * mm, "end": v(-14.37, 26.99) * mm});
            skLineSegment(sketch, "E2903", {"start": v(-14.37, 26.99) * mm, "end": v(-14.36, 26.94) * mm});
            skLineSegment(sketch, "E2904", {"start": v(-14.36, 26.94) * mm, "end": v(-14.37, 26.9) * mm});
            skLineSegment(sketch, "E2905", {"start": v(-14.37, 26.9) * mm, "end": v(-14.39, 26.84) * mm});
            skLineSegment(sketch, "E2906", {"start": v(-14.39, 26.84) * mm, "end": v(-14.42, 26.8) * mm});
            skLineSegment(sketch, "E2907", {"start": v(-14.42, 26.8) * mm, "end": v(-14.46, 26.75) * mm});
            skLineSegment(sketch, "E2908", {"start": v(-14.46, 26.75) * mm, "end": v(-14.5, 26.72) * mm});
            skLineSegment(sketch, "E2909", {"start": v(-14.5, 26.72) * mm, "end": v(-14.56, 26.7) * mm});
            skLineSegment(sketch, "E2910", {"start": v(-14.56, 26.7) * mm, "end": v(-14.62, 26.68) * mm});
            skLineSegment(sketch, "E2911", {"start": v(-14.62, 26.68) * mm, "end": v(-14.67, 26.68) * mm});
            skLineSegment(sketch, "E2912", {"start": v(-14.67, 26.68) * mm, "end": v(-14.73, 26.7) * mm});
            skLineSegment(sketch, "E2913", {"start": v(-14.73, 26.7) * mm, "end": v(-14.77, 26.72) * mm});
            skLineSegment(sketch, "E2914", {"start": v(-14.77, 26.72) * mm, "end": v(-14.8, 26.75) * mm});
            skLineSegment(sketch, "E2915", {"start": v(-14.8, 26.75) * mm, "end": v(-14.84, 26.78) * mm});
            skLineSegment(sketch, "E2916", {"start": v(-14.84, 26.78) * mm, "end": v(-14.87, 26.81) * mm});
            skLineSegment(sketch, "E2917", {"start": v(-14.87, 26.81) * mm, "end": v(-14.9, 26.83) * mm});
            skLineSegment(sketch, "E2918", {"start": v(-14.9, 26.83) * mm, "end": v(-14.95, 26.82) * mm});
            skLineSegment(sketch, "E2919", {"start": v(-14.95, 26.82) * mm, "end": v(-15.06, 26.76) * mm});
            skLineSegment(sketch, "E2920", {"start": v(-15.06, 26.76) * mm, "end": v(-15.1, 26.73) * mm});
            skLineSegment(sketch, "E2921", {"start": v(-15.1, 26.73) * mm, "end": v(-15.1, 26.69) * mm});
            skLineSegment(sketch, "E2922", {"start": v(-15.1, 26.69) * mm, "end": v(-15.08, 26.64) * mm});
            skLineSegment(sketch, "E2923", {"start": v(-15.08, 26.64) * mm, "end": v(-15.07, 26.6) * mm});
            skLineSegment(sketch, "E2924", {"start": v(-15.07, 26.6) * mm, "end": v(-15.06, 26.55) * mm});
            skLineSegment(sketch, "E2925", {"start": v(-15.06, 26.55) * mm, "end": v(-15.07, 26.5) * mm});
            skLineSegment(sketch, "E2926", {"start": v(-15.07, 26.5) * mm, "end": v(-15.08, 26.45) * mm});
            skLineSegment(sketch, "E2927", {"start": v(-15.08, 26.45) * mm, "end": v(-15.11, 26.4) * mm});
            skLineSegment(sketch, "E2928", {"start": v(-15.11, 26.4) * mm, "end": v(-15.15, 26.36) * mm});
            skLineSegment(sketch, "E2929", {"start": v(-15.15, 26.36) * mm, "end": v(-15.2, 26.33) * mm});
            skLineSegment(sketch, "E2930", {"start": v(-15.2, 26.33) * mm, "end": v(-15.25, 26.3) * mm});
            skLineSegment(sketch, "E2931", {"start": v(-15.25, 26.3) * mm, "end": v(-15.31, 26.3) * mm});
            skLineSegment(sketch, "E2932", {"start": v(-15.31, 26.3) * mm, "end": v(-15.37, 26.3) * mm});
            skLineSegment(sketch, "E2933", {"start": v(-15.37, 26.3) * mm, "end": v(-15.42, 26.3) * mm});
            skLineSegment(sketch, "E2934", {"start": v(-15.42, 26.3) * mm, "end": v(-15.46, 26.32) * mm});
            skLineSegment(sketch, "E2935", {"start": v(-15.46, 26.32) * mm, "end": v(-15.5, 26.35) * mm});
            skLineSegment(sketch, "E2936", {"start": v(-15.5, 26.35) * mm, "end": v(-15.54, 26.38) * mm});
            skLineSegment(sketch, "E2937", {"start": v(-15.54, 26.38) * mm, "end": v(-15.56, 26.41) * mm});
            skLineSegment(sketch, "E2938", {"start": v(-15.56, 26.41) * mm, "end": v(-15.6, 26.43) * mm});
            skLineSegment(sketch, "E2939", {"start": v(-15.6, 26.43) * mm, "end": v(-15.65, 26.42) * mm});
            skLineSegment(sketch, "E2940", {"start": v(-15.65, 26.42) * mm, "end": v(-15.75, 26.36) * mm});
            skLineSegment(sketch, "E2941", {"start": v(-15.75, 26.36) * mm, "end": v(-15.78, 26.33) * mm});
            skLineSegment(sketch, "E2942", {"start": v(-15.78, 26.33) * mm, "end": v(-15.78, 26.28) * mm});
            skLineSegment(sketch, "E2943", {"start": v(-15.78, 26.28) * mm, "end": v(-15.77, 26.24) * mm});
            skLineSegment(sketch, "E2944", {"start": v(-15.77, 26.24) * mm, "end": v(-15.76, 26.2) * mm});
            skLineSegment(sketch, "E2945", {"start": v(-15.76, 26.2) * mm, "end": v(-15.75, 26.15) * mm});
            skLineSegment(sketch, "E2946", {"start": v(-15.75, 26.15) * mm, "end": v(-15.76, 26.1) * mm});
            skLineSegment(sketch, "E2947", {"start": v(-15.76, 26.1) * mm, "end": v(-15.77, 26.05) * mm});
            skLineSegment(sketch, "E2948", {"start": v(-15.77, 26.05) * mm, "end": v(-15.8, 26) * mm});
            skLineSegment(sketch, "E2949", {"start": v(-15.8, 26) * mm, "end": v(-15.84, 25.96) * mm});
            skLineSegment(sketch, "E2950", {"start": v(-15.84, 25.96) * mm, "end": v(-15.88, 25.92) * mm});
            skLineSegment(sketch, "E2951", {"start": v(-15.88, 25.92) * mm, "end": v(-15.94, 25.9) * mm});
            skLineSegment(sketch, "E2952", {"start": v(-15.94, 25.9) * mm, "end": v(-16, 25.88) * mm});
            skLineSegment(sketch, "E2953", {"start": v(-16, 25.88) * mm, "end": v(-16.05, 25.88) * mm});
            skLineSegment(sketch, "E2954", {"start": v(-16.05, 25.88) * mm, "end": v(-16.1, 25.89) * mm});
            skLineSegment(sketch, "E2955", {"start": v(-16.1, 25.89) * mm, "end": v(-16.15, 25.91) * mm});
            skLineSegment(sketch, "E2956", {"start": v(-16.15, 25.91) * mm, "end": v(-16.19, 25.93) * mm});
            skLineSegment(sketch, "E2957", {"start": v(-16.19, 25.93) * mm, "end": v(-16.22, 25.96) * mm});
            skLineSegment(sketch, "E2958", {"start": v(-16.22, 25.96) * mm, "end": v(-16.25, 26) * mm});
            skLineSegment(sketch, "E2959", {"start": v(-16.25, 26) * mm, "end": v(-16.3, 26.02) * mm});
            skLineSegment(sketch, "E2960", {"start": v(-16.3, 26.02) * mm, "end": v(-16.34, 26) * mm});
            skLineSegment(sketch, "E2961", {"start": v(-16.34, 26) * mm, "end": v(-16.44, 25.94) * mm});
            skLineSegment(sketch, "E2962", {"start": v(-16.44, 25.94) * mm, "end": v(-16.47, 25.9) * mm});
            skLineSegment(sketch, "E2963", {"start": v(-16.47, 25.9) * mm, "end": v(-16.47, 25.86) * mm});
            skLineSegment(sketch, "E2964", {"start": v(-16.47, 25.86) * mm, "end": v(-16.45, 25.82) * mm});
            skLineSegment(sketch, "E2965", {"start": v(-16.45, 25.82) * mm, "end": v(-16.44, 25.77) * mm});
            skLineSegment(sketch, "E2966", {"start": v(-16.44, 25.77) * mm, "end": v(-16.43, 25.73) * mm});
            skLineSegment(sketch, "E2967", {"start": v(-16.43, 25.73) * mm, "end": v(-16.43, 25.68) * mm});
            skLineSegment(sketch, "E2968", {"start": v(-16.43, 25.68) * mm, "end": v(-16.45, 25.63) * mm});
            skLineSegment(sketch, "E2969", {"start": v(-16.45, 25.63) * mm, "end": v(-16.47, 25.58) * mm});
            skLineSegment(sketch, "E2970", {"start": v(-16.47, 25.58) * mm, "end": v(-16.51, 25.53) * mm});
            skLineSegment(sketch, "E2971", {"start": v(-16.51, 25.53) * mm, "end": v(-16.56, 25.5) * mm});
            skLineSegment(sketch, "E2972", {"start": v(-16.56, 25.5) * mm, "end": v(-16.6, 25.47) * mm});
            skLineSegment(sketch, "E2973", {"start": v(-16.6, 25.47) * mm, "end": v(-16.67, 25.45) * mm});
            skLineSegment(sketch, "E2974", {"start": v(-16.67, 25.45) * mm, "end": v(-16.72, 25.45) * mm});
            skLineSegment(sketch, "E2975", {"start": v(-16.72, 25.45) * mm, "end": v(-16.78, 25.46) * mm});
            skLineSegment(sketch, "E2976", {"start": v(-16.78, 25.46) * mm, "end": v(-16.82, 25.48) * mm});
            skLineSegment(sketch, "E2977", {"start": v(-16.82, 25.48) * mm, "end": v(-16.86, 25.5) * mm});
            skLineSegment(sketch, "E2978", {"start": v(-16.86, 25.5) * mm, "end": v(-16.9, 25.53) * mm});
            skLineSegment(sketch, "E2979", {"start": v(-16.9, 25.53) * mm, "end": v(-16.93, 25.56) * mm});
            skLineSegment(sketch, "E2980", {"start": v(-16.93, 25.56) * mm, "end": v(-16.97, 25.58) * mm});
            skLineSegment(sketch, "E2981", {"start": v(-16.97, 25.58) * mm, "end": v(-17.01, 25.57) * mm});
            skLineSegment(sketch, "E2982", {"start": v(-17.01, 25.57) * mm, "end": v(-17.11, 25.5) * mm});
            skLineSegment(sketch, "E2983", {"start": v(-17.11, 25.5) * mm, "end": v(-17.14, 25.46) * mm});
            skLineSegment(sketch, "E2984", {"start": v(-17.14, 25.46) * mm, "end": v(-17.14, 25.42) * mm});
            skLineSegment(sketch, "E2985", {"start": v(-17.14, 25.42) * mm, "end": v(-17.12, 25.38) * mm});
            skLineSegment(sketch, "E2986", {"start": v(-17.12, 25.38) * mm, "end": v(-17.1, 25.34) * mm});
            skLineSegment(sketch, "E2987", {"start": v(-17.1, 25.34) * mm, "end": v(-17.1, 25.3) * mm});
            skLineSegment(sketch, "E2988", {"start": v(-17.1, 25.3) * mm, "end": v(-17.1, 25.25) * mm});
            skLineSegment(sketch, "E2989", {"start": v(-17.1, 25.25) * mm, "end": v(-17.11, 25.19) * mm});
            skLineSegment(sketch, "E2990", {"start": v(-17.11, 25.19) * mm, "end": v(-17.14, 25.14) * mm});
            skLineSegment(sketch, "E2991", {"start": v(-17.14, 25.14) * mm, "end": v(-17.17, 25.1) * mm});
            skLineSegment(sketch, "E2992", {"start": v(-17.17, 25.1) * mm, "end": v(-17.22, 25.05) * mm});
            skLineSegment(sketch, "E2993", {"start": v(-17.22, 25.05) * mm, "end": v(-17.27, 25.03) * mm});
            skLineSegment(sketch, "E2994", {"start": v(-17.27, 25.03) * mm, "end": v(-17.33, 25) * mm});
            skLineSegment(sketch, "E2995", {"start": v(-17.33, 25) * mm, "end": v(-17.38, 25) * mm});
            skLineSegment(sketch, "E2996", {"start": v(-17.38, 25) * mm, "end": v(-17.44, 25.01) * mm});
            skLineSegment(sketch, "E2997", {"start": v(-17.44, 25.01) * mm, "end": v(-17.48, 25.03) * mm});
            skLineSegment(sketch, "E2998", {"start": v(-17.48, 25.03) * mm, "end": v(-17.52, 25.05) * mm});
            skLineSegment(sketch, "E2999", {"start": v(-17.52, 25.05) * mm, "end": v(-17.56, 25.08) * mm});
            skLineSegment(sketch, "E3000", {"start": v(-17.56, 25.08) * mm, "end": v(-17.59, 25.1) * mm});
            skLineSegment(sketch, "E3001", {"start": v(-17.59, 25.1) * mm, "end": v(-17.63, 25.13) * mm});
            skLineSegment(sketch, "E3002", {"start": v(-17.63, 25.13) * mm, "end": v(-17.67, 25.11) * mm});
            skLineSegment(sketch, "E3003", {"start": v(-17.67, 25.11) * mm, "end": v(-17.77, 25.04) * mm});
            skLineSegment(sketch, "E3004", {"start": v(-17.77, 25.04) * mm, "end": v(-17.8, 25) * mm});
            skLineSegment(sketch, "E3005", {"start": v(-17.8, 25) * mm, "end": v(-17.8, 24.96) * mm});
            skLineSegment(sketch, "E3006", {"start": v(-17.8, 24.96) * mm, "end": v(-17.78, 24.92) * mm});
            skLineSegment(sketch, "E3007", {"start": v(-17.78, 24.92) * mm, "end": v(-17.77, 24.88) * mm});
            skLineSegment(sketch, "E3008", {"start": v(-17.77, 24.88) * mm, "end": v(-17.76, 24.83) * mm});
            skLineSegment(sketch, "E3009", {"start": v(-17.76, 24.83) * mm, "end": v(-17.76, 24.79) * mm});
            skLineSegment(sketch, "E3010", {"start": v(-17.76, 24.79) * mm, "end": v(-17.77, 24.73) * mm});
            skLineSegment(sketch, "E3011", {"start": v(-17.77, 24.73) * mm, "end": v(-17.8, 24.68) * mm});
            skLineSegment(sketch, "E3012", {"start": v(-17.8, 24.68) * mm, "end": v(-17.83, 24.63) * mm});
            skLineSegment(sketch, "E3013", {"start": v(-17.83, 24.63) * mm, "end": v(-17.87, 24.6) * mm});
            skLineSegment(sketch, "E3014", {"start": v(-17.87, 24.6) * mm, "end": v(-17.92, 24.56) * mm});
            skLineSegment(sketch, "E3015", {"start": v(-17.92, 24.56) * mm, "end": v(-17.97, 24.55) * mm});
            skLineSegment(sketch, "E3016", {"start": v(-17.97, 24.55) * mm, "end": v(-18.03, 24.54) * mm});
            skLineSegment(sketch, "E3017", {"start": v(-18.03, 24.54) * mm, "end": v(-18.09, 24.55) * mm});
            skLineSegment(sketch, "E3018", {"start": v(-18.09, 24.55) * mm, "end": v(-18.13, 24.56) * mm});
            skLineSegment(sketch, "E3019", {"start": v(-18.13, 24.56) * mm, "end": v(-18.17, 24.58) * mm});
            skLineSegment(sketch, "E3020", {"start": v(-18.17, 24.58) * mm, "end": v(-18.2, 24.61) * mm});
            skLineSegment(sketch, "E3021", {"start": v(-18.2, 24.61) * mm, "end": v(-18.24, 24.64) * mm});
            skLineSegment(sketch, "E3022", {"start": v(-18.24, 24.64) * mm, "end": v(-18.28, 24.66) * mm});
            skLineSegment(sketch, "E3023", {"start": v(-18.28, 24.66) * mm, "end": v(-18.33, 24.64) * mm});
            skLineSegment(sketch, "E3024", {"start": v(-18.33, 24.64) * mm, "end": v(-18.42, 24.57) * mm});
            skLineSegment(sketch, "E3025", {"start": v(-18.42, 24.57) * mm, "end": v(-18.45, 24.53) * mm});
            skLineSegment(sketch, "E3026", {"start": v(-18.45, 24.53) * mm, "end": v(-18.45, 24.49) * mm});
            skLineSegment(sketch, "E3027", {"start": v(-18.45, 24.49) * mm, "end": v(-18.43, 24.45) * mm});
            skLineSegment(sketch, "E3028", {"start": v(-18.43, 24.45) * mm, "end": v(-18.41, 24.4) * mm});
            skLineSegment(sketch, "E3029", {"start": v(-18.41, 24.4) * mm, "end": v(-18.4, 24.36) * mm});
            skLineSegment(sketch, "E3030", {"start": v(-18.4, 24.36) * mm, "end": v(-18.4, 24.32) * mm});
            skLineSegment(sketch, "E3031", {"start": v(-18.4, 24.32) * mm, "end": v(-18.4, 24.26) * mm});
            skLineSegment(sketch, "E3032", {"start": v(-18.4, 24.26) * mm, "end": v(-18.43, 24.2) * mm});
            skLineSegment(sketch, "E3033", {"start": v(-18.43, 24.2) * mm, "end": v(-18.46, 24.16) * mm});
            skLineSegment(sketch, "E3034", {"start": v(-18.46, 24.16) * mm, "end": v(-18.5, 24.12) * mm});
            skLineSegment(sketch, "E3035", {"start": v(-18.5, 24.12) * mm, "end": v(-18.56, 24.09) * mm});
            skLineSegment(sketch, "E3036", {"start": v(-18.56, 24.09) * mm, "end": v(-18.61, 24.07) * mm});
            skLineSegment(sketch, "E3037", {"start": v(-18.61, 24.07) * mm, "end": v(-18.67, 24.06) * mm});
            skLineSegment(sketch, "E3038", {"start": v(-18.67, 24.06) * mm, "end": v(-18.73, 24.06) * mm});
            skLineSegment(sketch, "E3039", {"start": v(-18.73, 24.06) * mm, "end": v(-18.77, 24.08) * mm});
            skLineSegment(sketch, "E3040", {"start": v(-18.77, 24.08) * mm, "end": v(-18.8, 24.1) * mm});
            skLineSegment(sketch, "E3041", {"start": v(-18.8, 24.1) * mm, "end": v(-18.85, 24.13) * mm});
            skLineSegment(sketch, "E3042", {"start": v(-18.85, 24.13) * mm, "end": v(-18.88, 24.15) * mm});
            skLineSegment(sketch, "E3043", {"start": v(-18.88, 24.15) * mm, "end": v(-18.92, 24.17) * mm});
            skLineSegment(sketch, "E3044", {"start": v(-18.92, 24.17) * mm, "end": v(-18.96, 24.15) * mm});
            skLineSegment(sketch, "E3045", {"start": v(-18.96, 24.15) * mm, "end": v(-19.06, 24.08) * mm});
            skLineSegment(sketch, "E3046", {"start": v(-19.06, 24.08) * mm, "end": v(-19.09, 24.04) * mm});
            skLineSegment(sketch, "E3047", {"start": v(-19.09, 24.04) * mm, "end": v(-19.08, 24) * mm});
            skLineSegment(sketch, "E3048", {"start": v(-19.08, 24) * mm, "end": v(-19.06, 23.96) * mm});
            skLineSegment(sketch, "E3049", {"start": v(-19.06, 23.96) * mm, "end": v(-19.04, 23.92) * mm});
            skLineSegment(sketch, "E3050", {"start": v(-19.04, 23.92) * mm, "end": v(-19.03, 23.87) * mm});
            skLineSegment(sketch, "E3051", {"start": v(-19.03, 23.87) * mm, "end": v(-19.03, 23.83) * mm});
            skLineSegment(sketch, "E3052", {"start": v(-19.03, 23.83) * mm, "end": v(-19.04, 23.77) * mm});
            skLineSegment(sketch, "E3053", {"start": v(-19.04, 23.77) * mm, "end": v(-19.06, 23.71) * mm});
            skLineSegment(sketch, "E3054", {"start": v(-19.06, 23.71) * mm, "end": v(-19.09, 23.67) * mm});
            skLineSegment(sketch, "E3055", {"start": v(-19.09, 23.67) * mm, "end": v(-19.13, 23.63) * mm});
            skLineSegment(sketch, "E3056", {"start": v(-19.13, 23.63) * mm, "end": v(-19.18, 23.6) * mm});
            skLineSegment(sketch, "E3057", {"start": v(-19.18, 23.6) * mm, "end": v(-19.23, 23.57) * mm});
            skLineSegment(sketch, "E3058", {"start": v(-19.23, 23.57) * mm, "end": v(-19.3, 23.56) * mm});
            skLineSegment(sketch, "E3059", {"start": v(-19.3, 23.56) * mm, "end": v(-19.35, 23.57) * mm});
            skLineSegment(sketch, "E3060", {"start": v(-19.35, 23.57) * mm, "end": v(-19.4, 23.58) * mm});
            skLineSegment(sketch, "E3061", {"start": v(-19.4, 23.58) * mm, "end": v(-19.43, 23.6) * mm});
            skLineSegment(sketch, "E3062", {"start": v(-19.43, 23.6) * mm, "end": v(-19.47, 23.62) * mm});
            skLineSegment(sketch, "E3063", {"start": v(-19.47, 23.62) * mm, "end": v(-19.5, 23.65) * mm});
            skLineSegment(sketch, "E3064", {"start": v(-19.5, 23.65) * mm, "end": v(-19.55, 23.67) * mm});
            skLineSegment(sketch, "E3065", {"start": v(-19.55, 23.67) * mm, "end": v(-19.6, 23.65) * mm});
            skLineSegment(sketch, "E3066", {"start": v(-19.6, 23.65) * mm, "end": v(-19.68, 23.57) * mm});
            skLineSegment(sketch, "E3067", {"start": v(-19.68, 23.57) * mm, "end": v(-19.7, 23.53) * mm});
            skLineSegment(sketch, "E3068", {"start": v(-19.7, 23.53) * mm, "end": v(-19.7, 23.49) * mm});
            skLineSegment(sketch, "E3069", {"start": v(-19.7, 23.49) * mm, "end": v(-19.68, 23.45) * mm});
            skLineSegment(sketch, "E3070", {"start": v(-19.68, 23.45) * mm, "end": v(-19.66, 23.4) * mm});
            skLineSegment(sketch, "E3071", {"start": v(-19.66, 23.4) * mm, "end": v(-19.65, 23.36) * mm});
            skLineSegment(sketch, "E3072", {"start": v(-19.65, 23.36) * mm, "end": v(-19.65, 23.32) * mm});
            skLineSegment(sketch, "E3073", {"start": v(-19.65, 23.32) * mm, "end": v(-19.65, 23.26) * mm});
            skLineSegment(sketch, "E3074", {"start": v(-19.65, 23.26) * mm, "end": v(-19.67, 23.2) * mm});
            skLineSegment(sketch, "E3075", {"start": v(-19.67, 23.2) * mm, "end": v(-19.7, 23.16) * mm});
            skLineSegment(sketch, "E3076", {"start": v(-19.7, 23.16) * mm, "end": v(-19.74, 23.12) * mm});
            skLineSegment(sketch, "E3077", {"start": v(-19.74, 23.12) * mm, "end": v(-19.8, 23.08) * mm});
            skLineSegment(sketch, "E3078", {"start": v(-19.8, 23.08) * mm, "end": v(-19.84, 23.06) * mm});
            skLineSegment(sketch, "E3079", {"start": v(-19.84, 23.06) * mm, "end": v(-19.9, 23.05) * mm});
            skLineSegment(sketch, "E3080", {"start": v(-19.9, 23.05) * mm, "end": v(-19.96, 23.05) * mm});
            skLineSegment(sketch, "E3081", {"start": v(-19.96, 23.05) * mm, "end": v(-20, 23.07) * mm});
            skLineSegment(sketch, "E3082", {"start": v(-20, 23.07) * mm, "end": v(-20.04, 23.08) * mm});
            skLineSegment(sketch, "E3083", {"start": v(-20.04, 23.08) * mm, "end": v(-20.08, 23.1) * mm});
            skLineSegment(sketch, "E3084", {"start": v(-20.08, 23.1) * mm, "end": v(-20.12, 23.13) * mm});
            skLineSegment(sketch, "E3085", {"start": v(-20.12, 23.13) * mm, "end": v(-20.16, 23.15) * mm});
            skLineSegment(sketch, "E3086", {"start": v(-20.16, 23.15) * mm, "end": v(-20.2, 23.13) * mm});
            skLineSegment(sketch, "E3087", {"start": v(-20.2, 23.13) * mm, "end": v(-20.3, 23.05) * mm});
            skLineSegment(sketch, "E3088", {"start": v(-20.3, 23.05) * mm, "end": v(-20.32, 23) * mm});
            skLineSegment(sketch, "E3089", {"start": v(-20.32, 23) * mm, "end": v(-20.3, 22.96) * mm});
            skLineSegment(sketch, "E3090", {"start": v(-20.3, 22.96) * mm, "end": v(-20.29, 22.93) * mm});
            skLineSegment(sketch, "E3091", {"start": v(-20.29, 22.93) * mm, "end": v(-20.27, 22.89) * mm});
            skLineSegment(sketch, "E3092", {"start": v(-20.27, 22.89) * mm, "end": v(-20.26, 22.84) * mm});
            skLineSegment(sketch, "E3093", {"start": v(-20.26, 22.84) * mm, "end": v(-20.25, 22.8) * mm});
            skLineSegment(sketch, "E3094", {"start": v(-20.25, 22.8) * mm, "end": v(-20.25, 22.74) * mm});
            skLineSegment(sketch, "E3095", {"start": v(-20.25, 22.74) * mm, "end": v(-20.27, 22.68) * mm});
            skLineSegment(sketch, "E3096", {"start": v(-20.27, 22.68) * mm, "end": v(-20.3, 22.64) * mm});
            skLineSegment(sketch, "E3097", {"start": v(-20.3, 22.64) * mm, "end": v(-20.34, 22.6) * mm});
            skLineSegment(sketch, "E3098", {"start": v(-20.34, 22.6) * mm, "end": v(-20.39, 22.56) * mm});
            skLineSegment(sketch, "E3099", {"start": v(-20.39, 22.56) * mm, "end": v(-20.44, 22.53) * mm});
            skLineSegment(sketch, "E3100", {"start": v(-20.44, 22.53) * mm, "end": v(-20.5, 22.52) * mm});
            skLineSegment(sketch, "E3101", {"start": v(-20.5, 22.52) * mm, "end": v(-20.56, 22.52) * mm});
            skLineSegment(sketch, "E3102", {"start": v(-20.56, 22.52) * mm, "end": v(-20.6, 22.53) * mm});
            skLineSegment(sketch, "E3103", {"start": v(-20.6, 22.53) * mm, "end": v(-20.64, 22.55) * mm});
            skLineSegment(sketch, "E3104", {"start": v(-20.64, 22.55) * mm, "end": v(-20.68, 22.57) * mm});
            skLineSegment(sketch, "E3105", {"start": v(-20.68, 22.57) * mm, "end": v(-20.72, 22.6) * mm});
            skLineSegment(sketch, "E3106", {"start": v(-20.72, 22.6) * mm, "end": v(-20.76, 22.61) * mm});
            skLineSegment(sketch, "E3107", {"start": v(-20.76, 22.61) * mm, "end": v(-20.8, 22.6) * mm});
            skLineSegment(sketch, "E3108", {"start": v(-20.8, 22.6) * mm, "end": v(-20.9, 22.51) * mm});
            skLineSegment(sketch, "E3109", {"start": v(-20.9, 22.51) * mm, "end": v(-20.91, 22.47) * mm});
            skLineSegment(sketch, "E3110", {"start": v(-20.91, 22.47) * mm, "end": v(-20.9, 22.43) * mm});
            skLineSegment(sketch, "E3111", {"start": v(-20.9, 22.43) * mm, "end": v(-20.88, 22.39) * mm});
            skLineSegment(sketch, "E3112", {"start": v(-20.88, 22.39) * mm, "end": v(-20.86, 22.35) * mm});
            skLineSegment(sketch, "E3113", {"start": v(-20.86, 22.35) * mm, "end": v(-20.85, 22.3) * mm});
            skLineSegment(sketch, "E3114", {"start": v(-20.85, 22.3) * mm, "end": v(-20.84, 22.26) * mm});
            skLineSegment(sketch, "E3115", {"start": v(-20.84, 22.26) * mm, "end": v(-20.84, 22.2) * mm});
            skLineSegment(sketch, "E3116", {"start": v(-20.84, 22.2) * mm, "end": v(-20.86, 22.15) * mm});
            skLineSegment(sketch, "E3117", {"start": v(-20.86, 22.15) * mm, "end": v(-20.89, 22.1) * mm});
            skLineSegment(sketch, "E3118", {"start": v(-20.89, 22.1) * mm, "end": v(-20.93, 22.05) * mm});
            skLineSegment(sketch, "E3119", {"start": v(-20.93, 22.05) * mm, "end": v(-20.97, 22.02) * mm});
            skLineSegment(sketch, "E3120", {"start": v(-20.97, 22.02) * mm, "end": v(-21.02, 22) * mm});
            skLineSegment(sketch, "E3121", {"start": v(-21.02, 22) * mm, "end": v(-21.08, 21.98) * mm});
            skLineSegment(sketch, "E3122", {"start": v(-21.08, 21.98) * mm, "end": v(-21.14, 21.98) * mm});
            skLineSegment(sketch, "E3123", {"start": v(-21.14, 21.98) * mm, "end": v(-21.18, 21.99) * mm});
            skLineSegment(sketch, "E3124", {"start": v(-21.18, 21.99) * mm, "end": v(-21.22, 22) * mm});
            skLineSegment(sketch, "E3125", {"start": v(-21.22, 22) * mm, "end": v(-21.26, 22.02) * mm});
            skLineSegment(sketch, "E3126", {"start": v(-21.26, 22.02) * mm, "end": v(-21.3, 22.05) * mm});
            skLineSegment(sketch, "E3127", {"start": v(-21.3, 22.05) * mm, "end": v(-21.34, 22.06) * mm});
            skLineSegment(sketch, "E3128", {"start": v(-21.34, 22.06) * mm, "end": v(-21.39, 22.04) * mm});
            skLineSegment(sketch, "E3129", {"start": v(-21.39, 22.04) * mm, "end": v(-21.47, 21.96) * mm});
            skLineSegment(sketch, "E3130", {"start": v(-21.47, 21.96) * mm, "end": v(-21.5, 21.91) * mm});
            skLineSegment(sketch, "E3131", {"start": v(-21.5, 21.91) * mm, "end": v(-21.48, 21.87) * mm});
            skLineSegment(sketch, "E3132", {"start": v(-21.48, 21.87) * mm, "end": v(-21.46, 21.83) * mm});
            skLineSegment(sketch, "E3133", {"start": v(-21.46, 21.83) * mm, "end": v(-21.44, 21.8) * mm});
            skLineSegment(sketch, "E3134", {"start": v(-21.44, 21.8) * mm, "end": v(-21.42, 21.75) * mm});
            skLineSegment(sketch, "E3135", {"start": v(-21.42, 21.75) * mm, "end": v(-21.41, 21.7) * mm});
            skLineSegment(sketch, "E3136", {"start": v(-21.41, 21.7) * mm, "end": v(-21.42, 21.65) * mm});
            skLineSegment(sketch, "E3137", {"start": v(-21.42, 21.65) * mm, "end": v(-21.43, 21.6) * mm});
            skLineSegment(sketch, "E3138", {"start": v(-21.43, 21.6) * mm, "end": v(-21.46, 21.54) * mm});
            skLineSegment(sketch, "E3139", {"start": v(-21.46, 21.54) * mm, "end": v(-21.5, 21.5) * mm});
            skLineSegment(sketch, "E3140", {"start": v(-21.5, 21.5) * mm, "end": v(-21.54, 21.46) * mm});
            skLineSegment(sketch, "E3141", {"start": v(-21.54, 21.46) * mm, "end": v(-21.6, 21.43) * mm});
            skLineSegment(sketch, "E3142", {"start": v(-21.6, 21.43) * mm, "end": v(-21.65, 21.42) * mm});
            skLineSegment(sketch, "E3143", {"start": v(-21.65, 21.42) * mm, "end": v(-21.7, 21.41) * mm});
            skLineSegment(sketch, "E3144", {"start": v(-21.7, 21.41) * mm, "end": v(-21.75, 21.42) * mm});
            skLineSegment(sketch, "E3145", {"start": v(-21.75, 21.42) * mm, "end": v(-21.8, 21.44) * mm});
            skLineSegment(sketch, "E3146", {"start": v(-21.8, 21.44) * mm, "end": v(-21.83, 21.46) * mm});
            skLineSegment(sketch, "E3147", {"start": v(-21.83, 21.46) * mm, "end": v(-21.87, 21.48) * mm});
            skLineSegment(sketch, "E3148", {"start": v(-21.87, 21.48) * mm, "end": v(-21.91, 21.5) * mm});
            skLineSegment(sketch, "E3149", {"start": v(-21.91, 21.5) * mm, "end": v(-21.96, 21.47) * mm});
            skLineSegment(sketch, "E3150", {"start": v(-21.96, 21.47) * mm, "end": v(-22.04, 21.39) * mm});
            skLineSegment(sketch, "E3151", {"start": v(-22.04, 21.39) * mm, "end": v(-22.06, 21.34) * mm});
            skLineSegment(sketch, "E3152", {"start": v(-22.06, 21.34) * mm, "end": v(-22.05, 21.3) * mm});
            skLineSegment(sketch, "E3153", {"start": v(-22.05, 21.3) * mm, "end": v(-22.02, 21.26) * mm});
            skLineSegment(sketch, "E3154", {"start": v(-22.02, 21.26) * mm, "end": v(-22, 21.22) * mm});
            skLineSegment(sketch, "E3155", {"start": v(-22, 21.22) * mm, "end": v(-21.99, 21.18) * mm});
            skLineSegment(sketch, "E3156", {"start": v(-21.99, 21.18) * mm, "end": v(-21.98, 21.14) * mm});
            skLineSegment(sketch, "E3157", {"start": v(-21.98, 21.14) * mm, "end": v(-21.98, 21.08) * mm});
            skLineSegment(sketch, "E3158", {"start": v(-21.98, 21.08) * mm, "end": v(-22, 21.02) * mm});
            skLineSegment(sketch, "E3159", {"start": v(-22, 21.02) * mm, "end": v(-22.02, 20.97) * mm});
            skLineSegment(sketch, "E3160", {"start": v(-22.02, 20.97) * mm, "end": v(-22.05, 20.93) * mm});
            skLineSegment(sketch, "E3161", {"start": v(-22.05, 20.93) * mm, "end": v(-22.1, 20.89) * mm});
            skLineSegment(sketch, "E3162", {"start": v(-22.1, 20.89) * mm, "end": v(-22.15, 20.86) * mm});
            skLineSegment(sketch, "E3163", {"start": v(-22.15, 20.86) * mm, "end": v(-22.2, 20.84) * mm});
            skLineSegment(sketch, "E3164", {"start": v(-22.2, 20.84) * mm, "end": v(-22.26, 20.84) * mm});
            skLineSegment(sketch, "E3165", {"start": v(-22.26, 20.84) * mm, "end": v(-22.3, 20.85) * mm});
            skLineSegment(sketch, "E3166", {"start": v(-22.3, 20.85) * mm, "end": v(-22.35, 20.86) * mm});
            skLineSegment(sketch, "E3167", {"start": v(-22.35, 20.86) * mm, "end": v(-22.39, 20.88) * mm});
            skLineSegment(sketch, "E3168", {"start": v(-22.39, 20.88) * mm, "end": v(-22.43, 20.9) * mm});
            skLineSegment(sketch, "E3169", {"start": v(-22.43, 20.9) * mm, "end": v(-22.47, 20.91) * mm});
            skLineSegment(sketch, "E3170", {"start": v(-22.47, 20.91) * mm, "end": v(-22.51, 20.9) * mm});
            skLineSegment(sketch, "E3171", {"start": v(-22.51, 20.9) * mm, "end": v(-22.6, 20.8) * mm});
            skLineSegment(sketch, "E3172", {"start": v(-22.6, 20.8) * mm, "end": v(-22.61, 20.76) * mm});
            skLineSegment(sketch, "E3173", {"start": v(-22.61, 20.76) * mm, "end": v(-22.6, 20.72) * mm});
            skLineSegment(sketch, "E3174", {"start": v(-22.6, 20.72) * mm, "end": v(-22.57, 20.68) * mm});
            skLineSegment(sketch, "E3175", {"start": v(-22.57, 20.68) * mm, "end": v(-22.55, 20.64) * mm});
            skLineSegment(sketch, "E3176", {"start": v(-22.55, 20.64) * mm, "end": v(-22.53, 20.6) * mm});
            skLineSegment(sketch, "E3177", {"start": v(-22.53, 20.6) * mm, "end": v(-22.52, 20.56) * mm});
            skLineSegment(sketch, "E3178", {"start": v(-22.52, 20.56) * mm, "end": v(-22.52, 20.5) * mm});
            skLineSegment(sketch, "E3179", {"start": v(-22.52, 20.5) * mm, "end": v(-22.53, 20.44) * mm});
            skLineSegment(sketch, "E3180", {"start": v(-22.53, 20.44) * mm, "end": v(-22.56, 20.39) * mm});
            skLineSegment(sketch, "E3181", {"start": v(-22.56, 20.39) * mm, "end": v(-22.6, 20.34) * mm});
            skLineSegment(sketch, "E3182", {"start": v(-22.6, 20.34) * mm, "end": v(-22.64, 20.3) * mm});
            skLineSegment(sketch, "E3183", {"start": v(-22.64, 20.3) * mm, "end": v(-22.68, 20.27) * mm});
            skLineSegment(sketch, "E3184", {"start": v(-22.68, 20.27) * mm, "end": v(-22.74, 20.25) * mm});
            skLineSegment(sketch, "E3185", {"start": v(-22.74, 20.25) * mm, "end": v(-22.8, 20.25) * mm});
            skLineSegment(sketch, "E3186", {"start": v(-22.8, 20.25) * mm, "end": v(-22.84, 20.26) * mm});
            skLineSegment(sketch, "E3187", {"start": v(-22.84, 20.26) * mm, "end": v(-22.89, 20.27) * mm});
            skLineSegment(sketch, "E3188", {"start": v(-22.89, 20.27) * mm, "end": v(-22.93, 20.29) * mm});
            skLineSegment(sketch, "E3189", {"start": v(-22.93, 20.29) * mm, "end": v(-22.96, 20.3) * mm});
            skLineSegment(sketch, "E3190", {"start": v(-22.96, 20.3) * mm, "end": v(-23, 20.32) * mm});
            skLineSegment(sketch, "E3191", {"start": v(-23, 20.32) * mm, "end": v(-23.05, 20.3) * mm});
            skLineSegment(sketch, "E3192", {"start": v(-23.05, 20.3) * mm, "end": v(-23.13, 20.2) * mm});
            skLineSegment(sketch, "E3193", {"start": v(-23.13, 20.2) * mm, "end": v(-23.15, 20.16) * mm});
            skLineSegment(sketch, "E3194", {"start": v(-23.15, 20.16) * mm, "end": v(-23.13, 20.12) * mm});
            skLineSegment(sketch, "E3195", {"start": v(-23.13, 20.12) * mm, "end": v(-23.1, 20.08) * mm});
            skLineSegment(sketch, "E3196", {"start": v(-23.1, 20.08) * mm, "end": v(-23.08, 20.04) * mm});
            skLineSegment(sketch, "E3197", {"start": v(-23.08, 20.04) * mm, "end": v(-23.07, 20) * mm});
            skLineSegment(sketch, "E3198", {"start": v(-23.07, 20) * mm, "end": v(-23.05, 19.96) * mm});
            skLineSegment(sketch, "E3199", {"start": v(-23.05, 19.96) * mm, "end": v(-23.05, 19.9) * mm});
            skLineSegment(sketch, "E3200", {"start": v(-23.05, 19.9) * mm, "end": v(-23.06, 19.84) * mm});
            skLineSegment(sketch, "E3201", {"start": v(-23.06, 19.84) * mm, "end": v(-23.08, 19.8) * mm});
            skLineSegment(sketch, "E3202", {"start": v(-23.08, 19.8) * mm, "end": v(-23.12, 19.74) * mm});
            skLineSegment(sketch, "E3203", {"start": v(-23.12, 19.74) * mm, "end": v(-23.16, 19.7) * mm});
            skLineSegment(sketch, "E3204", {"start": v(-23.16, 19.7) * mm, "end": v(-23.2, 19.67) * mm});
            skLineSegment(sketch, "E3205", {"start": v(-23.2, 19.67) * mm, "end": v(-23.26, 19.65) * mm});
            skLineSegment(sketch, "E3206", {"start": v(-23.26, 19.65) * mm, "end": v(-23.32, 19.65) * mm});
            skLineSegment(sketch, "E3207", {"start": v(-23.32, 19.65) * mm, "end": v(-23.36, 19.65) * mm});
            skLineSegment(sketch, "E3208", {"start": v(-23.36, 19.65) * mm, "end": v(-23.4, 19.66) * mm});
            skLineSegment(sketch, "E3209", {"start": v(-23.4, 19.66) * mm, "end": v(-23.45, 19.68) * mm});
            skLineSegment(sketch, "E3210", {"start": v(-23.45, 19.68) * mm, "end": v(-23.49, 19.7) * mm});
            skLineSegment(sketch, "E3211", {"start": v(-23.49, 19.7) * mm, "end": v(-23.53, 19.7) * mm});
            skLineSegment(sketch, "E3212", {"start": v(-23.53, 19.7) * mm, "end": v(-23.57, 19.68) * mm});
            skLineSegment(sketch, "E3213", {"start": v(-23.57, 19.68) * mm, "end": v(-23.65, 19.6) * mm});
            skLineSegment(sketch, "E3214", {"start": v(-23.65, 19.6) * mm, "end": v(-23.67, 19.55) * mm});
            skLineSegment(sketch, "E3215", {"start": v(-23.67, 19.55) * mm, "end": v(-23.65, 19.5) * mm});
            skLineSegment(sketch, "E3216", {"start": v(-23.65, 19.5) * mm, "end": v(-23.62, 19.47) * mm});
            skLineSegment(sketch, "E3217", {"start": v(-23.62, 19.47) * mm, "end": v(-23.6, 19.43) * mm});
            skLineSegment(sketch, "E3218", {"start": v(-23.6, 19.43) * mm, "end": v(-23.58, 19.4) * mm});
            skLineSegment(sketch, "E3219", {"start": v(-23.58, 19.4) * mm, "end": v(-23.57, 19.35) * mm});
            skLineSegment(sketch, "E3220", {"start": v(-23.57, 19.35) * mm, "end": v(-23.56, 19.3) * mm});
            skLineSegment(sketch, "E3221", {"start": v(-23.56, 19.3) * mm, "end": v(-23.57, 19.23) * mm});
            skLineSegment(sketch, "E3222", {"start": v(-23.57, 19.23) * mm, "end": v(-23.6, 19.18) * mm});
            skLineSegment(sketch, "E3223", {"start": v(-23.6, 19.18) * mm, "end": v(-23.63, 19.13) * mm});
            skLineSegment(sketch, "E3224", {"start": v(-23.63, 19.13) * mm, "end": v(-23.67, 19.09) * mm});
            skLineSegment(sketch, "E3225", {"start": v(-23.67, 19.09) * mm, "end": v(-23.71, 19.06) * mm});
            skLineSegment(sketch, "E3226", {"start": v(-23.71, 19.06) * mm, "end": v(-23.77, 19.04) * mm});
            skLineSegment(sketch, "E3227", {"start": v(-23.77, 19.04) * mm, "end": v(-23.83, 19.03) * mm});
            skLineSegment(sketch, "E3228", {"start": v(-23.83, 19.03) * mm, "end": v(-23.87, 19.03) * mm});
            skLineSegment(sketch, "E3229", {"start": v(-23.87, 19.03) * mm, "end": v(-23.92, 19.04) * mm});
            skLineSegment(sketch, "E3230", {"start": v(-23.92, 19.04) * mm, "end": v(-23.96, 19.06) * mm});
            skLineSegment(sketch, "E3231", {"start": v(-23.96, 19.06) * mm, "end": v(-24, 19.08) * mm});
            skLineSegment(sketch, "E3232", {"start": v(-24, 19.08) * mm, "end": v(-24.04, 19.09) * mm});
            skLineSegment(sketch, "E3233", {"start": v(-24.04, 19.09) * mm, "end": v(-24.08, 19.06) * mm});
            skLineSegment(sketch, "E3234", {"start": v(-24.08, 19.06) * mm, "end": v(-24.15, 18.96) * mm});
            skLineSegment(sketch, "E3235", {"start": v(-24.15, 18.96) * mm, "end": v(-24.17, 18.92) * mm});
            skLineSegment(sketch, "E3236", {"start": v(-24.17, 18.92) * mm, "end": v(-24.15, 18.88) * mm});
            skLineSegment(sketch, "E3237", {"start": v(-24.15, 18.88) * mm, "end": v(-24.13, 18.85) * mm});
            skLineSegment(sketch, "E3238", {"start": v(-24.13, 18.85) * mm, "end": v(-24.1, 18.8) * mm});
            skLineSegment(sketch, "E3239", {"start": v(-24.1, 18.8) * mm, "end": v(-24.08, 18.77) * mm});
            skLineSegment(sketch, "E3240", {"start": v(-24.08, 18.77) * mm, "end": v(-24.06, 18.73) * mm});
            skLineSegment(sketch, "E3241", {"start": v(-24.06, 18.73) * mm, "end": v(-24.06, 18.67) * mm});
            skLineSegment(sketch, "E3242", {"start": v(-24.06, 18.67) * mm, "end": v(-24.07, 18.61) * mm});
            skLineSegment(sketch, "E3243", {"start": v(-24.07, 18.61) * mm, "end": v(-24.09, 18.56) * mm});
            skLineSegment(sketch, "E3244", {"start": v(-24.09, 18.56) * mm, "end": v(-24.12, 18.5) * mm});
            skLineSegment(sketch, "E3245", {"start": v(-24.12, 18.5) * mm, "end": v(-24.16, 18.46) * mm});
            skLineSegment(sketch, "E3246", {"start": v(-24.16, 18.46) * mm, "end": v(-24.2, 18.43) * mm});
            skLineSegment(sketch, "E3247", {"start": v(-24.2, 18.43) * mm, "end": v(-24.26, 18.4) * mm});
            skLineSegment(sketch, "E3248", {"start": v(-24.26, 18.4) * mm, "end": v(-24.32, 18.4) * mm});
            skLineSegment(sketch, "E3249", {"start": v(-24.32, 18.4) * mm, "end": v(-24.36, 18.4) * mm});
            skLineSegment(sketch, "E3250", {"start": v(-24.36, 18.4) * mm, "end": v(-24.4, 18.41) * mm});
            skLineSegment(sketch, "E3251", {"start": v(-24.4, 18.41) * mm, "end": v(-24.45, 18.43) * mm});
            skLineSegment(sketch, "E3252", {"start": v(-24.45, 18.43) * mm, "end": v(-24.49, 18.45) * mm});
            skLineSegment(sketch, "E3253", {"start": v(-24.49, 18.45) * mm, "end": v(-24.53, 18.45) * mm});
            skLineSegment(sketch, "E3254", {"start": v(-24.53, 18.45) * mm, "end": v(-24.57, 18.42) * mm});
            skLineSegment(sketch, "E3255", {"start": v(-24.57, 18.42) * mm, "end": v(-24.64, 18.33) * mm});
            skLineSegment(sketch, "E3256", {"start": v(-24.64, 18.33) * mm, "end": v(-24.66, 18.28) * mm});
            skLineSegment(sketch, "E3257", {"start": v(-24.66, 18.28) * mm, "end": v(-24.64, 18.24) * mm});
            skLineSegment(sketch, "E3258", {"start": v(-24.64, 18.24) * mm, "end": v(-24.61, 18.2) * mm});
            skLineSegment(sketch, "E3259", {"start": v(-24.61, 18.2) * mm, "end": v(-24.58, 18.17) * mm});
            skLineSegment(sketch, "E3260", {"start": v(-24.58, 18.17) * mm, "end": v(-24.56, 18.13) * mm});
            skLineSegment(sketch, "E3261", {"start": v(-24.56, 18.13) * mm, "end": v(-24.55, 18.09) * mm});
            skLineSegment(sketch, "E3262", {"start": v(-24.55, 18.09) * mm, "end": v(-24.54, 18.03) * mm});
            skLineSegment(sketch, "E3263", {"start": v(-24.54, 18.03) * mm, "end": v(-24.55, 17.97) * mm});
            skLineSegment(sketch, "E3264", {"start": v(-24.55, 17.97) * mm, "end": v(-24.56, 17.92) * mm});
            skLineSegment(sketch, "E3265", {"start": v(-24.56, 17.92) * mm, "end": v(-24.6, 17.87) * mm});
            skLineSegment(sketch, "E3266", {"start": v(-24.6, 17.87) * mm, "end": v(-24.63, 17.83) * mm});
            skLineSegment(sketch, "E3267", {"start": v(-24.63, 17.83) * mm, "end": v(-24.68, 17.8) * mm});
            skLineSegment(sketch, "E3268", {"start": v(-24.68, 17.8) * mm, "end": v(-24.73, 17.77) * mm});
            skLineSegment(sketch, "E3269", {"start": v(-24.73, 17.77) * mm, "end": v(-24.79, 17.76) * mm});
            skLineSegment(sketch, "E3270", {"start": v(-24.79, 17.76) * mm, "end": v(-24.83, 17.76) * mm});
            skLineSegment(sketch, "E3271", {"start": v(-24.83, 17.76) * mm, "end": v(-24.88, 17.77) * mm});
            skLineSegment(sketch, "E3272", {"start": v(-24.88, 17.77) * mm, "end": v(-24.92, 17.78) * mm});
            skLineSegment(sketch, "E3273", {"start": v(-24.92, 17.78) * mm, "end": v(-24.96, 17.8) * mm});
            skLineSegment(sketch, "E3274", {"start": v(-24.96, 17.8) * mm, "end": v(-25, 17.8) * mm});
            skLineSegment(sketch, "E3275", {"start": v(-25, 17.8) * mm, "end": v(-25.04, 17.77) * mm});
            skLineSegment(sketch, "E3276", {"start": v(-25.04, 17.77) * mm, "end": v(-25.11, 17.67) * mm});
            skLineSegment(sketch, "E3277", {"start": v(-25.11, 17.67) * mm, "end": v(-25.13, 17.63) * mm});
            skLineSegment(sketch, "E3278", {"start": v(-25.13, 17.63) * mm, "end": v(-25.1, 17.59) * mm});
            skLineSegment(sketch, "E3279", {"start": v(-25.1, 17.59) * mm, "end": v(-25.08, 17.56) * mm});
            skLineSegment(sketch, "E3280", {"start": v(-25.08, 17.56) * mm, "end": v(-25.05, 17.52) * mm});
            skLineSegment(sketch, "E3281", {"start": v(-25.05, 17.52) * mm, "end": v(-25.03, 17.48) * mm});
            skLineSegment(sketch, "E3282", {"start": v(-25.03, 17.48) * mm, "end": v(-25.01, 17.44) * mm});
            skLineSegment(sketch, "E3283", {"start": v(-25.01, 17.44) * mm, "end": v(-25, 17.38) * mm});
            skLineSegment(sketch, "E3284", {"start": v(-25, 17.38) * mm, "end": v(-25, 17.33) * mm});
            skLineSegment(sketch, "E3285", {"start": v(-25, 17.33) * mm, "end": v(-25.03, 17.27) * mm});
            skLineSegment(sketch, "E3286", {"start": v(-25.03, 17.27) * mm, "end": v(-25.05, 17.22) * mm});
            skLineSegment(sketch, "E3287", {"start": v(-25.05, 17.22) * mm, "end": v(-25.1, 17.17) * mm});
            skLineSegment(sketch, "E3288", {"start": v(-25.1, 17.17) * mm, "end": v(-25.14, 17.14) * mm});
            skLineSegment(sketch, "E3289", {"start": v(-25.14, 17.14) * mm, "end": v(-25.19, 17.11) * mm});
            skLineSegment(sketch, "E3290", {"start": v(-25.19, 17.11) * mm, "end": v(-25.25, 17.1) * mm});
            skLineSegment(sketch, "E3291", {"start": v(-25.25, 17.1) * mm, "end": v(-25.3, 17.1) * mm});
            skLineSegment(sketch, "E3292", {"start": v(-25.3, 17.1) * mm, "end": v(-25.34, 17.1) * mm});
            skLineSegment(sketch, "E3293", {"start": v(-25.34, 17.1) * mm, "end": v(-25.38, 17.12) * mm});
            skLineSegment(sketch, "E3294", {"start": v(-25.38, 17.12) * mm, "end": v(-25.42, 17.14) * mm});
            skLineSegment(sketch, "E3295", {"start": v(-25.42, 17.14) * mm, "end": v(-25.46, 17.14) * mm});
            skLineSegment(sketch, "E3296", {"start": v(-25.46, 17.14) * mm, "end": v(-25.5, 17.11) * mm});
            skLineSegment(sketch, "E3297", {"start": v(-25.5, 17.11) * mm, "end": v(-25.57, 17.01) * mm});
            skLineSegment(sketch, "E3298", {"start": v(-25.57, 17.01) * mm, "end": v(-25.58, 16.97) * mm});
            skLineSegment(sketch, "E3299", {"start": v(-25.58, 16.97) * mm, "end": v(-25.56, 16.93) * mm});
            skLineSegment(sketch, "E3300", {"start": v(-25.56, 16.93) * mm, "end": v(-25.53, 16.9) * mm});
            skLineSegment(sketch, "E3301", {"start": v(-25.53, 16.9) * mm, "end": v(-25.5, 16.86) * mm});
            skLineSegment(sketch, "E3302", {"start": v(-25.5, 16.86) * mm, "end": v(-25.48, 16.82) * mm});
            skLineSegment(sketch, "E3303", {"start": v(-25.48, 16.82) * mm, "end": v(-25.46, 16.78) * mm});
            skLineSegment(sketch, "E3304", {"start": v(-25.46, 16.78) * mm, "end": v(-25.45, 16.72) * mm});
            skLineSegment(sketch, "E3305", {"start": v(-25.45, 16.72) * mm, "end": v(-25.45, 16.67) * mm});
            skLineSegment(sketch, "E3306", {"start": v(-25.45, 16.67) * mm, "end": v(-25.47, 16.6) * mm});
            skLineSegment(sketch, "E3307", {"start": v(-25.47, 16.6) * mm, "end": v(-25.5, 16.56) * mm});
            skLineSegment(sketch, "E3308", {"start": v(-25.5, 16.56) * mm, "end": v(-25.53, 16.51) * mm});
            skLineSegment(sketch, "E3309", {"start": v(-25.53, 16.51) * mm, "end": v(-25.58, 16.47) * mm});
            skLineSegment(sketch, "E3310", {"start": v(-25.58, 16.47) * mm, "end": v(-25.63, 16.45) * mm});
            skLineSegment(sketch, "E3311", {"start": v(-25.63, 16.45) * mm, "end": v(-25.68, 16.43) * mm});
            skLineSegment(sketch, "E3312", {"start": v(-25.68, 16.43) * mm, "end": v(-25.73, 16.43) * mm});
            skLineSegment(sketch, "E3313", {"start": v(-25.73, 16.43) * mm, "end": v(-25.77, 16.44) * mm});
            skLineSegment(sketch, "E3314", {"start": v(-25.77, 16.44) * mm, "end": v(-25.82, 16.45) * mm});
            skLineSegment(sketch, "E3315", {"start": v(-25.82, 16.45) * mm, "end": v(-25.86, 16.47) * mm});
            skLineSegment(sketch, "E3316", {"start": v(-25.86, 16.47) * mm, "end": v(-25.9, 16.47) * mm});
            skLineSegment(sketch, "E3317", {"start": v(-25.9, 16.47) * mm, "end": v(-25.94, 16.44) * mm});
            skLineSegment(sketch, "E3318", {"start": v(-25.94, 16.44) * mm, "end": v(-26, 16.34) * mm});
            skLineSegment(sketch, "E3319", {"start": v(-26, 16.34) * mm, "end": v(-26.02, 16.3) * mm});
            skLineSegment(sketch, "E3320", {"start": v(-26.02, 16.3) * mm, "end": v(-26, 16.25) * mm});
            skLineSegment(sketch, "E3321", {"start": v(-26, 16.25) * mm, "end": v(-25.96, 16.22) * mm});
            skLineSegment(sketch, "E3322", {"start": v(-25.96, 16.22) * mm, "end": v(-25.93, 16.19) * mm});
            skLineSegment(sketch, "E3323", {"start": v(-25.93, 16.19) * mm, "end": v(-25.91, 16.15) * mm});
            skLineSegment(sketch, "E3324", {"start": v(-25.91, 16.15) * mm, "end": v(-25.89, 16.1) * mm});
            skLineSegment(sketch, "E3325", {"start": v(-25.89, 16.1) * mm, "end": v(-25.88, 16.05) * mm});
            skLineSegment(sketch, "E3326", {"start": v(-25.88, 16.05) * mm, "end": v(-25.88, 16) * mm});
            skLineSegment(sketch, "E3327", {"start": v(-25.88, 16) * mm, "end": v(-25.9, 15.94) * mm});
            skLineSegment(sketch, "E3328", {"start": v(-25.9, 15.94) * mm, "end": v(-25.92, 15.88) * mm});
            skLineSegment(sketch, "E3329", {"start": v(-25.92, 15.88) * mm, "end": v(-25.96, 15.84) * mm});
            skLineSegment(sketch, "E3330", {"start": v(-25.96, 15.84) * mm, "end": v(-26, 15.8) * mm});
            skLineSegment(sketch, "E3331", {"start": v(-26, 15.8) * mm, "end": v(-26.05, 15.77) * mm});
            skLineSegment(sketch, "E3332", {"start": v(-26.05, 15.77) * mm, "end": v(-26.1, 15.76) * mm});
            skLineSegment(sketch, "E3333", {"start": v(-26.1, 15.76) * mm, "end": v(-26.15, 15.75) * mm});
            skLineSegment(sketch, "E3334", {"start": v(-26.15, 15.75) * mm, "end": v(-26.2, 15.76) * mm});
            skLineSegment(sketch, "E3335", {"start": v(-26.2, 15.76) * mm, "end": v(-26.24, 15.77) * mm});
            skLineSegment(sketch, "E3336", {"start": v(-26.24, 15.77) * mm, "end": v(-26.28, 15.78) * mm});
            skLineSegment(sketch, "E3337", {"start": v(-26.28, 15.78) * mm, "end": v(-26.33, 15.78) * mm});
            skLineSegment(sketch, "E3338", {"start": v(-26.33, 15.78) * mm, "end": v(-26.36, 15.75) * mm});
            skLineSegment(sketch, "E3339", {"start": v(-26.36, 15.75) * mm, "end": v(-26.42, 15.65) * mm});
            skLineSegment(sketch, "E3340", {"start": v(-26.42, 15.65) * mm, "end": v(-26.43, 15.6) * mm});
            skLineSegment(sketch, "E3341", {"start": v(-26.43, 15.6) * mm, "end": v(-26.41, 15.56) * mm});
            skLineSegment(sketch, "E3342", {"start": v(-26.41, 15.56) * mm, "end": v(-26.38, 15.54) * mm});
            skLineSegment(sketch, "E3343", {"start": v(-26.38, 15.54) * mm, "end": v(-26.35, 15.5) * mm});
            skLineSegment(sketch, "E3344", {"start": v(-26.35, 15.5) * mm, "end": v(-26.32, 15.46) * mm});
            skLineSegment(sketch, "E3345", {"start": v(-26.32, 15.46) * mm, "end": v(-26.3, 15.42) * mm});
            skLineSegment(sketch, "E3346", {"start": v(-26.3, 15.42) * mm, "end": v(-26.3, 15.37) * mm});
            skLineSegment(sketch, "E3347", {"start": v(-26.3, 15.37) * mm, "end": v(-26.3, 15.31) * mm});
            skLineSegment(sketch, "E3348", {"start": v(-26.3, 15.31) * mm, "end": v(-26.3, 15.25) * mm});
            skLineSegment(sketch, "E3349", {"start": v(-26.3, 15.25) * mm, "end": v(-26.33, 15.2) * mm});
            skLineSegment(sketch, "E3350", {"start": v(-26.33, 15.2) * mm, "end": v(-26.36, 15.15) * mm});
            skLineSegment(sketch, "E3351", {"start": v(-26.36, 15.15) * mm, "end": v(-26.4, 15.11) * mm});
            skLineSegment(sketch, "E3352", {"start": v(-26.4, 15.11) * mm, "end": v(-26.45, 15.08) * mm});
            skLineSegment(sketch, "E3353", {"start": v(-26.45, 15.08) * mm, "end": v(-26.5, 15.07) * mm});
            skLineSegment(sketch, "E3354", {"start": v(-26.5, 15.07) * mm, "end": v(-26.55, 15.06) * mm});
            skLineSegment(sketch, "E3355", {"start": v(-26.55, 15.06) * mm, "end": v(-26.6, 15.07) * mm});
            skLineSegment(sketch, "E3356", {"start": v(-26.6, 15.07) * mm, "end": v(-26.64, 15.08) * mm});
            skLineSegment(sketch, "E3357", {"start": v(-26.64, 15.08) * mm, "end": v(-26.69, 15.1) * mm});
            skLineSegment(sketch, "E3358", {"start": v(-26.69, 15.1) * mm, "end": v(-26.73, 15.1) * mm});
            skLineSegment(sketch, "E3359", {"start": v(-26.73, 15.1) * mm, "end": v(-26.76, 15.06) * mm});
            skLineSegment(sketch, "E3360", {"start": v(-26.76, 15.06) * mm, "end": v(-26.82, 14.95) * mm});
            skLineSegment(sketch, "E3361", {"start": v(-26.82, 14.95) * mm, "end": v(-26.83, 14.9) * mm});
            skLineSegment(sketch, "E3362", {"start": v(-26.83, 14.9) * mm, "end": v(-26.81, 14.87) * mm});
            skLineSegment(sketch, "E3363", {"start": v(-26.81, 14.87) * mm, "end": v(-26.78, 14.84) * mm});
            skLineSegment(sketch, "E3364", {"start": v(-26.78, 14.84) * mm, "end": v(-26.75, 14.8) * mm});
            skLineSegment(sketch, "E3365", {"start": v(-26.75, 14.8) * mm, "end": v(-26.72, 14.77) * mm});
            skLineSegment(sketch, "E3366", {"start": v(-26.72, 14.77) * mm, "end": v(-26.7, 14.73) * mm});
            skLineSegment(sketch, "E3367", {"start": v(-26.7, 14.73) * mm, "end": v(-26.68, 14.67) * mm});
            skLineSegment(sketch, "E3368", {"start": v(-26.68, 14.67) * mm, "end": v(-26.68, 14.62) * mm});
            skLineSegment(sketch, "E3369", {"start": v(-26.68, 14.62) * mm, "end": v(-26.7, 14.56) * mm});
            skLineSegment(sketch, "E3370", {"start": v(-26.7, 14.56) * mm, "end": v(-26.72, 14.5) * mm});
            skLineSegment(sketch, "E3371", {"start": v(-26.72, 14.5) * mm, "end": v(-26.75, 14.46) * mm});
            skLineSegment(sketch, "E3372", {"start": v(-26.75, 14.46) * mm, "end": v(-26.8, 14.42) * mm});
            skLineSegment(sketch, "E3373", {"start": v(-26.8, 14.42) * mm, "end": v(-26.84, 14.39) * mm});
            skLineSegment(sketch, "E3374", {"start": v(-26.84, 14.39) * mm, "end": v(-26.9, 14.37) * mm});
            skLineSegment(sketch, "E3375", {"start": v(-26.9, 14.37) * mm, "end": v(-26.94, 14.36) * mm});
            skLineSegment(sketch, "E3376", {"start": v(-26.94, 14.36) * mm, "end": v(-26.99, 14.37) * mm});
            skLineSegment(sketch, "E3377", {"start": v(-26.99, 14.37) * mm, "end": v(-27.03, 14.37) * mm});
            skLineSegment(sketch, "E3378", {"start": v(-27.03, 14.37) * mm, "end": v(-27.07, 14.39) * mm});
            skLineSegment(sketch, "E3379", {"start": v(-27.07, 14.39) * mm, "end": v(-27.12, 14.39) * mm});
            skLineSegment(sketch, "E3380", {"start": v(-27.12, 14.39) * mm, "end": v(-27.15, 14.35) * mm});
            skLineSegment(sketch, "E3381", {"start": v(-27.15, 14.35) * mm, "end": v(-27.2, 14.25) * mm});
            skLineSegment(sketch, "E3382", {"start": v(-27.2, 14.25) * mm, "end": v(-27.21, 14.2) * mm});
            skLineSegment(sketch, "E3383", {"start": v(-27.21, 14.2) * mm, "end": v(-27.2, 14.16) * mm});
            skLineSegment(sketch, "E3384", {"start": v(-27.2, 14.16) * mm, "end": v(-27.16, 14.13) * mm});
            skLineSegment(sketch, "E3385", {"start": v(-27.16, 14.13) * mm, "end": v(-27.12, 14.1) * mm});
            skLineSegment(sketch, "E3386", {"start": v(-27.12, 14.1) * mm, "end": v(-27.1, 14.07) * mm});
            skLineSegment(sketch, "E3387", {"start": v(-27.1, 14.07) * mm, "end": v(-27.07, 14.03) * mm});
            skLineSegment(sketch, "E3388", {"start": v(-27.07, 14.03) * mm, "end": v(-27.06, 13.97) * mm});
            skLineSegment(sketch, "E3389", {"start": v(-27.06, 13.97) * mm, "end": v(-27.06, 13.91) * mm});
            skLineSegment(sketch, "E3390", {"start": v(-27.06, 13.91) * mm, "end": v(-27.07, 13.86) * mm});
            skLineSegment(sketch, "E3391", {"start": v(-27.07, 13.86) * mm, "end": v(-27.09, 13.8) * mm});
            skLineSegment(sketch, "E3392", {"start": v(-27.09, 13.8) * mm, "end": v(-27.12, 13.75) * mm});
            skLineSegment(sketch, "E3393", {"start": v(-27.12, 13.75) * mm, "end": v(-27.16, 13.71) * mm});
            skLineSegment(sketch, "E3394", {"start": v(-27.16, 13.71) * mm, "end": v(-27.2, 13.68) * mm});
            skLineSegment(sketch, "E3395", {"start": v(-27.2, 13.68) * mm, "end": v(-27.26, 13.66) * mm});
            skLineSegment(sketch, "E3396", {"start": v(-27.26, 13.66) * mm, "end": v(-27.3, 13.65) * mm});
            skLineSegment(sketch, "E3397", {"start": v(-27.3, 13.65) * mm, "end": v(-27.35, 13.66) * mm});
            skLineSegment(sketch, "E3398", {"start": v(-27.35, 13.66) * mm, "end": v(-27.4, 13.66) * mm});
            skLineSegment(sketch, "E3399", {"start": v(-27.4, 13.66) * mm, "end": v(-27.44, 13.67) * mm});
            skLineSegment(sketch, "E3400", {"start": v(-27.44, 13.67) * mm, "end": v(-27.48, 13.67) * mm});
            skLineSegment(sketch, "E3401", {"start": v(-27.48, 13.67) * mm, "end": v(-27.52, 13.64) * mm});
            skLineSegment(sketch, "E3402", {"start": v(-27.52, 13.64) * mm, "end": v(-27.57, 13.53) * mm});
            skLineSegment(sketch, "E3403", {"start": v(-27.57, 13.53) * mm, "end": v(-27.58, 13.48) * mm});
            skLineSegment(sketch, "E3404", {"start": v(-27.58, 13.48) * mm, "end": v(-27.55, 13.44) * mm});
            skLineSegment(sketch, "E3405", {"start": v(-27.55, 13.44) * mm, "end": v(-27.52, 13.42) * mm});
            skLineSegment(sketch, "E3406", {"start": v(-27.52, 13.42) * mm, "end": v(-27.48, 13.39) * mm});
            skLineSegment(sketch, "E3407", {"start": v(-27.48, 13.39) * mm, "end": v(-27.46, 13.35) * mm});
            skLineSegment(sketch, "E3408", {"start": v(-27.46, 13.35) * mm, "end": v(-27.43, 13.31) * mm});
            skLineSegment(sketch, "E3409", {"start": v(-27.43, 13.31) * mm, "end": v(-27.41, 13.26) * mm});
            skLineSegment(sketch, "E3410", {"start": v(-27.41, 13.26) * mm, "end": v(-27.41, 13.2) * mm});
            skLineSegment(sketch, "E3411", {"start": v(-27.41, 13.2) * mm, "end": v(-27.42, 13.14) * mm});
            skLineSegment(sketch, "E3412", {"start": v(-27.42, 13.14) * mm, "end": v(-27.44, 13.09) * mm});
            skLineSegment(sketch, "E3413", {"start": v(-27.44, 13.09) * mm, "end": v(-27.47, 13.04) * mm});
            skLineSegment(sketch, "E3414", {"start": v(-27.47, 13.04) * mm, "end": v(-27.5, 13) * mm});
            skLineSegment(sketch, "E3415", {"start": v(-27.5, 13) * mm, "end": v(-27.56, 12.96) * mm});
            skLineSegment(sketch, "E3416", {"start": v(-27.56, 12.96) * mm, "end": v(-27.6, 12.94) * mm});
            skLineSegment(sketch, "E3417", {"start": v(-27.6, 12.94) * mm, "end": v(-27.65, 12.94) * mm});
            skLineSegment(sketch, "E3418", {"start": v(-27.65, 12.94) * mm, "end": v(-27.7, 12.93) * mm});
            skLineSegment(sketch, "E3419", {"start": v(-27.7, 12.93) * mm, "end": v(-27.74, 12.94) * mm});
            skLineSegment(sketch, "E3420", {"start": v(-27.74, 12.94) * mm, "end": v(-27.79, 12.95) * mm});
            skLineSegment(sketch, "E3421", {"start": v(-27.79, 12.95) * mm, "end": v(-27.83, 12.95) * mm});
            skLineSegment(sketch, "E3422", {"start": v(-27.83, 12.95) * mm, "end": v(-27.86, 12.91) * mm});
            skLineSegment(sketch, "E3423", {"start": v(-27.86, 12.91) * mm, "end": v(-27.91, 12.8) * mm});
            skLineSegment(sketch, "E3424", {"start": v(-27.91, 12.8) * mm, "end": v(-27.92, 12.75) * mm});
            skLineSegment(sketch, "E3425", {"start": v(-27.92, 12.75) * mm, "end": v(-27.9, 12.72) * mm});
            skLineSegment(sketch, "E3426", {"start": v(-27.9, 12.72) * mm, "end": v(-27.86, 12.7) * mm});
            skLineSegment(sketch, "E3427", {"start": v(-27.86, 12.7) * mm, "end": v(-27.83, 12.66) * mm});
            skLineSegment(sketch, "E3428", {"start": v(-27.83, 12.66) * mm, "end": v(-27.8, 12.63) * mm});
            skLineSegment(sketch, "E3429", {"start": v(-27.8, 12.63) * mm, "end": v(-27.77, 12.6) * mm});
            skLineSegment(sketch, "E3430", {"start": v(-27.77, 12.6) * mm, "end": v(-27.75, 12.54) * mm});
            skLineSegment(sketch, "E3431", {"start": v(-27.75, 12.54) * mm, "end": v(-27.75, 12.48) * mm});
            skLineSegment(sketch, "E3432", {"start": v(-27.75, 12.48) * mm, "end": v(-27.75, 12.42) * mm});
            skLineSegment(sketch, "E3433", {"start": v(-27.75, 12.42) * mm, "end": v(-27.77, 12.36) * mm});
            skLineSegment(sketch, "E3434", {"start": v(-27.77, 12.36) * mm, "end": v(-27.8, 12.31) * mm});
            skLineSegment(sketch, "E3435", {"start": v(-27.8, 12.31) * mm, "end": v(-27.84, 12.27) * mm});
            skLineSegment(sketch, "E3436", {"start": v(-27.84, 12.27) * mm, "end": v(-27.89, 12.24) * mm});
            skLineSegment(sketch, "E3437", {"start": v(-27.89, 12.24) * mm, "end": v(-27.94, 12.21) * mm});
            skLineSegment(sketch, "E3438", {"start": v(-27.94, 12.21) * mm, "end": v(-27.98, 12.2) * mm});
            skLineSegment(sketch, "E3439", {"start": v(-27.98, 12.2) * mm, "end": v(-28.03, 12.2) * mm});
            skLineSegment(sketch, "E3440", {"start": v(-28.03, 12.2) * mm, "end": v(-28.07, 12.2) * mm});
            skLineSegment(sketch, "E3441", {"start": v(-28.07, 12.2) * mm, "end": v(-28.12, 12.22) * mm});
            skLineSegment(sketch, "E3442", {"start": v(-28.12, 12.22) * mm, "end": v(-28.16, 12.21) * mm});
            skLineSegment(sketch, "E3443", {"start": v(-28.16, 12.21) * mm, "end": v(-28.2, 12.18) * mm});
            skLineSegment(sketch, "E3444", {"start": v(-28.2, 12.18) * mm, "end": v(-28.24, 12.07) * mm});
            skLineSegment(sketch, "E3445", {"start": v(-28.24, 12.07) * mm, "end": v(-28.24, 12.02) * mm});
            skLineSegment(sketch, "E3446", {"start": v(-28.24, 12.02) * mm, "end": v(-28.22, 11.98) * mm});
            skLineSegment(sketch, "E3447", {"start": v(-28.22, 11.98) * mm, "end": v(-28.18, 11.96) * mm});
            skLineSegment(sketch, "E3448", {"start": v(-28.18, 11.96) * mm, "end": v(-28.15, 11.93) * mm});
            skLineSegment(sketch, "E3449", {"start": v(-28.15, 11.93) * mm, "end": v(-28.12, 11.9) * mm});
            skLineSegment(sketch, "E3450", {"start": v(-28.12, 11.9) * mm, "end": v(-28.1, 11.86) * mm});
            skLineSegment(sketch, "E3451", {"start": v(-28.1, 11.86) * mm, "end": v(-28.07, 11.8) * mm});
            skLineSegment(sketch, "E3452", {"start": v(-28.07, 11.8) * mm, "end": v(-28.06, 11.75) * mm});
            skLineSegment(sketch, "E3453", {"start": v(-28.06, 11.75) * mm, "end": v(-28.07, 11.69) * mm});
            skLineSegment(sketch, "E3454", {"start": v(-28.07, 11.69) * mm, "end": v(-28.09, 11.63) * mm});
            skLineSegment(sketch, "E3455", {"start": v(-28.09, 11.63) * mm, "end": v(-28.11, 11.58) * mm});
            skLineSegment(sketch, "E3456", {"start": v(-28.11, 11.58) * mm, "end": v(-28.15, 11.54) * mm});
            skLineSegment(sketch, "E3457", {"start": v(-28.15, 11.54) * mm, "end": v(-28.2, 11.5) * mm});
            skLineSegment(sketch, "E3458", {"start": v(-28.2, 11.5) * mm, "end": v(-28.25, 11.48) * mm});
            skLineSegment(sketch, "E3459", {"start": v(-28.25, 11.48) * mm, "end": v(-28.3, 11.47) * mm});
            skLineSegment(sketch, "E3460", {"start": v(-28.3, 11.47) * mm, "end": v(-28.34, 11.47) * mm});
            skLineSegment(sketch, "E3461", {"start": v(-28.34, 11.47) * mm, "end": v(-28.38, 11.47) * mm});
            skLineSegment(sketch, "E3462", {"start": v(-28.38, 11.47) * mm, "end": v(-28.43, 11.48) * mm});
            skLineSegment(sketch, "E3463", {"start": v(-28.43, 11.48) * mm, "end": v(-28.47, 11.47) * mm});
            skLineSegment(sketch, "E3464", {"start": v(-28.47, 11.47) * mm, "end": v(-28.5, 11.44) * mm});
            skLineSegment(sketch, "E3465", {"start": v(-28.5, 11.44) * mm, "end": v(-28.55, 11.32) * mm});
            skLineSegment(sketch, "E3466", {"start": v(-28.55, 11.32) * mm, "end": v(-28.55, 11.28) * mm});
            skLineSegment(sketch, "E3467", {"start": v(-28.55, 11.28) * mm, "end": v(-28.52, 11.24) * mm});
            skLineSegment(sketch, "E3468", {"start": v(-28.52, 11.24) * mm, "end": v(-28.48, 11.22) * mm});
            skLineSegment(sketch, "E3469", {"start": v(-28.48, 11.22) * mm, "end": v(-28.45, 11.19) * mm});
            skLineSegment(sketch, "E3470", {"start": v(-28.45, 11.19) * mm, "end": v(-28.42, 11.16) * mm});
            skLineSegment(sketch, "E3471", {"start": v(-28.42, 11.16) * mm, "end": v(-28.4, 11.12) * mm});
            skLineSegment(sketch, "E3472", {"start": v(-28.4, 11.12) * mm, "end": v(-28.37, 11.07) * mm});
            skLineSegment(sketch, "E3473", {"start": v(-28.37, 11.07) * mm, "end": v(-28.36, 11) * mm});
            skLineSegment(sketch, "E3474", {"start": v(-28.36, 11) * mm, "end": v(-28.37, 10.95) * mm});
            skLineSegment(sketch, "E3475", {"start": v(-28.37, 10.95) * mm, "end": v(-28.38, 10.9) * mm});
            skLineSegment(sketch, "E3476", {"start": v(-28.38, 10.9) * mm, "end": v(-28.4, 10.84) * mm});
            skLineSegment(sketch, "E3477", {"start": v(-28.4, 10.84) * mm, "end": v(-28.44, 10.8) * mm});
            skLineSegment(sketch, "E3478", {"start": v(-28.44, 10.8) * mm, "end": v(-28.49, 10.76) * mm});
            skLineSegment(sketch, "E3479", {"start": v(-28.49, 10.76) * mm, "end": v(-28.54, 10.73) * mm});
            skLineSegment(sketch, "E3480", {"start": v(-28.54, 10.73) * mm, "end": v(-28.58, 10.73) * mm});
            skLineSegment(sketch, "E3481", {"start": v(-28.58, 10.73) * mm, "end": v(-28.63, 10.72) * mm});
            skLineSegment(sketch, "E3482", {"start": v(-28.63, 10.72) * mm, "end": v(-28.67, 10.72) * mm});
            skLineSegment(sketch, "E3483", {"start": v(-28.67, 10.72) * mm, "end": v(-28.72, 10.73) * mm});
            skLineSegment(sketch, "E3484", {"start": v(-28.72, 10.73) * mm, "end": v(-28.76, 10.72) * mm});
            skLineSegment(sketch, "E3485", {"start": v(-28.76, 10.72) * mm, "end": v(-28.8, 10.69) * mm});
            skLineSegment(sketch, "E3486", {"start": v(-28.8, 10.69) * mm, "end": v(-28.83, 10.57) * mm});
            skLineSegment(sketch, "E3487", {"start": v(-28.83, 10.57) * mm, "end": v(-28.83, 10.53) * mm});
            skLineSegment(sketch, "E3488", {"start": v(-28.83, 10.53) * mm, "end": v(-28.8, 10.5) * mm});
            skLineSegment(sketch, "E3489", {"start": v(-28.8, 10.5) * mm, "end": v(-28.77, 10.47) * mm});
            skLineSegment(sketch, "E3490", {"start": v(-28.77, 10.47) * mm, "end": v(-28.73, 10.44) * mm});
            skLineSegment(sketch, "E3491", {"start": v(-28.73, 10.44) * mm, "end": v(-28.7, 10.4) * mm});
            skLineSegment(sketch, "E3492", {"start": v(-28.7, 10.4) * mm, "end": v(-28.67, 10.37) * mm});
            skLineSegment(sketch, "E3493", {"start": v(-28.67, 10.37) * mm, "end": v(-28.65, 10.32) * mm});
            skLineSegment(sketch, "E3494", {"start": v(-28.65, 10.32) * mm, "end": v(-28.64, 10.26) * mm});
            skLineSegment(sketch, "E3495", {"start": v(-28.64, 10.26) * mm, "end": v(-28.64, 10.2) * mm});
            skLineSegment(sketch, "E3496", {"start": v(-28.64, 10.2) * mm, "end": v(-28.66, 10.15) * mm});
            skLineSegment(sketch, "E3497", {"start": v(-28.66, 10.15) * mm, "end": v(-28.68, 10.1) * mm});
            skLineSegment(sketch, "E3498", {"start": v(-28.68, 10.1) * mm, "end": v(-28.72, 10.05) * mm});
            skLineSegment(sketch, "E3499", {"start": v(-28.72, 10.05) * mm, "end": v(-28.76, 10.01) * mm});
            skLineSegment(sketch, "E3500", {"start": v(-28.76, 10.01) * mm, "end": v(-28.81, 9.98) * mm});
            skLineSegment(sketch, "E3501", {"start": v(-28.81, 9.98) * mm, "end": v(-28.86, 9.97) * mm});
            skLineSegment(sketch, "E3502", {"start": v(-28.86, 9.97) * mm, "end": v(-28.9, 9.97) * mm});
            skLineSegment(sketch, "E3503", {"start": v(-28.9, 9.97) * mm, "end": v(-28.94, 9.97) * mm});
            skLineSegment(sketch, "E3504", {"start": v(-28.94, 9.97) * mm, "end": v(-28.99, 9.98) * mm});
            skLineSegment(sketch, "E3505", {"start": v(-28.99, 9.98) * mm, "end": v(-29.03, 9.97) * mm});
            skLineSegment(sketch, "E3506", {"start": v(-29.03, 9.97) * mm, "end": v(-29.06, 9.93) * mm});
            skLineSegment(sketch, "E3507", {"start": v(-29.06, 9.93) * mm, "end": v(-29.1, 9.81) * mm});
            skLineSegment(sketch, "E3508", {"start": v(-29.1, 9.81) * mm, "end": v(-29.1, 9.77) * mm});
            skLineSegment(sketch, "E3509", {"start": v(-29.1, 9.77) * mm, "end": v(-29.07, 9.73) * mm});
            skLineSegment(sketch, "E3510", {"start": v(-29.07, 9.73) * mm, "end": v(-29.03, 9.71) * mm});
            skLineSegment(sketch, "E3511", {"start": v(-29.03, 9.71) * mm, "end": v(-29, 9.68) * mm});
            skLineSegment(sketch, "E3512", {"start": v(-29, 9.68) * mm, "end": v(-28.96, 9.65) * mm});
            skLineSegment(sketch, "E3513", {"start": v(-28.96, 9.65) * mm, "end": v(-28.93, 9.62) * mm});
            skLineSegment(sketch, "E3514", {"start": v(-28.93, 9.62) * mm, "end": v(-28.91, 9.57) * mm});
            skLineSegment(sketch, "E3515", {"start": v(-28.91, 9.57) * mm, "end": v(-28.9, 9.5) * mm});
            skLineSegment(sketch, "E3516", {"start": v(-28.9, 9.5) * mm, "end": v(-28.9, 9.45) * mm});
            skLineSegment(sketch, "E3517", {"start": v(-28.9, 9.45) * mm, "end": v(-28.91, 9.4) * mm});
            skLineSegment(sketch, "E3518", {"start": v(-28.91, 9.4) * mm, "end": v(-28.94, 9.34) * mm});
            skLineSegment(sketch, "E3519", {"start": v(-28.94, 9.34) * mm, "end": v(-28.97, 9.3) * mm});
            skLineSegment(sketch, "E3520", {"start": v(-28.97, 9.3) * mm, "end": v(-29.01, 9.25) * mm});
            skLineSegment(sketch, "E3521", {"start": v(-29.01, 9.25) * mm, "end": v(-29.06, 9.23) * mm});
            skLineSegment(sketch, "E3522", {"start": v(-29.06, 9.23) * mm, "end": v(-29.1, 9.21) * mm});
            skLineSegment(sketch, "E3523", {"start": v(-29.1, 9.21) * mm, "end": v(-29.15, 9.2) * mm});
            skLineSegment(sketch, "E3524", {"start": v(-29.15, 9.2) * mm, "end": v(-29.2, 9.2) * mm});
            skLineSegment(sketch, "E3525", {"start": v(-29.2, 9.2) * mm, "end": v(-29.24, 9.21) * mm});
            skLineSegment(sketch, "E3526", {"start": v(-29.24, 9.21) * mm, "end": v(-29.28, 9.2) * mm});
            skLineSegment(sketch, "E3527", {"start": v(-29.28, 9.2) * mm, "end": v(-29.31, 9.16) * mm});
            skLineSegment(sketch, "E3528", {"start": v(-29.31, 9.16) * mm, "end": v(-29.35, 9.05) * mm});
            skLineSegment(sketch, "E3529", {"start": v(-29.35, 9.05) * mm, "end": v(-29.35, 9) * mm});
            skLineSegment(sketch, "E3530", {"start": v(-29.35, 9) * mm, "end": v(-29.32, 8.97) * mm});
            skLineSegment(sketch, "E3531", {"start": v(-29.32, 8.97) * mm, "end": v(-29.28, 8.95) * mm});
            skLineSegment(sketch, "E3532", {"start": v(-29.28, 8.95) * mm, "end": v(-29.24, 8.92) * mm});
            skLineSegment(sketch, "E3533", {"start": v(-29.24, 8.92) * mm, "end": v(-29.2, 8.9) * mm});
            skLineSegment(sketch, "E3534", {"start": v(-29.2, 8.9) * mm, "end": v(-29.18, 8.86) * mm});
            skLineSegment(sketch, "E3535", {"start": v(-29.18, 8.86) * mm, "end": v(-29.15, 8.8) * mm});
            skLineSegment(sketch, "E3536", {"start": v(-29.15, 8.8) * mm, "end": v(-29.14, 8.75) * mm});
            skLineSegment(sketch, "E3537", {"start": v(-29.14, 8.75) * mm, "end": v(-29.14, 8.7) * mm});
            skLineSegment(sketch, "E3538", {"start": v(-29.14, 8.7) * mm, "end": v(-29.15, 8.63) * mm});
            skLineSegment(sketch, "E3539", {"start": v(-29.15, 8.63) * mm, "end": v(-29.17, 8.58) * mm});
            skLineSegment(sketch, "E3540", {"start": v(-29.17, 8.58) * mm, "end": v(-29.2, 8.53) * mm});
            skLineSegment(sketch, "E3541", {"start": v(-29.2, 8.53) * mm, "end": v(-29.24, 8.5) * mm});
            skLineSegment(sketch, "E3542", {"start": v(-29.24, 8.5) * mm, "end": v(-29.3, 8.46) * mm});
            skLineSegment(sketch, "E3543", {"start": v(-29.3, 8.46) * mm, "end": v(-29.34, 8.45) * mm});
            skLineSegment(sketch, "E3544", {"start": v(-29.34, 8.45) * mm, "end": v(-29.38, 8.44) * mm});
            skLineSegment(sketch, "E3545", {"start": v(-29.38, 8.44) * mm, "end": v(-29.43, 8.44) * mm});
            skLineSegment(sketch, "E3546", {"start": v(-29.43, 8.44) * mm, "end": v(-29.47, 8.44) * mm});
            skLineSegment(sketch, "E3547", {"start": v(-29.47, 8.44) * mm, "end": v(-29.51, 8.43) * mm});
            skLineSegment(sketch, "E3548", {"start": v(-29.51, 8.43) * mm, "end": v(-29.54, 8.4) * mm});
            skLineSegment(sketch, "E3549", {"start": v(-29.54, 8.4) * mm, "end": v(-29.57, 8.28) * mm});
            skLineSegment(sketch, "E3550", {"start": v(-29.57, 8.28) * mm, "end": v(-29.57, 8.23) * mm});
            skLineSegment(sketch, "E3551", {"start": v(-29.57, 8.23) * mm, "end": v(-29.54, 8.2) * mm});
            skLineSegment(sketch, "E3552", {"start": v(-29.54, 8.2) * mm, "end": v(-29.5, 8.18) * mm});
            skLineSegment(sketch, "E3553", {"start": v(-29.5, 8.18) * mm, "end": v(-29.46, 8.15) * mm});
            skLineSegment(sketch, "E3554", {"start": v(-29.46, 8.15) * mm, "end": v(-29.43, 8.12) * mm});
            skLineSegment(sketch, "E3555", {"start": v(-29.43, 8.12) * mm, "end": v(-29.4, 8.1) * mm});
            skLineSegment(sketch, "E3556", {"start": v(-29.4, 8.1) * mm, "end": v(-29.37, 8.04) * mm});
            skLineSegment(sketch, "E3557", {"start": v(-29.37, 8.04) * mm, "end": v(-29.36, 7.98) * mm});
            skLineSegment(sketch, "E3558", {"start": v(-29.36, 7.98) * mm, "end": v(-29.35, 7.93) * mm});
            skLineSegment(sketch, "E3559", {"start": v(-29.35, 7.93) * mm, "end": v(-29.36, 7.87) * mm});
            skLineSegment(sketch, "E3560", {"start": v(-29.36, 7.87) * mm, "end": v(-29.39, 7.81) * mm});
            skLineSegment(sketch, "E3561", {"start": v(-29.39, 7.81) * mm, "end": v(-29.42, 7.76) * mm});
            skLineSegment(sketch, "E3562", {"start": v(-29.42, 7.76) * mm, "end": v(-29.46, 7.72) * mm});
            skLineSegment(sketch, "E3563", {"start": v(-29.46, 7.72) * mm, "end": v(-29.5, 7.7) * mm});
            skLineSegment(sketch, "E3564", {"start": v(-29.5, 7.7) * mm, "end": v(-29.55, 7.68) * mm});
            skLineSegment(sketch, "E3565", {"start": v(-29.55, 7.68) * mm, "end": v(-29.6, 7.67) * mm});
            skLineSegment(sketch, "E3566", {"start": v(-29.6, 7.67) * mm, "end": v(-29.64, 7.67) * mm});
            skLineSegment(sketch, "E3567", {"start": v(-29.64, 7.67) * mm, "end": v(-29.68, 7.67) * mm});
            skLineSegment(sketch, "E3568", {"start": v(-29.68, 7.67) * mm, "end": v(-29.72, 7.66) * mm});
            skLineSegment(sketch, "E3569", {"start": v(-29.72, 7.66) * mm, "end": v(-29.75, 7.62) * mm});
            skLineSegment(sketch, "E3570", {"start": v(-29.75, 7.62) * mm, "end": v(-29.78, 7.5) * mm});
            skLineSegment(sketch, "E3571", {"start": v(-29.78, 7.5) * mm, "end": v(-29.78, 7.45) * mm});
            skLineSegment(sketch, "E3572", {"start": v(-29.78, 7.45) * mm, "end": v(-29.75, 7.42) * mm});
            skLineSegment(sketch, "E3573", {"start": v(-29.75, 7.42) * mm, "end": v(-29.7, 7.4) * mm});
            skLineSegment(sketch, "E3574", {"start": v(-29.7, 7.4) * mm, "end": v(-29.67, 7.38) * mm});
            skLineSegment(sketch, "E3575", {"start": v(-29.67, 7.38) * mm, "end": v(-29.63, 7.35) * mm});
            skLineSegment(sketch, "E3576", {"start": v(-29.63, 7.35) * mm, "end": v(-29.6, 7.32) * mm});
            skLineSegment(sketch, "E3577", {"start": v(-29.6, 7.32) * mm, "end": v(-29.57, 7.27) * mm});
            skLineSegment(sketch, "E3578", {"start": v(-29.57, 7.27) * mm, "end": v(-29.56, 7.21) * mm});
            skLineSegment(sketch, "E3579", {"start": v(-29.56, 7.21) * mm, "end": v(-29.55, 7.15) * mm});
            skLineSegment(sketch, "E3580", {"start": v(-29.55, 7.15) * mm, "end": v(-29.56, 7.1) * mm});
            skLineSegment(sketch, "E3581", {"start": v(-29.56, 7.1) * mm, "end": v(-29.58, 7.04) * mm});
            skLineSegment(sketch, "E3582", {"start": v(-29.58, 7.04) * mm, "end": v(-29.6, 7) * mm});
            skLineSegment(sketch, "E3583", {"start": v(-29.6, 7) * mm, "end": v(-29.65, 6.95) * mm});
            skLineSegment(sketch, "E3584", {"start": v(-29.65, 6.95) * mm, "end": v(-29.7, 6.92) * mm});
            skLineSegment(sketch, "E3585", {"start": v(-29.7, 6.92) * mm, "end": v(-29.74, 6.9) * mm});
            skLineSegment(sketch, "E3586", {"start": v(-29.74, 6.9) * mm, "end": v(-29.78, 6.9) * mm});
            skLineSegment(sketch, "E3587", {"start": v(-29.78, 6.9) * mm, "end": v(-29.83, 6.89) * mm});
            skLineSegment(sketch, "E3588", {"start": v(-29.83, 6.89) * mm, "end": v(-29.87, 6.9) * mm});
            skLineSegment(sketch, "E3589", {"start": v(-29.87, 6.9) * mm, "end": v(-29.91, 6.88) * mm});
            skLineSegment(sketch, "E3590", {"start": v(-29.91, 6.88) * mm, "end": v(-29.94, 6.84) * mm});
            skLineSegment(sketch, "E3591", {"start": v(-29.94, 6.84) * mm, "end": v(-29.97, 6.72) * mm});
            skLineSegment(sketch, "E3592", {"start": v(-29.97, 6.72) * mm, "end": v(-29.96, 6.67) * mm});
            skLineSegment(sketch, "E3593", {"start": v(-29.96, 6.67) * mm, "end": v(-29.93, 6.64) * mm});
            skLineSegment(sketch, "E3594", {"start": v(-29.93, 6.64) * mm, "end": v(-29.89, 6.62) * mm});
            skLineSegment(sketch, "E3595", {"start": v(-29.89, 6.62) * mm, "end": v(-29.85, 6.6) * mm});
            skLineSegment(sketch, "E3596", {"start": v(-29.85, 6.6) * mm, "end": v(-29.81, 6.57) * mm});
            skLineSegment(sketch, "E3597", {"start": v(-29.81, 6.57) * mm, "end": v(-29.78, 6.54) * mm});
            skLineSegment(sketch, "E3598", {"start": v(-29.78, 6.54) * mm, "end": v(-29.75, 6.5) * mm});
            skLineSegment(sketch, "E3599", {"start": v(-29.75, 6.5) * mm, "end": v(-29.73, 6.44) * mm});
            skLineSegment(sketch, "E3600", {"start": v(-29.73, 6.44) * mm, "end": v(-29.73, 6.38) * mm});
            skLineSegment(sketch, "E3601", {"start": v(-29.73, 6.38) * mm, "end": v(-29.74, 6.32) * mm});
            skLineSegment(sketch, "E3602", {"start": v(-29.74, 6.32) * mm, "end": v(-29.75, 6.26) * mm});
            skLineSegment(sketch, "E3603", {"start": v(-29.75, 6.26) * mm, "end": v(-29.78, 6.21) * mm});
            skLineSegment(sketch, "E3604", {"start": v(-29.78, 6.21) * mm, "end": v(-29.82, 6.17) * mm});
            skLineSegment(sketch, "E3605", {"start": v(-29.82, 6.17) * mm, "end": v(-29.87, 6.14) * mm});
            skLineSegment(sketch, "E3606", {"start": v(-29.87, 6.14) * mm, "end": v(-29.91, 6.12) * mm});
            skLineSegment(sketch, "E3607", {"start": v(-29.91, 6.12) * mm, "end": v(-29.95, 6.11) * mm});
            skLineSegment(sketch, "E3608", {"start": v(-29.95, 6.11) * mm, "end": v(-30, 6.1) * mm});
            skLineSegment(sketch, "E3609", {"start": v(-30, 6.1) * mm, "end": v(-30.04, 6.1) * mm});
            skLineSegment(sketch, "E3610", {"start": v(-30.04, 6.1) * mm, "end": v(-30.08, 6.1) * mm});
            skLineSegment(sketch, "E3611", {"start": v(-30.08, 6.1) * mm, "end": v(-30.1, 6.05) * mm});
            skLineSegment(sketch, "E3612", {"start": v(-30.1, 6.05) * mm, "end": v(-30.13, 5.93) * mm});
            skLineSegment(sketch, "E3613", {"start": v(-30.13, 5.93) * mm, "end": v(-30.13, 5.88) * mm});
            skLineSegment(sketch, "E3614", {"start": v(-30.13, 5.88) * mm, "end": v(-30.1, 5.86) * mm});
            skLineSegment(sketch, "E3615", {"start": v(-30.1, 5.86) * mm, "end": v(-30.05, 5.84) * mm});
            skLineSegment(sketch, "E3616", {"start": v(-30.05, 5.84) * mm, "end": v(-30.01, 5.82) * mm});
            skLineSegment(sketch, "E3617", {"start": v(-30.01, 5.82) * mm, "end": v(-29.98, 5.8) * mm});
            skLineSegment(sketch, "E3618", {"start": v(-29.98, 5.8) * mm, "end": v(-29.94, 5.76) * mm});
            skLineSegment(sketch, "E3619", {"start": v(-29.94, 5.76) * mm, "end": v(-29.91, 5.71) * mm});
            skLineSegment(sketch, "E3620", {"start": v(-29.91, 5.71) * mm, "end": v(-29.9, 5.66) * mm});
            skLineSegment(sketch, "E3621", {"start": v(-29.9, 5.66) * mm, "end": v(-29.89, 5.6) * mm});
            skLineSegment(sketch, "E3622", {"start": v(-29.89, 5.6) * mm, "end": v(-29.9, 5.54) * mm});
            skLineSegment(sketch, "E3623", {"start": v(-29.9, 5.54) * mm, "end": v(-29.9, 5.48) * mm});
            skLineSegment(sketch, "E3624", {"start": v(-29.9, 5.48) * mm, "end": v(-29.93, 5.43) * mm});
            skLineSegment(sketch, "E3625", {"start": v(-29.93, 5.43) * mm, "end": v(-29.97, 5.39) * mm});
            skLineSegment(sketch, "E3626", {"start": v(-29.97, 5.39) * mm, "end": v(-30.02, 5.35) * mm});
            skLineSegment(sketch, "E3627", {"start": v(-30.02, 5.35) * mm, "end": v(-30.06, 5.34) * mm});
            skLineSegment(sketch, "E3628", {"start": v(-30.06, 5.34) * mm, "end": v(-30.1, 5.32) * mm});
            skLineSegment(sketch, "E3629", {"start": v(-30.1, 5.32) * mm, "end": v(-30.15, 5.32) * mm});
            skLineSegment(sketch, "E3630", {"start": v(-30.15, 5.32) * mm, "end": v(-30.2, 5.32) * mm});
            skLineSegment(sketch, "E3631", {"start": v(-30.2, 5.32) * mm, "end": v(-30.23, 5.3) * mm});
            skLineSegment(sketch, "E3632", {"start": v(-30.23, 5.3) * mm, "end": v(-30.26, 5.26) * mm});
            skLineSegment(sketch, "E3633", {"start": v(-30.26, 5.26) * mm, "end": v(-30.28, 5.14) * mm});
            skLineSegment(sketch, "E3634", {"start": v(-30.28, 5.14) * mm, "end": v(-30.27, 5.1) * mm});
            skLineSegment(sketch, "E3635", {"start": v(-30.27, 5.1) * mm, "end": v(-30.24, 5.07) * mm});
            skLineSegment(sketch, "E3636", {"start": v(-30.24, 5.07) * mm, "end": v(-30.2, 5.05) * mm});
            skLineSegment(sketch, "E3637", {"start": v(-30.2, 5.05) * mm, "end": v(-30.15, 5.03) * mm});
            skLineSegment(sketch, "E3638", {"start": v(-30.15, 5.03) * mm, "end": v(-30.12, 5) * mm});
            skLineSegment(sketch, "E3639", {"start": v(-30.12, 5) * mm, "end": v(-30.08, 4.97) * mm});
            skLineSegment(sketch, "E3640", {"start": v(-30.08, 4.97) * mm, "end": v(-30.05, 4.93) * mm});
            skLineSegment(sketch, "E3641", {"start": v(-30.05, 4.93) * mm, "end": v(-30.03, 4.87) * mm});
            skLineSegment(sketch, "E3642", {"start": v(-30.03, 4.87) * mm, "end": v(-30.02, 4.81) * mm});
            skLineSegment(sketch, "E3643", {"start": v(-30.02, 4.81) * mm, "end": v(-30.03, 4.76) * mm});
            skLineSegment(sketch, "E3644", {"start": v(-30.03, 4.76) * mm, "end": v(-30.04, 4.7) * mm});
            skLineSegment(sketch, "E3645", {"start": v(-30.04, 4.7) * mm, "end": v(-30.07, 4.65) * mm});
            skLineSegment(sketch, "E3646", {"start": v(-30.07, 4.65) * mm, "end": v(-30.1, 4.6) * mm});
            skLineSegment(sketch, "E3647", {"start": v(-30.1, 4.6) * mm, "end": v(-30.15, 4.57) * mm});
            skLineSegment(sketch, "E3648", {"start": v(-30.15, 4.57) * mm, "end": v(-30.19, 4.55) * mm});
            skLineSegment(sketch, "E3649", {"start": v(-30.19, 4.55) * mm, "end": v(-30.23, 4.54) * mm});
            skLineSegment(sketch, "E3650", {"start": v(-30.23, 4.54) * mm, "end": v(-30.28, 4.53) * mm});
            skLineSegment(sketch, "E3651", {"start": v(-30.28, 4.53) * mm, "end": v(-30.32, 4.53) * mm});
            skLineSegment(sketch, "E3652", {"start": v(-30.32, 4.53) * mm, "end": v(-30.36, 4.5) * mm});
            skLineSegment(sketch, "E3653", {"start": v(-30.36, 4.5) * mm, "end": v(-30.38, 4.47) * mm});
            skLineSegment(sketch, "E3654", {"start": v(-30.38, 4.47) * mm, "end": v(-30.4, 4.35) * mm});
            skLineSegment(sketch, "E3655", {"start": v(-30.4, 4.35) * mm, "end": v(-30.4, 4.3) * mm});
            skLineSegment(sketch, "E3656", {"start": v(-30.4, 4.3) * mm, "end": v(-30.36, 4.27) * mm});
            skLineSegment(sketch, "E3657", {"start": v(-30.36, 4.27) * mm, "end": v(-30.32, 4.26) * mm});
            skLineSegment(sketch, "E3658", {"start": v(-30.32, 4.26) * mm, "end": v(-30.28, 4.24) * mm});
            skLineSegment(sketch, "E3659", {"start": v(-30.28, 4.24) * mm, "end": v(-30.24, 4.21) * mm});
            skLineSegment(sketch, "E3660", {"start": v(-30.24, 4.21) * mm, "end": v(-30.2, 4.18) * mm});
            skLineSegment(sketch, "E3661", {"start": v(-30.2, 4.18) * mm, "end": v(-30.17, 4.14) * mm});
            skLineSegment(sketch, "E3662", {"start": v(-30.17, 4.14) * mm, "end": v(-30.15, 4.08) * mm});
            skLineSegment(sketch, "E3663", {"start": v(-30.15, 4.08) * mm, "end": v(-30.14, 4.03) * mm});
            skLineSegment(sketch, "E3664", {"start": v(-30.14, 4.03) * mm, "end": v(-30.14, 3.97) * mm});
            skLineSegment(sketch, "E3665", {"start": v(-30.14, 3.97) * mm, "end": v(-30.15, 3.91) * mm});
            skLineSegment(sketch, "E3666", {"start": v(-30.15, 3.91) * mm, "end": v(-30.18, 3.86) * mm});
            skLineSegment(sketch, "E3667", {"start": v(-30.18, 3.86) * mm, "end": v(-30.21, 3.81) * mm});
            skLineSegment(sketch, "E3668", {"start": v(-30.21, 3.81) * mm, "end": v(-30.26, 3.78) * mm});
            skLineSegment(sketch, "E3669", {"start": v(-30.26, 3.78) * mm, "end": v(-30.3, 3.76) * mm});
            skLineSegment(sketch, "E3670", {"start": v(-30.3, 3.76) * mm, "end": v(-30.34, 3.74) * mm});
            skLineSegment(sketch, "E3671", {"start": v(-30.34, 3.74) * mm, "end": v(-30.39, 3.73) * mm});
            skLineSegment(sketch, "E3672", {"start": v(-30.39, 3.73) * mm, "end": v(-30.43, 3.73) * mm});
            skLineSegment(sketch, "E3673", {"start": v(-30.43, 3.73) * mm, "end": v(-30.47, 3.71) * mm});
            skLineSegment(sketch, "E3674", {"start": v(-30.47, 3.71) * mm, "end": v(-30.5, 3.67) * mm});
            skLineSegment(sketch, "E3675", {"start": v(-30.5, 3.67) * mm, "end": v(-30.5, 3.55) * mm});
            skLineSegment(sketch, "E3676", {"start": v(-30.5, 3.55) * mm, "end": v(-30.5, 3.5) * mm});
            skLineSegment(sketch, "E3677", {"start": v(-30.5, 3.5) * mm, "end": v(-30.46, 3.48) * mm});
            skLineSegment(sketch, "E3678", {"start": v(-30.46, 3.48) * mm, "end": v(-30.42, 3.46) * mm});
            skLineSegment(sketch, "E3679", {"start": v(-30.42, 3.46) * mm, "end": v(-30.38, 3.44) * mm});
            skLineSegment(sketch, "E3680", {"start": v(-30.38, 3.44) * mm, "end": v(-30.34, 3.42) * mm});
            skLineSegment(sketch, "E3681", {"start": v(-30.34, 3.42) * mm, "end": v(-30.3, 3.4) * mm});
            skLineSegment(sketch, "E3682", {"start": v(-30.3, 3.4) * mm, "end": v(-30.27, 3.35) * mm});
            skLineSegment(sketch, "E3683", {"start": v(-30.27, 3.35) * mm, "end": v(-30.24, 3.3) * mm});
            skLineSegment(sketch, "E3684", {"start": v(-30.24, 3.3) * mm, "end": v(-30.23, 3.24) * mm});
            skLineSegment(sketch, "E3685", {"start": v(-30.23, 3.24) * mm, "end": v(-30.23, 3.18) * mm});
            skLineSegment(sketch, "E3686", {"start": v(-30.23, 3.18) * mm, "end": v(-30.25, 3.12) * mm});
            skLineSegment(sketch, "E3687", {"start": v(-30.25, 3.12) * mm, "end": v(-30.27, 3.07) * mm});
            skLineSegment(sketch, "E3688", {"start": v(-30.27, 3.07) * mm, "end": v(-30.3, 3.02) * mm});
            skLineSegment(sketch, "E3689", {"start": v(-30.3, 3.02) * mm, "end": v(-30.35, 2.98) * mm});
            skLineSegment(sketch, "E3690", {"start": v(-30.35, 2.98) * mm, "end": v(-30.39, 2.96) * mm});
            skLineSegment(sketch, "E3691", {"start": v(-30.39, 2.96) * mm, "end": v(-30.43, 2.95) * mm});
            skLineSegment(sketch, "E3692", {"start": v(-30.43, 2.95) * mm, "end": v(-30.47, 2.94) * mm});
            skLineSegment(sketch, "E3693", {"start": v(-30.47, 2.94) * mm, "end": v(-30.52, 2.93) * mm});
            skLineSegment(sketch, "E3694", {"start": v(-30.52, 2.93) * mm, "end": v(-30.56, 2.91) * mm});
            skLineSegment(sketch, "E3695", {"start": v(-30.56, 2.91) * mm, "end": v(-30.58, 2.87) * mm});
            skLineSegment(sketch, "E3696", {"start": v(-30.58, 2.87) * mm, "end": v(-30.59, 2.75) * mm});
            skLineSegment(sketch, "E3697", {"start": v(-30.59, 2.75) * mm, "end": v(-30.58, 2.7) * mm});
            skLineSegment(sketch, "E3698", {"start": v(-30.58, 2.7) * mm, "end": v(-30.54, 2.68) * mm});
            skLineSegment(sketch, "E3699", {"start": v(-30.54, 2.68) * mm, "end": v(-30.5, 2.67) * mm});
            skLineSegment(sketch, "E3700", {"start": v(-30.5, 2.67) * mm, "end": v(-30.46, 2.65) * mm});
            skLineSegment(sketch, "E3701", {"start": v(-30.46, 2.65) * mm, "end": v(-30.42, 2.63) * mm});
            skLineSegment(sketch, "E3702", {"start": v(-30.42, 2.63) * mm, "end": v(-30.38, 2.6) * mm});
            skLineSegment(sketch, "E3703", {"start": v(-30.38, 2.6) * mm, "end": v(-30.34, 2.55) * mm});
            skLineSegment(sketch, "E3704", {"start": v(-30.34, 2.55) * mm, "end": v(-30.32, 2.5) * mm});
            skLineSegment(sketch, "E3705", {"start": v(-30.32, 2.5) * mm, "end": v(-30.3, 2.44) * mm});
            skLineSegment(sketch, "E3706", {"start": v(-30.3, 2.44) * mm, "end": v(-30.3, 2.39) * mm});
            skLineSegment(sketch, "E3707", {"start": v(-30.3, 2.39) * mm, "end": v(-30.32, 2.33) * mm});
            skLineSegment(sketch, "E3708", {"start": v(-30.32, 2.33) * mm, "end": v(-30.34, 2.27) * mm});
            skLineSegment(sketch, "E3709", {"start": v(-30.34, 2.27) * mm, "end": v(-30.37, 2.23) * mm});
            skLineSegment(sketch, "E3710", {"start": v(-30.37, 2.23) * mm, "end": v(-30.41, 2.19) * mm});
            skLineSegment(sketch, "E3711", {"start": v(-30.41, 2.19) * mm, "end": v(-30.45, 2.17) * mm});
            skLineSegment(sketch, "E3712", {"start": v(-30.45, 2.17) * mm, "end": v(-30.5, 2.15) * mm});
            skLineSegment(sketch, "E3713", {"start": v(-30.5, 2.15) * mm, "end": v(-30.54, 2.14) * mm});
            skLineSegment(sketch, "E3714", {"start": v(-30.54, 2.14) * mm, "end": v(-30.58, 2.13) * mm});
            skLineSegment(sketch, "E3715", {"start": v(-30.58, 2.13) * mm, "end": v(-30.62, 2.11) * mm});
            skLineSegment(sketch, "E3716", {"start": v(-30.62, 2.11) * mm, "end": v(-30.64, 2.07) * mm});
            skLineSegment(sketch, "E3717", {"start": v(-30.64, 2.07) * mm, "end": v(-30.65, 1.95) * mm});
            skLineSegment(sketch, "E3718", {"start": v(-30.65, 1.95) * mm, "end": v(-30.64, 1.9) * mm});
            skLineSegment(sketch, "E3719", {"start": v(-30.64, 1.9) * mm, "end": v(-30.6, 1.88) * mm});
            skLineSegment(sketch, "E3720", {"start": v(-30.6, 1.88) * mm, "end": v(-30.56, 1.87) * mm});
            skLineSegment(sketch, "E3721", {"start": v(-30.56, 1.87) * mm, "end": v(-30.52, 1.85) * mm});
            skLineSegment(sketch, "E3722", {"start": v(-30.52, 1.85) * mm, "end": v(-30.48, 1.83) * mm});
            skLineSegment(sketch, "E3723", {"start": v(-30.48, 1.83) * mm, "end": v(-30.44, 1.8) * mm});
            skLineSegment(sketch, "E3724", {"start": v(-30.44, 1.8) * mm, "end": v(-30.4, 1.76) * mm});
            skLineSegment(sketch, "E3725", {"start": v(-30.4, 1.76) * mm, "end": v(-30.38, 1.7) * mm});
            skLineSegment(sketch, "E3726", {"start": v(-30.38, 1.7) * mm, "end": v(-30.36, 1.65) * mm});
            skLineSegment(sketch, "E3727", {"start": v(-30.36, 1.65) * mm, "end": v(-30.36, 1.6) * mm});
            skLineSegment(sketch, "E3728", {"start": v(-30.36, 1.6) * mm, "end": v(-30.37, 1.53) * mm});
            skLineSegment(sketch, "E3729", {"start": v(-30.37, 1.53) * mm, "end": v(-30.39, 1.48) * mm});
            skLineSegment(sketch, "E3730", {"start": v(-30.39, 1.48) * mm, "end": v(-30.42, 1.43) * mm});
            skLineSegment(sketch, "E3731", {"start": v(-30.42, 1.43) * mm, "end": v(-30.46, 1.39) * mm});
            skLineSegment(sketch, "E3732", {"start": v(-30.46, 1.39) * mm, "end": v(-30.5, 1.37) * mm});
            skLineSegment(sketch, "E3733", {"start": v(-30.5, 1.37) * mm, "end": v(-30.54, 1.35) * mm});
            skLineSegment(sketch, "E3734", {"start": v(-30.54, 1.35) * mm, "end": v(-30.58, 1.34) * mm});
            skLineSegment(sketch, "E3735", {"start": v(-30.58, 1.34) * mm, "end": v(-30.63, 1.33) * mm});
            skLineSegment(sketch, "E3736", {"start": v(-30.63, 1.33) * mm, "end": v(-30.67, 1.31) * mm});
            skLineSegment(sketch, "E3737", {"start": v(-30.67, 1.31) * mm, "end": v(-30.68, 1.27) * mm});
            skLineSegment(sketch, "E3738", {"start": v(-30.68, 1.27) * mm, "end": v(-30.69, 1.15) * mm});
            skLineSegment(sketch, "E3739", {"start": v(-30.69, 1.15) * mm, "end": v(-30.68, 1.1) * mm});
            skLineSegment(sketch, "E3740", {"start": v(-30.68, 1.1) * mm, "end": v(-30.64, 1.08) * mm});
            skLineSegment(sketch, "E3741", {"start": v(-30.64, 1.08) * mm, "end": v(-30.6, 1.07) * mm});
            skLineSegment(sketch, "E3742", {"start": v(-30.6, 1.07) * mm, "end": v(-30.55, 1.05) * mm});
            skLineSegment(sketch, "E3743", {"start": v(-30.55, 1.05) * mm, "end": v(-30.51, 1.03) * mm});
            skLineSegment(sketch, "E3744", {"start": v(-30.51, 1.03) * mm, "end": v(-30.48, 1) * mm});
            skLineSegment(sketch, "E3745", {"start": v(-30.48, 1) * mm, "end": v(-30.44, 0.96) * mm});
            skLineSegment(sketch, "E3746", {"start": v(-30.44, 0.96) * mm, "end": v(-30.4, 0.9) * mm});
            skLineSegment(sketch, "E3747", {"start": v(-30.4, 0.9) * mm, "end": v(-30.4, 0.85) * mm});
            skLineSegment(sketch, "E3748", {"start": v(-30.4, 0.85) * mm, "end": v(-30.39, 0.8) * mm});
            skLineSegment(sketch, "E3749", {"start": v(-30.39, 0.8) * mm, "end": v(-30.4, 0.74) * mm});
            skLineSegment(sketch, "E3750", {"start": v(-30.4, 0.74) * mm, "end": v(-30.42, 0.68) * mm});
            skLineSegment(sketch, "E3751", {"start": v(-30.42, 0.68) * mm, "end": v(-30.45, 0.63) * mm});
            skLineSegment(sketch, "E3752", {"start": v(-30.45, 0.63) * mm, "end": v(-30.49, 0.6) * mm});
            skLineSegment(sketch, "E3753", {"start": v(-30.49, 0.6) * mm, "end": v(-30.53, 0.57) * mm});
            skLineSegment(sketch, "E3754", {"start": v(-30.53, 0.57) * mm, "end": v(-30.57, 0.55) * mm});
            skLineSegment(sketch, "E3755", {"start": v(-30.57, 0.55) * mm, "end": v(-30.6, 0.54) * mm});
            skLineSegment(sketch, "E3756", {"start": v(-30.6, 0.54) * mm, "end": v(-30.65, 0.53) * mm});
            skLineSegment(sketch, "E3757", {"start": v(-30.65, 0.53) * mm, "end": v(-30.7, 0.5) * mm});
            skLineSegment(sketch, "E3758", {"start": v(-30.7, 0.5) * mm, "end": v(-30.7, 0.46) * mm});
            skLineSegment(sketch, "E3759", {"start": v(-30.7, 0.46) * mm, "end": v(-30.7, 0.34) * mm});
            skLineSegment(sketch, "E3760", {"start": v(-30.7, 0.34) * mm, "end": v(-30.7, 0.3) * mm});
            skLineSegment(sketch, "E3761", {"start": v(-30.7, 0.3) * mm, "end": v(-30.66, 0.27) * mm});
            skLineSegment(sketch, "E3762", {"start": v(-30.66, 0.27) * mm, "end": v(-30.61, 0.26) * mm});
            skLineSegment(sketch, "E3763", {"start": v(-30.61, 0.26) * mm, "end": v(-30.57, 0.25) * mm});
            skLineSegment(sketch, "E3764", {"start": v(-30.57, 0.25) * mm, "end": v(-30.53, 0.23) * mm});
            skLineSegment(sketch, "E3765", {"start": v(-30.53, 0.23) * mm, "end": v(-30.5, 0.2) * mm});
            skLineSegment(sketch, "E3766", {"start": v(-30.5, 0.2) * mm, "end": v(-30.45, 0.16) * mm});
            skLineSegment(sketch, "E3767", {"start": v(-30.45, 0.16) * mm, "end": v(-30.42, 0.11) * mm});
            skLineSegment(sketch, "E3768", {"start": v(-30.42, 0.11) * mm, "end": v(-30.4, 0.06) * mm});
            skLineSegment(sketch, "E3769", {"start": v(-30.4, 0.06) * mm, "end": v(-30.4, 0) * mm});
            skLineSegment(sketch, "E3770", {"start": v(-30.4, 0) * mm, "end": v(-30.4, -0.06) * mm});
            skLineSegment(sketch, "E3771", {"start": v(-30.4, -0.06) * mm, "end": v(-30.42, -0.11) * mm});
            skLineSegment(sketch, "E3772", {"start": v(-30.42, -0.11) * mm, "end": v(-30.45, -0.16) * mm});
            skLineSegment(sketch, "E3773", {"start": v(-30.45, -0.16) * mm, "end": v(-30.5, -0.2) * mm});
            skLineSegment(sketch, "E3774", {"start": v(-30.5, -0.2) * mm, "end": v(-30.53, -0.23) * mm});
            skLineSegment(sketch, "E3775", {"start": v(-30.53, -0.23) * mm, "end": v(-30.57, -0.25) * mm});
            skLineSegment(sketch, "E3776", {"start": v(-30.57, -0.25) * mm, "end": v(-30.61, -0.26) * mm});
            skLineSegment(sketch, "E3777", {"start": v(-30.61, -0.26) * mm, "end": v(-30.66, -0.27) * mm});
            skLineSegment(sketch, "E3778", {"start": v(-30.66, -0.27) * mm, "end": v(-30.7, -0.3) * mm});
            skLineSegment(sketch, "E3779", {"start": v(-30.7, -0.3) * mm, "end": v(-30.7, -0.34) * mm});
            skLineSegment(sketch, "E3780", {"start": v(-30.7, -0.34) * mm, "end": v(-30.7, -0.46) * mm});
            skLineSegment(sketch, "E3781", {"start": v(-30.7, -0.46) * mm, "end": v(-30.7, -0.5) * mm});
            skLineSegment(sketch, "E3782", {"start": v(-30.7, -0.5) * mm, "end": v(-30.65, -0.53) * mm});
            skLineSegment(sketch, "E3783", {"start": v(-30.65, -0.53) * mm, "end": v(-30.6, -0.54) * mm});
            skLineSegment(sketch, "E3784", {"start": v(-30.6, -0.54) * mm, "end": v(-30.57, -0.55) * mm});
            skLineSegment(sketch, "E3785", {"start": v(-30.57, -0.55) * mm, "end": v(-30.53, -0.57) * mm});
            skLineSegment(sketch, "E3786", {"start": v(-30.53, -0.57) * mm, "end": v(-30.49, -0.6) * mm});
            skLineSegment(sketch, "E3787", {"start": v(-30.49, -0.6) * mm, "end": v(-30.45, -0.63) * mm});
            skLineSegment(sketch, "E3788", {"start": v(-30.45, -0.63) * mm, "end": v(-30.42, -0.68) * mm});
            skLineSegment(sketch, "E3789", {"start": v(-30.42, -0.68) * mm, "end": v(-30.4, -0.74) * mm});
            skLineSegment(sketch, "E3790", {"start": v(-30.4, -0.74) * mm, "end": v(-30.39, -0.8) * mm});
            skLineSegment(sketch, "E3791", {"start": v(-30.39, -0.8) * mm, "end": v(-30.4, -0.85) * mm});
            skLineSegment(sketch, "E3792", {"start": v(-30.4, -0.85) * mm, "end": v(-30.4, -0.9) * mm});
            skLineSegment(sketch, "E3793", {"start": v(-30.4, -0.9) * mm, "end": v(-30.44, -0.96) * mm});
            skLineSegment(sketch, "E3794", {"start": v(-30.44, -0.96) * mm, "end": v(-30.48, -1) * mm});
            skLineSegment(sketch, "E3795", {"start": v(-30.48, -1) * mm, "end": v(-30.51, -1.03) * mm});
            skLineSegment(sketch, "E3796", {"start": v(-30.51, -1.03) * mm, "end": v(-30.55, -1.05) * mm});
            skLineSegment(sketch, "E3797", {"start": v(-30.55, -1.05) * mm, "end": v(-30.6, -1.07) * mm});
            skLineSegment(sketch, "E3798", {"start": v(-30.6, -1.07) * mm, "end": v(-30.64, -1.08) * mm});
            skLineSegment(sketch, "E3799", {"start": v(-30.64, -1.08) * mm, "end": v(-30.68, -1.1) * mm});
            skLineSegment(sketch, "E3800", {"start": v(-30.68, -1.1) * mm, "end": v(-30.69, -1.15) * mm});
            skLineSegment(sketch, "E3801", {"start": v(-30.69, -1.15) * mm, "end": v(-30.68, -1.27) * mm});
            skLineSegment(sketch, "E3802", {"start": v(-30.68, -1.27) * mm, "end": v(-30.67, -1.31) * mm});
            skLineSegment(sketch, "E3803", {"start": v(-30.67, -1.31) * mm, "end": v(-30.63, -1.33) * mm});
            skLineSegment(sketch, "E3804", {"start": v(-30.63, -1.33) * mm, "end": v(-30.58, -1.34) * mm});
            skLineSegment(sketch, "E3805", {"start": v(-30.58, -1.34) * mm, "end": v(-30.54, -1.35) * mm});
            skLineSegment(sketch, "E3806", {"start": v(-30.54, -1.35) * mm, "end": v(-30.5, -1.37) * mm});
            skLineSegment(sketch, "E3807", {"start": v(-30.5, -1.37) * mm, "end": v(-30.46, -1.39) * mm});
            skLineSegment(sketch, "E3808", {"start": v(-30.46, -1.39) * mm, "end": v(-30.42, -1.43) * mm});
            skLineSegment(sketch, "E3809", {"start": v(-30.42, -1.43) * mm, "end": v(-30.39, -1.48) * mm});
            skLineSegment(sketch, "E3810", {"start": v(-30.39, -1.48) * mm, "end": v(-30.37, -1.53) * mm});
            skLineSegment(sketch, "E3811", {"start": v(-30.37, -1.53) * mm, "end": v(-30.36, -1.6) * mm});
            skLineSegment(sketch, "E3812", {"start": v(-30.36, -1.6) * mm, "end": v(-30.36, -1.65) * mm});
            skLineSegment(sketch, "E3813", {"start": v(-30.36, -1.65) * mm, "end": v(-30.38, -1.7) * mm});
            skLineSegment(sketch, "E3814", {"start": v(-30.38, -1.7) * mm, "end": v(-30.4, -1.76) * mm});
            skLineSegment(sketch, "E3815", {"start": v(-30.4, -1.76) * mm, "end": v(-30.44, -1.8) * mm});
            skLineSegment(sketch, "E3816", {"start": v(-30.44, -1.8) * mm, "end": v(-30.48, -1.83) * mm});
            skLineSegment(sketch, "E3817", {"start": v(-30.48, -1.83) * mm, "end": v(-30.52, -1.85) * mm});
            skLineSegment(sketch, "E3818", {"start": v(-30.52, -1.85) * mm, "end": v(-30.56, -1.87) * mm});
            skLineSegment(sketch, "E3819", {"start": v(-30.56, -1.87) * mm, "end": v(-30.6, -1.88) * mm});
            skLineSegment(sketch, "E3820", {"start": v(-30.6, -1.88) * mm, "end": v(-30.64, -1.9) * mm});
            skLineSegment(sketch, "E3821", {"start": v(-30.64, -1.9) * mm, "end": v(-30.65, -1.95) * mm});
            skLineSegment(sketch, "E3822", {"start": v(-30.65, -1.95) * mm, "end": v(-30.64, -2.07) * mm});
            skLineSegment(sketch, "E3823", {"start": v(-30.64, -2.07) * mm, "end": v(-30.62, -2.11) * mm});
            skLineSegment(sketch, "E3824", {"start": v(-30.62, -2.11) * mm, "end": v(-30.58, -2.13) * mm});
            skLineSegment(sketch, "E3825", {"start": v(-30.58, -2.13) * mm, "end": v(-30.54, -2.14) * mm});
            skLineSegment(sketch, "E3826", {"start": v(-30.54, -2.14) * mm, "end": v(-30.5, -2.15) * mm});
            skLineSegment(sketch, "E3827", {"start": v(-30.5, -2.15) * mm, "end": v(-30.45, -2.17) * mm});
            skLineSegment(sketch, "E3828", {"start": v(-30.45, -2.17) * mm, "end": v(-30.41, -2.19) * mm});
            skLineSegment(sketch, "E3829", {"start": v(-30.41, -2.19) * mm, "end": v(-30.37, -2.23) * mm});
            skLineSegment(sketch, "E3830", {"start": v(-30.37, -2.23) * mm, "end": v(-30.34, -2.27) * mm});
            skLineSegment(sketch, "E3831", {"start": v(-30.34, -2.27) * mm, "end": v(-30.32, -2.33) * mm});
            skLineSegment(sketch, "E3832", {"start": v(-30.32, -2.33) * mm, "end": v(-30.3, -2.39) * mm});
            skLineSegment(sketch, "E3833", {"start": v(-30.3, -2.39) * mm, "end": v(-30.3, -2.44) * mm});
            skLineSegment(sketch, "E3834", {"start": v(-30.3, -2.44) * mm, "end": v(-30.32, -2.5) * mm});
            skLineSegment(sketch, "E3835", {"start": v(-30.32, -2.5) * mm, "end": v(-30.34, -2.55) * mm});
            skLineSegment(sketch, "E3836", {"start": v(-30.34, -2.55) * mm, "end": v(-30.38, -2.6) * mm});
            skLineSegment(sketch, "E3837", {"start": v(-30.38, -2.6) * mm, "end": v(-30.42, -2.63) * mm});
            skLineSegment(sketch, "E3838", {"start": v(-30.42, -2.63) * mm, "end": v(-30.46, -2.65) * mm});
            skLineSegment(sketch, "E3839", {"start": v(-30.46, -2.65) * mm, "end": v(-30.5, -2.67) * mm});
            skLineSegment(sketch, "E3840", {"start": v(-30.5, -2.67) * mm, "end": v(-30.54, -2.68) * mm});
            skLineSegment(sketch, "E3841", {"start": v(-30.54, -2.68) * mm, "end": v(-30.58, -2.7) * mm});
            skLineSegment(sketch, "E3842", {"start": v(-30.58, -2.7) * mm, "end": v(-30.59, -2.75) * mm});
            skLineSegment(sketch, "E3843", {"start": v(-30.59, -2.75) * mm, "end": v(-30.58, -2.87) * mm});
            skLineSegment(sketch, "E3844", {"start": v(-30.58, -2.87) * mm, "end": v(-30.56, -2.91) * mm});
            skLineSegment(sketch, "E3845", {"start": v(-30.56, -2.91) * mm, "end": v(-30.52, -2.93) * mm});
            skLineSegment(sketch, "E3846", {"start": v(-30.52, -2.93) * mm, "end": v(-30.47, -2.94) * mm});
            skLineSegment(sketch, "E3847", {"start": v(-30.47, -2.94) * mm, "end": v(-30.43, -2.95) * mm});
            skLineSegment(sketch, "E3848", {"start": v(-30.43, -2.95) * mm, "end": v(-30.39, -2.96) * mm});
            skLineSegment(sketch, "E3849", {"start": v(-30.39, -2.96) * mm, "end": v(-30.35, -2.98) * mm});
            skLineSegment(sketch, "E3850", {"start": v(-30.35, -2.98) * mm, "end": v(-30.3, -3.02) * mm});
            skLineSegment(sketch, "E3851", {"start": v(-30.3, -3.02) * mm, "end": v(-30.27, -3.07) * mm});
            skLineSegment(sketch, "E3852", {"start": v(-30.27, -3.07) * mm, "end": v(-30.25, -3.12) * mm});
            skLineSegment(sketch, "E3853", {"start": v(-30.25, -3.12) * mm, "end": v(-30.23, -3.18) * mm});
            skLineSegment(sketch, "E3854", {"start": v(-30.23, -3.18) * mm, "end": v(-30.23, -3.24) * mm});
            skLineSegment(sketch, "E3855", {"start": v(-30.23, -3.24) * mm, "end": v(-30.24, -3.3) * mm});
            skLineSegment(sketch, "E3856", {"start": v(-30.24, -3.3) * mm, "end": v(-30.27, -3.35) * mm});
            skLineSegment(sketch, "E3857", {"start": v(-30.27, -3.35) * mm, "end": v(-30.3, -3.4) * mm});
            skLineSegment(sketch, "E3858", {"start": v(-30.3, -3.4) * mm, "end": v(-30.34, -3.42) * mm});
            skLineSegment(sketch, "E3859", {"start": v(-30.34, -3.42) * mm, "end": v(-30.38, -3.44) * mm});
            skLineSegment(sketch, "E3860", {"start": v(-30.38, -3.44) * mm, "end": v(-30.42, -3.46) * mm});
            skLineSegment(sketch, "E3861", {"start": v(-30.42, -3.46) * mm, "end": v(-30.46, -3.48) * mm});
            skLineSegment(sketch, "E3862", {"start": v(-30.46, -3.48) * mm, "end": v(-30.5, -3.5) * mm});
            skLineSegment(sketch, "E3863", {"start": v(-30.5, -3.5) * mm, "end": v(-30.5, -3.55) * mm});
            skLineSegment(sketch, "E3864", {"start": v(-30.5, -3.55) * mm, "end": v(-30.5, -3.67) * mm});
            skLineSegment(sketch, "E3865", {"start": v(-30.5, -3.67) * mm, "end": v(-30.47, -3.71) * mm});
            skLineSegment(sketch, "E3866", {"start": v(-30.47, -3.71) * mm, "end": v(-30.43, -3.73) * mm});
            skLineSegment(sketch, "E3867", {"start": v(-30.43, -3.73) * mm, "end": v(-30.39, -3.73) * mm});
            skLineSegment(sketch, "E3868", {"start": v(-30.39, -3.73) * mm, "end": v(-30.34, -3.74) * mm});
            skLineSegment(sketch, "E3869", {"start": v(-30.34, -3.74) * mm, "end": v(-30.3, -3.76) * mm});
            skLineSegment(sketch, "E3870", {"start": v(-30.3, -3.76) * mm, "end": v(-30.26, -3.78) * mm});
            skLineSegment(sketch, "E3871", {"start": v(-30.26, -3.78) * mm, "end": v(-30.21, -3.81) * mm});
            skLineSegment(sketch, "E3872", {"start": v(-30.21, -3.81) * mm, "end": v(-30.18, -3.86) * mm});
            skLineSegment(sketch, "E3873", {"start": v(-30.18, -3.86) * mm, "end": v(-30.15, -3.91) * mm});
            skLineSegment(sketch, "E3874", {"start": v(-30.15, -3.91) * mm, "end": v(-30.14, -3.97) * mm});
            skLineSegment(sketch, "E3875", {"start": v(-30.14, -3.97) * mm, "end": v(-30.14, -4.03) * mm});
            skLineSegment(sketch, "E3876", {"start": v(-30.14, -4.03) * mm, "end": v(-30.15, -4.08) * mm});
            skLineSegment(sketch, "E3877", {"start": v(-30.15, -4.08) * mm, "end": v(-30.17, -4.14) * mm});
            skLineSegment(sketch, "E3878", {"start": v(-30.17, -4.14) * mm, "end": v(-30.2, -4.18) * mm});
            skLineSegment(sketch, "E3879", {"start": v(-30.2, -4.18) * mm, "end": v(-30.24, -4.21) * mm});
            skLineSegment(sketch, "E3880", {"start": v(-30.24, -4.21) * mm, "end": v(-30.28, -4.24) * mm});
            skLineSegment(sketch, "E3881", {"start": v(-30.28, -4.24) * mm, "end": v(-30.32, -4.26) * mm});
            skLineSegment(sketch, "E3882", {"start": v(-30.32, -4.26) * mm, "end": v(-30.36, -4.27) * mm});
            skLineSegment(sketch, "E3883", {"start": v(-30.36, -4.27) * mm, "end": v(-30.4, -4.3) * mm});
            skLineSegment(sketch, "E3884", {"start": v(-30.4, -4.3) * mm, "end": v(-30.4, -4.35) * mm});
            skLineSegment(sketch, "E3885", {"start": v(-30.4, -4.35) * mm, "end": v(-30.38, -4.47) * mm});
            skLineSegment(sketch, "E3886", {"start": v(-30.38, -4.47) * mm, "end": v(-30.36, -4.5) * mm});
            skLineSegment(sketch, "E3887", {"start": v(-30.36, -4.5) * mm, "end": v(-30.32, -4.53) * mm});
            skLineSegment(sketch, "E3888", {"start": v(-30.32, -4.53) * mm, "end": v(-30.28, -4.53) * mm});
            skLineSegment(sketch, "E3889", {"start": v(-30.28, -4.53) * mm, "end": v(-30.23, -4.54) * mm});
            skLineSegment(sketch, "E3890", {"start": v(-30.23, -4.54) * mm, "end": v(-30.19, -4.55) * mm});
            skLineSegment(sketch, "E3891", {"start": v(-30.19, -4.55) * mm, "end": v(-30.15, -4.57) * mm});
            skLineSegment(sketch, "E3892", {"start": v(-30.15, -4.57) * mm, "end": v(-30.1, -4.6) * mm});
            skLineSegment(sketch, "E3893", {"start": v(-30.1, -4.6) * mm, "end": v(-30.07, -4.65) * mm});
            skLineSegment(sketch, "E3894", {"start": v(-30.07, -4.65) * mm, "end": v(-30.04, -4.7) * mm});
            skLineSegment(sketch, "E3895", {"start": v(-30.04, -4.7) * mm, "end": v(-30.03, -4.76) * mm});
            skLineSegment(sketch, "E3896", {"start": v(-30.03, -4.76) * mm, "end": v(-30.02, -4.81) * mm});
            skLineSegment(sketch, "E3897", {"start": v(-30.02, -4.81) * mm, "end": v(-30.03, -4.87) * mm});
            skLineSegment(sketch, "E3898", {"start": v(-30.03, -4.87) * mm, "end": v(-30.05, -4.93) * mm});
            skLineSegment(sketch, "E3899", {"start": v(-30.05, -4.93) * mm, "end": v(-30.08, -4.97) * mm});
            skLineSegment(sketch, "E3900", {"start": v(-30.08, -4.97) * mm, "end": v(-30.12, -5) * mm});
            skLineSegment(sketch, "E3901", {"start": v(-30.12, -5) * mm, "end": v(-30.15, -5.03) * mm});
            skLineSegment(sketch, "E3902", {"start": v(-30.15, -5.03) * mm, "end": v(-30.2, -5.05) * mm});
            skLineSegment(sketch, "E3903", {"start": v(-30.2, -5.05) * mm, "end": v(-30.24, -5.07) * mm});
            skLineSegment(sketch, "E3904", {"start": v(-30.24, -5.07) * mm, "end": v(-30.27, -5.1) * mm});
            skLineSegment(sketch, "E3905", {"start": v(-30.27, -5.1) * mm, "end": v(-30.28, -5.14) * mm});
            skLineSegment(sketch, "E3906", {"start": v(-30.28, -5.14) * mm, "end": v(-30.26, -5.26) * mm});
            skLineSegment(sketch, "E3907", {"start": v(-30.26, -5.26) * mm, "end": v(-30.23, -5.3) * mm});
            skLineSegment(sketch, "E3908", {"start": v(-30.23, -5.3) * mm, "end": v(-30.2, -5.32) * mm});
            skLineSegment(sketch, "E3909", {"start": v(-30.2, -5.32) * mm, "end": v(-30.15, -5.32) * mm});
            skLineSegment(sketch, "E3910", {"start": v(-30.15, -5.32) * mm, "end": v(-30.1, -5.32) * mm});
            skLineSegment(sketch, "E3911", {"start": v(-30.1, -5.32) * mm, "end": v(-30.06, -5.34) * mm});
            skLineSegment(sketch, "E3912", {"start": v(-30.06, -5.34) * mm, "end": v(-30.02, -5.35) * mm});
            skLineSegment(sketch, "E3913", {"start": v(-30.02, -5.35) * mm, "end": v(-29.97, -5.39) * mm});
            skLineSegment(sketch, "E3914", {"start": v(-29.97, -5.39) * mm, "end": v(-29.93, -5.43) * mm});
            skLineSegment(sketch, "E3915", {"start": v(-29.93, -5.43) * mm, "end": v(-29.9, -5.48) * mm});
            skLineSegment(sketch, "E3916", {"start": v(-29.9, -5.48) * mm, "end": v(-29.9, -5.54) * mm});
            skLineSegment(sketch, "E3917", {"start": v(-29.9, -5.54) * mm, "end": v(-29.89, -5.6) * mm});
            skLineSegment(sketch, "E3918", {"start": v(-29.89, -5.6) * mm, "end": v(-29.9, -5.66) * mm});
            skLineSegment(sketch, "E3919", {"start": v(-29.9, -5.66) * mm, "end": v(-29.91, -5.71) * mm});
            skLineSegment(sketch, "E3920", {"start": v(-29.91, -5.71) * mm, "end": v(-29.94, -5.76) * mm});
            skLineSegment(sketch, "E3921", {"start": v(-29.94, -5.76) * mm, "end": v(-29.98, -5.8) * mm});
            skLineSegment(sketch, "E3922", {"start": v(-29.98, -5.8) * mm, "end": v(-30.01, -5.82) * mm});
            skLineSegment(sketch, "E3923", {"start": v(-30.01, -5.82) * mm, "end": v(-30.05, -5.84) * mm});
            skLineSegment(sketch, "E3924", {"start": v(-30.05, -5.84) * mm, "end": v(-30.1, -5.86) * mm});
            skLineSegment(sketch, "E3925", {"start": v(-30.1, -5.86) * mm, "end": v(-30.13, -5.88) * mm});
            skLineSegment(sketch, "E3926", {"start": v(-30.13, -5.88) * mm, "end": v(-30.13, -5.93) * mm});
            skLineSegment(sketch, "E3927", {"start": v(-30.13, -5.93) * mm, "end": v(-30.1, -6.05) * mm});
            skLineSegment(sketch, "E3928", {"start": v(-30.1, -6.05) * mm, "end": v(-30.08, -6.1) * mm});
            skLineSegment(sketch, "E3929", {"start": v(-30.08, -6.1) * mm, "end": v(-30.04, -6.1) * mm});
            skLineSegment(sketch, "E3930", {"start": v(-30.04, -6.1) * mm, "end": v(-30, -6.1) * mm});
            skLineSegment(sketch, "E3931", {"start": v(-30, -6.1) * mm, "end": v(-29.95, -6.11) * mm});
            skLineSegment(sketch, "E3932", {"start": v(-29.95, -6.11) * mm, "end": v(-29.91, -6.12) * mm});
            skLineSegment(sketch, "E3933", {"start": v(-29.91, -6.12) * mm, "end": v(-29.87, -6.14) * mm});
            skLineSegment(sketch, "E3934", {"start": v(-29.87, -6.14) * mm, "end": v(-29.82, -6.17) * mm});
            skLineSegment(sketch, "E3935", {"start": v(-29.82, -6.17) * mm, "end": v(-29.78, -6.21) * mm});
            skLineSegment(sketch, "E3936", {"start": v(-29.78, -6.21) * mm, "end": v(-29.75, -6.26) * mm});
            skLineSegment(sketch, "E3937", {"start": v(-29.75, -6.26) * mm, "end": v(-29.74, -6.32) * mm});
            skLineSegment(sketch, "E3938", {"start": v(-29.74, -6.32) * mm, "end": v(-29.73, -6.38) * mm});
            skLineSegment(sketch, "E3939", {"start": v(-29.73, -6.38) * mm, "end": v(-29.73, -6.44) * mm});
            skLineSegment(sketch, "E3940", {"start": v(-29.73, -6.44) * mm, "end": v(-29.75, -6.5) * mm});
            skLineSegment(sketch, "E3941", {"start": v(-29.75, -6.5) * mm, "end": v(-29.78, -6.54) * mm});
            skLineSegment(sketch, "E3942", {"start": v(-29.78, -6.54) * mm, "end": v(-29.81, -6.57) * mm});
            skLineSegment(sketch, "E3943", {"start": v(-29.81, -6.57) * mm, "end": v(-29.85, -6.6) * mm});
            skLineSegment(sketch, "E3944", {"start": v(-29.85, -6.6) * mm, "end": v(-29.89, -6.62) * mm});
            skLineSegment(sketch, "E3945", {"start": v(-29.89, -6.62) * mm, "end": v(-29.93, -6.64) * mm});
            skLineSegment(sketch, "E3946", {"start": v(-29.93, -6.64) * mm, "end": v(-29.96, -6.67) * mm});
            skLineSegment(sketch, "E3947", {"start": v(-29.96, -6.67) * mm, "end": v(-29.97, -6.72) * mm});
            skLineSegment(sketch, "E3948", {"start": v(-29.97, -6.72) * mm, "end": v(-29.94, -6.84) * mm});
            skLineSegment(sketch, "E3949", {"start": v(-29.94, -6.84) * mm, "end": v(-29.91, -6.88) * mm});
            skLineSegment(sketch, "E3950", {"start": v(-29.91, -6.88) * mm, "end": v(-29.87, -6.9) * mm});
            skLineSegment(sketch, "E3951", {"start": v(-29.87, -6.9) * mm, "end": v(-29.83, -6.89) * mm});
            skLineSegment(sketch, "E3952", {"start": v(-29.83, -6.89) * mm, "end": v(-29.78, -6.9) * mm});
            skLineSegment(sketch, "E3953", {"start": v(-29.78, -6.9) * mm, "end": v(-29.74, -6.9) * mm});
            skLineSegment(sketch, "E3954", {"start": v(-29.74, -6.9) * mm, "end": v(-29.7, -6.92) * mm});
            skLineSegment(sketch, "E3955", {"start": v(-29.7, -6.92) * mm, "end": v(-29.65, -6.95) * mm});
            skLineSegment(sketch, "E3956", {"start": v(-29.65, -6.95) * mm, "end": v(-29.6, -7) * mm});
            skLineSegment(sketch, "E3957", {"start": v(-29.6, -7) * mm, "end": v(-29.58, -7.04) * mm});
            skLineSegment(sketch, "E3958", {"start": v(-29.58, -7.04) * mm, "end": v(-29.56, -7.1) * mm});
            skLineSegment(sketch, "E3959", {"start": v(-29.56, -7.1) * mm, "end": v(-29.55, -7.15) * mm});
            skLineSegment(sketch, "E3960", {"start": v(-29.55, -7.15) * mm, "end": v(-29.56, -7.21) * mm});
            skLineSegment(sketch, "E3961", {"start": v(-29.56, -7.21) * mm, "end": v(-29.57, -7.27) * mm});
            skLineSegment(sketch, "E3962", {"start": v(-29.57, -7.27) * mm, "end": v(-29.6, -7.32) * mm});
            skLineSegment(sketch, "E3963", {"start": v(-29.6, -7.32) * mm, "end": v(-29.63, -7.35) * mm});
            skLineSegment(sketch, "E3964", {"start": v(-29.63, -7.35) * mm, "end": v(-29.67, -7.38) * mm});
            skLineSegment(sketch, "E3965", {"start": v(-29.67, -7.38) * mm, "end": v(-29.7, -7.4) * mm});
            skLineSegment(sketch, "E3966", {"start": v(-29.7, -7.4) * mm, "end": v(-29.75, -7.42) * mm});
            skLineSegment(sketch, "E3967", {"start": v(-29.75, -7.42) * mm, "end": v(-29.78, -7.45) * mm});
            skLineSegment(sketch, "E3968", {"start": v(-29.78, -7.45) * mm, "end": v(-29.78, -7.5) * mm});
            skLineSegment(sketch, "E3969", {"start": v(-29.78, -7.5) * mm, "end": v(-29.75, -7.62) * mm});
            skLineSegment(sketch, "E3970", {"start": v(-29.75, -7.62) * mm, "end": v(-29.72, -7.66) * mm});
            skLineSegment(sketch, "E3971", {"start": v(-29.72, -7.66) * mm, "end": v(-29.68, -7.67) * mm});
            skLineSegment(sketch, "E3972", {"start": v(-29.68, -7.67) * mm, "end": v(-29.64, -7.67) * mm});
            skLineSegment(sketch, "E3973", {"start": v(-29.64, -7.67) * mm, "end": v(-29.6, -7.67) * mm});
            skLineSegment(sketch, "E3974", {"start": v(-29.6, -7.67) * mm, "end": v(-29.55, -7.68) * mm});
            skLineSegment(sketch, "E3975", {"start": v(-29.55, -7.68) * mm, "end": v(-29.5, -7.7) * mm});
            skLineSegment(sketch, "E3976", {"start": v(-29.5, -7.7) * mm, "end": v(-29.46, -7.72) * mm});
            skLineSegment(sketch, "E3977", {"start": v(-29.46, -7.72) * mm, "end": v(-29.42, -7.76) * mm});
            skLineSegment(sketch, "E3978", {"start": v(-29.42, -7.76) * mm, "end": v(-29.39, -7.81) * mm});
            skLineSegment(sketch, "E3979", {"start": v(-29.39, -7.81) * mm, "end": v(-29.36, -7.87) * mm});
            skLineSegment(sketch, "E3980", {"start": v(-29.36, -7.87) * mm, "end": v(-29.35, -7.93) * mm});
            skLineSegment(sketch, "E3981", {"start": v(-29.35, -7.93) * mm, "end": v(-29.36, -7.98) * mm});
            skLineSegment(sketch, "E3982", {"start": v(-29.36, -7.98) * mm, "end": v(-29.37, -8.04) * mm});
            skLineSegment(sketch, "E3983", {"start": v(-29.37, -8.04) * mm, "end": v(-29.4, -8.1) * mm});
            skLineSegment(sketch, "E3984", {"start": v(-29.4, -8.1) * mm, "end": v(-29.43, -8.12) * mm});
            skLineSegment(sketch, "E3985", {"start": v(-29.43, -8.12) * mm, "end": v(-29.46, -8.15) * mm});
            skLineSegment(sketch, "E3986", {"start": v(-29.46, -8.15) * mm, "end": v(-29.5, -8.18) * mm});
            skLineSegment(sketch, "E3987", {"start": v(-29.5, -8.18) * mm, "end": v(-29.54, -8.2) * mm});
            skLineSegment(sketch, "E3988", {"start": v(-29.54, -8.2) * mm, "end": v(-29.57, -8.23) * mm});
            skLineSegment(sketch, "E3989", {"start": v(-29.57, -8.23) * mm, "end": v(-29.57, -8.28) * mm});
            skLineSegment(sketch, "E3990", {"start": v(-29.57, -8.28) * mm, "end": v(-29.54, -8.4) * mm});
            skLineSegment(sketch, "E3991", {"start": v(-29.54, -8.4) * mm, "end": v(-29.51, -8.43) * mm});
            skLineSegment(sketch, "E3992", {"start": v(-29.51, -8.43) * mm, "end": v(-29.47, -8.44) * mm});
            skLineSegment(sketch, "E3993", {"start": v(-29.47, -8.44) * mm, "end": v(-29.43, -8.44) * mm});
            skLineSegment(sketch, "E3994", {"start": v(-29.43, -8.44) * mm, "end": v(-29.38, -8.44) * mm});
            skLineSegment(sketch, "E3995", {"start": v(-29.38, -8.44) * mm, "end": v(-29.34, -8.45) * mm});
            skLineSegment(sketch, "E3996", {"start": v(-29.34, -8.45) * mm, "end": v(-29.3, -8.46) * mm});
            skLineSegment(sketch, "E3997", {"start": v(-29.3, -8.46) * mm, "end": v(-29.24, -8.5) * mm});
            skLineSegment(sketch, "E3998", {"start": v(-29.24, -8.5) * mm, "end": v(-29.2, -8.53) * mm});
            skLineSegment(sketch, "E3999", {"start": v(-29.2, -8.53) * mm, "end": v(-29.17, -8.58) * mm});
            skLineSegment(sketch, "E4000", {"start": v(-29.17, -8.58) * mm, "end": v(-29.15, -8.63) * mm});
            skLineSegment(sketch, "E4001", {"start": v(-29.15, -8.63) * mm, "end": v(-29.14, -8.7) * mm});
            skLineSegment(sketch, "E4002", {"start": v(-29.14, -8.7) * mm, "end": v(-29.14, -8.75) * mm});
            skLineSegment(sketch, "E4003", {"start": v(-29.14, -8.75) * mm, "end": v(-29.15, -8.8) * mm});
            skLineSegment(sketch, "E4004", {"start": v(-29.15, -8.8) * mm, "end": v(-29.18, -8.86) * mm});
            skLineSegment(sketch, "E4005", {"start": v(-29.18, -8.86) * mm, "end": v(-29.2, -8.9) * mm});
            skLineSegment(sketch, "E4006", {"start": v(-29.2, -8.9) * mm, "end": v(-29.24, -8.92) * mm});
            skLineSegment(sketch, "E4007", {"start": v(-29.24, -8.92) * mm, "end": v(-29.28, -8.95) * mm});
            skLineSegment(sketch, "E4008", {"start": v(-29.28, -8.95) * mm, "end": v(-29.32, -8.97) * mm});
            skLineSegment(sketch, "E4009", {"start": v(-29.32, -8.97) * mm, "end": v(-29.35, -9) * mm});
            skLineSegment(sketch, "E4010", {"start": v(-29.35, -9) * mm, "end": v(-29.35, -9.05) * mm});
            skLineSegment(sketch, "E4011", {"start": v(-29.35, -9.05) * mm, "end": v(-29.31, -9.16) * mm});
            skLineSegment(sketch, "E4012", {"start": v(-29.31, -9.16) * mm, "end": v(-29.28, -9.2) * mm});
            skLineSegment(sketch, "E4013", {"start": v(-29.28, -9.2) * mm, "end": v(-29.24, -9.21) * mm});
            skLineSegment(sketch, "E4014", {"start": v(-29.24, -9.21) * mm, "end": v(-29.2, -9.2) * mm});
            skLineSegment(sketch, "E4015", {"start": v(-29.2, -9.2) * mm, "end": v(-29.15, -9.2) * mm});
            skLineSegment(sketch, "E4016", {"start": v(-29.15, -9.2) * mm, "end": v(-29.1, -9.21) * mm});
            skLineSegment(sketch, "E4017", {"start": v(-29.1, -9.21) * mm, "end": v(-29.06, -9.23) * mm});
            skLineSegment(sketch, "E4018", {"start": v(-29.06, -9.23) * mm, "end": v(-29.01, -9.25) * mm});
            skLineSegment(sketch, "E4019", {"start": v(-29.01, -9.25) * mm, "end": v(-28.97, -9.3) * mm});
            skLineSegment(sketch, "E4020", {"start": v(-28.97, -9.3) * mm, "end": v(-28.94, -9.34) * mm});
            skLineSegment(sketch, "E4021", {"start": v(-28.94, -9.34) * mm, "end": v(-28.91, -9.4) * mm});
            skLineSegment(sketch, "E4022", {"start": v(-28.91, -9.4) * mm, "end": v(-28.9, -9.45) * mm});
            skLineSegment(sketch, "E4023", {"start": v(-28.9, -9.45) * mm, "end": v(-28.9, -9.5) * mm});
            skLineSegment(sketch, "E4024", {"start": v(-28.9, -9.5) * mm, "end": v(-28.91, -9.57) * mm});
            skLineSegment(sketch, "E4025", {"start": v(-28.91, -9.57) * mm, "end": v(-28.93, -9.62) * mm});
            skLineSegment(sketch, "E4026", {"start": v(-28.93, -9.62) * mm, "end": v(-28.96, -9.65) * mm});
            skLineSegment(sketch, "E4027", {"start": v(-28.96, -9.65) * mm, "end": v(-29, -9.68) * mm});
            skLineSegment(sketch, "E4028", {"start": v(-29, -9.68) * mm, "end": v(-29.03, -9.71) * mm});
            skLineSegment(sketch, "E4029", {"start": v(-29.03, -9.71) * mm, "end": v(-29.07, -9.73) * mm});
            skLineSegment(sketch, "E4030", {"start": v(-29.07, -9.73) * mm, "end": v(-29.1, -9.77) * mm});
            skLineSegment(sketch, "E4031", {"start": v(-29.1, -9.77) * mm, "end": v(-29.1, -9.81) * mm});
            skLineSegment(sketch, "E4032", {"start": v(-29.1, -9.81) * mm, "end": v(-29.06, -9.93) * mm});
            skLineSegment(sketch, "E4033", {"start": v(-29.06, -9.93) * mm, "end": v(-29.03, -9.97) * mm});
            skLineSegment(sketch, "E4034", {"start": v(-29.03, -9.97) * mm, "end": v(-28.99, -9.98) * mm});
            skLineSegment(sketch, "E4035", {"start": v(-28.99, -9.98) * mm, "end": v(-28.94, -9.97) * mm});
            skLineSegment(sketch, "E4036", {"start": v(-28.94, -9.97) * mm, "end": v(-28.9, -9.97) * mm});
            skLineSegment(sketch, "E4037", {"start": v(-28.9, -9.97) * mm, "end": v(-28.86, -9.97) * mm});
            skLineSegment(sketch, "E4038", {"start": v(-28.86, -9.97) * mm, "end": v(-28.81, -9.98) * mm});
            skLineSegment(sketch, "E4039", {"start": v(-28.81, -9.98) * mm, "end": v(-28.76, -10.01) * mm});
            skLineSegment(sketch, "E4040", {"start": v(-28.76, -10.01) * mm, "end": v(-28.72, -10.05) * mm});
            skLineSegment(sketch, "E4041", {"start": v(-28.72, -10.05) * mm, "end": v(-28.68, -10.1) * mm});
            skLineSegment(sketch, "E4042", {"start": v(-28.68, -10.1) * mm, "end": v(-28.66, -10.15) * mm});
            skLineSegment(sketch, "E4043", {"start": v(-28.66, -10.15) * mm, "end": v(-28.64, -10.2) * mm});
            skLineSegment(sketch, "E4044", {"start": v(-28.64, -10.2) * mm, "end": v(-28.64, -10.26) * mm});
            skLineSegment(sketch, "E4045", {"start": v(-28.64, -10.26) * mm, "end": v(-28.65, -10.32) * mm});
            skLineSegment(sketch, "E4046", {"start": v(-28.65, -10.32) * mm, "end": v(-28.67, -10.37) * mm});
            skLineSegment(sketch, "E4047", {"start": v(-28.67, -10.37) * mm, "end": v(-28.7, -10.4) * mm});
            skLineSegment(sketch, "E4048", {"start": v(-28.7, -10.4) * mm, "end": v(-28.73, -10.44) * mm});
            skLineSegment(sketch, "E4049", {"start": v(-28.73, -10.44) * mm, "end": v(-28.77, -10.47) * mm});
            skLineSegment(sketch, "E4050", {"start": v(-28.77, -10.47) * mm, "end": v(-28.8, -10.5) * mm});
            skLineSegment(sketch, "E4051", {"start": v(-28.8, -10.5) * mm, "end": v(-28.83, -10.53) * mm});
            skLineSegment(sketch, "E4052", {"start": v(-28.83, -10.53) * mm, "end": v(-28.83, -10.57) * mm});
            skLineSegment(sketch, "E4053", {"start": v(-28.83, -10.57) * mm, "end": v(-28.8, -10.69) * mm});
            skLineSegment(sketch, "E4054", {"start": v(-28.8, -10.69) * mm, "end": v(-28.76, -10.72) * mm});
            skLineSegment(sketch, "E4055", {"start": v(-28.76, -10.72) * mm, "end": v(-28.72, -10.73) * mm});
            skLineSegment(sketch, "E4056", {"start": v(-28.72, -10.73) * mm, "end": v(-28.67, -10.72) * mm});
            skLineSegment(sketch, "E4057", {"start": v(-28.67, -10.72) * mm, "end": v(-28.63, -10.72) * mm});
            skLineSegment(sketch, "E4058", {"start": v(-28.63, -10.72) * mm, "end": v(-28.58, -10.73) * mm});
            skLineSegment(sketch, "E4059", {"start": v(-28.58, -10.73) * mm, "end": v(-28.54, -10.73) * mm});
            skLineSegment(sketch, "E4060", {"start": v(-28.54, -10.73) * mm, "end": v(-28.49, -10.76) * mm});
            skLineSegment(sketch, "E4061", {"start": v(-28.49, -10.76) * mm, "end": v(-28.44, -10.8) * mm});
            skLineSegment(sketch, "E4062", {"start": v(-28.44, -10.8) * mm, "end": v(-28.4, -10.84) * mm});
            skLineSegment(sketch, "E4063", {"start": v(-28.4, -10.84) * mm, "end": v(-28.38, -10.9) * mm});
            skLineSegment(sketch, "E4064", {"start": v(-28.38, -10.9) * mm, "end": v(-28.37, -10.95) * mm});
            skLineSegment(sketch, "E4065", {"start": v(-28.37, -10.95) * mm, "end": v(-28.36, -11) * mm});
            skLineSegment(sketch, "E4066", {"start": v(-28.36, -11) * mm, "end": v(-28.37, -11.07) * mm});
            skLineSegment(sketch, "E4067", {"start": v(-28.37, -11.07) * mm, "end": v(-28.4, -11.12) * mm});
            skLineSegment(sketch, "E4068", {"start": v(-28.4, -11.12) * mm, "end": v(-28.42, -11.16) * mm});
            skLineSegment(sketch, "E4069", {"start": v(-28.42, -11.16) * mm, "end": v(-28.45, -11.19) * mm});
            skLineSegment(sketch, "E4070", {"start": v(-28.45, -11.19) * mm, "end": v(-28.48, -11.22) * mm});
            skLineSegment(sketch, "E4071", {"start": v(-28.48, -11.22) * mm, "end": v(-28.52, -11.24) * mm});
            skLineSegment(sketch, "E4072", {"start": v(-28.52, -11.24) * mm, "end": v(-28.55, -11.28) * mm});
            skLineSegment(sketch, "E4073", {"start": v(-28.55, -11.28) * mm, "end": v(-28.55, -11.32) * mm});
            skLineSegment(sketch, "E4074", {"start": v(-28.55, -11.32) * mm, "end": v(-28.5, -11.44) * mm});
            skLineSegment(sketch, "E4075", {"start": v(-28.5, -11.44) * mm, "end": v(-28.47, -11.47) * mm});
            skLineSegment(sketch, "E4076", {"start": v(-28.47, -11.47) * mm, "end": v(-28.43, -11.48) * mm});
            skLineSegment(sketch, "E4077", {"start": v(-28.43, -11.48) * mm, "end": v(-28.38, -11.47) * mm});
            skLineSegment(sketch, "E4078", {"start": v(-28.38, -11.47) * mm, "end": v(-28.34, -11.47) * mm});
            skLineSegment(sketch, "E4079", {"start": v(-28.34, -11.47) * mm, "end": v(-28.3, -11.47) * mm});
            skLineSegment(sketch, "E4080", {"start": v(-28.3, -11.47) * mm, "end": v(-28.25, -11.48) * mm});
            skLineSegment(sketch, "E4081", {"start": v(-28.25, -11.48) * mm, "end": v(-28.2, -11.5) * mm});
            skLineSegment(sketch, "E4082", {"start": v(-28.2, -11.5) * mm, "end": v(-28.15, -11.54) * mm});
            skLineSegment(sketch, "E4083", {"start": v(-28.15, -11.54) * mm, "end": v(-28.11, -11.58) * mm});
            skLineSegment(sketch, "E4084", {"start": v(-28.11, -11.58) * mm, "end": v(-28.09, -11.63) * mm});
            skLineSegment(sketch, "E4085", {"start": v(-28.09, -11.63) * mm, "end": v(-28.07, -11.69) * mm});
            skLineSegment(sketch, "E4086", {"start": v(-28.07, -11.69) * mm, "end": v(-28.06, -11.75) * mm});
            skLineSegment(sketch, "E4087", {"start": v(-28.06, -11.75) * mm, "end": v(-28.07, -11.8) * mm});
            skLineSegment(sketch, "E4088", {"start": v(-28.07, -11.8) * mm, "end": v(-28.1, -11.86) * mm});
            skLineSegment(sketch, "E4089", {"start": v(-28.1, -11.86) * mm, "end": v(-28.12, -11.9) * mm});
            skLineSegment(sketch, "E4090", {"start": v(-28.12, -11.9) * mm, "end": v(-28.15, -11.93) * mm});
            skLineSegment(sketch, "E4091", {"start": v(-28.15, -11.93) * mm, "end": v(-28.18, -11.96) * mm});
            skLineSegment(sketch, "E4092", {"start": v(-28.18, -11.96) * mm, "end": v(-28.22, -11.98) * mm});
            skLineSegment(sketch, "E4093", {"start": v(-28.22, -11.98) * mm, "end": v(-28.24, -12.02) * mm});
            skLineSegment(sketch, "E4094", {"start": v(-28.24, -12.02) * mm, "end": v(-28.24, -12.07) * mm});
            skLineSegment(sketch, "E4095", {"start": v(-28.24, -12.07) * mm, "end": v(-28.2, -12.18) * mm});
            skLineSegment(sketch, "E4096", {"start": v(-28.2, -12.18) * mm, "end": v(-28.16, -12.21) * mm});
            skLineSegment(sketch, "E4097", {"start": v(-28.16, -12.21) * mm, "end": v(-28.12, -12.22) * mm});
            skLineSegment(sketch, "E4098", {"start": v(-28.12, -12.22) * mm, "end": v(-28.07, -12.2) * mm});
            skLineSegment(sketch, "E4099", {"start": v(-28.07, -12.2) * mm, "end": v(-28.03, -12.2) * mm});
            skLineSegment(sketch, "E4100", {"start": v(-28.03, -12.2) * mm, "end": v(-27.98, -12.2) * mm});
            skLineSegment(sketch, "E4101", {"start": v(-27.98, -12.2) * mm, "end": v(-27.94, -12.21) * mm});
            skLineSegment(sketch, "E4102", {"start": v(-27.94, -12.21) * mm, "end": v(-27.89, -12.24) * mm});
            skLineSegment(sketch, "E4103", {"start": v(-27.89, -12.24) * mm, "end": v(-27.84, -12.27) * mm});
            skLineSegment(sketch, "E4104", {"start": v(-27.84, -12.27) * mm, "end": v(-27.8, -12.31) * mm});
            skLineSegment(sketch, "E4105", {"start": v(-27.8, -12.31) * mm, "end": v(-27.77, -12.36) * mm});
            skLineSegment(sketch, "E4106", {"start": v(-27.77, -12.36) * mm, "end": v(-27.75, -12.42) * mm});
            skLineSegment(sketch, "E4107", {"start": v(-27.75, -12.42) * mm, "end": v(-27.75, -12.48) * mm});
            skLineSegment(sketch, "E4108", {"start": v(-27.75, -12.48) * mm, "end": v(-27.75, -12.54) * mm});
            skLineSegment(sketch, "E4109", {"start": v(-27.75, -12.54) * mm, "end": v(-27.77, -12.6) * mm});
            skLineSegment(sketch, "E4110", {"start": v(-27.77, -12.6) * mm, "end": v(-27.8, -12.63) * mm});
            skLineSegment(sketch, "E4111", {"start": v(-27.8, -12.63) * mm, "end": v(-27.83, -12.66) * mm});
            skLineSegment(sketch, "E4112", {"start": v(-27.83, -12.66) * mm, "end": v(-27.86, -12.7) * mm});
            skLineSegment(sketch, "E4113", {"start": v(-27.86, -12.7) * mm, "end": v(-27.9, -12.72) * mm});
            skLineSegment(sketch, "E4114", {"start": v(-27.9, -12.72) * mm, "end": v(-27.92, -12.75) * mm});
            skLineSegment(sketch, "E4115", {"start": v(-27.92, -12.75) * mm, "end": v(-27.91, -12.8) * mm});
            skLineSegment(sketch, "E4116", {"start": v(-27.91, -12.8) * mm, "end": v(-27.86, -12.91) * mm});
            skLineSegment(sketch, "E4117", {"start": v(-27.86, -12.91) * mm, "end": v(-27.83, -12.95) * mm});
            skLineSegment(sketch, "E4118", {"start": v(-27.83, -12.95) * mm, "end": v(-27.79, -12.95) * mm});
            skLineSegment(sketch, "E4119", {"start": v(-27.79, -12.95) * mm, "end": v(-27.74, -12.94) * mm});
            skLineSegment(sketch, "E4120", {"start": v(-27.74, -12.94) * mm, "end": v(-27.7, -12.93) * mm});
            skLineSegment(sketch, "E4121", {"start": v(-27.7, -12.93) * mm, "end": v(-27.65, -12.93) * mm});
            skLineSegment(sketch, "E4122", {"start": v(-27.65, -12.93) * mm, "end": v(-27.6, -12.94) * mm});
            skLineSegment(sketch, "E4123", {"start": v(-27.6, -12.94) * mm, "end": v(-27.56, -12.96) * mm});
            skLineSegment(sketch, "E4124", {"start": v(-27.56, -12.96) * mm, "end": v(-27.5, -13) * mm});
            skLineSegment(sketch, "E4125", {"start": v(-27.5, -13) * mm, "end": v(-27.47, -13.04) * mm});
            skLineSegment(sketch, "E4126", {"start": v(-27.47, -13.04) * mm, "end": v(-27.44, -13.09) * mm});
            skLineSegment(sketch, "E4127", {"start": v(-27.44, -13.09) * mm, "end": v(-27.42, -13.14) * mm});
            skLineSegment(sketch, "E4128", {"start": v(-27.42, -13.14) * mm, "end": v(-27.41, -13.2) * mm});
            skLineSegment(sketch, "E4129", {"start": v(-27.41, -13.2) * mm, "end": v(-27.41, -13.26) * mm});
            skLineSegment(sketch, "E4130", {"start": v(-27.41, -13.26) * mm, "end": v(-27.43, -13.31) * mm});
            skLineSegment(sketch, "E4131", {"start": v(-27.43, -13.31) * mm, "end": v(-27.46, -13.35) * mm});
            skLineSegment(sketch, "E4132", {"start": v(-27.46, -13.35) * mm, "end": v(-27.48, -13.39) * mm});
            skLineSegment(sketch, "E4133", {"start": v(-27.48, -13.39) * mm, "end": v(-27.52, -13.42) * mm});
            skLineSegment(sketch, "E4134", {"start": v(-27.52, -13.42) * mm, "end": v(-27.55, -13.44) * mm});
            skLineSegment(sketch, "E4135", {"start": v(-27.55, -13.44) * mm, "end": v(-27.58, -13.48) * mm});
            skLineSegment(sketch, "E4136", {"start": v(-27.58, -13.48) * mm, "end": v(-27.57, -13.53) * mm});
            skLineSegment(sketch, "E4137", {"start": v(-27.57, -13.53) * mm, "end": v(-27.52, -13.64) * mm});
            skLineSegment(sketch, "E4138", {"start": v(-27.52, -13.64) * mm, "end": v(-27.48, -13.67) * mm});
            skLineSegment(sketch, "E4139", {"start": v(-27.48, -13.67) * mm, "end": v(-27.44, -13.67) * mm});
            skLineSegment(sketch, "E4140", {"start": v(-27.44, -13.67) * mm, "end": v(-27.4, -13.66) * mm});
            skLineSegment(sketch, "E4141", {"start": v(-27.4, -13.66) * mm, "end": v(-27.35, -13.66) * mm});
            skLineSegment(sketch, "E4142", {"start": v(-27.35, -13.66) * mm, "end": v(-27.3, -13.65) * mm});
            skLineSegment(sketch, "E4143", {"start": v(-27.3, -13.65) * mm, "end": v(-27.26, -13.66) * mm});
            skLineSegment(sketch, "E4144", {"start": v(-27.26, -13.66) * mm, "end": v(-27.2, -13.68) * mm});
            skLineSegment(sketch, "E4145", {"start": v(-27.2, -13.68) * mm, "end": v(-27.16, -13.71) * mm});
            skLineSegment(sketch, "E4146", {"start": v(-27.16, -13.71) * mm, "end": v(-27.12, -13.75) * mm});
            skLineSegment(sketch, "E4147", {"start": v(-27.12, -13.75) * mm, "end": v(-27.09, -13.8) * mm});
            skLineSegment(sketch, "E4148", {"start": v(-27.09, -13.8) * mm, "end": v(-27.07, -13.86) * mm});
            skLineSegment(sketch, "E4149", {"start": v(-27.07, -13.86) * mm, "end": v(-27.06, -13.91) * mm});
            skLineSegment(sketch, "E4150", {"start": v(-27.06, -13.91) * mm, "end": v(-27.06, -13.97) * mm});
            skLineSegment(sketch, "E4151", {"start": v(-27.06, -13.97) * mm, "end": v(-27.07, -14.03) * mm});
            skLineSegment(sketch, "E4152", {"start": v(-27.07, -14.03) * mm, "end": v(-27.1, -14.07) * mm});
            skLineSegment(sketch, "E4153", {"start": v(-27.1, -14.07) * mm, "end": v(-27.12, -14.1) * mm});
            skLineSegment(sketch, "E4154", {"start": v(-27.12, -14.1) * mm, "end": v(-27.16, -14.13) * mm});
            skLineSegment(sketch, "E4155", {"start": v(-27.16, -14.13) * mm, "end": v(-27.2, -14.16) * mm});
            skLineSegment(sketch, "E4156", {"start": v(-27.2, -14.16) * mm, "end": v(-27.21, -14.2) * mm});
            skLineSegment(sketch, "E4157", {"start": v(-27.21, -14.2) * mm, "end": v(-27.2, -14.25) * mm});
            skLineSegment(sketch, "E4158", {"start": v(-27.2, -14.25) * mm, "end": v(-27.15, -14.35) * mm});
            skLineSegment(sketch, "E4159", {"start": v(-27.15, -14.35) * mm, "end": v(-27.12, -14.39) * mm});
            skLineSegment(sketch, "E4160", {"start": v(-27.12, -14.39) * mm, "end": v(-27.07, -14.39) * mm});
            skLineSegment(sketch, "E4161", {"start": v(-27.07, -14.39) * mm, "end": v(-27.03, -14.37) * mm});
            skLineSegment(sketch, "E4162", {"start": v(-27.03, -14.37) * mm, "end": v(-26.99, -14.37) * mm});
            skLineSegment(sketch, "E4163", {"start": v(-26.99, -14.37) * mm, "end": v(-26.94, -14.36) * mm});
            skLineSegment(sketch, "E4164", {"start": v(-26.94, -14.36) * mm, "end": v(-26.9, -14.37) * mm});
            skLineSegment(sketch, "E4165", {"start": v(-26.9, -14.37) * mm, "end": v(-26.84, -14.39) * mm});
            skLineSegment(sketch, "E4166", {"start": v(-26.84, -14.39) * mm, "end": v(-26.8, -14.42) * mm});
            skLineSegment(sketch, "E4167", {"start": v(-26.8, -14.42) * mm, "end": v(-26.75, -14.46) * mm});
            skLineSegment(sketch, "E4168", {"start": v(-26.75, -14.46) * mm, "end": v(-26.72, -14.5) * mm});
            skLineSegment(sketch, "E4169", {"start": v(-26.72, -14.5) * mm, "end": v(-26.7, -14.56) * mm});
            skLineSegment(sketch, "E4170", {"start": v(-26.7, -14.56) * mm, "end": v(-26.68, -14.62) * mm});
            skLineSegment(sketch, "E4171", {"start": v(-26.68, -14.62) * mm, "end": v(-26.68, -14.67) * mm});
            skLineSegment(sketch, "E4172", {"start": v(-26.68, -14.67) * mm, "end": v(-26.7, -14.73) * mm});
            skLineSegment(sketch, "E4173", {"start": v(-26.7, -14.73) * mm, "end": v(-26.72, -14.77) * mm});
            skLineSegment(sketch, "E4174", {"start": v(-26.72, -14.77) * mm, "end": v(-26.75, -14.8) * mm});
            skLineSegment(sketch, "E4175", {"start": v(-26.75, -14.8) * mm, "end": v(-26.78, -14.84) * mm});
            skLineSegment(sketch, "E4176", {"start": v(-26.78, -14.84) * mm, "end": v(-26.81, -14.87) * mm});
            skLineSegment(sketch, "E4177", {"start": v(-26.81, -14.87) * mm, "end": v(-26.83, -14.9) * mm});
            skLineSegment(sketch, "E4178", {"start": v(-26.83, -14.9) * mm, "end": v(-26.82, -14.95) * mm});
            skLineSegment(sketch, "E4179", {"start": v(-26.82, -14.95) * mm, "end": v(-26.76, -15.06) * mm});
            skLineSegment(sketch, "E4180", {"start": v(-26.76, -15.06) * mm, "end": v(-26.73, -15.1) * mm});
            skLineSegment(sketch, "E4181", {"start": v(-26.73, -15.1) * mm, "end": v(-26.69, -15.1) * mm});
            skLineSegment(sketch, "E4182", {"start": v(-26.69, -15.1) * mm, "end": v(-26.64, -15.08) * mm});
            skLineSegment(sketch, "E4183", {"start": v(-26.64, -15.08) * mm, "end": v(-26.6, -15.07) * mm});
            skLineSegment(sketch, "E4184", {"start": v(-26.6, -15.07) * mm, "end": v(-26.55, -15.06) * mm});
            skLineSegment(sketch, "E4185", {"start": v(-26.55, -15.06) * mm, "end": v(-26.5, -15.07) * mm});
            skLineSegment(sketch, "E4186", {"start": v(-26.5, -15.07) * mm, "end": v(-26.45, -15.08) * mm});
            skLineSegment(sketch, "E4187", {"start": v(-26.45, -15.08) * mm, "end": v(-26.4, -15.11) * mm});
            skLineSegment(sketch, "E4188", {"start": v(-26.4, -15.11) * mm, "end": v(-26.36, -15.15) * mm});
            skLineSegment(sketch, "E4189", {"start": v(-26.36, -15.15) * mm, "end": v(-26.33, -15.2) * mm});
            skLineSegment(sketch, "E4190", {"start": v(-26.33, -15.2) * mm, "end": v(-26.3, -15.25) * mm});
            skLineSegment(sketch, "E4191", {"start": v(-26.3, -15.25) * mm, "end": v(-26.3, -15.31) * mm});
            skLineSegment(sketch, "E4192", {"start": v(-26.3, -15.31) * mm, "end": v(-26.3, -15.37) * mm});
            skLineSegment(sketch, "E4193", {"start": v(-26.3, -15.37) * mm, "end": v(-26.3, -15.42) * mm});
            skLineSegment(sketch, "E4194", {"start": v(-26.3, -15.42) * mm, "end": v(-26.32, -15.46) * mm});
            skLineSegment(sketch, "E4195", {"start": v(-26.32, -15.46) * mm, "end": v(-26.35, -15.5) * mm});
            skLineSegment(sketch, "E4196", {"start": v(-26.35, -15.5) * mm, "end": v(-26.38, -15.54) * mm});
            skLineSegment(sketch, "E4197", {"start": v(-26.38, -15.54) * mm, "end": v(-26.41, -15.56) * mm});
            skLineSegment(sketch, "E4198", {"start": v(-26.41, -15.56) * mm, "end": v(-26.43, -15.6) * mm});
            skLineSegment(sketch, "E4199", {"start": v(-26.43, -15.6) * mm, "end": v(-26.42, -15.65) * mm});
            skLineSegment(sketch, "E4200", {"start": v(-26.42, -15.65) * mm, "end": v(-26.36, -15.75) * mm});
            skLineSegment(sketch, "E4201", {"start": v(-26.36, -15.75) * mm, "end": v(-26.33, -15.78) * mm});
            skLineSegment(sketch, "E4202", {"start": v(-26.33, -15.78) * mm, "end": v(-26.28, -15.78) * mm});
            skLineSegment(sketch, "E4203", {"start": v(-26.28, -15.78) * mm, "end": v(-26.24, -15.77) * mm});
            skLineSegment(sketch, "E4204", {"start": v(-26.24, -15.77) * mm, "end": v(-26.2, -15.76) * mm});
            skLineSegment(sketch, "E4205", {"start": v(-26.2, -15.76) * mm, "end": v(-26.15, -15.75) * mm});
            skLineSegment(sketch, "E4206", {"start": v(-26.15, -15.75) * mm, "end": v(-26.1, -15.76) * mm});
            skLineSegment(sketch, "E4207", {"start": v(-26.1, -15.76) * mm, "end": v(-26.05, -15.77) * mm});
            skLineSegment(sketch, "E4208", {"start": v(-26.05, -15.77) * mm, "end": v(-26, -15.8) * mm});
            skLineSegment(sketch, "E4209", {"start": v(-26, -15.8) * mm, "end": v(-25.96, -15.84) * mm});
            skLineSegment(sketch, "E4210", {"start": v(-25.96, -15.84) * mm, "end": v(-25.92, -15.88) * mm});
            skLineSegment(sketch, "E4211", {"start": v(-25.92, -15.88) * mm, "end": v(-25.9, -15.94) * mm});
            skLineSegment(sketch, "E4212", {"start": v(-25.9, -15.94) * mm, "end": v(-25.88, -16) * mm});
            skLineSegment(sketch, "E4213", {"start": v(-25.88, -16) * mm, "end": v(-25.88, -16.05) * mm});
            skLineSegment(sketch, "E4214", {"start": v(-25.88, -16.05) * mm, "end": v(-25.89, -16.1) * mm});
            skLineSegment(sketch, "E4215", {"start": v(-25.89, -16.1) * mm, "end": v(-25.91, -16.15) * mm});
            skLineSegment(sketch, "E4216", {"start": v(-25.91, -16.15) * mm, "end": v(-25.93, -16.19) * mm});
            skLineSegment(sketch, "E4217", {"start": v(-25.93, -16.19) * mm, "end": v(-25.96, -16.22) * mm});
            skLineSegment(sketch, "E4218", {"start": v(-25.96, -16.22) * mm, "end": v(-26, -16.25) * mm});
            skLineSegment(sketch, "E4219", {"start": v(-26, -16.25) * mm, "end": v(-26.02, -16.3) * mm});
            skLineSegment(sketch, "E4220", {"start": v(-26.02, -16.3) * mm, "end": v(-26, -16.34) * mm});
            skLineSegment(sketch, "E4221", {"start": v(-26, -16.34) * mm, "end": v(-25.94, -16.44) * mm});
            skLineSegment(sketch, "E4222", {"start": v(-25.94, -16.44) * mm, "end": v(-25.9, -16.47) * mm});
            skLineSegment(sketch, "E4223", {"start": v(-25.9, -16.47) * mm, "end": v(-25.86, -16.47) * mm});
            skLineSegment(sketch, "E4224", {"start": v(-25.86, -16.47) * mm, "end": v(-25.82, -16.45) * mm});
            skLineSegment(sketch, "E4225", {"start": v(-25.82, -16.45) * mm, "end": v(-25.77, -16.44) * mm});
            skLineSegment(sketch, "E4226", {"start": v(-25.77, -16.44) * mm, "end": v(-25.73, -16.43) * mm});
            skLineSegment(sketch, "E4227", {"start": v(-25.73, -16.43) * mm, "end": v(-25.68, -16.43) * mm});
            skLineSegment(sketch, "E4228", {"start": v(-25.68, -16.43) * mm, "end": v(-25.63, -16.45) * mm});
            skLineSegment(sketch, "E4229", {"start": v(-25.63, -16.45) * mm, "end": v(-25.58, -16.47) * mm});
            skLineSegment(sketch, "E4230", {"start": v(-25.58, -16.47) * mm, "end": v(-25.53, -16.51) * mm});
            skLineSegment(sketch, "E4231", {"start": v(-25.53, -16.51) * mm, "end": v(-25.5, -16.56) * mm});
            skLineSegment(sketch, "E4232", {"start": v(-25.5, -16.56) * mm, "end": v(-25.47, -16.6) * mm});
            skLineSegment(sketch, "E4233", {"start": v(-25.47, -16.6) * mm, "end": v(-25.45, -16.67) * mm});
            skLineSegment(sketch, "E4234", {"start": v(-25.45, -16.67) * mm, "end": v(-25.45, -16.72) * mm});
            skLineSegment(sketch, "E4235", {"start": v(-25.45, -16.72) * mm, "end": v(-25.46, -16.78) * mm});
            skLineSegment(sketch, "E4236", {"start": v(-25.46, -16.78) * mm, "end": v(-25.48, -16.82) * mm});
            skLineSegment(sketch, "E4237", {"start": v(-25.48, -16.82) * mm, "end": v(-25.5, -16.86) * mm});
            skLineSegment(sketch, "E4238", {"start": v(-25.5, -16.86) * mm, "end": v(-25.53, -16.9) * mm});
            skLineSegment(sketch, "E4239", {"start": v(-25.53, -16.9) * mm, "end": v(-25.56, -16.93) * mm});
            skLineSegment(sketch, "E4240", {"start": v(-25.56, -16.93) * mm, "end": v(-25.58, -16.97) * mm});
            skLineSegment(sketch, "E4241", {"start": v(-25.58, -16.97) * mm, "end": v(-25.57, -17.01) * mm});
            skLineSegment(sketch, "E4242", {"start": v(-25.57, -17.01) * mm, "end": v(-25.5, -17.11) * mm});
            skLineSegment(sketch, "E4243", {"start": v(-25.5, -17.11) * mm, "end": v(-25.46, -17.14) * mm});
            skLineSegment(sketch, "E4244", {"start": v(-25.46, -17.14) * mm, "end": v(-25.42, -17.14) * mm});
            skLineSegment(sketch, "E4245", {"start": v(-25.42, -17.14) * mm, "end": v(-25.38, -17.12) * mm});
            skLineSegment(sketch, "E4246", {"start": v(-25.38, -17.12) * mm, "end": v(-25.34, -17.1) * mm});
            skLineSegment(sketch, "E4247", {"start": v(-25.34, -17.1) * mm, "end": v(-25.3, -17.1) * mm});
            skLineSegment(sketch, "E4248", {"start": v(-25.3, -17.1) * mm, "end": v(-25.25, -17.1) * mm});
            skLineSegment(sketch, "E4249", {"start": v(-25.25, -17.1) * mm, "end": v(-25.19, -17.11) * mm});
            skLineSegment(sketch, "E4250", {"start": v(-25.19, -17.11) * mm, "end": v(-25.14, -17.14) * mm});
            skLineSegment(sketch, "E4251", {"start": v(-25.14, -17.14) * mm, "end": v(-25.1, -17.17) * mm});
            skLineSegment(sketch, "E4252", {"start": v(-25.1, -17.17) * mm, "end": v(-25.05, -17.22) * mm});
            skLineSegment(sketch, "E4253", {"start": v(-25.05, -17.22) * mm, "end": v(-25.03, -17.27) * mm});
            skLineSegment(sketch, "E4254", {"start": v(-25.03, -17.27) * mm, "end": v(-25, -17.33) * mm});
            skLineSegment(sketch, "E4255", {"start": v(-25, -17.33) * mm, "end": v(-25, -17.38) * mm});
            skLineSegment(sketch, "E4256", {"start": v(-25, -17.38) * mm, "end": v(-25.01, -17.44) * mm});
            skLineSegment(sketch, "E4257", {"start": v(-25.01, -17.44) * mm, "end": v(-25.03, -17.48) * mm});
            skLineSegment(sketch, "E4258", {"start": v(-25.03, -17.48) * mm, "end": v(-25.05, -17.52) * mm});
            skLineSegment(sketch, "E4259", {"start": v(-25.05, -17.52) * mm, "end": v(-25.08, -17.56) * mm});
            skLineSegment(sketch, "E4260", {"start": v(-25.08, -17.56) * mm, "end": v(-25.1, -17.59) * mm});
            skLineSegment(sketch, "E4261", {"start": v(-25.1, -17.59) * mm, "end": v(-25.13, -17.63) * mm});
            skLineSegment(sketch, "E4262", {"start": v(-25.13, -17.63) * mm, "end": v(-25.11, -17.67) * mm});
            skLineSegment(sketch, "E4263", {"start": v(-25.11, -17.67) * mm, "end": v(-25.04, -17.77) * mm});
            skLineSegment(sketch, "E4264", {"start": v(-25.04, -17.77) * mm, "end": v(-25, -17.8) * mm});
            skLineSegment(sketch, "E4265", {"start": v(-25, -17.8) * mm, "end": v(-24.96, -17.8) * mm});
            skLineSegment(sketch, "E4266", {"start": v(-24.96, -17.8) * mm, "end": v(-24.92, -17.78) * mm});
            skLineSegment(sketch, "E4267", {"start": v(-24.92, -17.78) * mm, "end": v(-24.88, -17.77) * mm});
            skLineSegment(sketch, "E4268", {"start": v(-24.88, -17.77) * mm, "end": v(-24.83, -17.76) * mm});
            skLineSegment(sketch, "E4269", {"start": v(-24.83, -17.76) * mm, "end": v(-24.79, -17.76) * mm});
            skLineSegment(sketch, "E4270", {"start": v(-24.79, -17.76) * mm, "end": v(-24.73, -17.77) * mm});
            skLineSegment(sketch, "E4271", {"start": v(-24.73, -17.77) * mm, "end": v(-24.68, -17.8) * mm});
            skLineSegment(sketch, "E4272", {"start": v(-24.68, -17.8) * mm, "end": v(-24.63, -17.83) * mm});
            skLineSegment(sketch, "E4273", {"start": v(-24.63, -17.83) * mm, "end": v(-24.6, -17.87) * mm});
            skLineSegment(sketch, "E4274", {"start": v(-24.6, -17.87) * mm, "end": v(-24.56, -17.92) * mm});
            skLineSegment(sketch, "E4275", {"start": v(-24.56, -17.92) * mm, "end": v(-24.55, -17.97) * mm});
            skLineSegment(sketch, "E4276", {"start": v(-24.55, -17.97) * mm, "end": v(-24.54, -18.03) * mm});
            skLineSegment(sketch, "E4277", {"start": v(-24.54, -18.03) * mm, "end": v(-24.55, -18.09) * mm});
            skLineSegment(sketch, "E4278", {"start": v(-24.55, -18.09) * mm, "end": v(-24.56, -18.13) * mm});
            skLineSegment(sketch, "E4279", {"start": v(-24.56, -18.13) * mm, "end": v(-24.58, -18.17) * mm});
            skLineSegment(sketch, "E4280", {"start": v(-24.58, -18.17) * mm, "end": v(-24.61, -18.2) * mm});
            skLineSegment(sketch, "E4281", {"start": v(-24.61, -18.2) * mm, "end": v(-24.64, -18.24) * mm});
            skLineSegment(sketch, "E4282", {"start": v(-24.64, -18.24) * mm, "end": v(-24.66, -18.28) * mm});
            skLineSegment(sketch, "E4283", {"start": v(-24.66, -18.28) * mm, "end": v(-24.64, -18.33) * mm});
            skLineSegment(sketch, "E4284", {"start": v(-24.64, -18.33) * mm, "end": v(-24.57, -18.42) * mm});
            skLineSegment(sketch, "E4285", {"start": v(-24.57, -18.42) * mm, "end": v(-24.53, -18.45) * mm});
            skLineSegment(sketch, "E4286", {"start": v(-24.53, -18.45) * mm, "end": v(-24.49, -18.45) * mm});
            skLineSegment(sketch, "E4287", {"start": v(-24.49, -18.45) * mm, "end": v(-24.45, -18.43) * mm});
            skLineSegment(sketch, "E4288", {"start": v(-24.45, -18.43) * mm, "end": v(-24.4, -18.41) * mm});
            skLineSegment(sketch, "E4289", {"start": v(-24.4, -18.41) * mm, "end": v(-24.36, -18.4) * mm});
            skLineSegment(sketch, "E4290", {"start": v(-24.36, -18.4) * mm, "end": v(-24.32, -18.4) * mm});
            skLineSegment(sketch, "E4291", {"start": v(-24.32, -18.4) * mm, "end": v(-24.26, -18.4) * mm});
            skLineSegment(sketch, "E4292", {"start": v(-24.26, -18.4) * mm, "end": v(-24.2, -18.43) * mm});
            skLineSegment(sketch, "E4293", {"start": v(-24.2, -18.43) * mm, "end": v(-24.16, -18.46) * mm});
            skLineSegment(sketch, "E4294", {"start": v(-24.16, -18.46) * mm, "end": v(-24.12, -18.5) * mm});
            skLineSegment(sketch, "E4295", {"start": v(-24.12, -18.5) * mm, "end": v(-24.09, -18.56) * mm});
            skLineSegment(sketch, "E4296", {"start": v(-24.09, -18.56) * mm, "end": v(-24.07, -18.61) * mm});
            skLineSegment(sketch, "E4297", {"start": v(-24.07, -18.61) * mm, "end": v(-24.06, -18.67) * mm});
            skLineSegment(sketch, "E4298", {"start": v(-24.06, -18.67) * mm, "end": v(-24.06, -18.73) * mm});
            skLineSegment(sketch, "E4299", {"start": v(-24.06, -18.73) * mm, "end": v(-24.08, -18.77) * mm});
            skLineSegment(sketch, "E4300", {"start": v(-24.08, -18.77) * mm, "end": v(-24.1, -18.8) * mm});
            skLineSegment(sketch, "E4301", {"start": v(-24.1, -18.8) * mm, "end": v(-24.13, -18.85) * mm});
            skLineSegment(sketch, "E4302", {"start": v(-24.13, -18.85) * mm, "end": v(-24.15, -18.88) * mm});
            skLineSegment(sketch, "E4303", {"start": v(-24.15, -18.88) * mm, "end": v(-24.17, -18.92) * mm});
            skLineSegment(sketch, "E4304", {"start": v(-24.17, -18.92) * mm, "end": v(-24.15, -18.96) * mm});
            skLineSegment(sketch, "E4305", {"start": v(-24.15, -18.96) * mm, "end": v(-24.08, -19.06) * mm});
            skLineSegment(sketch, "E4306", {"start": v(-24.08, -19.06) * mm, "end": v(-24.04, -19.09) * mm});
            skLineSegment(sketch, "E4307", {"start": v(-24.04, -19.09) * mm, "end": v(-24, -19.08) * mm});
            skLineSegment(sketch, "E4308", {"start": v(-24, -19.08) * mm, "end": v(-23.96, -19.06) * mm});
            skLineSegment(sketch, "E4309", {"start": v(-23.96, -19.06) * mm, "end": v(-23.92, -19.04) * mm});
            skLineSegment(sketch, "E4310", {"start": v(-23.92, -19.04) * mm, "end": v(-23.87, -19.03) * mm});
            skLineSegment(sketch, "E4311", {"start": v(-23.87, -19.03) * mm, "end": v(-23.83, -19.03) * mm});
            skLineSegment(sketch, "E4312", {"start": v(-23.83, -19.03) * mm, "end": v(-23.77, -19.04) * mm});
            skLineSegment(sketch, "E4313", {"start": v(-23.77, -19.04) * mm, "end": v(-23.71, -19.06) * mm});
            skLineSegment(sketch, "E4314", {"start": v(-23.71, -19.06) * mm, "end": v(-23.67, -19.09) * mm});
            skLineSegment(sketch, "E4315", {"start": v(-23.67, -19.09) * mm, "end": v(-23.63, -19.13) * mm});
            skLineSegment(sketch, "E4316", {"start": v(-23.63, -19.13) * mm, "end": v(-23.6, -19.18) * mm});
            skLineSegment(sketch, "E4317", {"start": v(-23.6, -19.18) * mm, "end": v(-23.57, -19.23) * mm});
            skLineSegment(sketch, "E4318", {"start": v(-23.57, -19.23) * mm, "end": v(-23.56, -19.3) * mm});
            skLineSegment(sketch, "E4319", {"start": v(-23.56, -19.3) * mm, "end": v(-23.57, -19.35) * mm});
            skLineSegment(sketch, "E4320", {"start": v(-23.57, -19.35) * mm, "end": v(-23.58, -19.4) * mm});
            skLineSegment(sketch, "E4321", {"start": v(-23.58, -19.4) * mm, "end": v(-23.6, -19.43) * mm});
            skLineSegment(sketch, "E4322", {"start": v(-23.6, -19.43) * mm, "end": v(-23.62, -19.47) * mm});
            skLineSegment(sketch, "E4323", {"start": v(-23.62, -19.47) * mm, "end": v(-23.65, -19.5) * mm});
            skLineSegment(sketch, "E4324", {"start": v(-23.65, -19.5) * mm, "end": v(-23.67, -19.55) * mm});
            skLineSegment(sketch, "E4325", {"start": v(-23.67, -19.55) * mm, "end": v(-23.65, -19.6) * mm});
            skLineSegment(sketch, "E4326", {"start": v(-23.65, -19.6) * mm, "end": v(-23.57, -19.68) * mm});
            skLineSegment(sketch, "E4327", {"start": v(-23.57, -19.68) * mm, "end": v(-23.53, -19.7) * mm});
            skLineSegment(sketch, "E4328", {"start": v(-23.53, -19.7) * mm, "end": v(-23.49, -19.7) * mm});
            skLineSegment(sketch, "E4329", {"start": v(-23.49, -19.7) * mm, "end": v(-23.45, -19.68) * mm});
            skLineSegment(sketch, "E4330", {"start": v(-23.45, -19.68) * mm, "end": v(-23.4, -19.66) * mm});
            skLineSegment(sketch, "E4331", {"start": v(-23.4, -19.66) * mm, "end": v(-23.36, -19.65) * mm});
            skLineSegment(sketch, "E4332", {"start": v(-23.36, -19.65) * mm, "end": v(-23.32, -19.65) * mm});
            skLineSegment(sketch, "E4333", {"start": v(-23.32, -19.65) * mm, "end": v(-23.26, -19.65) * mm});
            skLineSegment(sketch, "E4334", {"start": v(-23.26, -19.65) * mm, "end": v(-23.2, -19.67) * mm});
            skLineSegment(sketch, "E4335", {"start": v(-23.2, -19.67) * mm, "end": v(-23.16, -19.7) * mm});
            skLineSegment(sketch, "E4336", {"start": v(-23.16, -19.7) * mm, "end": v(-23.12, -19.74) * mm});
            skLineSegment(sketch, "E4337", {"start": v(-23.12, -19.74) * mm, "end": v(-23.08, -19.8) * mm});
            skLineSegment(sketch, "E4338", {"start": v(-23.08, -19.8) * mm, "end": v(-23.06, -19.84) * mm});
            skLineSegment(sketch, "E4339", {"start": v(-23.06, -19.84) * mm, "end": v(-23.05, -19.9) * mm});
            skLineSegment(sketch, "E4340", {"start": v(-23.05, -19.9) * mm, "end": v(-23.05, -19.96) * mm});
            skLineSegment(sketch, "E4341", {"start": v(-23.05, -19.96) * mm, "end": v(-23.07, -20) * mm});
            skLineSegment(sketch, "E4342", {"start": v(-23.07, -20) * mm, "end": v(-23.08, -20.04) * mm});
            skLineSegment(sketch, "E4343", {"start": v(-23.08, -20.04) * mm, "end": v(-23.1, -20.08) * mm});
            skLineSegment(sketch, "E4344", {"start": v(-23.1, -20.08) * mm, "end": v(-23.13, -20.12) * mm});
            skLineSegment(sketch, "E4345", {"start": v(-23.13, -20.12) * mm, "end": v(-23.15, -20.16) * mm});
            skLineSegment(sketch, "E4346", {"start": v(-23.15, -20.16) * mm, "end": v(-23.13, -20.2) * mm});
            skLineSegment(sketch, "E4347", {"start": v(-23.13, -20.2) * mm, "end": v(-23.05, -20.3) * mm});
            skLineSegment(sketch, "E4348", {"start": v(-23.05, -20.3) * mm, "end": v(-23, -20.32) * mm});
            skLineSegment(sketch, "E4349", {"start": v(-23, -20.32) * mm, "end": v(-22.96, -20.3) * mm});
            skLineSegment(sketch, "E4350", {"start": v(-22.96, -20.3) * mm, "end": v(-22.93, -20.29) * mm});
            skLineSegment(sketch, "E4351", {"start": v(-22.93, -20.29) * mm, "end": v(-22.89, -20.27) * mm});
            skLineSegment(sketch, "E4352", {"start": v(-22.89, -20.27) * mm, "end": v(-22.84, -20.26) * mm});
            skLineSegment(sketch, "E4353", {"start": v(-22.84, -20.26) * mm, "end": v(-22.8, -20.25) * mm});
            skLineSegment(sketch, "E4354", {"start": v(-22.8, -20.25) * mm, "end": v(-22.74, -20.25) * mm});
            skLineSegment(sketch, "E4355", {"start": v(-22.74, -20.25) * mm, "end": v(-22.68, -20.27) * mm});
            skLineSegment(sketch, "E4356", {"start": v(-22.68, -20.27) * mm, "end": v(-22.64, -20.3) * mm});
            skLineSegment(sketch, "E4357", {"start": v(-22.64, -20.3) * mm, "end": v(-22.6, -20.34) * mm});
            skLineSegment(sketch, "E4358", {"start": v(-22.6, -20.34) * mm, "end": v(-22.56, -20.39) * mm});
            skLineSegment(sketch, "E4359", {"start": v(-22.56, -20.39) * mm, "end": v(-22.53, -20.44) * mm});
            skLineSegment(sketch, "E4360", {"start": v(-22.53, -20.44) * mm, "end": v(-22.52, -20.5) * mm});
            skLineSegment(sketch, "E4361", {"start": v(-22.52, -20.5) * mm, "end": v(-22.52, -20.56) * mm});
            skLineSegment(sketch, "E4362", {"start": v(-22.52, -20.56) * mm, "end": v(-22.53, -20.6) * mm});
            skLineSegment(sketch, "E4363", {"start": v(-22.53, -20.6) * mm, "end": v(-22.55, -20.64) * mm});
            skLineSegment(sketch, "E4364", {"start": v(-22.55, -20.64) * mm, "end": v(-22.57, -20.68) * mm});
            skLineSegment(sketch, "E4365", {"start": v(-22.57, -20.68) * mm, "end": v(-22.6, -20.72) * mm});
            skLineSegment(sketch, "E4366", {"start": v(-22.6, -20.72) * mm, "end": v(-22.61, -20.76) * mm});
            skLineSegment(sketch, "E4367", {"start": v(-22.61, -20.76) * mm, "end": v(-22.6, -20.8) * mm});
            skLineSegment(sketch, "E4368", {"start": v(-22.6, -20.8) * mm, "end": v(-22.51, -20.9) * mm});
            skLineSegment(sketch, "E4369", {"start": v(-22.51, -20.9) * mm, "end": v(-22.47, -20.91) * mm});
            skLineSegment(sketch, "E4370", {"start": v(-22.47, -20.91) * mm, "end": v(-22.43, -20.9) * mm});
            skLineSegment(sketch, "E4371", {"start": v(-22.43, -20.9) * mm, "end": v(-22.39, -20.88) * mm});
            skLineSegment(sketch, "E4372", {"start": v(-22.39, -20.88) * mm, "end": v(-22.35, -20.86) * mm});
            skLineSegment(sketch, "E4373", {"start": v(-22.35, -20.86) * mm, "end": v(-22.3, -20.85) * mm});
            skLineSegment(sketch, "E4374", {"start": v(-22.3, -20.85) * mm, "end": v(-22.26, -20.84) * mm});
            skLineSegment(sketch, "E4375", {"start": v(-22.26, -20.84) * mm, "end": v(-22.2, -20.84) * mm});
            skLineSegment(sketch, "E4376", {"start": v(-22.2, -20.84) * mm, "end": v(-22.15, -20.86) * mm});
            skLineSegment(sketch, "E4377", {"start": v(-22.15, -20.86) * mm, "end": v(-22.1, -20.89) * mm});
            skLineSegment(sketch, "E4378", {"start": v(-22.1, -20.89) * mm, "end": v(-22.05, -20.93) * mm});
            skLineSegment(sketch, "E4379", {"start": v(-22.05, -20.93) * mm, "end": v(-22.02, -20.97) * mm});
            skLineSegment(sketch, "E4380", {"start": v(-22.02, -20.97) * mm, "end": v(-22, -21.02) * mm});
            skLineSegment(sketch, "E4381", {"start": v(-22, -21.02) * mm, "end": v(-21.98, -21.08) * mm});
            skLineSegment(sketch, "E4382", {"start": v(-21.98, -21.08) * mm, "end": v(-21.98, -21.14) * mm});
            skLineSegment(sketch, "E4383", {"start": v(-21.98, -21.14) * mm, "end": v(-21.99, -21.18) * mm});
            skLineSegment(sketch, "E4384", {"start": v(-21.99, -21.18) * mm, "end": v(-22, -21.22) * mm});
            skLineSegment(sketch, "E4385", {"start": v(-22, -21.22) * mm, "end": v(-22.02, -21.26) * mm});
            skLineSegment(sketch, "E4386", {"start": v(-22.02, -21.26) * mm, "end": v(-22.05, -21.3) * mm});
            skLineSegment(sketch, "E4387", {"start": v(-22.05, -21.3) * mm, "end": v(-22.06, -21.34) * mm});
            skLineSegment(sketch, "E4388", {"start": v(-22.06, -21.34) * mm, "end": v(-22.04, -21.39) * mm});
            skLineSegment(sketch, "E4389", {"start": v(-22.04, -21.39) * mm, "end": v(-21.96, -21.47) * mm});
            skLineSegment(sketch, "E4390", {"start": v(-21.96, -21.47) * mm, "end": v(-21.91, -21.5) * mm});
            skLineSegment(sketch, "E4391", {"start": v(-21.91, -21.5) * mm, "end": v(-21.87, -21.48) * mm});
            skLineSegment(sketch, "E4392", {"start": v(-21.87, -21.48) * mm, "end": v(-21.83, -21.46) * mm});
            skLineSegment(sketch, "E4393", {"start": v(-21.83, -21.46) * mm, "end": v(-21.8, -21.44) * mm});
            skLineSegment(sketch, "E4394", {"start": v(-21.8, -21.44) * mm, "end": v(-21.75, -21.42) * mm});
            skLineSegment(sketch, "E4395", {"start": v(-21.75, -21.42) * mm, "end": v(-21.7, -21.41) * mm});
            skLineSegment(sketch, "E4396", {"start": v(-21.7, -21.41) * mm, "end": v(-21.65, -21.42) * mm});
            skLineSegment(sketch, "E4397", {"start": v(-21.65, -21.42) * mm, "end": v(-21.6, -21.43) * mm});
            skLineSegment(sketch, "E4398", {"start": v(-21.6, -21.43) * mm, "end": v(-21.54, -21.46) * mm});
            skLineSegment(sketch, "E4399", {"start": v(-21.54, -21.46) * mm, "end": v(-21.5, -21.5) * mm});
            skLineSegment(sketch, "E4400", {"start": v(-21.5, -21.5) * mm, "end": v(-21.46, -21.54) * mm});
            skLineSegment(sketch, "E4401", {"start": v(-21.46, -21.54) * mm, "end": v(-21.43, -21.6) * mm});
            skLineSegment(sketch, "E4402", {"start": v(-21.43, -21.6) * mm, "end": v(-21.42, -21.65) * mm});
            skLineSegment(sketch, "E4403", {"start": v(-21.42, -21.65) * mm, "end": v(-21.41, -21.7) * mm});
            skLineSegment(sketch, "E4404", {"start": v(-21.41, -21.7) * mm, "end": v(-21.42, -21.75) * mm});
            skLineSegment(sketch, "E4405", {"start": v(-21.42, -21.75) * mm, "end": v(-21.44, -21.8) * mm});
            skLineSegment(sketch, "E4406", {"start": v(-21.44, -21.8) * mm, "end": v(-21.46, -21.83) * mm});
            skLineSegment(sketch, "E4407", {"start": v(-21.46, -21.83) * mm, "end": v(-21.48, -21.87) * mm});
            skLineSegment(sketch, "E4408", {"start": v(-21.48, -21.87) * mm, "end": v(-21.5, -21.91) * mm});
            skLineSegment(sketch, "E4409", {"start": v(-21.5, -21.91) * mm, "end": v(-21.47, -21.96) * mm});
            skLineSegment(sketch, "E4410", {"start": v(-21.47, -21.96) * mm, "end": v(-21.39, -22.04) * mm});
            skLineSegment(sketch, "E4411", {"start": v(-21.39, -22.04) * mm, "end": v(-21.34, -22.06) * mm});
            skLineSegment(sketch, "E4412", {"start": v(-21.34, -22.06) * mm, "end": v(-21.3, -22.05) * mm});
            skLineSegment(sketch, "E4413", {"start": v(-21.3, -22.05) * mm, "end": v(-21.26, -22.02) * mm});
            skLineSegment(sketch, "E4414", {"start": v(-21.26, -22.02) * mm, "end": v(-21.22, -22) * mm});
            skLineSegment(sketch, "E4415", {"start": v(-21.22, -22) * mm, "end": v(-21.18, -21.99) * mm});
            skLineSegment(sketch, "E4416", {"start": v(-21.18, -21.99) * mm, "end": v(-21.14, -21.98) * mm});
            skLineSegment(sketch, "E4417", {"start": v(-21.14, -21.98) * mm, "end": v(-21.08, -21.98) * mm});
            skLineSegment(sketch, "E4418", {"start": v(-21.08, -21.98) * mm, "end": v(-21.02, -22) * mm});
            skLineSegment(sketch, "E4419", {"start": v(-21.02, -22) * mm, "end": v(-20.97, -22.02) * mm});
            skLineSegment(sketch, "E4420", {"start": v(-20.97, -22.02) * mm, "end": v(-20.93, -22.05) * mm});
            skLineSegment(sketch, "E4421", {"start": v(-20.93, -22.05) * mm, "end": v(-20.89, -22.1) * mm});
            skLineSegment(sketch, "E4422", {"start": v(-20.89, -22.1) * mm, "end": v(-20.86, -22.15) * mm});
            skLineSegment(sketch, "E4423", {"start": v(-20.86, -22.15) * mm, "end": v(-20.84, -22.2) * mm});
            skLineSegment(sketch, "E4424", {"start": v(-20.84, -22.2) * mm, "end": v(-20.84, -22.26) * mm});
            skLineSegment(sketch, "E4425", {"start": v(-20.84, -22.26) * mm, "end": v(-20.85, -22.3) * mm});
            skLineSegment(sketch, "E4426", {"start": v(-20.85, -22.3) * mm, "end": v(-20.86, -22.35) * mm});
            skLineSegment(sketch, "E4427", {"start": v(-20.86, -22.35) * mm, "end": v(-20.88, -22.39) * mm});
            skLineSegment(sketch, "E4428", {"start": v(-20.88, -22.39) * mm, "end": v(-20.9, -22.43) * mm});
            skLineSegment(sketch, "E4429", {"start": v(-20.9, -22.43) * mm, "end": v(-20.91, -22.47) * mm});
            skLineSegment(sketch, "E4430", {"start": v(-20.91, -22.47) * mm, "end": v(-20.9, -22.51) * mm});
            skLineSegment(sketch, "E4431", {"start": v(-20.9, -22.51) * mm, "end": v(-20.8, -22.6) * mm});
            skLineSegment(sketch, "E4432", {"start": v(-20.8, -22.6) * mm, "end": v(-20.76, -22.61) * mm});
            skLineSegment(sketch, "E4433", {"start": v(-20.76, -22.61) * mm, "end": v(-20.72, -22.6) * mm});
            skLineSegment(sketch, "E4434", {"start": v(-20.72, -22.6) * mm, "end": v(-20.68, -22.57) * mm});
            skLineSegment(sketch, "E4435", {"start": v(-20.68, -22.57) * mm, "end": v(-20.64, -22.55) * mm});
            skLineSegment(sketch, "E4436", {"start": v(-20.64, -22.55) * mm, "end": v(-20.6, -22.53) * mm});
            skLineSegment(sketch, "E4437", {"start": v(-20.6, -22.53) * mm, "end": v(-20.56, -22.52) * mm});
            skLineSegment(sketch, "E4438", {"start": v(-20.56, -22.52) * mm, "end": v(-20.5, -22.52) * mm});
            skLineSegment(sketch, "E4439", {"start": v(-20.5, -22.52) * mm, "end": v(-20.44, -22.53) * mm});
            skLineSegment(sketch, "E4440", {"start": v(-20.44, -22.53) * mm, "end": v(-20.39, -22.56) * mm});
            skLineSegment(sketch, "E4441", {"start": v(-20.39, -22.56) * mm, "end": v(-20.34, -22.6) * mm});
            skLineSegment(sketch, "E4442", {"start": v(-20.34, -22.6) * mm, "end": v(-20.3, -22.64) * mm});
            skLineSegment(sketch, "E4443", {"start": v(-20.3, -22.64) * mm, "end": v(-20.27, -22.68) * mm});
            skLineSegment(sketch, "E4444", {"start": v(-20.27, -22.68) * mm, "end": v(-20.25, -22.74) * mm});
            skLineSegment(sketch, "E4445", {"start": v(-20.25, -22.74) * mm, "end": v(-20.25, -22.8) * mm});
            skLineSegment(sketch, "E4446", {"start": v(-20.25, -22.8) * mm, "end": v(-20.26, -22.84) * mm});
            skLineSegment(sketch, "E4447", {"start": v(-20.26, -22.84) * mm, "end": v(-20.27, -22.89) * mm});
            skLineSegment(sketch, "E4448", {"start": v(-20.27, -22.89) * mm, "end": v(-20.29, -22.93) * mm});
            skLineSegment(sketch, "E4449", {"start": v(-20.29, -22.93) * mm, "end": v(-20.3, -22.96) * mm});
            skLineSegment(sketch, "E4450", {"start": v(-20.3, -22.96) * mm, "end": v(-20.32, -23) * mm});
            skLineSegment(sketch, "E4451", {"start": v(-20.32, -23) * mm, "end": v(-20.3, -23.05) * mm});
            skLineSegment(sketch, "E4452", {"start": v(-20.3, -23.05) * mm, "end": v(-20.2, -23.13) * mm});
            skLineSegment(sketch, "E4453", {"start": v(-20.2, -23.13) * mm, "end": v(-20.16, -23.15) * mm});
            skLineSegment(sketch, "E4454", {"start": v(-20.16, -23.15) * mm, "end": v(-20.12, -23.13) * mm});
            skLineSegment(sketch, "E4455", {"start": v(-20.12, -23.13) * mm, "end": v(-20.08, -23.1) * mm});
            skLineSegment(sketch, "E4456", {"start": v(-20.08, -23.1) * mm, "end": v(-20.04, -23.08) * mm});
            skLineSegment(sketch, "E4457", {"start": v(-20.04, -23.08) * mm, "end": v(-20, -23.07) * mm});
            skLineSegment(sketch, "E4458", {"start": v(-20, -23.07) * mm, "end": v(-19.96, -23.05) * mm});
            skLineSegment(sketch, "E4459", {"start": v(-19.96, -23.05) * mm, "end": v(-19.9, -23.05) * mm});
            skLineSegment(sketch, "E4460", {"start": v(-19.9, -23.05) * mm, "end": v(-19.84, -23.06) * mm});
            skLineSegment(sketch, "E4461", {"start": v(-19.84, -23.06) * mm, "end": v(-19.8, -23.08) * mm});
            skLineSegment(sketch, "E4462", {"start": v(-19.8, -23.08) * mm, "end": v(-19.74, -23.12) * mm});
            skLineSegment(sketch, "E4463", {"start": v(-19.74, -23.12) * mm, "end": v(-19.7, -23.16) * mm});
            skLineSegment(sketch, "E4464", {"start": v(-19.7, -23.16) * mm, "end": v(-19.67, -23.2) * mm});
            skLineSegment(sketch, "E4465", {"start": v(-19.67, -23.2) * mm, "end": v(-19.65, -23.26) * mm});
            skLineSegment(sketch, "E4466", {"start": v(-19.65, -23.26) * mm, "end": v(-19.65, -23.32) * mm});
            skLineSegment(sketch, "E4467", {"start": v(-19.65, -23.32) * mm, "end": v(-19.65, -23.36) * mm});
            skLineSegment(sketch, "E4468", {"start": v(-19.65, -23.36) * mm, "end": v(-19.66, -23.4) * mm});
            skLineSegment(sketch, "E4469", {"start": v(-19.66, -23.4) * mm, "end": v(-19.68, -23.45) * mm});
            skLineSegment(sketch, "E4470", {"start": v(-19.68, -23.45) * mm, "end": v(-19.7, -23.49) * mm});
            skLineSegment(sketch, "E4471", {"start": v(-19.7, -23.49) * mm, "end": v(-19.7, -23.53) * mm});
            skLineSegment(sketch, "E4472", {"start": v(-19.7, -23.53) * mm, "end": v(-19.68, -23.57) * mm});
            skLineSegment(sketch, "E4473", {"start": v(-19.68, -23.57) * mm, "end": v(-19.6, -23.65) * mm});
            skLineSegment(sketch, "E4474", {"start": v(-19.6, -23.65) * mm, "end": v(-19.55, -23.67) * mm});
            skLineSegment(sketch, "E4475", {"start": v(-19.55, -23.67) * mm, "end": v(-19.5, -23.65) * mm});
            skLineSegment(sketch, "E4476", {"start": v(-19.5, -23.65) * mm, "end": v(-19.47, -23.62) * mm});
            skLineSegment(sketch, "E4477", {"start": v(-19.47, -23.62) * mm, "end": v(-19.43, -23.6) * mm});
            skLineSegment(sketch, "E4478", {"start": v(-19.43, -23.6) * mm, "end": v(-19.4, -23.58) * mm});
            skLineSegment(sketch, "E4479", {"start": v(-19.4, -23.58) * mm, "end": v(-19.35, -23.57) * mm});
            skLineSegment(sketch, "E4480", {"start": v(-19.35, -23.57) * mm, "end": v(-19.3, -23.56) * mm});
            skLineSegment(sketch, "E4481", {"start": v(-19.3, -23.56) * mm, "end": v(-19.23, -23.57) * mm});
            skLineSegment(sketch, "E4482", {"start": v(-19.23, -23.57) * mm, "end": v(-19.18, -23.6) * mm});
            skLineSegment(sketch, "E4483", {"start": v(-19.18, -23.6) * mm, "end": v(-19.13, -23.63) * mm});
            skLineSegment(sketch, "E4484", {"start": v(-19.13, -23.63) * mm, "end": v(-19.09, -23.67) * mm});
            skLineSegment(sketch, "E4485", {"start": v(-19.09, -23.67) * mm, "end": v(-19.06, -23.71) * mm});
            skLineSegment(sketch, "E4486", {"start": v(-19.06, -23.71) * mm, "end": v(-19.04, -23.77) * mm});
            skLineSegment(sketch, "E4487", {"start": v(-19.04, -23.77) * mm, "end": v(-19.03, -23.83) * mm});
            skLineSegment(sketch, "E4488", {"start": v(-19.03, -23.83) * mm, "end": v(-19.03, -23.87) * mm});
            skLineSegment(sketch, "E4489", {"start": v(-19.03, -23.87) * mm, "end": v(-19.04, -23.92) * mm});
            skLineSegment(sketch, "E4490", {"start": v(-19.04, -23.92) * mm, "end": v(-19.06, -23.96) * mm});
            skLineSegment(sketch, "E4491", {"start": v(-19.06, -23.96) * mm, "end": v(-19.08, -24) * mm});
            skLineSegment(sketch, "E4492", {"start": v(-19.08, -24) * mm, "end": v(-19.09, -24.04) * mm});
            skLineSegment(sketch, "E4493", {"start": v(-19.09, -24.04) * mm, "end": v(-19.06, -24.08) * mm});
            skLineSegment(sketch, "E4494", {"start": v(-19.06, -24.08) * mm, "end": v(-18.96, -24.15) * mm});
            skLineSegment(sketch, "E4495", {"start": v(-18.96, -24.15) * mm, "end": v(-18.92, -24.17) * mm});
            skLineSegment(sketch, "E4496", {"start": v(-18.92, -24.17) * mm, "end": v(-18.88, -24.15) * mm});
            skLineSegment(sketch, "E4497", {"start": v(-18.88, -24.15) * mm, "end": v(-18.85, -24.13) * mm});
            skLineSegment(sketch, "E4498", {"start": v(-18.85, -24.13) * mm, "end": v(-18.8, -24.1) * mm});
            skLineSegment(sketch, "E4499", {"start": v(-18.8, -24.1) * mm, "end": v(-18.77, -24.08) * mm});
            skLineSegment(sketch, "E4500", {"start": v(-18.77, -24.08) * mm, "end": v(-18.73, -24.06) * mm});
            skLineSegment(sketch, "E4501", {"start": v(-18.73, -24.06) * mm, "end": v(-18.67, -24.06) * mm});
            skLineSegment(sketch, "E4502", {"start": v(-18.67, -24.06) * mm, "end": v(-18.61, -24.07) * mm});
            skLineSegment(sketch, "E4503", {"start": v(-18.61, -24.07) * mm, "end": v(-18.56, -24.09) * mm});
            skLineSegment(sketch, "E4504", {"start": v(-18.56, -24.09) * mm, "end": v(-18.5, -24.12) * mm});
            skLineSegment(sketch, "E4505", {"start": v(-18.5, -24.12) * mm, "end": v(-18.46, -24.16) * mm});
            skLineSegment(sketch, "E4506", {"start": v(-18.46, -24.16) * mm, "end": v(-18.43, -24.2) * mm});
            skLineSegment(sketch, "E4507", {"start": v(-18.43, -24.2) * mm, "end": v(-18.4, -24.26) * mm});
            skLineSegment(sketch, "E4508", {"start": v(-18.4, -24.26) * mm, "end": v(-18.4, -24.32) * mm});
            skLineSegment(sketch, "E4509", {"start": v(-18.4, -24.32) * mm, "end": v(-18.4, -24.36) * mm});
            skLineSegment(sketch, "E4510", {"start": v(-18.4, -24.36) * mm, "end": v(-18.41, -24.4) * mm});
            skLineSegment(sketch, "E4511", {"start": v(-18.41, -24.4) * mm, "end": v(-18.43, -24.45) * mm});
            skLineSegment(sketch, "E4512", {"start": v(-18.43, -24.45) * mm, "end": v(-18.45, -24.49) * mm});
            skLineSegment(sketch, "E4513", {"start": v(-18.45, -24.49) * mm, "end": v(-18.45, -24.53) * mm});
            skLineSegment(sketch, "E4514", {"start": v(-18.45, -24.53) * mm, "end": v(-18.42, -24.57) * mm});
            skLineSegment(sketch, "E4515", {"start": v(-18.42, -24.57) * mm, "end": v(-18.33, -24.64) * mm});
            skLineSegment(sketch, "E4516", {"start": v(-18.33, -24.64) * mm, "end": v(-18.28, -24.66) * mm});
            skLineSegment(sketch, "E4517", {"start": v(-18.28, -24.66) * mm, "end": v(-18.24, -24.64) * mm});
            skLineSegment(sketch, "E4518", {"start": v(-18.24, -24.64) * mm, "end": v(-18.2, -24.61) * mm});
            skLineSegment(sketch, "E4519", {"start": v(-18.2, -24.61) * mm, "end": v(-18.17, -24.58) * mm});
            skLineSegment(sketch, "E4520", {"start": v(-18.17, -24.58) * mm, "end": v(-18.13, -24.56) * mm});
            skLineSegment(sketch, "E4521", {"start": v(-18.13, -24.56) * mm, "end": v(-18.09, -24.55) * mm});
            skLineSegment(sketch, "E4522", {"start": v(-18.09, -24.55) * mm, "end": v(-18.03, -24.54) * mm});
            skLineSegment(sketch, "E4523", {"start": v(-18.03, -24.54) * mm, "end": v(-17.97, -24.55) * mm});
            skLineSegment(sketch, "E4524", {"start": v(-17.97, -24.55) * mm, "end": v(-17.92, -24.56) * mm});
            skLineSegment(sketch, "E4525", {"start": v(-17.92, -24.56) * mm, "end": v(-17.87, -24.6) * mm});
            skLineSegment(sketch, "E4526", {"start": v(-17.87, -24.6) * mm, "end": v(-17.83, -24.63) * mm});
            skLineSegment(sketch, "E4527", {"start": v(-17.83, -24.63) * mm, "end": v(-17.8, -24.68) * mm});
            skLineSegment(sketch, "E4528", {"start": v(-17.8, -24.68) * mm, "end": v(-17.77, -24.73) * mm});
            skLineSegment(sketch, "E4529", {"start": v(-17.77, -24.73) * mm, "end": v(-17.76, -24.79) * mm});
            skLineSegment(sketch, "E4530", {"start": v(-17.76, -24.79) * mm, "end": v(-17.76, -24.83) * mm});
            skLineSegment(sketch, "E4531", {"start": v(-17.76, -24.83) * mm, "end": v(-17.77, -24.88) * mm});
            skLineSegment(sketch, "E4532", {"start": v(-17.77, -24.88) * mm, "end": v(-17.78, -24.92) * mm});
            skLineSegment(sketch, "E4533", {"start": v(-17.78, -24.92) * mm, "end": v(-17.8, -24.96) * mm});
            skLineSegment(sketch, "E4534", {"start": v(-17.8, -24.96) * mm, "end": v(-17.8, -25) * mm});
            skLineSegment(sketch, "E4535", {"start": v(-17.8, -25) * mm, "end": v(-17.77, -25.04) * mm});
            skLineSegment(sketch, "E4536", {"start": v(-17.77, -25.04) * mm, "end": v(-17.67, -25.11) * mm});
            skLineSegment(sketch, "E4537", {"start": v(-17.67, -25.11) * mm, "end": v(-17.63, -25.13) * mm});
            skLineSegment(sketch, "E4538", {"start": v(-17.63, -25.13) * mm, "end": v(-17.59, -25.1) * mm});
            skLineSegment(sketch, "E4539", {"start": v(-17.59, -25.1) * mm, "end": v(-17.56, -25.08) * mm});
            skLineSegment(sketch, "E4540", {"start": v(-17.56, -25.08) * mm, "end": v(-17.52, -25.05) * mm});
            skLineSegment(sketch, "E4541", {"start": v(-17.52, -25.05) * mm, "end": v(-17.48, -25.03) * mm});
            skLineSegment(sketch, "E4542", {"start": v(-17.48, -25.03) * mm, "end": v(-17.44, -25.01) * mm});
            skLineSegment(sketch, "E4543", {"start": v(-17.44, -25.01) * mm, "end": v(-17.38, -25) * mm});
            skLineSegment(sketch, "E4544", {"start": v(-17.38, -25) * mm, "end": v(-17.33, -25) * mm});
            skLineSegment(sketch, "E4545", {"start": v(-17.33, -25) * mm, "end": v(-17.27, -25.03) * mm});
            skLineSegment(sketch, "E4546", {"start": v(-17.27, -25.03) * mm, "end": v(-17.22, -25.05) * mm});
            skLineSegment(sketch, "E4547", {"start": v(-17.22, -25.05) * mm, "end": v(-17.17, -25.1) * mm});
            skLineSegment(sketch, "E4548", {"start": v(-17.17, -25.1) * mm, "end": v(-17.14, -25.14) * mm});
            skLineSegment(sketch, "E4549", {"start": v(-17.14, -25.14) * mm, "end": v(-17.11, -25.19) * mm});
            skLineSegment(sketch, "E4550", {"start": v(-17.11, -25.19) * mm, "end": v(-17.1, -25.25) * mm});
            skLineSegment(sketch, "E4551", {"start": v(-17.1, -25.25) * mm, "end": v(-17.1, -25.3) * mm});
            skLineSegment(sketch, "E4552", {"start": v(-17.1, -25.3) * mm, "end": v(-17.1, -25.34) * mm});
            skLineSegment(sketch, "E4553", {"start": v(-17.1, -25.34) * mm, "end": v(-17.12, -25.38) * mm});
            skLineSegment(sketch, "E4554", {"start": v(-17.12, -25.38) * mm, "end": v(-17.14, -25.42) * mm});
            skLineSegment(sketch, "E4555", {"start": v(-17.14, -25.42) * mm, "end": v(-17.14, -25.46) * mm});
            skLineSegment(sketch, "E4556", {"start": v(-17.14, -25.46) * mm, "end": v(-17.11, -25.5) * mm});
            skLineSegment(sketch, "E4557", {"start": v(-17.11, -25.5) * mm, "end": v(-17.01, -25.57) * mm});
            skLineSegment(sketch, "E4558", {"start": v(-17.01, -25.57) * mm, "end": v(-16.97, -25.58) * mm});
            skLineSegment(sketch, "E4559", {"start": v(-16.97, -25.58) * mm, "end": v(-16.93, -25.56) * mm});
            skLineSegment(sketch, "E4560", {"start": v(-16.93, -25.56) * mm, "end": v(-16.9, -25.53) * mm});
            skLineSegment(sketch, "E4561", {"start": v(-16.9, -25.53) * mm, "end": v(-16.86, -25.5) * mm});
            skLineSegment(sketch, "E4562", {"start": v(-16.86, -25.5) * mm, "end": v(-16.82, -25.48) * mm});
            skLineSegment(sketch, "E4563", {"start": v(-16.82, -25.48) * mm, "end": v(-16.78, -25.46) * mm});
            skLineSegment(sketch, "E4564", {"start": v(-16.78, -25.46) * mm, "end": v(-16.72, -25.45) * mm});
            skLineSegment(sketch, "E4565", {"start": v(-16.72, -25.45) * mm, "end": v(-16.67, -25.45) * mm});
            skLineSegment(sketch, "E4566", {"start": v(-16.67, -25.45) * mm, "end": v(-16.6, -25.47) * mm});
            skLineSegment(sketch, "E4567", {"start": v(-16.6, -25.47) * mm, "end": v(-16.56, -25.5) * mm});
            skLineSegment(sketch, "E4568", {"start": v(-16.56, -25.5) * mm, "end": v(-16.51, -25.53) * mm});
            skLineSegment(sketch, "E4569", {"start": v(-16.51, -25.53) * mm, "end": v(-16.47, -25.58) * mm});
            skLineSegment(sketch, "E4570", {"start": v(-16.47, -25.58) * mm, "end": v(-16.45, -25.63) * mm});
            skLineSegment(sketch, "E4571", {"start": v(-16.45, -25.63) * mm, "end": v(-16.43, -25.68) * mm});
            skLineSegment(sketch, "E4572", {"start": v(-16.43, -25.68) * mm, "end": v(-16.43, -25.73) * mm});
            skLineSegment(sketch, "E4573", {"start": v(-16.43, -25.73) * mm, "end": v(-16.44, -25.77) * mm});
            skLineSegment(sketch, "E4574", {"start": v(-16.44, -25.77) * mm, "end": v(-16.45, -25.82) * mm});
            skLineSegment(sketch, "E4575", {"start": v(-16.45, -25.82) * mm, "end": v(-16.47, -25.86) * mm});
            skLineSegment(sketch, "E4576", {"start": v(-16.47, -25.86) * mm, "end": v(-16.47, -25.9) * mm});
            skLineSegment(sketch, "E4577", {"start": v(-16.47, -25.9) * mm, "end": v(-16.44, -25.94) * mm});
            skLineSegment(sketch, "E4578", {"start": v(-16.44, -25.94) * mm, "end": v(-16.34, -26) * mm});
            skLineSegment(sketch, "E4579", {"start": v(-16.34, -26) * mm, "end": v(-16.3, -26.02) * mm});
            skLineSegment(sketch, "E4580", {"start": v(-16.3, -26.02) * mm, "end": v(-16.25, -26) * mm});
            skLineSegment(sketch, "E4581", {"start": v(-16.25, -26) * mm, "end": v(-16.22, -25.96) * mm});
            skLineSegment(sketch, "E4582", {"start": v(-16.22, -25.96) * mm, "end": v(-16.19, -25.93) * mm});
            skLineSegment(sketch, "E4583", {"start": v(-16.19, -25.93) * mm, "end": v(-16.15, -25.91) * mm});
            skLineSegment(sketch, "E4584", {"start": v(-16.15, -25.91) * mm, "end": v(-16.1, -25.89) * mm});
            skLineSegment(sketch, "E4585", {"start": v(-16.1, -25.89) * mm, "end": v(-16.05, -25.88) * mm});
            skLineSegment(sketch, "E4586", {"start": v(-16.05, -25.88) * mm, "end": v(-16, -25.88) * mm});
            skLineSegment(sketch, "E4587", {"start": v(-16, -25.88) * mm, "end": v(-15.94, -25.9) * mm});
            skLineSegment(sketch, "E4588", {"start": v(-15.94, -25.9) * mm, "end": v(-15.88, -25.92) * mm});
            skLineSegment(sketch, "E4589", {"start": v(-15.88, -25.92) * mm, "end": v(-15.84, -25.96) * mm});
            skLineSegment(sketch, "E4590", {"start": v(-15.84, -25.96) * mm, "end": v(-15.8, -26) * mm});
            skLineSegment(sketch, "E4591", {"start": v(-15.8, -26) * mm, "end": v(-15.77, -26.05) * mm});
            skLineSegment(sketch, "E4592", {"start": v(-15.77, -26.05) * mm, "end": v(-15.76, -26.1) * mm});
            skLineSegment(sketch, "E4593", {"start": v(-15.76, -26.1) * mm, "end": v(-15.75, -26.15) * mm});
            skLineSegment(sketch, "E4594", {"start": v(-15.75, -26.15) * mm, "end": v(-15.76, -26.2) * mm});
            skLineSegment(sketch, "E4595", {"start": v(-15.76, -26.2) * mm, "end": v(-15.77, -26.24) * mm});
            skLineSegment(sketch, "E4596", {"start": v(-15.77, -26.24) * mm, "end": v(-15.78, -26.28) * mm});
            skLineSegment(sketch, "E4597", {"start": v(-15.78, -26.28) * mm, "end": v(-15.78, -26.33) * mm});
            skLineSegment(sketch, "E4598", {"start": v(-15.78, -26.33) * mm, "end": v(-15.75, -26.36) * mm});
            skLineSegment(sketch, "E4599", {"start": v(-15.75, -26.36) * mm, "end": v(-15.65, -26.42) * mm});
            skLineSegment(sketch, "E4600", {"start": v(-15.65, -26.42) * mm, "end": v(-15.6, -26.43) * mm});
            skLineSegment(sketch, "E4601", {"start": v(-15.6, -26.43) * mm, "end": v(-15.56, -26.41) * mm});
            skLineSegment(sketch, "E4602", {"start": v(-15.56, -26.41) * mm, "end": v(-15.54, -26.38) * mm});
            skLineSegment(sketch, "E4603", {"start": v(-15.54, -26.38) * mm, "end": v(-15.5, -26.35) * mm});
            skLineSegment(sketch, "E4604", {"start": v(-15.5, -26.35) * mm, "end": v(-15.46, -26.32) * mm});
            skLineSegment(sketch, "E4605", {"start": v(-15.46, -26.32) * mm, "end": v(-15.42, -26.3) * mm});
            skLineSegment(sketch, "E4606", {"start": v(-15.42, -26.3) * mm, "end": v(-15.37, -26.3) * mm});
            skLineSegment(sketch, "E4607", {"start": v(-15.37, -26.3) * mm, "end": v(-15.31, -26.3) * mm});
            skLineSegment(sketch, "E4608", {"start": v(-15.31, -26.3) * mm, "end": v(-15.25, -26.3) * mm});
            skLineSegment(sketch, "E4609", {"start": v(-15.25, -26.3) * mm, "end": v(-15.2, -26.33) * mm});
            skLineSegment(sketch, "E4610", {"start": v(-15.2, -26.33) * mm, "end": v(-15.15, -26.36) * mm});
            skLineSegment(sketch, "E4611", {"start": v(-15.15, -26.36) * mm, "end": v(-15.11, -26.4) * mm});
            skLineSegment(sketch, "E4612", {"start": v(-15.11, -26.4) * mm, "end": v(-15.08, -26.45) * mm});
            skLineSegment(sketch, "E4613", {"start": v(-15.08, -26.45) * mm, "end": v(-15.07, -26.5) * mm});
            skLineSegment(sketch, "E4614", {"start": v(-15.07, -26.5) * mm, "end": v(-15.06, -26.55) * mm});
            skLineSegment(sketch, "E4615", {"start": v(-15.06, -26.55) * mm, "end": v(-15.07, -26.6) * mm});
            skLineSegment(sketch, "E4616", {"start": v(-15.07, -26.6) * mm, "end": v(-15.08, -26.64) * mm});
            skLineSegment(sketch, "E4617", {"start": v(-15.08, -26.64) * mm, "end": v(-15.1, -26.69) * mm});
            skLineSegment(sketch, "E4618", {"start": v(-15.1, -26.69) * mm, "end": v(-15.1, -26.73) * mm});
            skLineSegment(sketch, "E4619", {"start": v(-15.1, -26.73) * mm, "end": v(-15.06, -26.76) * mm});
            skLineSegment(sketch, "E4620", {"start": v(-15.06, -26.76) * mm, "end": v(-14.95, -26.82) * mm});
            skLineSegment(sketch, "E4621", {"start": v(-14.95, -26.82) * mm, "end": v(-14.9, -26.83) * mm});
            skLineSegment(sketch, "E4622", {"start": v(-14.9, -26.83) * mm, "end": v(-14.87, -26.81) * mm});
            skLineSegment(sketch, "E4623", {"start": v(-14.87, -26.81) * mm, "end": v(-14.84, -26.78) * mm});
            skLineSegment(sketch, "E4624", {"start": v(-14.84, -26.78) * mm, "end": v(-14.8, -26.75) * mm});
            skLineSegment(sketch, "E4625", {"start": v(-14.8, -26.75) * mm, "end": v(-14.77, -26.72) * mm});
            skLineSegment(sketch, "E4626", {"start": v(-14.77, -26.72) * mm, "end": v(-14.73, -26.7) * mm});
            skLineSegment(sketch, "E4627", {"start": v(-14.73, -26.7) * mm, "end": v(-14.67, -26.68) * mm});
            skLineSegment(sketch, "E4628", {"start": v(-14.67, -26.68) * mm, "end": v(-14.62, -26.68) * mm});
            skLineSegment(sketch, "E4629", {"start": v(-14.62, -26.68) * mm, "end": v(-14.56, -26.7) * mm});
            skLineSegment(sketch, "E4630", {"start": v(-14.56, -26.7) * mm, "end": v(-14.5, -26.72) * mm});
            skLineSegment(sketch, "E4631", {"start": v(-14.5, -26.72) * mm, "end": v(-14.46, -26.75) * mm});
            skLineSegment(sketch, "E4632", {"start": v(-14.46, -26.75) * mm, "end": v(-14.42, -26.8) * mm});
            skLineSegment(sketch, "E4633", {"start": v(-14.42, -26.8) * mm, "end": v(-14.39, -26.84) * mm});
            skLineSegment(sketch, "E4634", {"start": v(-14.39, -26.84) * mm, "end": v(-14.37, -26.9) * mm});
            skLineSegment(sketch, "E4635", {"start": v(-14.37, -26.9) * mm, "end": v(-14.36, -26.94) * mm});
            skLineSegment(sketch, "E4636", {"start": v(-14.36, -26.94) * mm, "end": v(-14.37, -26.99) * mm});
            skLineSegment(sketch, "E4637", {"start": v(-14.37, -26.99) * mm, "end": v(-14.37, -27.03) * mm});
            skLineSegment(sketch, "E4638", {"start": v(-14.37, -27.03) * mm, "end": v(-14.39, -27.07) * mm});
            skLineSegment(sketch, "E4639", {"start": v(-14.39, -27.07) * mm, "end": v(-14.39, -27.12) * mm});
            skLineSegment(sketch, "E4640", {"start": v(-14.39, -27.12) * mm, "end": v(-14.35, -27.15) * mm});
            skLineSegment(sketch, "E4641", {"start": v(-14.35, -27.15) * mm, "end": v(-14.25, -27.2) * mm});
            skLineSegment(sketch, "E4642", {"start": v(-14.25, -27.2) * mm, "end": v(-14.2, -27.21) * mm});
            skLineSegment(sketch, "E4643", {"start": v(-14.2, -27.21) * mm, "end": v(-14.16, -27.2) * mm});
            skLineSegment(sketch, "E4644", {"start": v(-14.16, -27.2) * mm, "end": v(-14.13, -27.16) * mm});
            skLineSegment(sketch, "E4645", {"start": v(-14.13, -27.16) * mm, "end": v(-14.1, -27.12) * mm});
            skLineSegment(sketch, "E4646", {"start": v(-14.1, -27.12) * mm, "end": v(-14.07, -27.1) * mm});
            skLineSegment(sketch, "E4647", {"start": v(-14.07, -27.1) * mm, "end": v(-14.03, -27.07) * mm});
            skLineSegment(sketch, "E4648", {"start": v(-14.03, -27.07) * mm, "end": v(-13.97, -27.06) * mm});
            skLineSegment(sketch, "E4649", {"start": v(-13.97, -27.06) * mm, "end": v(-13.91, -27.06) * mm});
            skLineSegment(sketch, "E4650", {"start": v(-13.91, -27.06) * mm, "end": v(-13.86, -27.07) * mm});
            skLineSegment(sketch, "E4651", {"start": v(-13.86, -27.07) * mm, "end": v(-13.8, -27.09) * mm});
            skLineSegment(sketch, "E4652", {"start": v(-13.8, -27.09) * mm, "end": v(-13.75, -27.12) * mm});
            skLineSegment(sketch, "E4653", {"start": v(-13.75, -27.12) * mm, "end": v(-13.71, -27.16) * mm});
            skLineSegment(sketch, "E4654", {"start": v(-13.71, -27.16) * mm, "end": v(-13.68, -27.2) * mm});
            skLineSegment(sketch, "E4655", {"start": v(-13.68, -27.2) * mm, "end": v(-13.66, -27.26) * mm});
            skLineSegment(sketch, "E4656", {"start": v(-13.66, -27.26) * mm, "end": v(-13.65, -27.3) * mm});
            skLineSegment(sketch, "E4657", {"start": v(-13.65, -27.3) * mm, "end": v(-13.66, -27.35) * mm});
            skLineSegment(sketch, "E4658", {"start": v(-13.66, -27.35) * mm, "end": v(-13.66, -27.4) * mm});
            skLineSegment(sketch, "E4659", {"start": v(-13.66, -27.4) * mm, "end": v(-13.67, -27.44) * mm});
            skLineSegment(sketch, "E4660", {"start": v(-13.67, -27.44) * mm, "end": v(-13.67, -27.48) * mm});
            skLineSegment(sketch, "E4661", {"start": v(-13.67, -27.48) * mm, "end": v(-13.64, -27.52) * mm});
            skLineSegment(sketch, "E4662", {"start": v(-13.64, -27.52) * mm, "end": v(-13.53, -27.57) * mm});
            skLineSegment(sketch, "E4663", {"start": v(-13.53, -27.57) * mm, "end": v(-13.48, -27.58) * mm});
            skLineSegment(sketch, "E4664", {"start": v(-13.48, -27.58) * mm, "end": v(-13.44, -27.55) * mm});
            skLineSegment(sketch, "E4665", {"start": v(-13.44, -27.55) * mm, "end": v(-13.42, -27.52) * mm});
            skLineSegment(sketch, "E4666", {"start": v(-13.42, -27.52) * mm, "end": v(-13.39, -27.48) * mm});
            skLineSegment(sketch, "E4667", {"start": v(-13.39, -27.48) * mm, "end": v(-13.35, -27.46) * mm});
            skLineSegment(sketch, "E4668", {"start": v(-13.35, -27.46) * mm, "end": v(-13.31, -27.43) * mm});
            skLineSegment(sketch, "E4669", {"start": v(-13.31, -27.43) * mm, "end": v(-13.26, -27.41) * mm});
            skLineSegment(sketch, "E4670", {"start": v(-13.26, -27.41) * mm, "end": v(-13.2, -27.41) * mm});
            skLineSegment(sketch, "E4671", {"start": v(-13.2, -27.41) * mm, "end": v(-13.14, -27.42) * mm});
            skLineSegment(sketch, "E4672", {"start": v(-13.14, -27.42) * mm, "end": v(-13.09, -27.44) * mm});
            skLineSegment(sketch, "E4673", {"start": v(-13.09, -27.44) * mm, "end": v(-13.04, -27.47) * mm});
            skLineSegment(sketch, "E4674", {"start": v(-13.04, -27.47) * mm, "end": v(-13, -27.5) * mm});
            skLineSegment(sketch, "E4675", {"start": v(-13, -27.5) * mm, "end": v(-12.96, -27.56) * mm});
            skLineSegment(sketch, "E4676", {"start": v(-12.96, -27.56) * mm, "end": v(-12.94, -27.6) * mm});
            skLineSegment(sketch, "E4677", {"start": v(-12.94, -27.6) * mm, "end": v(-12.94, -27.65) * mm});
            skLineSegment(sketch, "E4678", {"start": v(-12.94, -27.65) * mm, "end": v(-12.93, -27.7) * mm});
            skLineSegment(sketch, "E4679", {"start": v(-12.93, -27.7) * mm, "end": v(-12.94, -27.74) * mm});
            skLineSegment(sketch, "E4680", {"start": v(-12.94, -27.74) * mm, "end": v(-12.95, -27.79) * mm});
            skLineSegment(sketch, "E4681", {"start": v(-12.95, -27.79) * mm, "end": v(-12.95, -27.83) * mm});
            skLineSegment(sketch, "E4682", {"start": v(-12.95, -27.83) * mm, "end": v(-12.91, -27.86) * mm});
            skLineSegment(sketch, "E4683", {"start": v(-12.91, -27.86) * mm, "end": v(-12.8, -27.91) * mm});
            skLineSegment(sketch, "E4684", {"start": v(-12.8, -27.91) * mm, "end": v(-12.75, -27.92) * mm});
            skLineSegment(sketch, "E4685", {"start": v(-12.75, -27.92) * mm, "end": v(-12.72, -27.9) * mm});
            skLineSegment(sketch, "E4686", {"start": v(-12.72, -27.9) * mm, "end": v(-12.7, -27.86) * mm});
            skLineSegment(sketch, "E4687", {"start": v(-12.7, -27.86) * mm, "end": v(-12.66, -27.83) * mm});
            skLineSegment(sketch, "E4688", {"start": v(-12.66, -27.83) * mm, "end": v(-12.63, -27.8) * mm});
            skLineSegment(sketch, "E4689", {"start": v(-12.63, -27.8) * mm, "end": v(-12.6, -27.77) * mm});
            skLineSegment(sketch, "E4690", {"start": v(-12.6, -27.77) * mm, "end": v(-12.54, -27.75) * mm});
            skLineSegment(sketch, "E4691", {"start": v(-12.54, -27.75) * mm, "end": v(-12.48, -27.75) * mm});
            skLineSegment(sketch, "E4692", {"start": v(-12.48, -27.75) * mm, "end": v(-12.42, -27.75) * mm});
            skLineSegment(sketch, "E4693", {"start": v(-12.42, -27.75) * mm, "end": v(-12.36, -27.77) * mm});
            skLineSegment(sketch, "E4694", {"start": v(-12.36, -27.77) * mm, "end": v(-12.31, -27.8) * mm});
            skLineSegment(sketch, "E4695", {"start": v(-12.31, -27.8) * mm, "end": v(-12.27, -27.84) * mm});
            skLineSegment(sketch, "E4696", {"start": v(-12.27, -27.84) * mm, "end": v(-12.24, -27.89) * mm});
            skLineSegment(sketch, "E4697", {"start": v(-12.24, -27.89) * mm, "end": v(-12.21, -27.94) * mm});
            skLineSegment(sketch, "E4698", {"start": v(-12.21, -27.94) * mm, "end": v(-12.2, -27.98) * mm});
            skLineSegment(sketch, "E4699", {"start": v(-12.2, -27.98) * mm, "end": v(-12.2, -28.03) * mm});
            skLineSegment(sketch, "E4700", {"start": v(-12.2, -28.03) * mm, "end": v(-12.2, -28.07) * mm});
            skLineSegment(sketch, "E4701", {"start": v(-12.2, -28.07) * mm, "end": v(-12.22, -28.12) * mm});
            skLineSegment(sketch, "E4702", {"start": v(-12.22, -28.12) * mm, "end": v(-12.21, -28.16) * mm});
            skLineSegment(sketch, "E4703", {"start": v(-12.21, -28.16) * mm, "end": v(-12.18, -28.2) * mm});
            skLineSegment(sketch, "E4704", {"start": v(-12.18, -28.2) * mm, "end": v(-12.07, -28.24) * mm});
            skLineSegment(sketch, "E4705", {"start": v(-12.07, -28.24) * mm, "end": v(-12.02, -28.24) * mm});
            skLineSegment(sketch, "E4706", {"start": v(-12.02, -28.24) * mm, "end": v(-11.98, -28.22) * mm});
            skLineSegment(sketch, "E4707", {"start": v(-11.98, -28.22) * mm, "end": v(-11.96, -28.18) * mm});
            skLineSegment(sketch, "E4708", {"start": v(-11.96, -28.18) * mm, "end": v(-11.93, -28.15) * mm});
            skLineSegment(sketch, "E4709", {"start": v(-11.93, -28.15) * mm, "end": v(-11.9, -28.12) * mm});
            skLineSegment(sketch, "E4710", {"start": v(-11.9, -28.12) * mm, "end": v(-11.86, -28.1) * mm});
            skLineSegment(sketch, "E4711", {"start": v(-11.86, -28.1) * mm, "end": v(-11.8, -28.07) * mm});
            skLineSegment(sketch, "E4712", {"start": v(-11.8, -28.07) * mm, "end": v(-11.75, -28.06) * mm});
            skLineSegment(sketch, "E4713", {"start": v(-11.75, -28.06) * mm, "end": v(-11.69, -28.07) * mm});
            skLineSegment(sketch, "E4714", {"start": v(-11.69, -28.07) * mm, "end": v(-11.63, -28.09) * mm});
            skLineSegment(sketch, "E4715", {"start": v(-11.63, -28.09) * mm, "end": v(-11.58, -28.11) * mm});
            skLineSegment(sketch, "E4716", {"start": v(-11.58, -28.11) * mm, "end": v(-11.54, -28.15) * mm});
            skLineSegment(sketch, "E4717", {"start": v(-11.54, -28.15) * mm, "end": v(-11.5, -28.2) * mm});
            skLineSegment(sketch, "E4718", {"start": v(-11.5, -28.2) * mm, "end": v(-11.48, -28.25) * mm});
            skLineSegment(sketch, "E4719", {"start": v(-11.48, -28.25) * mm, "end": v(-11.47, -28.3) * mm});
            skLineSegment(sketch, "E4720", {"start": v(-11.47, -28.3) * mm, "end": v(-11.47, -28.34) * mm});
            skLineSegment(sketch, "E4721", {"start": v(-11.47, -28.34) * mm, "end": v(-11.47, -28.38) * mm});
            skLineSegment(sketch, "E4722", {"start": v(-11.47, -28.38) * mm, "end": v(-11.48, -28.43) * mm});
            skLineSegment(sketch, "E4723", {"start": v(-11.48, -28.43) * mm, "end": v(-11.47, -28.47) * mm});
            skLineSegment(sketch, "E4724", {"start": v(-11.47, -28.47) * mm, "end": v(-11.44, -28.5) * mm});
            skLineSegment(sketch, "E4725", {"start": v(-11.44, -28.5) * mm, "end": v(-11.32, -28.55) * mm});
            skLineSegment(sketch, "E4726", {"start": v(-11.32, -28.55) * mm, "end": v(-11.28, -28.55) * mm});
            skLineSegment(sketch, "E4727", {"start": v(-11.28, -28.55) * mm, "end": v(-11.24, -28.52) * mm});
            skLineSegment(sketch, "E4728", {"start": v(-11.24, -28.52) * mm, "end": v(-11.22, -28.48) * mm});
            skLineSegment(sketch, "E4729", {"start": v(-11.22, -28.48) * mm, "end": v(-11.19, -28.45) * mm});
            skLineSegment(sketch, "E4730", {"start": v(-11.19, -28.45) * mm, "end": v(-11.16, -28.42) * mm});
            skLineSegment(sketch, "E4731", {"start": v(-11.16, -28.42) * mm, "end": v(-11.12, -28.4) * mm});
            skLineSegment(sketch, "E4732", {"start": v(-11.12, -28.4) * mm, "end": v(-11.07, -28.37) * mm});
            skLineSegment(sketch, "E4733", {"start": v(-11.07, -28.37) * mm, "end": v(-11, -28.36) * mm});
            skLineSegment(sketch, "E4734", {"start": v(-11, -28.36) * mm, "end": v(-10.95, -28.37) * mm});
            skLineSegment(sketch, "E4735", {"start": v(-10.95, -28.37) * mm, "end": v(-10.9, -28.38) * mm});
            skLineSegment(sketch, "E4736", {"start": v(-10.9, -28.38) * mm, "end": v(-10.84, -28.4) * mm});
            skLineSegment(sketch, "E4737", {"start": v(-10.84, -28.4) * mm, "end": v(-10.8, -28.44) * mm});
            skLineSegment(sketch, "E4738", {"start": v(-10.8, -28.44) * mm, "end": v(-10.76, -28.49) * mm});
            skLineSegment(sketch, "E4739", {"start": v(-10.76, -28.49) * mm, "end": v(-10.73, -28.54) * mm});
            skLineSegment(sketch, "E4740", {"start": v(-10.73, -28.54) * mm, "end": v(-10.73, -28.58) * mm});
            skLineSegment(sketch, "E4741", {"start": v(-10.73, -28.58) * mm, "end": v(-10.72, -28.63) * mm});
            skLineSegment(sketch, "E4742", {"start": v(-10.72, -28.63) * mm, "end": v(-10.72, -28.67) * mm});
            skLineSegment(sketch, "E4743", {"start": v(-10.72, -28.67) * mm, "end": v(-10.73, -28.72) * mm});
            skLineSegment(sketch, "E4744", {"start": v(-10.73, -28.72) * mm, "end": v(-10.72, -28.76) * mm});
            skLineSegment(sketch, "E4745", {"start": v(-10.72, -28.76) * mm, "end": v(-10.69, -28.8) * mm});
            skLineSegment(sketch, "E4746", {"start": v(-10.69, -28.8) * mm, "end": v(-10.57, -28.83) * mm});
            skLineSegment(sketch, "E4747", {"start": v(-10.57, -28.83) * mm, "end": v(-10.53, -28.83) * mm});
            skLineSegment(sketch, "E4748", {"start": v(-10.53, -28.83) * mm, "end": v(-10.5, -28.8) * mm});
            skLineSegment(sketch, "E4749", {"start": v(-10.5, -28.8) * mm, "end": v(-10.47, -28.77) * mm});
            skLineSegment(sketch, "E4750", {"start": v(-10.47, -28.77) * mm, "end": v(-10.44, -28.73) * mm});
            skLineSegment(sketch, "E4751", {"start": v(-10.44, -28.73) * mm, "end": v(-10.4, -28.7) * mm});
            skLineSegment(sketch, "E4752", {"start": v(-10.4, -28.7) * mm, "end": v(-10.37, -28.67) * mm});
            skLineSegment(sketch, "E4753", {"start": v(-10.37, -28.67) * mm, "end": v(-10.32, -28.65) * mm});
            skLineSegment(sketch, "E4754", {"start": v(-10.32, -28.65) * mm, "end": v(-10.26, -28.64) * mm});
            skLineSegment(sketch, "E4755", {"start": v(-10.26, -28.64) * mm, "end": v(-10.2, -28.64) * mm});
            skLineSegment(sketch, "E4756", {"start": v(-10.2, -28.64) * mm, "end": v(-10.15, -28.66) * mm});
            skLineSegment(sketch, "E4757", {"start": v(-10.15, -28.66) * mm, "end": v(-10.1, -28.68) * mm});
            skLineSegment(sketch, "E4758", {"start": v(-10.1, -28.68) * mm, "end": v(-10.05, -28.72) * mm});
            skLineSegment(sketch, "E4759", {"start": v(-10.05, -28.72) * mm, "end": v(-10.01, -28.76) * mm});
            skLineSegment(sketch, "E4760", {"start": v(-10.01, -28.76) * mm, "end": v(-9.98, -28.81) * mm});
            skLineSegment(sketch, "E4761", {"start": v(-9.98, -28.81) * mm, "end": v(-9.97, -28.86) * mm});
            skLineSegment(sketch, "E4762", {"start": v(-9.97, -28.86) * mm, "end": v(-9.97, -28.9) * mm});
            skLineSegment(sketch, "E4763", {"start": v(-9.97, -28.9) * mm, "end": v(-9.97, -28.94) * mm});
            skLineSegment(sketch, "E4764", {"start": v(-9.97, -28.94) * mm, "end": v(-9.98, -28.99) * mm});
            skLineSegment(sketch, "E4765", {"start": v(-9.98, -28.99) * mm, "end": v(-9.97, -29.03) * mm});
            skLineSegment(sketch, "E4766", {"start": v(-9.97, -29.03) * mm, "end": v(-9.93, -29.06) * mm});
            skLineSegment(sketch, "E4767", {"start": v(-9.93, -29.06) * mm, "end": v(-9.81, -29.1) * mm});
            skLineSegment(sketch, "E4768", {"start": v(-9.81, -29.1) * mm, "end": v(-9.77, -29.1) * mm});
            skLineSegment(sketch, "E4769", {"start": v(-9.77, -29.1) * mm, "end": v(-9.73, -29.07) * mm});
            skLineSegment(sketch, "E4770", {"start": v(-9.73, -29.07) * mm, "end": v(-9.71, -29.03) * mm});
            skLineSegment(sketch, "E4771", {"start": v(-9.71, -29.03) * mm, "end": v(-9.68, -29) * mm});
            skLineSegment(sketch, "E4772", {"start": v(-9.68, -29) * mm, "end": v(-9.65, -28.96) * mm});
            skLineSegment(sketch, "E4773", {"start": v(-9.65, -28.96) * mm, "end": v(-9.62, -28.93) * mm});
            skLineSegment(sketch, "E4774", {"start": v(-9.62, -28.93) * mm, "end": v(-9.57, -28.91) * mm});
            skLineSegment(sketch, "E4775", {"start": v(-9.57, -28.91) * mm, "end": v(-9.5, -28.9) * mm});
            skLineSegment(sketch, "E4776", {"start": v(-9.5, -28.9) * mm, "end": v(-9.45, -28.9) * mm});
            skLineSegment(sketch, "E4777", {"start": v(-9.45, -28.9) * mm, "end": v(-9.4, -28.91) * mm});
            skLineSegment(sketch, "E4778", {"start": v(-9.4, -28.91) * mm, "end": v(-9.34, -28.94) * mm});
            skLineSegment(sketch, "E4779", {"start": v(-9.34, -28.94) * mm, "end": v(-9.3, -28.97) * mm});
            skLineSegment(sketch, "E4780", {"start": v(-9.3, -28.97) * mm, "end": v(-9.25, -29.01) * mm});
            skLineSegment(sketch, "E4781", {"start": v(-9.25, -29.01) * mm, "end": v(-9.23, -29.06) * mm});
            skLineSegment(sketch, "E4782", {"start": v(-9.23, -29.06) * mm, "end": v(-9.21, -29.1) * mm});
            skLineSegment(sketch, "E4783", {"start": v(-9.21, -29.1) * mm, "end": v(-9.2, -29.15) * mm});
            skLineSegment(sketch, "E4784", {"start": v(-9.2, -29.15) * mm, "end": v(-9.2, -29.2) * mm});
            skLineSegment(sketch, "E4785", {"start": v(-9.2, -29.2) * mm, "end": v(-9.21, -29.24) * mm});
            skLineSegment(sketch, "E4786", {"start": v(-9.21, -29.24) * mm, "end": v(-9.2, -29.28) * mm});
            skLineSegment(sketch, "E4787", {"start": v(-9.2, -29.28) * mm, "end": v(-9.16, -29.31) * mm});
            skLineSegment(sketch, "E4788", {"start": v(-9.16, -29.31) * mm, "end": v(-9.05, -29.35) * mm});
            skLineSegment(sketch, "E4789", {"start": v(-9.05, -29.35) * mm, "end": v(-9, -29.35) * mm});
            skLineSegment(sketch, "E4790", {"start": v(-9, -29.35) * mm, "end": v(-8.97, -29.32) * mm});
            skLineSegment(sketch, "E4791", {"start": v(-8.97, -29.32) * mm, "end": v(-8.95, -29.28) * mm});
            skLineSegment(sketch, "E4792", {"start": v(-8.95, -29.28) * mm, "end": v(-8.92, -29.24) * mm});
            skLineSegment(sketch, "E4793", {"start": v(-8.92, -29.24) * mm, "end": v(-8.9, -29.2) * mm});
            skLineSegment(sketch, "E4794", {"start": v(-8.9, -29.2) * mm, "end": v(-8.86, -29.18) * mm});
            skLineSegment(sketch, "E4795", {"start": v(-8.86, -29.18) * mm, "end": v(-8.8, -29.15) * mm});
            skLineSegment(sketch, "E4796", {"start": v(-8.8, -29.15) * mm, "end": v(-8.75, -29.14) * mm});
            skLineSegment(sketch, "E4797", {"start": v(-8.75, -29.14) * mm, "end": v(-8.7, -29.14) * mm});
            skLineSegment(sketch, "E4798", {"start": v(-8.7, -29.14) * mm, "end": v(-8.63, -29.15) * mm});
            skLineSegment(sketch, "E4799", {"start": v(-8.63, -29.15) * mm, "end": v(-8.58, -29.17) * mm});
            skLineSegment(sketch, "E4800", {"start": v(-8.58, -29.17) * mm, "end": v(-8.53, -29.2) * mm});
            skLineSegment(sketch, "E4801", {"start": v(-8.53, -29.2) * mm, "end": v(-8.5, -29.24) * mm});
            skLineSegment(sketch, "E4802", {"start": v(-8.5, -29.24) * mm, "end": v(-8.46, -29.3) * mm});
            skLineSegment(sketch, "E4803", {"start": v(-8.46, -29.3) * mm, "end": v(-8.45, -29.34) * mm});
            skLineSegment(sketch, "E4804", {"start": v(-8.45, -29.34) * mm, "end": v(-8.44, -29.38) * mm});
            skLineSegment(sketch, "E4805", {"start": v(-8.44, -29.38) * mm, "end": v(-8.44, -29.43) * mm});
            skLineSegment(sketch, "E4806", {"start": v(-8.44, -29.43) * mm, "end": v(-8.44, -29.47) * mm});
            skLineSegment(sketch, "E4807", {"start": v(-8.44, -29.47) * mm, "end": v(-8.43, -29.51) * mm});
            skLineSegment(sketch, "E4808", {"start": v(-8.43, -29.51) * mm, "end": v(-8.4, -29.54) * mm});
            skLineSegment(sketch, "E4809", {"start": v(-8.4, -29.54) * mm, "end": v(-8.28, -29.57) * mm});
            skLineSegment(sketch, "E4810", {"start": v(-8.28, -29.57) * mm, "end": v(-8.23, -29.57) * mm});
            skLineSegment(sketch, "E4811", {"start": v(-8.23, -29.57) * mm, "end": v(-8.2, -29.54) * mm});
            skLineSegment(sketch, "E4812", {"start": v(-8.2, -29.54) * mm, "end": v(-8.18, -29.5) * mm});
            skLineSegment(sketch, "E4813", {"start": v(-8.18, -29.5) * mm, "end": v(-8.15, -29.46) * mm});
            skLineSegment(sketch, "E4814", {"start": v(-8.15, -29.46) * mm, "end": v(-8.12, -29.43) * mm});
            skLineSegment(sketch, "E4815", {"start": v(-8.12, -29.43) * mm, "end": v(-8.1, -29.4) * mm});
            skLineSegment(sketch, "E4816", {"start": v(-8.1, -29.4) * mm, "end": v(-8.04, -29.37) * mm});
            skLineSegment(sketch, "E4817", {"start": v(-8.04, -29.37) * mm, "end": v(-7.98, -29.36) * mm});
            skLineSegment(sketch, "E4818", {"start": v(-7.98, -29.36) * mm, "end": v(-7.93, -29.35) * mm});
            skLineSegment(sketch, "E4819", {"start": v(-7.93, -29.35) * mm, "end": v(-7.87, -29.36) * mm});
            skLineSegment(sketch, "E4820", {"start": v(-7.87, -29.36) * mm, "end": v(-7.81, -29.39) * mm});
            skLineSegment(sketch, "E4821", {"start": v(-7.81, -29.39) * mm, "end": v(-7.76, -29.42) * mm});
            skLineSegment(sketch, "E4822", {"start": v(-7.76, -29.42) * mm, "end": v(-7.72, -29.46) * mm});
            skLineSegment(sketch, "E4823", {"start": v(-7.72, -29.46) * mm, "end": v(-7.7, -29.5) * mm});
            skLineSegment(sketch, "E4824", {"start": v(-7.7, -29.5) * mm, "end": v(-7.68, -29.55) * mm});
            skLineSegment(sketch, "E4825", {"start": v(-7.68, -29.55) * mm, "end": v(-7.67, -29.6) * mm});
            skLineSegment(sketch, "E4826", {"start": v(-7.67, -29.6) * mm, "end": v(-7.67, -29.64) * mm});
            skLineSegment(sketch, "E4827", {"start": v(-7.67, -29.64) * mm, "end": v(-7.67, -29.68) * mm});
            skLineSegment(sketch, "E4828", {"start": v(-7.67, -29.68) * mm, "end": v(-7.66, -29.72) * mm});
            skLineSegment(sketch, "E4829", {"start": v(-7.66, -29.72) * mm, "end": v(-7.62, -29.75) * mm});
            skLineSegment(sketch, "E4830", {"start": v(-7.62, -29.75) * mm, "end": v(-7.5, -29.78) * mm});
            skLineSegment(sketch, "E4831", {"start": v(-7.5, -29.78) * mm, "end": v(-7.45, -29.78) * mm});
            skLineSegment(sketch, "E4832", {"start": v(-7.45, -29.78) * mm, "end": v(-7.42, -29.75) * mm});
            skLineSegment(sketch, "E4833", {"start": v(-7.42, -29.75) * mm, "end": v(-7.4, -29.7) * mm});
            skLineSegment(sketch, "E4834", {"start": v(-7.4, -29.7) * mm, "end": v(-7.38, -29.67) * mm});
            skLineSegment(sketch, "E4835", {"start": v(-7.38, -29.67) * mm, "end": v(-7.35, -29.63) * mm});
            skLineSegment(sketch, "E4836", {"start": v(-7.35, -29.63) * mm, "end": v(-7.32, -29.6) * mm});
            skLineSegment(sketch, "E4837", {"start": v(-7.32, -29.6) * mm, "end": v(-7.27, -29.57) * mm});
            skLineSegment(sketch, "E4838", {"start": v(-7.27, -29.57) * mm, "end": v(-7.21, -29.56) * mm});
            skLineSegment(sketch, "E4839", {"start": v(-7.21, -29.56) * mm, "end": v(-7.15, -29.55) * mm});
            skLineSegment(sketch, "E4840", {"start": v(-7.15, -29.55) * mm, "end": v(-7.1, -29.56) * mm});
            skLineSegment(sketch, "E4841", {"start": v(-7.1, -29.56) * mm, "end": v(-7.04, -29.58) * mm});
            skLineSegment(sketch, "E4842", {"start": v(-7.04, -29.58) * mm, "end": v(-7, -29.6) * mm});
            skLineSegment(sketch, "E4843", {"start": v(-7, -29.6) * mm, "end": v(-6.95, -29.65) * mm});
            skLineSegment(sketch, "E4844", {"start": v(-6.95, -29.65) * mm, "end": v(-6.92, -29.7) * mm});
            skLineSegment(sketch, "E4845", {"start": v(-6.92, -29.7) * mm, "end": v(-6.9, -29.74) * mm});
            skLineSegment(sketch, "E4846", {"start": v(-6.9, -29.74) * mm, "end": v(-6.9, -29.78) * mm});
            skLineSegment(sketch, "E4847", {"start": v(-6.9, -29.78) * mm, "end": v(-6.89, -29.83) * mm});
            skLineSegment(sketch, "E4848", {"start": v(-6.89, -29.83) * mm, "end": v(-6.9, -29.87) * mm});
            skLineSegment(sketch, "E4849", {"start": v(-6.9, -29.87) * mm, "end": v(-6.88, -29.91) * mm});
            skLineSegment(sketch, "E4850", {"start": v(-6.88, -29.91) * mm, "end": v(-6.84, -29.94) * mm});
            skLineSegment(sketch, "E4851", {"start": v(-6.84, -29.94) * mm, "end": v(-6.72, -29.97) * mm});
            skLineSegment(sketch, "E4852", {"start": v(-6.72, -29.97) * mm, "end": v(-6.67, -29.96) * mm});
            skLineSegment(sketch, "E4853", {"start": v(-6.67, -29.96) * mm, "end": v(-6.64, -29.93) * mm});
            skLineSegment(sketch, "E4854", {"start": v(-6.64, -29.93) * mm, "end": v(-6.62, -29.89) * mm});
            skLineSegment(sketch, "E4855", {"start": v(-6.62, -29.89) * mm, "end": v(-6.6, -29.85) * mm});
            skLineSegment(sketch, "E4856", {"start": v(-6.6, -29.85) * mm, "end": v(-6.57, -29.81) * mm});
            skLineSegment(sketch, "E4857", {"start": v(-6.57, -29.81) * mm, "end": v(-6.54, -29.78) * mm});
            skLineSegment(sketch, "E4858", {"start": v(-6.54, -29.78) * mm, "end": v(-6.5, -29.75) * mm});
            skLineSegment(sketch, "E4859", {"start": v(-6.5, -29.75) * mm, "end": v(-6.44, -29.73) * mm});
            skLineSegment(sketch, "E4860", {"start": v(-6.44, -29.73) * mm, "end": v(-6.38, -29.73) * mm});
            skLineSegment(sketch, "E4861", {"start": v(-6.38, -29.73) * mm, "end": v(-6.32, -29.74) * mm});
            skLineSegment(sketch, "E4862", {"start": v(-6.32, -29.74) * mm, "end": v(-6.26, -29.75) * mm});
            skLineSegment(sketch, "E4863", {"start": v(-6.26, -29.75) * mm, "end": v(-6.21, -29.78) * mm});
            skLineSegment(sketch, "E4864", {"start": v(-6.21, -29.78) * mm, "end": v(-6.17, -29.82) * mm});
            skLineSegment(sketch, "E4865", {"start": v(-6.17, -29.82) * mm, "end": v(-6.14, -29.87) * mm});
            skLineSegment(sketch, "E4866", {"start": v(-6.14, -29.87) * mm, "end": v(-6.12, -29.91) * mm});
            skLineSegment(sketch, "E4867", {"start": v(-6.12, -29.91) * mm, "end": v(-6.11, -29.95) * mm});
            skLineSegment(sketch, "E4868", {"start": v(-6.11, -29.95) * mm, "end": v(-6.1, -30) * mm});
            skLineSegment(sketch, "E4869", {"start": v(-6.1, -30) * mm, "end": v(-6.1, -30.04) * mm});
            skLineSegment(sketch, "E4870", {"start": v(-6.1, -30.04) * mm, "end": v(-6.1, -30.08) * mm});
            skLineSegment(sketch, "E4871", {"start": v(-6.1, -30.08) * mm, "end": v(-6.05, -30.1) * mm});
            skLineSegment(sketch, "E4872", {"start": v(-6.05, -30.1) * mm, "end": v(-5.93, -30.13) * mm});
            skLineSegment(sketch, "E4873", {"start": v(-5.93, -30.13) * mm, "end": v(-5.88, -30.13) * mm});
            skLineSegment(sketch, "E4874", {"start": v(-5.88, -30.13) * mm, "end": v(-5.86, -30.1) * mm});
            skLineSegment(sketch, "E4875", {"start": v(-5.86, -30.1) * mm, "end": v(-5.84, -30.05) * mm});
            skLineSegment(sketch, "E4876", {"start": v(-5.84, -30.05) * mm, "end": v(-5.82, -30.01) * mm});
            skLineSegment(sketch, "E4877", {"start": v(-5.82, -30.01) * mm, "end": v(-5.8, -29.98) * mm});
            skLineSegment(sketch, "E4878", {"start": v(-5.8, -29.98) * mm, "end": v(-5.76, -29.94) * mm});
            skLineSegment(sketch, "E4879", {"start": v(-5.76, -29.94) * mm, "end": v(-5.71, -29.91) * mm});
            skLineSegment(sketch, "E4880", {"start": v(-5.71, -29.91) * mm, "end": v(-5.66, -29.9) * mm});
            skLineSegment(sketch, "E4881", {"start": v(-5.66, -29.9) * mm, "end": v(-5.6, -29.89) * mm});
            skLineSegment(sketch, "E4882", {"start": v(-5.6, -29.89) * mm, "end": v(-5.54, -29.9) * mm});
            skLineSegment(sketch, "E4883", {"start": v(-5.54, -29.9) * mm, "end": v(-5.48, -29.9) * mm});
            skLineSegment(sketch, "E4884", {"start": v(-5.48, -29.9) * mm, "end": v(-5.43, -29.93) * mm});
            skLineSegment(sketch, "E4885", {"start": v(-5.43, -29.93) * mm, "end": v(-5.39, -29.97) * mm});
            skLineSegment(sketch, "E4886", {"start": v(-5.39, -29.97) * mm, "end": v(-5.35, -30.02) * mm});
            skLineSegment(sketch, "E4887", {"start": v(-5.35, -30.02) * mm, "end": v(-5.34, -30.06) * mm});
            skLineSegment(sketch, "E4888", {"start": v(-5.34, -30.06) * mm, "end": v(-5.32, -30.1) * mm});
            skLineSegment(sketch, "E4889", {"start": v(-5.32, -30.1) * mm, "end": v(-5.32, -30.15) * mm});
            skLineSegment(sketch, "E4890", {"start": v(-5.32, -30.15) * mm, "end": v(-5.32, -30.2) * mm});
            skLineSegment(sketch, "E4891", {"start": v(-5.32, -30.2) * mm, "end": v(-5.3, -30.23) * mm});
            skLineSegment(sketch, "E4892", {"start": v(-5.3, -30.23) * mm, "end": v(-5.26, -30.26) * mm});
            skLineSegment(sketch, "E4893", {"start": v(-5.26, -30.26) * mm, "end": v(-5.14, -30.28) * mm});
            skLineSegment(sketch, "E4894", {"start": v(-5.14, -30.28) * mm, "end": v(-5.1, -30.27) * mm});
            skLineSegment(sketch, "E4895", {"start": v(-5.1, -30.27) * mm, "end": v(-5.07, -30.24) * mm});
            skLineSegment(sketch, "E4896", {"start": v(-5.07, -30.24) * mm, "end": v(-5.05, -30.2) * mm});
            skLineSegment(sketch, "E4897", {"start": v(-5.05, -30.2) * mm, "end": v(-5.03, -30.15) * mm});
            skLineSegment(sketch, "E4898", {"start": v(-5.03, -30.15) * mm, "end": v(-5, -30.12) * mm});
            skLineSegment(sketch, "E4899", {"start": v(-5, -30.12) * mm, "end": v(-4.97, -30.08) * mm});
            skLineSegment(sketch, "E4900", {"start": v(-4.97, -30.08) * mm, "end": v(-4.93, -30.05) * mm});
            skLineSegment(sketch, "E4901", {"start": v(-4.93, -30.05) * mm, "end": v(-4.87, -30.03) * mm});
            skLineSegment(sketch, "E4902", {"start": v(-4.87, -30.03) * mm, "end": v(-4.81, -30.02) * mm});
            skLineSegment(sketch, "E4903", {"start": v(-4.81, -30.02) * mm, "end": v(-4.76, -30.03) * mm});
            skLineSegment(sketch, "E4904", {"start": v(-4.76, -30.03) * mm, "end": v(-4.7, -30.04) * mm});
            skLineSegment(sketch, "E4905", {"start": v(-4.7, -30.04) * mm, "end": v(-4.65, -30.07) * mm});
            skLineSegment(sketch, "E4906", {"start": v(-4.65, -30.07) * mm, "end": v(-4.6, -30.1) * mm});
            skLineSegment(sketch, "E4907", {"start": v(-4.6, -30.1) * mm, "end": v(-4.57, -30.15) * mm});
            skLineSegment(sketch, "E4908", {"start": v(-4.57, -30.15) * mm, "end": v(-4.55, -30.19) * mm});
            skLineSegment(sketch, "E4909", {"start": v(-4.55, -30.19) * mm, "end": v(-4.54, -30.23) * mm});
            skLineSegment(sketch, "E4910", {"start": v(-4.54, -30.23) * mm, "end": v(-4.53, -30.28) * mm});
            skLineSegment(sketch, "E4911", {"start": v(-4.53, -30.28) * mm, "end": v(-4.53, -30.32) * mm});
            skLineSegment(sketch, "E4912", {"start": v(-4.53, -30.32) * mm, "end": v(-4.5, -30.36) * mm});
            skLineSegment(sketch, "E4913", {"start": v(-4.5, -30.36) * mm, "end": v(-4.47, -30.38) * mm});
            skLineSegment(sketch, "E4914", {"start": v(-4.47, -30.38) * mm, "end": v(-4.35, -30.4) * mm});
            skLineSegment(sketch, "E4915", {"start": v(-4.35, -30.4) * mm, "end": v(-4.3, -30.4) * mm});
            skLineSegment(sketch, "E4916", {"start": v(-4.3, -30.4) * mm, "end": v(-4.27, -30.36) * mm});
            skLineSegment(sketch, "E4917", {"start": v(-4.27, -30.36) * mm, "end": v(-4.26, -30.32) * mm});
            skLineSegment(sketch, "E4918", {"start": v(-4.26, -30.32) * mm, "end": v(-4.24, -30.28) * mm});
            skLineSegment(sketch, "E4919", {"start": v(-4.24, -30.28) * mm, "end": v(-4.21, -30.24) * mm});
            skLineSegment(sketch, "E4920", {"start": v(-4.21, -30.24) * mm, "end": v(-4.18, -30.2) * mm});
            skLineSegment(sketch, "E4921", {"start": v(-4.18, -30.2) * mm, "end": v(-4.14, -30.17) * mm});
            skLineSegment(sketch, "E4922", {"start": v(-4.14, -30.17) * mm, "end": v(-4.08, -30.15) * mm});
            skLineSegment(sketch, "E4923", {"start": v(-4.08, -30.15) * mm, "end": v(-4.03, -30.14) * mm});
            skLineSegment(sketch, "E4924", {"start": v(-4.03, -30.14) * mm, "end": v(-3.97, -30.14) * mm});
            skLineSegment(sketch, "E4925", {"start": v(-3.97, -30.14) * mm, "end": v(-3.91, -30.15) * mm});
            skLineSegment(sketch, "E4926", {"start": v(-3.91, -30.15) * mm, "end": v(-3.86, -30.18) * mm});
            skLineSegment(sketch, "E4927", {"start": v(-3.86, -30.18) * mm, "end": v(-3.81, -30.21) * mm});
            skLineSegment(sketch, "E4928", {"start": v(-3.81, -30.21) * mm, "end": v(-3.78, -30.26) * mm});
            skLineSegment(sketch, "E4929", {"start": v(-3.78, -30.26) * mm, "end": v(-3.76, -30.3) * mm});
            skLineSegment(sketch, "E4930", {"start": v(-3.76, -30.3) * mm, "end": v(-3.74, -30.34) * mm});
            skLineSegment(sketch, "E4931", {"start": v(-3.74, -30.34) * mm, "end": v(-3.73, -30.39) * mm});
            skLineSegment(sketch, "E4932", {"start": v(-3.73, -30.39) * mm, "end": v(-3.73, -30.43) * mm});
            skLineSegment(sketch, "E4933", {"start": v(-3.73, -30.43) * mm, "end": v(-3.71, -30.47) * mm});
            skLineSegment(sketch, "E4934", {"start": v(-3.71, -30.47) * mm, "end": v(-3.67, -30.5) * mm});
            skLineSegment(sketch, "E4935", {"start": v(-3.67, -30.5) * mm, "end": v(-3.55, -30.5) * mm});
            skLineSegment(sketch, "E4936", {"start": v(-3.55, -30.5) * mm, "end": v(-3.5, -30.5) * mm});
            skLineSegment(sketch, "E4937", {"start": v(-3.5, -30.5) * mm, "end": v(-3.48, -30.46) * mm});
            skLineSegment(sketch, "E4938", {"start": v(-3.48, -30.46) * mm, "end": v(-3.46, -30.42) * mm});
            skLineSegment(sketch, "E4939", {"start": v(-3.46, -30.42) * mm, "end": v(-3.44, -30.38) * mm});
            skLineSegment(sketch, "E4940", {"start": v(-3.44, -30.38) * mm, "end": v(-3.42, -30.34) * mm});
            skLineSegment(sketch, "E4941", {"start": v(-3.42, -30.34) * mm, "end": v(-3.4, -30.3) * mm});
            skLineSegment(sketch, "E4942", {"start": v(-3.4, -30.3) * mm, "end": v(-3.35, -30.27) * mm});
            skLineSegment(sketch, "E4943", {"start": v(-3.35, -30.27) * mm, "end": v(-3.3, -30.24) * mm});
            skLineSegment(sketch, "E4944", {"start": v(-3.3, -30.24) * mm, "end": v(-3.24, -30.23) * mm});
            skLineSegment(sketch, "E4945", {"start": v(-3.24, -30.23) * mm, "end": v(-3.18, -30.23) * mm});
            skLineSegment(sketch, "E4946", {"start": v(-3.18, -30.23) * mm, "end": v(-3.12, -30.25) * mm});
            skLineSegment(sketch, "E4947", {"start": v(-3.12, -30.25) * mm, "end": v(-3.07, -30.27) * mm});
            skLineSegment(sketch, "E4948", {"start": v(-3.07, -30.27) * mm, "end": v(-3.02, -30.3) * mm});
            skLineSegment(sketch, "E4949", {"start": v(-3.02, -30.3) * mm, "end": v(-2.98, -30.35) * mm});
            skLineSegment(sketch, "E4950", {"start": v(-2.98, -30.35) * mm, "end": v(-2.96, -30.39) * mm});
            skLineSegment(sketch, "E4951", {"start": v(-2.96, -30.39) * mm, "end": v(-2.95, -30.43) * mm});
            skLineSegment(sketch, "E4952", {"start": v(-2.95, -30.43) * mm, "end": v(-2.94, -30.47) * mm});
            skLineSegment(sketch, "E4953", {"start": v(-2.94, -30.47) * mm, "end": v(-2.93, -30.52) * mm});
            skLineSegment(sketch, "E4954", {"start": v(-2.93, -30.52) * mm, "end": v(-2.91, -30.56) * mm});
            skLineSegment(sketch, "E4955", {"start": v(-2.91, -30.56) * mm, "end": v(-2.87, -30.58) * mm});
            skLineSegment(sketch, "E4956", {"start": v(-2.87, -30.58) * mm, "end": v(-2.75, -30.59) * mm});
            skLineSegment(sketch, "E4957", {"start": v(-2.75, -30.59) * mm, "end": v(-2.7, -30.58) * mm});
            skLineSegment(sketch, "E4958", {"start": v(-2.7, -30.58) * mm, "end": v(-2.68, -30.54) * mm});
            skLineSegment(sketch, "E4959", {"start": v(-2.68, -30.54) * mm, "end": v(-2.67, -30.5) * mm});
            skLineSegment(sketch, "E4960", {"start": v(-2.67, -30.5) * mm, "end": v(-2.65, -30.46) * mm});
            skLineSegment(sketch, "E4961", {"start": v(-2.65, -30.46) * mm, "end": v(-2.63, -30.42) * mm});
            skLineSegment(sketch, "E4962", {"start": v(-2.63, -30.42) * mm, "end": v(-2.6, -30.38) * mm});
            skLineSegment(sketch, "E4963", {"start": v(-2.6, -30.38) * mm, "end": v(-2.55, -30.34) * mm});
            skLineSegment(sketch, "E4964", {"start": v(-2.55, -30.34) * mm, "end": v(-2.5, -30.32) * mm});
            skLineSegment(sketch, "E4965", {"start": v(-2.5, -30.32) * mm, "end": v(-2.44, -30.3) * mm});
            skLineSegment(sketch, "E4966", {"start": v(-2.44, -30.3) * mm, "end": v(-2.39, -30.3) * mm});
            skLineSegment(sketch, "E4967", {"start": v(-2.39, -30.3) * mm, "end": v(-2.33, -30.32) * mm});
            skLineSegment(sketch, "E4968", {"start": v(-2.33, -30.32) * mm, "end": v(-2.27, -30.34) * mm});
            skLineSegment(sketch, "E4969", {"start": v(-2.27, -30.34) * mm, "end": v(-2.23, -30.37) * mm});
            skLineSegment(sketch, "E4970", {"start": v(-2.23, -30.37) * mm, "end": v(-2.19, -30.41) * mm});
            skLineSegment(sketch, "E4971", {"start": v(-2.19, -30.41) * mm, "end": v(-2.17, -30.45) * mm});
            skLineSegment(sketch, "E4972", {"start": v(-2.17, -30.45) * mm, "end": v(-2.15, -30.5) * mm});
            skLineSegment(sketch, "E4973", {"start": v(-2.15, -30.5) * mm, "end": v(-2.14, -30.54) * mm});
            skLineSegment(sketch, "E4974", {"start": v(-2.14, -30.54) * mm, "end": v(-2.13, -30.58) * mm});
            skLineSegment(sketch, "E4975", {"start": v(-2.13, -30.58) * mm, "end": v(-2.11, -30.62) * mm});
            skLineSegment(sketch, "E4976", {"start": v(-2.11, -30.62) * mm, "end": v(-2.07, -30.64) * mm});
            skLineSegment(sketch, "E4977", {"start": v(-2.07, -30.64) * mm, "end": v(-1.95, -30.65) * mm});
            skLineSegment(sketch, "E4978", {"start": v(-1.95, -30.65) * mm, "end": v(-1.9, -30.64) * mm});
            skLineSegment(sketch, "E4979", {"start": v(-1.9, -30.64) * mm, "end": v(-1.88, -30.6) * mm});
            skLineSegment(sketch, "E4980", {"start": v(-1.88, -30.6) * mm, "end": v(-1.87, -30.56) * mm});
            skLineSegment(sketch, "E4981", {"start": v(-1.87, -30.56) * mm, "end": v(-1.85, -30.52) * mm});
            skLineSegment(sketch, "E4982", {"start": v(-1.85, -30.52) * mm, "end": v(-1.83, -30.48) * mm});
            skLineSegment(sketch, "E4983", {"start": v(-1.83, -30.48) * mm, "end": v(-1.8, -30.44) * mm});
            skLineSegment(sketch, "E4984", {"start": v(-1.8, -30.44) * mm, "end": v(-1.76, -30.4) * mm});
            skLineSegment(sketch, "E4985", {"start": v(-1.76, -30.4) * mm, "end": v(-1.7, -30.38) * mm});
            skLineSegment(sketch, "E4986", {"start": v(-1.7, -30.38) * mm, "end": v(-1.65, -30.36) * mm});
            skLineSegment(sketch, "E4987", {"start": v(-1.65, -30.36) * mm, "end": v(-1.6, -30.36) * mm});
            skLineSegment(sketch, "E4988", {"start": v(-1.6, -30.36) * mm, "end": v(-1.53, -30.37) * mm});
            skLineSegment(sketch, "E4989", {"start": v(-1.53, -30.37) * mm, "end": v(-1.48, -30.39) * mm});
            skLineSegment(sketch, "E4990", {"start": v(-1.48, -30.39) * mm, "end": v(-1.43, -30.42) * mm});
            skLineSegment(sketch, "E4991", {"start": v(-1.43, -30.42) * mm, "end": v(-1.39, -30.46) * mm});
            skLineSegment(sketch, "E4992", {"start": v(-1.39, -30.46) * mm, "end": v(-1.37, -30.5) * mm});
            skLineSegment(sketch, "E4993", {"start": v(-1.37, -30.5) * mm, "end": v(-1.35, -30.54) * mm});
            skLineSegment(sketch, "E4994", {"start": v(-1.35, -30.54) * mm, "end": v(-1.34, -30.58) * mm});
            skLineSegment(sketch, "E4995", {"start": v(-1.34, -30.58) * mm, "end": v(-1.33, -30.63) * mm});
            skLineSegment(sketch, "E4996", {"start": v(-1.33, -30.63) * mm, "end": v(-1.31, -30.67) * mm});
            skLineSegment(sketch, "E4997", {"start": v(-1.31, -30.67) * mm, "end": v(-1.27, -30.68) * mm});
            skLineSegment(sketch, "E4998", {"start": v(-1.27, -30.68) * mm, "end": v(-1.15, -30.69) * mm});
            skLineSegment(sketch, "E4999", {"start": v(-1.15, -30.69) * mm, "end": v(-1.1, -30.68) * mm});
            skLineSegment(sketch, "E5000", {"start": v(-1.1, -30.68) * mm, "end": v(-1.08, -30.64) * mm});
            skLineSegment(sketch, "E5001", {"start": v(-1.08, -30.64) * mm, "end": v(-1.07, -30.6) * mm});
            skLineSegment(sketch, "E5002", {"start": v(-1.07, -30.6) * mm, "end": v(-1.05, -30.55) * mm});
            skLineSegment(sketch, "E5003", {"start": v(-1.05, -30.55) * mm, "end": v(-1.03, -30.51) * mm});
            skLineSegment(sketch, "E5004", {"start": v(-1.03, -30.51) * mm, "end": v(-1, -30.48) * mm});
            skLineSegment(sketch, "E5005", {"start": v(-1, -30.48) * mm, "end": v(-0.96, -30.44) * mm});
            skLineSegment(sketch, "E5006", {"start": v(-0.96, -30.44) * mm, "end": v(-0.9, -30.4) * mm});
            skLineSegment(sketch, "E5007", {"start": v(-0.9, -30.4) * mm, "end": v(-0.85, -30.4) * mm});
            skLineSegment(sketch, "E5008", {"start": v(-0.85, -30.4) * mm, "end": v(-0.8, -30.39) * mm});
            skLineSegment(sketch, "E5009", {"start": v(-0.8, -30.39) * mm, "end": v(-0.74, -30.4) * mm});
            skLineSegment(sketch, "E5010", {"start": v(-0.74, -30.4) * mm, "end": v(-0.68, -30.42) * mm});
            skLineSegment(sketch, "E5011", {"start": v(-0.68, -30.42) * mm, "end": v(-0.63, -30.45) * mm});
            skLineSegment(sketch, "E5012", {"start": v(-0.63, -30.45) * mm, "end": v(-0.6, -30.49) * mm});
            skLineSegment(sketch, "E5013", {"start": v(-0.6, -30.49) * mm, "end": v(-0.57, -30.53) * mm});
            skLineSegment(sketch, "E5014", {"start": v(-0.57, -30.53) * mm, "end": v(-0.55, -30.57) * mm});
            skLineSegment(sketch, "E5015", {"start": v(-0.55, -30.57) * mm, "end": v(-0.54, -30.6) * mm});
            skLineSegment(sketch, "E5016", {"start": v(-0.54, -30.6) * mm, "end": v(-0.53, -30.65) * mm});
            skLineSegment(sketch, "E5017", {"start": v(-0.53, -30.65) * mm, "end": v(-0.5, -30.7) * mm});
            skLineSegment(sketch, "E5018", {"start": v(-0.5, -30.7) * mm, "end": v(-0.46, -30.7) * mm});
            skLineSegment(sketch, "E5019", {"start": v(-0.46, -30.7) * mm, "end": v(-0.34, -30.7) * mm});
            skLineSegment(sketch, "E5020", {"start": v(-0.34, -30.7) * mm, "end": v(-0.3, -30.7) * mm});
            skLineSegment(sketch, "E5021", {"start": v(-0.3, -30.7) * mm, "end": v(-0.27, -30.66) * mm});
            skLineSegment(sketch, "E5022", {"start": v(-0.27, -30.66) * mm, "end": v(-0.26, -30.61) * mm});
            skLineSegment(sketch, "E5023", {"start": v(-0.26, -30.61) * mm, "end": v(-0.25, -30.57) * mm});
            skLineSegment(sketch, "E5024", {"start": v(-0.25, -30.57) * mm, "end": v(-0.23, -30.53) * mm});
            skLineSegment(sketch, "E5025", {"start": v(-0.23, -30.53) * mm, "end": v(-0.2, -30.5) * mm});
            skLineSegment(sketch, "E5026", {"start": v(-0.2, -30.5) * mm, "end": v(-0.16, -30.45) * mm});
            skLineSegment(sketch, "E5027", {"start": v(-0.16, -30.45) * mm, "end": v(-0.11, -30.42) * mm});
            skLineSegment(sketch, "E5028", {"start": v(-0.11, -30.42) * mm, "end": v(-0.06, -30.4) * mm});
            skLineSegment(sketch, "E5029", {"start": v(-0.06, -30.4) * mm, "end": v(0, -30.4) * mm});
            skLineSegment(sketch, "E5030", {"start": v(0, -30.4) * mm, "end": v(0.06, -30.4) * mm});
            skLineSegment(sketch, "E5031", {"start": v(0.06, -30.4) * mm, "end": v(0.11, -30.42) * mm});
            skLineSegment(sketch, "E5032", {"start": v(0.11, -30.42) * mm, "end": v(0.16, -30.45) * mm});
            skLineSegment(sketch, "E5033", {"start": v(0.16, -30.45) * mm, "end": v(0.2, -30.5) * mm});
            skLineSegment(sketch, "E5034", {"start": v(0.2, -30.5) * mm, "end": v(0.23, -30.53) * mm});
            skLineSegment(sketch, "E5035", {"start": v(0.23, -30.53) * mm, "end": v(0.25, -30.57) * mm});
            skLineSegment(sketch, "E5036", {"start": v(0.25, -30.57) * mm, "end": v(0.26, -30.61) * mm});
            skLineSegment(sketch, "E5037", {"start": v(0.26, -30.61) * mm, "end": v(0.27, -30.66) * mm});
            skLineSegment(sketch, "E5038", {"start": v(0.27, -30.66) * mm, "end": v(0.3, -30.7) * mm});
            skLineSegment(sketch, "E5039", {"start": v(0.3, -30.7) * mm, "end": v(0.34, -30.7) * mm});
            skLineSegment(sketch, "E5040", {"start": v(-0.32, -1) * mm, "end": v(-0.62, -0.85) * mm});
            skLineSegment(sketch, "E5041", {"start": v(-0.62, -0.85) * mm, "end": v(-0.85, -0.62) * mm});
            skLineSegment(sketch, "E5042", {"start": v(-0.85, -0.62) * mm, "end": v(-1, -0.32) * mm});
            skLineSegment(sketch, "E5043", {"start": v(-1, -0.32) * mm, "end": v(-1.05, 0) * mm});
            skLineSegment(sketch, "E5044", {"start": v(-1.05, 0) * mm, "end": v(-1, 0.32) * mm});
            skLineSegment(sketch, "E5045", {"start": v(-1, 0.32) * mm, "end": v(-0.85, 0.62) * mm});
            skLineSegment(sketch, "E5046", {"start": v(-0.85, 0.62) * mm, "end": v(-0.62, 0.85) * mm});
            skLineSegment(sketch, "E5047", {"start": v(-0.62, 0.85) * mm, "end": v(-0.32, 1) * mm});
            skLineSegment(sketch, "E5048", {"start": v(-0.32, 1) * mm, "end": v(0, 1.05) * mm});
            skLineSegment(sketch, "E5049", {"start": v(0, 1.05) * mm, "end": v(0.32, 1) * mm});
            skLineSegment(sketch, "E5050", {"start": v(0.32, 1) * mm, "end": v(0.62, 0.85) * mm});
            skLineSegment(sketch, "E5051", {"start": v(0.62, 0.85) * mm, "end": v(0.85, 0.62) * mm});
            skLineSegment(sketch, "E5052", {"start": v(0.85, 0.62) * mm, "end": v(1, 0.32) * mm});
            skLineSegment(sketch, "E5053", {"start": v(1, 0.32) * mm, "end": v(1.05, 0) * mm});
            skLineSegment(sketch, "E5054", {"start": v(1.05, 0) * mm, "end": v(1, -0.32) * mm});
            skLineSegment(sketch, "E5055", {"start": v(1, -0.32) * mm, "end": v(0.85, -0.62) * mm});
            skLineSegment(sketch, "E5056", {"start": v(0.85, -0.62) * mm, "end": v(0.62, -0.85) * mm});
            skLineSegment(sketch, "E5057", {"start": v(0.62, -0.85) * mm, "end": v(0.32, -1) * mm});
            skLineSegment(sketch, "E5058", {"start": v(0.32, -1) * mm, "end": v(0, -1.05) * mm});
            skLineSegment(sketch, "E5059", {"start": v(0, -1.05) * mm, "end": v(-0.32, -1) * mm});
            skCircle(sketch, "E5060", {"center": v(0, 0) * mm, "radius": 3.18 * mm});
            skSolve(sketch);
        }
        {
            var Q0;
            Q0=makeQuery(id+"F0.imprint","IMPRINT",FACE,{"disambiguationData":[TD([[makeQuery(id+"F0.imprint","IMPRINT",EDGE,{"derivedFrom":sQuery(id+"F0.wireOp",EDGE,"E0")}),1.0]])]});
            extrude(context, id + "F1", {"entities" : qUnion([Q0]), "depth" : 5 * mm, "offsetDistance" : 25 * mm});
        }
    });
